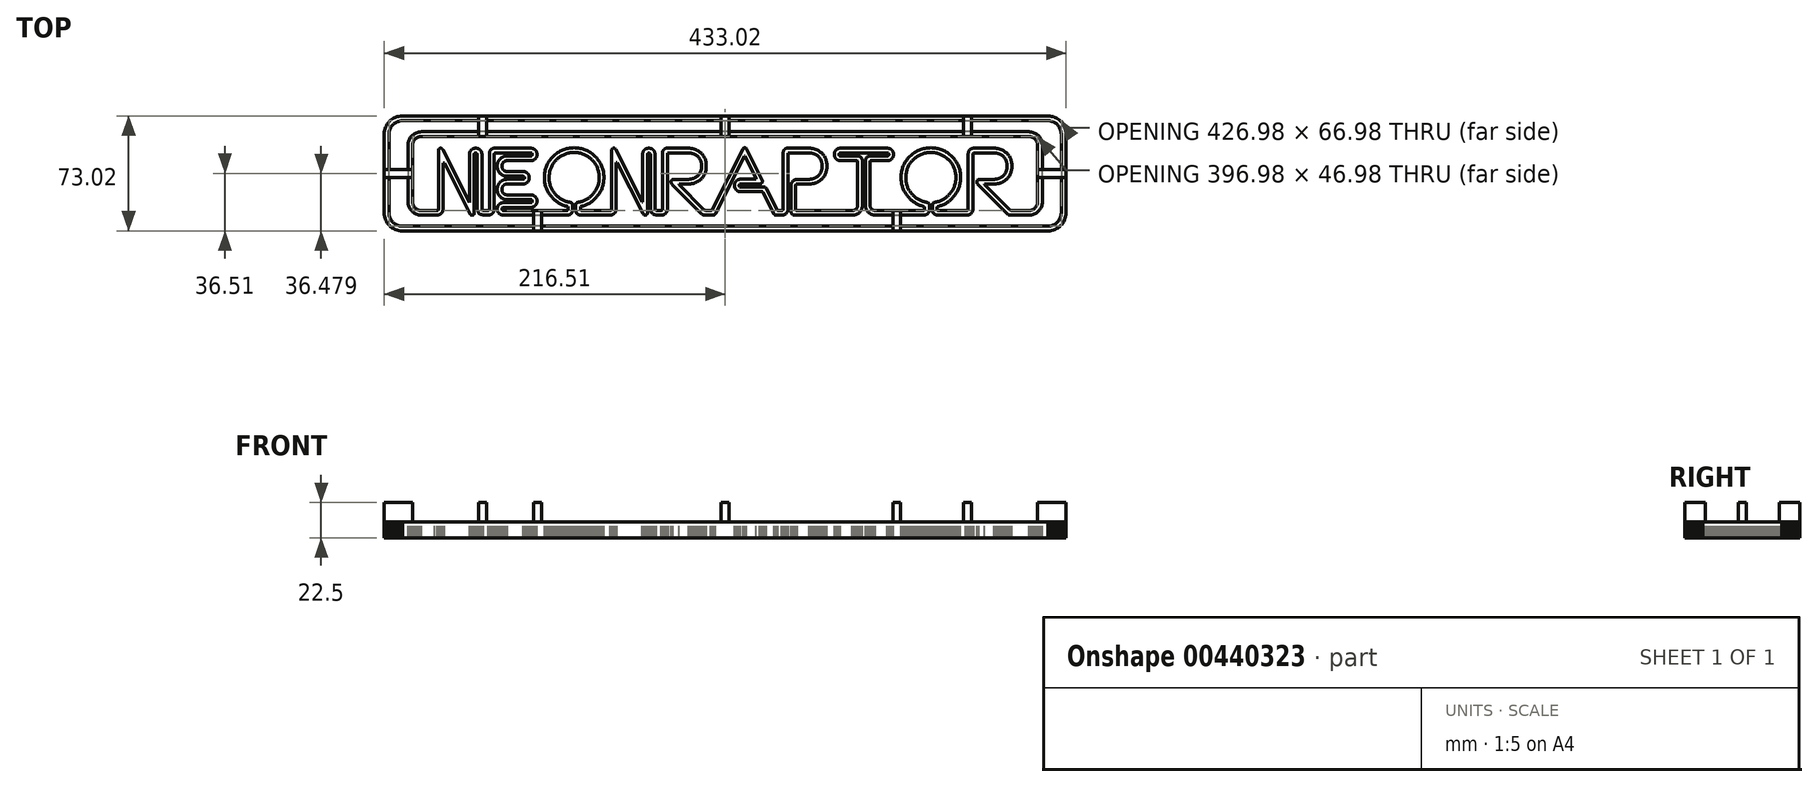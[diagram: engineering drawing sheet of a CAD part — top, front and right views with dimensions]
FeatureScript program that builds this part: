
annotation { "Feature Type Name" : "Feature", "Feature Type Description" : "" }
export const myFeature = defineFeature(function(context is Context, id is Id, definition is map)
    precondition{}
    {
        {
            var Q0;
            Q0=qCreatedBy(makeId("Top.planeOp"),FACE);
            var Q1;
            Q1=qCreatedBy(makeId("Top.planeOp"),FACE);
            var sketch = newSketch(context, id + "F0", { "sketchPlane" : qUnion([Q0, Q1])});
            skLineSegment(sketch, "E0", {"start": v(205, 36.51) * mm, "end": v(-205, 36.51) * mm});
            skLineSegment(sketch, "E1", {"start": v(-205, 36.51) * mm, "end": v(-206.18, 36.45) * mm});
            skLineSegment(sketch, "E2", {"start": v(-206.18, 36.45) * mm, "end": v(-207.32, 36.28) * mm});
            skLineSegment(sketch, "E3", {"start": v(-207.32, 36.28) * mm, "end": v(-208.42, 36) * mm});
            skLineSegment(sketch, "E4", {"start": v(-208.42, 36) * mm, "end": v(-209.48, 35.6) * mm});
            skLineSegment(sketch, "E5", {"start": v(-209.48, 35.6) * mm, "end": v(-210.48, 35.12) * mm});
            skLineSegment(sketch, "E6", {"start": v(-210.48, 35.12) * mm, "end": v(-211.43, 34.54) * mm});
            skLineSegment(sketch, "E7", {"start": v(-211.43, 34.54) * mm, "end": v(-212.32, 33.88) * mm});
            skLineSegment(sketch, "E8", {"start": v(-212.32, 33.88) * mm, "end": v(-213.14, 33.14) * mm});
            skLineSegment(sketch, "E9", {"start": v(-213.14, 33.14) * mm, "end": v(-213.88, 32.32) * mm});
            skLineSegment(sketch, "E10", {"start": v(-213.88, 32.32) * mm, "end": v(-214.54, 31.43) * mm});
            skLineSegment(sketch, "E11", {"start": v(-214.54, 31.43) * mm, "end": v(-215.12, 30.48) * mm});
            skLineSegment(sketch, "E12", {"start": v(-215.12, 30.48) * mm, "end": v(-215.6, 29.48) * mm});
            skLineSegment(sketch, "E13", {"start": v(-215.6, 29.48) * mm, "end": v(-216, 28.42) * mm});
            skLineSegment(sketch, "E14", {"start": v(-216, 28.42) * mm, "end": v(-216.28, 27.32) * mm});
            skLineSegment(sketch, "E15", {"start": v(-216.28, 27.32) * mm, "end": v(-216.45, 26.18) * mm});
            skLineSegment(sketch, "E16", {"start": v(-216.45, 26.18) * mm, "end": v(-216.51, 25) * mm});
            skLineSegment(sketch, "E17", {"start": v(-216.51, 25) * mm, "end": v(-216.51, -25) * mm});
            skLineSegment(sketch, "E18", {"start": v(-216.51, -25) * mm, "end": v(-216.45, -26.18) * mm});
            skLineSegment(sketch, "E19", {"start": v(-216.45, -26.18) * mm, "end": v(-216.28, -27.32) * mm});
            skLineSegment(sketch, "E20", {"start": v(-216.28, -27.32) * mm, "end": v(-216, -28.42) * mm});
            skLineSegment(sketch, "E21", {"start": v(-216, -28.42) * mm, "end": v(-215.6, -29.48) * mm});
            skLineSegment(sketch, "E22", {"start": v(-215.6, -29.48) * mm, "end": v(-215.12, -30.48) * mm});
            skLineSegment(sketch, "E23", {"start": v(-215.12, -30.48) * mm, "end": v(-214.54, -31.43) * mm});
            skLineSegment(sketch, "E24", {"start": v(-214.54, -31.43) * mm, "end": v(-213.88, -32.32) * mm});
            skLineSegment(sketch, "E25", {"start": v(-213.88, -32.32) * mm, "end": v(-213.14, -33.14) * mm});
            skLineSegment(sketch, "E26", {"start": v(-213.14, -33.14) * mm, "end": v(-212.32, -33.88) * mm});
            skLineSegment(sketch, "E27", {"start": v(-212.32, -33.88) * mm, "end": v(-211.43, -34.54) * mm});
            skLineSegment(sketch, "E28", {"start": v(-211.43, -34.54) * mm, "end": v(-210.48, -35.12) * mm});
            skLineSegment(sketch, "E29", {"start": v(-210.48, -35.12) * mm, "end": v(-209.48, -35.6) * mm});
            skLineSegment(sketch, "E30", {"start": v(-209.48, -35.6) * mm, "end": v(-208.42, -36) * mm});
            skLineSegment(sketch, "E31", {"start": v(-208.42, -36) * mm, "end": v(-207.32, -36.28) * mm});
            skLineSegment(sketch, "E32", {"start": v(-207.32, -36.28) * mm, "end": v(-206.18, -36.45) * mm});
            skLineSegment(sketch, "E33", {"start": v(-206.18, -36.45) * mm, "end": v(-205, -36.51) * mm});
            skLineSegment(sketch, "E34", {"start": v(-205, -36.51) * mm, "end": v(205, -36.51) * mm});
            skLineSegment(sketch, "E35", {"start": v(205, -36.51) * mm, "end": v(206.18, -36.45) * mm});
            skLineSegment(sketch, "E36", {"start": v(206.18, -36.45) * mm, "end": v(207.32, -36.28) * mm});
            skLineSegment(sketch, "E37", {"start": v(207.32, -36.28) * mm, "end": v(208.42, -36) * mm});
            skLineSegment(sketch, "E38", {"start": v(208.42, -36) * mm, "end": v(209.48, -35.6) * mm});
            skLineSegment(sketch, "E39", {"start": v(209.48, -35.6) * mm, "end": v(210.48, -35.12) * mm});
            skLineSegment(sketch, "E40", {"start": v(210.48, -35.12) * mm, "end": v(211.43, -34.54) * mm});
            skLineSegment(sketch, "E41", {"start": v(211.43, -34.54) * mm, "end": v(212.32, -33.88) * mm});
            skLineSegment(sketch, "E42", {"start": v(212.32, -33.88) * mm, "end": v(213.14, -33.14) * mm});
            skLineSegment(sketch, "E43", {"start": v(213.14, -33.14) * mm, "end": v(213.88, -32.32) * mm});
            skLineSegment(sketch, "E44", {"start": v(213.88, -32.32) * mm, "end": v(214.54, -31.43) * mm});
            skLineSegment(sketch, "E45", {"start": v(214.54, -31.43) * mm, "end": v(215.12, -30.48) * mm});
            skLineSegment(sketch, "E46", {"start": v(215.12, -30.48) * mm, "end": v(215.6, -29.48) * mm});
            skLineSegment(sketch, "E47", {"start": v(215.6, -29.48) * mm, "end": v(216, -28.42) * mm});
            skLineSegment(sketch, "E48", {"start": v(216, -28.42) * mm, "end": v(216.28, -27.32) * mm});
            skLineSegment(sketch, "E49", {"start": v(216.28, -27.32) * mm, "end": v(216.45, -26.18) * mm});
            skLineSegment(sketch, "E50", {"start": v(216.45, -26.18) * mm, "end": v(216.51, -25) * mm});
            skLineSegment(sketch, "E51", {"start": v(216.51, -25) * mm, "end": v(216.51, 25) * mm});
            skLineSegment(sketch, "E52", {"start": v(216.51, 25) * mm, "end": v(216.45, 26.18) * mm});
            skLineSegment(sketch, "E53", {"start": v(216.45, 26.18) * mm, "end": v(216.28, 27.32) * mm});
            skLineSegment(sketch, "E54", {"start": v(216.28, 27.32) * mm, "end": v(216, 28.42) * mm});
            skLineSegment(sketch, "E55", {"start": v(216, 28.42) * mm, "end": v(215.6, 29.48) * mm});
            skLineSegment(sketch, "E56", {"start": v(215.6, 29.48) * mm, "end": v(215.12, 30.48) * mm});
            skLineSegment(sketch, "E57", {"start": v(215.12, 30.48) * mm, "end": v(214.54, 31.43) * mm});
            skLineSegment(sketch, "E58", {"start": v(214.54, 31.43) * mm, "end": v(213.88, 32.32) * mm});
            skLineSegment(sketch, "E59", {"start": v(213.88, 32.32) * mm, "end": v(213.14, 33.14) * mm});
            skLineSegment(sketch, "E60", {"start": v(213.14, 33.14) * mm, "end": v(212.32, 33.88) * mm});
            skLineSegment(sketch, "E61", {"start": v(212.32, 33.88) * mm, "end": v(211.43, 34.54) * mm});
            skLineSegment(sketch, "E62", {"start": v(211.43, 34.54) * mm, "end": v(210.48, 35.12) * mm});
            skLineSegment(sketch, "E63", {"start": v(210.48, 35.12) * mm, "end": v(209.48, 35.6) * mm});
            skLineSegment(sketch, "E64", {"start": v(209.48, 35.6) * mm, "end": v(208.42, 36) * mm});
            skLineSegment(sketch, "E65", {"start": v(208.42, 36) * mm, "end": v(207.32, 36.28) * mm});
            skLineSegment(sketch, "E66", {"start": v(207.32, 36.28) * mm, "end": v(206.18, 36.45) * mm});
            skLineSegment(sketch, "E67", {"start": v(206.18, 36.45) * mm, "end": v(205, 36.51) * mm});
            skLineSegment(sketch, "E68", {"start": v(213.49, -25) * mm, "end": v(213.45, -25.87) * mm});
            skLineSegment(sketch, "E69", {"start": v(213.45, -25.87) * mm, "end": v(213.32, -26.7) * mm});
            skLineSegment(sketch, "E70", {"start": v(213.32, -26.7) * mm, "end": v(213.1, -27.52) * mm});
            skLineSegment(sketch, "E71", {"start": v(213.1, -27.52) * mm, "end": v(212.82, -28.3) * mm});
            skLineSegment(sketch, "E72", {"start": v(212.82, -28.3) * mm, "end": v(212.46, -29.04) * mm});
            skLineSegment(sketch, "E73", {"start": v(212.46, -29.04) * mm, "end": v(212.04, -29.74) * mm});
            skLineSegment(sketch, "E74", {"start": v(212.04, -29.74) * mm, "end": v(211.55, -30.4) * mm});
            skLineSegment(sketch, "E75", {"start": v(211.55, -30.4) * mm, "end": v(211, -31) * mm});
            skLineSegment(sketch, "E76", {"start": v(211, -31) * mm, "end": v(210.4, -31.55) * mm});
            skLineSegment(sketch, "E77", {"start": v(210.4, -31.55) * mm, "end": v(209.74, -32.04) * mm});
            skLineSegment(sketch, "E78", {"start": v(209.74, -32.04) * mm, "end": v(209.04, -32.46) * mm});
            skLineSegment(sketch, "E79", {"start": v(209.04, -32.46) * mm, "end": v(208.3, -32.82) * mm});
            skLineSegment(sketch, "E80", {"start": v(208.3, -32.82) * mm, "end": v(207.52, -33.1) * mm});
            skLineSegment(sketch, "E81", {"start": v(207.52, -33.1) * mm, "end": v(206.7, -33.32) * mm});
            skLineSegment(sketch, "E82", {"start": v(206.7, -33.32) * mm, "end": v(205.87, -33.45) * mm});
            skLineSegment(sketch, "E83", {"start": v(205.87, -33.45) * mm, "end": v(205, -33.49) * mm});
            skLineSegment(sketch, "E84", {"start": v(205, -33.49) * mm, "end": v(-205, -33.49) * mm});
            skLineSegment(sketch, "E85", {"start": v(-205, -33.49) * mm, "end": v(-205.87, -33.45) * mm});
            skLineSegment(sketch, "E86", {"start": v(-205.87, -33.45) * mm, "end": v(-206.7, -33.32) * mm});
            skLineSegment(sketch, "E87", {"start": v(-206.7, -33.32) * mm, "end": v(-207.52, -33.1) * mm});
            skLineSegment(sketch, "E88", {"start": v(-207.52, -33.1) * mm, "end": v(-208.3, -32.82) * mm});
            skLineSegment(sketch, "E89", {"start": v(-208.3, -32.82) * mm, "end": v(-209.04, -32.46) * mm});
            skLineSegment(sketch, "E90", {"start": v(-209.04, -32.46) * mm, "end": v(-209.74, -32.04) * mm});
            skLineSegment(sketch, "E91", {"start": v(-209.74, -32.04) * mm, "end": v(-210.4, -31.55) * mm});
            skLineSegment(sketch, "E92", {"start": v(-210.4, -31.55) * mm, "end": v(-211, -31) * mm});
            skLineSegment(sketch, "E93", {"start": v(-211, -31) * mm, "end": v(-211.55, -30.4) * mm});
            skLineSegment(sketch, "E94", {"start": v(-211.55, -30.4) * mm, "end": v(-212.04, -29.74) * mm});
            skLineSegment(sketch, "E95", {"start": v(-212.04, -29.74) * mm, "end": v(-212.46, -29.04) * mm});
            skLineSegment(sketch, "E96", {"start": v(-212.46, -29.04) * mm, "end": v(-212.82, -28.3) * mm});
            skLineSegment(sketch, "E97", {"start": v(-212.82, -28.3) * mm, "end": v(-213.1, -27.52) * mm});
            skLineSegment(sketch, "E98", {"start": v(-213.1, -27.52) * mm, "end": v(-213.32, -26.7) * mm});
            skLineSegment(sketch, "E99", {"start": v(-213.32, -26.7) * mm, "end": v(-213.44, -25.87) * mm});
            skLineSegment(sketch, "E100", {"start": v(-213.44, -25.87) * mm, "end": v(-213.49, -25) * mm});
            skLineSegment(sketch, "E101", {"start": v(-213.49, -25) * mm, "end": v(-213.49, 25) * mm});
            skLineSegment(sketch, "E102", {"start": v(-213.49, 25) * mm, "end": v(-213.44, 25.87) * mm});
            skLineSegment(sketch, "E103", {"start": v(-213.44, 25.87) * mm, "end": v(-213.32, 26.7) * mm});
            skLineSegment(sketch, "E104", {"start": v(-213.32, 26.7) * mm, "end": v(-213.1, 27.52) * mm});
            skLineSegment(sketch, "E105", {"start": v(-213.1, 27.52) * mm, "end": v(-212.82, 28.3) * mm});
            skLineSegment(sketch, "E106", {"start": v(-212.82, 28.3) * mm, "end": v(-212.46, 29.04) * mm});
            skLineSegment(sketch, "E107", {"start": v(-212.46, 29.04) * mm, "end": v(-212.04, 29.74) * mm});
            skLineSegment(sketch, "E108", {"start": v(-212.04, 29.74) * mm, "end": v(-211.55, 30.4) * mm});
            skLineSegment(sketch, "E109", {"start": v(-211.55, 30.4) * mm, "end": v(-211, 31) * mm});
            skLineSegment(sketch, "E110", {"start": v(-211, 31) * mm, "end": v(-210.4, 31.55) * mm});
            skLineSegment(sketch, "E111", {"start": v(-210.4, 31.55) * mm, "end": v(-209.74, 32.04) * mm});
            skLineSegment(sketch, "E112", {"start": v(-209.74, 32.04) * mm, "end": v(-209.04, 32.46) * mm});
            skLineSegment(sketch, "E113", {"start": v(-209.04, 32.46) * mm, "end": v(-208.3, 32.82) * mm});
            skLineSegment(sketch, "E114", {"start": v(-208.3, 32.82) * mm, "end": v(-207.52, 33.1) * mm});
            skLineSegment(sketch, "E115", {"start": v(-207.52, 33.1) * mm, "end": v(-206.7, 33.32) * mm});
            skLineSegment(sketch, "E116", {"start": v(-206.7, 33.32) * mm, "end": v(-205.87, 33.44) * mm});
            skLineSegment(sketch, "E117", {"start": v(-205.87, 33.44) * mm, "end": v(-205, 33.49) * mm});
            skLineSegment(sketch, "E118", {"start": v(-205, 33.49) * mm, "end": v(205, 33.49) * mm});
            skLineSegment(sketch, "E119", {"start": v(205, 33.49) * mm, "end": v(205.87, 33.44) * mm});
            skLineSegment(sketch, "E120", {"start": v(205.87, 33.44) * mm, "end": v(206.7, 33.32) * mm});
            skLineSegment(sketch, "E121", {"start": v(206.7, 33.32) * mm, "end": v(207.52, 33.1) * mm});
            skLineSegment(sketch, "E122", {"start": v(207.52, 33.1) * mm, "end": v(208.3, 32.82) * mm});
            skLineSegment(sketch, "E123", {"start": v(208.3, 32.82) * mm, "end": v(209.04, 32.46) * mm});
            skLineSegment(sketch, "E124", {"start": v(209.04, 32.46) * mm, "end": v(209.74, 32.04) * mm});
            skLineSegment(sketch, "E125", {"start": v(209.74, 32.04) * mm, "end": v(210.4, 31.55) * mm});
            skLineSegment(sketch, "E126", {"start": v(210.4, 31.55) * mm, "end": v(211, 31) * mm});
            skLineSegment(sketch, "E127", {"start": v(211, 31) * mm, "end": v(211.55, 30.4) * mm});
            skLineSegment(sketch, "E128", {"start": v(211.55, 30.4) * mm, "end": v(212.04, 29.74) * mm});
            skLineSegment(sketch, "E129", {"start": v(212.04, 29.74) * mm, "end": v(212.46, 29.04) * mm});
            skLineSegment(sketch, "E130", {"start": v(212.46, 29.04) * mm, "end": v(212.82, 28.3) * mm});
            skLineSegment(sketch, "E131", {"start": v(212.82, 28.3) * mm, "end": v(213.1, 27.52) * mm});
            skLineSegment(sketch, "E132", {"start": v(213.1, 27.52) * mm, "end": v(213.32, 26.7) * mm});
            skLineSegment(sketch, "E133", {"start": v(213.32, 26.7) * mm, "end": v(213.45, 25.87) * mm});
            skLineSegment(sketch, "E134", {"start": v(213.45, 25.87) * mm, "end": v(213.49, 25) * mm});
            skLineSegment(sketch, "E135", {"start": v(213.49, 25) * mm, "end": v(213.49, -25) * mm});
            skLineSegment(sketch, "E136", {"start": v(192.86, 26.48) * mm, "end": v(-192.86, 26.48) * mm});
            skLineSegment(sketch, "E137", {"start": v(-192.86, 26.48) * mm, "end": v(-193.74, 26.44) * mm});
            skLineSegment(sketch, "E138", {"start": v(-193.74, 26.44) * mm, "end": v(-194.6, 26.3) * mm});
            skLineSegment(sketch, "E139", {"start": v(-194.6, 26.3) * mm, "end": v(-195.43, 26.1) * mm});
            skLineSegment(sketch, "E140", {"start": v(-195.43, 26.1) * mm, "end": v(-196.22, 25.8) * mm});
            skLineSegment(sketch, "E141", {"start": v(-196.22, 25.8) * mm, "end": v(-196.98, 25.43) * mm});
            skLineSegment(sketch, "E142", {"start": v(-196.98, 25.43) * mm, "end": v(-197.7, 25) * mm});
            skLineSegment(sketch, "E143", {"start": v(-197.7, 25) * mm, "end": v(-198.36, 24.5) * mm});
            skLineSegment(sketch, "E144", {"start": v(-198.36, 24.5) * mm, "end": v(-198.97, 23.94) * mm});
            skLineSegment(sketch, "E145", {"start": v(-198.97, 23.94) * mm, "end": v(-199.53, 23.33) * mm});
            skLineSegment(sketch, "E146", {"start": v(-199.53, 23.33) * mm, "end": v(-200.03, 22.66) * mm});
            skLineSegment(sketch, "E147", {"start": v(-200.03, 22.66) * mm, "end": v(-200.46, 21.95) * mm});
            skLineSegment(sketch, "E148", {"start": v(-200.46, 21.95) * mm, "end": v(-200.83, 21.2) * mm});
            skLineSegment(sketch, "E149", {"start": v(-200.83, 21.2) * mm, "end": v(-201.12, 20.4) * mm});
            skLineSegment(sketch, "E150", {"start": v(-201.12, 20.4) * mm, "end": v(-201.33, 19.57) * mm});
            skLineSegment(sketch, "E151", {"start": v(-201.33, 19.57) * mm, "end": v(-201.47, 18.7) * mm});
            skLineSegment(sketch, "E152", {"start": v(-201.47, 18.7) * mm, "end": v(-201.51, 17.82) * mm});
            skLineSegment(sketch, "E153", {"start": v(-201.51, 17.82) * mm, "end": v(-201.51, -17.89) * mm});
            skLineSegment(sketch, "E154", {"start": v(-201.51, -17.89) * mm, "end": v(-201.47, -18.77) * mm});
            skLineSegment(sketch, "E155", {"start": v(-201.47, -18.77) * mm, "end": v(-201.33, -19.63) * mm});
            skLineSegment(sketch, "E156", {"start": v(-201.33, -19.63) * mm, "end": v(-201.12, -20.46) * mm});
            skLineSegment(sketch, "E157", {"start": v(-201.12, -20.46) * mm, "end": v(-200.83, -21.25) * mm});
            skLineSegment(sketch, "E158", {"start": v(-200.83, -21.25) * mm, "end": v(-200.46, -22) * mm});
            skLineSegment(sketch, "E159", {"start": v(-200.46, -22) * mm, "end": v(-200.03, -22.72) * mm});
            skLineSegment(sketch, "E160", {"start": v(-200.03, -22.72) * mm, "end": v(-199.53, -23.39) * mm});
            skLineSegment(sketch, "E161", {"start": v(-199.53, -23.39) * mm, "end": v(-198.97, -24) * mm});
            skLineSegment(sketch, "E162", {"start": v(-198.97, -24) * mm, "end": v(-198.36, -24.56) * mm});
            skLineSegment(sketch, "E163", {"start": v(-198.36, -24.56) * mm, "end": v(-197.7, -25.06) * mm});
            skLineSegment(sketch, "E164", {"start": v(-197.7, -25.06) * mm, "end": v(-196.98, -25.5) * mm});
            skLineSegment(sketch, "E165", {"start": v(-196.98, -25.5) * mm, "end": v(-196.22, -25.86) * mm});
            skLineSegment(sketch, "E166", {"start": v(-196.22, -25.86) * mm, "end": v(-195.43, -26.15) * mm});
            skLineSegment(sketch, "E167", {"start": v(-195.43, -26.15) * mm, "end": v(-194.6, -26.37) * mm});
            skLineSegment(sketch, "E168", {"start": v(-194.6, -26.37) * mm, "end": v(-193.74, -26.5) * mm});
            skLineSegment(sketch, "E169", {"start": v(-193.74, -26.5) * mm, "end": v(-192.86, -26.54) * mm});
            skLineSegment(sketch, "E170", {"start": v(-192.86, -26.54) * mm, "end": v(-184.5, -26.54) * mm});
            skLineSegment(sketch, "E171", {"start": v(-184.5, -26.54) * mm, "end": v(-184.4, -26.44) * mm});
            skLineSegment(sketch, "E172", {"start": v(-184.4, -26.44) * mm, "end": v(-184.4, -26.44) * mm});
            skLineSegment(sketch, "E173", {"start": v(-184.4, -26.44) * mm, "end": v(-183.06, -26.44) * mm});
            skLineSegment(sketch, "E174", {"start": v(-183.06, -26.44) * mm, "end": v(-182.85, -26.43) * mm});
            skLineSegment(sketch, "E175", {"start": v(-182.85, -26.43) * mm, "end": v(-182.64, -26.42) * mm});
            skLineSegment(sketch, "E176", {"start": v(-182.64, -26.42) * mm, "end": v(-182.44, -26.4) * mm});
            skLineSegment(sketch, "E177", {"start": v(-182.44, -26.4) * mm, "end": v(-182.24, -26.37) * mm});
            skLineSegment(sketch, "E178", {"start": v(-182.24, -26.37) * mm, "end": v(-182.04, -26.33) * mm});
            skLineSegment(sketch, "E179", {"start": v(-182.04, -26.33) * mm, "end": v(-181.85, -26.28) * mm});
            skLineSegment(sketch, "E180", {"start": v(-181.85, -26.28) * mm, "end": v(-181.67, -26.22) * mm});
            skLineSegment(sketch, "E181", {"start": v(-181.67, -26.22) * mm, "end": v(-181.5, -26.16) * mm});
            skLineSegment(sketch, "E182", {"start": v(-181.5, -26.16) * mm, "end": v(-181.32, -26.08) * mm});
            skLineSegment(sketch, "E183", {"start": v(-181.32, -26.08) * mm, "end": v(-181.15, -26) * mm});
            skLineSegment(sketch, "E184", {"start": v(-181.15, -26) * mm, "end": v(-180.98, -25.9) * mm});
            skLineSegment(sketch, "E185", {"start": v(-180.98, -25.9) * mm, "end": v(-180.82, -25.8) * mm});
            skLineSegment(sketch, "E186", {"start": v(-180.82, -25.8) * mm, "end": v(-180.67, -25.7) * mm});
            skLineSegment(sketch, "E187", {"start": v(-180.67, -25.7) * mm, "end": v(-180.52, -25.58) * mm});
            skLineSegment(sketch, "E188", {"start": v(-180.52, -25.58) * mm, "end": v(-180.38, -25.46) * mm});
            skLineSegment(sketch, "E189", {"start": v(-180.38, -25.46) * mm, "end": v(-180.24, -25.32) * mm});
            skLineSegment(sketch, "E190", {"start": v(-180.24, -25.32) * mm, "end": v(-180.1, -25.18) * mm});
            skLineSegment(sketch, "E191", {"start": v(-180.1, -25.18) * mm, "end": v(-179.99, -25.03) * mm});
            skLineSegment(sketch, "E192", {"start": v(-179.99, -25.03) * mm, "end": v(-179.87, -24.88) * mm});
            skLineSegment(sketch, "E193", {"start": v(-179.87, -24.88) * mm, "end": v(-179.77, -24.73) * mm});
            skLineSegment(sketch, "E194", {"start": v(-179.77, -24.73) * mm, "end": v(-179.67, -24.56) * mm});
            skLineSegment(sketch, "E195", {"start": v(-179.67, -24.56) * mm, "end": v(-179.58, -24.4) * mm});
            skLineSegment(sketch, "E196", {"start": v(-179.58, -24.4) * mm, "end": v(-179.5, -24.23) * mm});
            skLineSegment(sketch, "E197", {"start": v(-179.5, -24.23) * mm, "end": v(-179.43, -24.05) * mm});
            skLineSegment(sketch, "E198", {"start": v(-179.43, -24.05) * mm, "end": v(-179.36, -23.87) * mm});
            skLineSegment(sketch, "E199", {"start": v(-179.36, -23.87) * mm, "end": v(-179.3, -23.68) * mm});
            skLineSegment(sketch, "E200", {"start": v(-179.3, -23.68) * mm, "end": v(-179.26, -23.5) * mm});
            skLineSegment(sketch, "E201", {"start": v(-179.26, -23.5) * mm, "end": v(-179.22, -23.3) * mm});
            skLineSegment(sketch, "E202", {"start": v(-179.22, -23.3) * mm, "end": v(-179.2, -23.1) * mm});
            skLineSegment(sketch, "E203", {"start": v(-179.2, -23.1) * mm, "end": v(-179.17, -22.9) * mm});
            skLineSegment(sketch, "E204", {"start": v(-179.17, -22.9) * mm, "end": v(-179.16, -22.69) * mm});
            skLineSegment(sketch, "E205", {"start": v(-179.16, -22.69) * mm, "end": v(-179.15, -22.47) * mm});
            skLineSegment(sketch, "E206", {"start": v(-179.15, -22.47) * mm, "end": v(-179.15, 6.31) * mm});
            skLineSegment(sketch, "E207", {"start": v(-179.15, 6.31) * mm, "end": v(-179.15, 6.36) * mm});
            skLineSegment(sketch, "E208", {"start": v(-179.15, 6.36) * mm, "end": v(-179.14, 6.41) * mm});
            skLineSegment(sketch, "E209", {"start": v(-179.14, 6.41) * mm, "end": v(-179.13, 6.46) * mm});
            skLineSegment(sketch, "E210", {"start": v(-179.13, 6.46) * mm, "end": v(-179.11, 6.5) * mm});
            skLineSegment(sketch, "E211", {"start": v(-179.11, 6.5) * mm, "end": v(-179.1, 6.54) * mm});
            skLineSegment(sketch, "E212", {"start": v(-179.1, 6.54) * mm, "end": v(-179.07, 6.58) * mm});
            skLineSegment(sketch, "E213", {"start": v(-179.07, 6.58) * mm, "end": v(-179.04, 6.6) * mm});
            skLineSegment(sketch, "E214", {"start": v(-179.04, 6.6) * mm, "end": v(-179.01, 6.64) * mm});
            skLineSegment(sketch, "E215", {"start": v(-179.01, 6.64) * mm, "end": v(-178.98, 6.67) * mm});
            skLineSegment(sketch, "E216", {"start": v(-178.98, 6.67) * mm, "end": v(-178.94, 6.69) * mm});
            skLineSegment(sketch, "E217", {"start": v(-178.94, 6.69) * mm, "end": v(-178.9, 6.7) * mm});
            skLineSegment(sketch, "E218", {"start": v(-178.9, 6.7) * mm, "end": v(-178.87, 6.72) * mm});
            skLineSegment(sketch, "E219", {"start": v(-178.87, 6.72) * mm, "end": v(-178.83, 6.74) * mm});
            skLineSegment(sketch, "E220", {"start": v(-178.83, 6.74) * mm, "end": v(-178.79, 6.75) * mm});
            skLineSegment(sketch, "E221", {"start": v(-178.79, 6.75) * mm, "end": v(-178.75, 6.75) * mm});
            skLineSegment(sketch, "E222", {"start": v(-178.75, 6.75) * mm, "end": v(-178.7, 6.75) * mm});
            skLineSegment(sketch, "E223", {"start": v(-178.7, 6.75) * mm, "end": v(-178.67, 6.75) * mm});
            skLineSegment(sketch, "E224", {"start": v(-178.67, 6.75) * mm, "end": v(-178.64, 6.75) * mm});
            skLineSegment(sketch, "E225", {"start": v(-178.64, 6.75) * mm, "end": v(-178.61, 6.74) * mm});
            skLineSegment(sketch, "E226", {"start": v(-178.61, 6.74) * mm, "end": v(-178.58, 6.74) * mm});
            skLineSegment(sketch, "E227", {"start": v(-178.58, 6.74) * mm, "end": v(-178.56, 6.73) * mm});
            skLineSegment(sketch, "E228", {"start": v(-178.56, 6.73) * mm, "end": v(-178.53, 6.72) * mm});
            skLineSegment(sketch, "E229", {"start": v(-178.53, 6.72) * mm, "end": v(-178.5, 6.7) * mm});
            skLineSegment(sketch, "E230", {"start": v(-178.5, 6.7) * mm, "end": v(-178.48, 6.69) * mm});
            skLineSegment(sketch, "E231", {"start": v(-178.48, 6.69) * mm, "end": v(-178.45, 6.67) * mm});
            skLineSegment(sketch, "E232", {"start": v(-178.45, 6.67) * mm, "end": v(-178.43, 6.65) * mm});
            skLineSegment(sketch, "E233", {"start": v(-178.43, 6.65) * mm, "end": v(-178.4, 6.63) * mm});
            skLineSegment(sketch, "E234", {"start": v(-178.4, 6.63) * mm, "end": v(-178.39, 6.61) * mm});
            skLineSegment(sketch, "E235", {"start": v(-178.39, 6.61) * mm, "end": v(-178.37, 6.59) * mm});
            skLineSegment(sketch, "E236", {"start": v(-178.37, 6.59) * mm, "end": v(-178.35, 6.56) * mm});
            skLineSegment(sketch, "E237", {"start": v(-178.35, 6.56) * mm, "end": v(-178.33, 6.54) * mm});
            skLineSegment(sketch, "E238", {"start": v(-178.33, 6.54) * mm, "end": v(-178.32, 6.5) * mm});
            skLineSegment(sketch, "E239", {"start": v(-178.32, 6.5) * mm, "end": v(-162.07, -25.76) * mm});
            skLineSegment(sketch, "E240", {"start": v(-162.07, -25.76) * mm, "end": v(-162.03, -25.83) * mm});
            skLineSegment(sketch, "E241", {"start": v(-162.03, -25.83) * mm, "end": v(-161.98, -25.9) * mm});
            skLineSegment(sketch, "E242", {"start": v(-161.98, -25.9) * mm, "end": v(-161.92, -25.98) * mm});
            skLineSegment(sketch, "E243", {"start": v(-161.92, -25.98) * mm, "end": v(-161.86, -26.04) * mm});
            skLineSegment(sketch, "E244", {"start": v(-161.86, -26.04) * mm, "end": v(-161.8, -26.1) * mm});
            skLineSegment(sketch, "E245", {"start": v(-161.8, -26.1) * mm, "end": v(-161.72, -26.17) * mm});
            skLineSegment(sketch, "E246", {"start": v(-161.72, -26.17) * mm, "end": v(-161.65, -26.22) * mm});
            skLineSegment(sketch, "E247", {"start": v(-161.65, -26.22) * mm, "end": v(-161.57, -26.27) * mm});
            skLineSegment(sketch, "E248", {"start": v(-161.57, -26.27) * mm, "end": v(-161.49, -26.32) * mm});
            skLineSegment(sketch, "E249", {"start": v(-161.49, -26.32) * mm, "end": v(-161.4, -26.36) * mm});
            skLineSegment(sketch, "E250", {"start": v(-161.4, -26.36) * mm, "end": v(-161.32, -26.4) * mm});
            skLineSegment(sketch, "E251", {"start": v(-161.32, -26.4) * mm, "end": v(-161.23, -26.43) * mm});
            skLineSegment(sketch, "E252", {"start": v(-161.23, -26.43) * mm, "end": v(-161.14, -26.46) * mm});
            skLineSegment(sketch, "E253", {"start": v(-161.14, -26.46) * mm, "end": v(-161.05, -26.47) * mm});
            skLineSegment(sketch, "E254", {"start": v(-161.05, -26.47) * mm, "end": v(-160.97, -26.48) * mm});
            skLineSegment(sketch, "E255", {"start": v(-160.97, -26.48) * mm, "end": v(-160.88, -26.49) * mm});
            skLineSegment(sketch, "E256", {"start": v(-160.88, -26.49) * mm, "end": v(-160.61, -26.49) * mm});
            skLineSegment(sketch, "E257", {"start": v(-160.61, -26.49) * mm, "end": v(-160.49, -26.48) * mm});
            skLineSegment(sketch, "E258", {"start": v(-160.49, -26.48) * mm, "end": v(-160.36, -26.46) * mm});
            skLineSegment(sketch, "E259", {"start": v(-160.36, -26.46) * mm, "end": v(-160.24, -26.43) * mm});
            skLineSegment(sketch, "E260", {"start": v(-160.24, -26.43) * mm, "end": v(-160.13, -26.4) * mm});
            skLineSegment(sketch, "E261", {"start": v(-160.13, -26.4) * mm, "end": v(-160.02, -26.34) * mm});
            skLineSegment(sketch, "E262", {"start": v(-160.02, -26.34) * mm, "end": v(-159.91, -26.27) * mm});
            skLineSegment(sketch, "E263", {"start": v(-159.91, -26.27) * mm, "end": v(-159.82, -26.2) * mm});
            skLineSegment(sketch, "E264", {"start": v(-159.82, -26.2) * mm, "end": v(-159.73, -26.12) * mm});
            skLineSegment(sketch, "E265", {"start": v(-159.73, -26.12) * mm, "end": v(-159.65, -26.03) * mm});
            skLineSegment(sketch, "E266", {"start": v(-159.65, -26.03) * mm, "end": v(-159.58, -25.94) * mm});
            skLineSegment(sketch, "E267", {"start": v(-159.58, -25.94) * mm, "end": v(-159.51, -25.83) * mm});
            skLineSegment(sketch, "E268", {"start": v(-159.51, -25.83) * mm, "end": v(-159.46, -25.72) * mm});
            skLineSegment(sketch, "E269", {"start": v(-159.46, -25.72) * mm, "end": v(-159.42, -25.61) * mm});
            skLineSegment(sketch, "E270", {"start": v(-159.42, -25.61) * mm, "end": v(-159.39, -25.5) * mm});
            skLineSegment(sketch, "E271", {"start": v(-159.39, -25.5) * mm, "end": v(-159.37, -25.37) * mm});
            skLineSegment(sketch, "E272", {"start": v(-159.37, -25.37) * mm, "end": v(-159.36, -25.24) * mm});
            skLineSegment(sketch, "E273", {"start": v(-159.36, -25.24) * mm, "end": v(-159.36, 11.98) * mm});
            skLineSegment(sketch, "E274", {"start": v(-159.36, 11.98) * mm, "end": v(-159.36, 12.1) * mm});
            skLineSegment(sketch, "E275", {"start": v(-159.36, 12.1) * mm, "end": v(-159.35, 12.22) * mm});
            skLineSegment(sketch, "E276", {"start": v(-159.35, 12.22) * mm, "end": v(-159.33, 12.33) * mm});
            skLineSegment(sketch, "E277", {"start": v(-159.33, 12.33) * mm, "end": v(-159.3, 12.43) * mm});
            skLineSegment(sketch, "E278", {"start": v(-159.3, 12.43) * mm, "end": v(-159.27, 12.52) * mm});
            skLineSegment(sketch, "E279", {"start": v(-159.27, 12.52) * mm, "end": v(-159.24, 12.6) * mm});
            skLineSegment(sketch, "E280", {"start": v(-159.24, 12.6) * mm, "end": v(-159.19, 12.67) * mm});
            skLineSegment(sketch, "E281", {"start": v(-159.19, 12.67) * mm, "end": v(-159.14, 12.74) * mm});
            skLineSegment(sketch, "E282", {"start": v(-159.14, 12.74) * mm, "end": v(-159.07, 12.8) * mm});
            skLineSegment(sketch, "E283", {"start": v(-159.07, 12.8) * mm, "end": v(-159, 12.85) * mm});
            skLineSegment(sketch, "E284", {"start": v(-159, 12.85) * mm, "end": v(-158.93, 12.9) * mm});
            skLineSegment(sketch, "E285", {"start": v(-158.93, 12.9) * mm, "end": v(-158.84, 12.93) * mm});
            skLineSegment(sketch, "E286", {"start": v(-158.84, 12.93) * mm, "end": v(-158.75, 12.95) * mm});
            skLineSegment(sketch, "E287", {"start": v(-158.75, 12.95) * mm, "end": v(-158.65, 12.97) * mm});
            skLineSegment(sketch, "E288", {"start": v(-158.65, 12.97) * mm, "end": v(-158.55, 12.98) * mm});
            skLineSegment(sketch, "E289", {"start": v(-158.55, 12.98) * mm, "end": v(-158.43, 12.99) * mm});
            skLineSegment(sketch, "E290", {"start": v(-158.43, 12.99) * mm, "end": v(-158.3, 12.98) * mm});
            skLineSegment(sketch, "E291", {"start": v(-158.3, 12.98) * mm, "end": v(-158.2, 12.97) * mm});
            skLineSegment(sketch, "E292", {"start": v(-158.2, 12.97) * mm, "end": v(-158.09, 12.95) * mm});
            skLineSegment(sketch, "E293", {"start": v(-158.09, 12.95) * mm, "end": v(-158, 12.93) * mm});
            skLineSegment(sketch, "E294", {"start": v(-158, 12.93) * mm, "end": v(-157.9, 12.9) * mm});
            skLineSegment(sketch, "E295", {"start": v(-157.9, 12.9) * mm, "end": v(-157.82, 12.85) * mm});
            skLineSegment(sketch, "E296", {"start": v(-157.82, 12.85) * mm, "end": v(-157.75, 12.8) * mm});
            skLineSegment(sketch, "E297", {"start": v(-157.75, 12.8) * mm, "end": v(-157.69, 12.74) * mm});
            skLineSegment(sketch, "E298", {"start": v(-157.69, 12.74) * mm, "end": v(-157.63, 12.67) * mm});
            skLineSegment(sketch, "E299", {"start": v(-157.63, 12.67) * mm, "end": v(-157.58, 12.6) * mm});
            skLineSegment(sketch, "E300", {"start": v(-157.58, 12.6) * mm, "end": v(-157.54, 12.52) * mm});
            skLineSegment(sketch, "E301", {"start": v(-157.54, 12.52) * mm, "end": v(-157.5, 12.43) * mm});
            skLineSegment(sketch, "E302", {"start": v(-157.5, 12.43) * mm, "end": v(-157.48, 12.33) * mm});
            skLineSegment(sketch, "E303", {"start": v(-157.48, 12.33) * mm, "end": v(-157.46, 12.22) * mm});
            skLineSegment(sketch, "E304", {"start": v(-157.46, 12.22) * mm, "end": v(-157.45, 12.1) * mm});
            skLineSegment(sketch, "E305", {"start": v(-157.45, 12.1) * mm, "end": v(-157.45, 11.98) * mm});
            skLineSegment(sketch, "E306", {"start": v(-157.45, 11.98) * mm, "end": v(-157.45, -22.43) * mm});
            skLineSegment(sketch, "E307", {"start": v(-157.45, -22.43) * mm, "end": v(-157.43, -22.85) * mm});
            skLineSegment(sketch, "E308", {"start": v(-157.43, -22.85) * mm, "end": v(-157.38, -23.26) * mm});
            skLineSegment(sketch, "E309", {"start": v(-157.38, -23.26) * mm, "end": v(-157.3, -23.63) * mm});
            skLineSegment(sketch, "E310", {"start": v(-157.3, -23.63) * mm, "end": v(-157.2, -24) * mm});
            skLineSegment(sketch, "E311", {"start": v(-157.2, -24) * mm, "end": v(-157.06, -24.32) * mm});
            skLineSegment(sketch, "E312", {"start": v(-157.06, -24.32) * mm, "end": v(-156.9, -24.63) * mm});
            skLineSegment(sketch, "E313", {"start": v(-156.9, -24.63) * mm, "end": v(-156.7, -24.91) * mm});
            skLineSegment(sketch, "E314", {"start": v(-156.7, -24.91) * mm, "end": v(-156.46, -25.17) * mm});
            skLineSegment(sketch, "E315", {"start": v(-156.46, -25.17) * mm, "end": v(-156.2, -25.4) * mm});
            skLineSegment(sketch, "E316", {"start": v(-156.2, -25.4) * mm, "end": v(-155.91, -25.62) * mm});
            skLineSegment(sketch, "E317", {"start": v(-155.91, -25.62) * mm, "end": v(-155.6, -25.8) * mm});
            skLineSegment(sketch, "E318", {"start": v(-155.6, -25.8) * mm, "end": v(-155.24, -25.97) * mm});
            skLineSegment(sketch, "E319", {"start": v(-155.24, -25.97) * mm, "end": v(-154.86, -26.11) * mm});
            skLineSegment(sketch, "E320", {"start": v(-154.86, -26.11) * mm, "end": v(-154.45, -26.23) * mm});
            skLineSegment(sketch, "E321", {"start": v(-154.45, -26.23) * mm, "end": v(-154, -26.32) * mm});
            skLineSegment(sketch, "E322", {"start": v(-154, -26.32) * mm, "end": v(-153.53, -26.38) * mm});
            skLineSegment(sketch, "E323", {"start": v(-153.53, -26.38) * mm, "end": v(-150.63, -26.49) * mm});
            skLineSegment(sketch, "E324", {"start": v(-150.63, -26.49) * mm, "end": v(-150.41, -26.48) * mm});
            skLineSegment(sketch, "E325", {"start": v(-150.41, -26.48) * mm, "end": v(-150.2, -26.47) * mm});
            skLineSegment(sketch, "E326", {"start": v(-150.2, -26.47) * mm, "end": v(-150, -26.45) * mm});
            skLineSegment(sketch, "E327", {"start": v(-150, -26.45) * mm, "end": v(-149.8, -26.42) * mm});
            skLineSegment(sketch, "E328", {"start": v(-149.8, -26.42) * mm, "end": v(-149.6, -26.38) * mm});
            skLineSegment(sketch, "E329", {"start": v(-149.6, -26.38) * mm, "end": v(-149.41, -26.33) * mm});
            skLineSegment(sketch, "E330", {"start": v(-149.41, -26.33) * mm, "end": v(-149.23, -26.27) * mm});
            skLineSegment(sketch, "E331", {"start": v(-149.23, -26.27) * mm, "end": v(-149.05, -26.2) * mm});
            skLineSegment(sketch, "E332", {"start": v(-149.05, -26.2) * mm, "end": v(-148.87, -26.13) * mm});
            skLineSegment(sketch, "E333", {"start": v(-148.87, -26.13) * mm, "end": v(-148.7, -26.05) * mm});
            skLineSegment(sketch, "E334", {"start": v(-148.7, -26.05) * mm, "end": v(-148.53, -25.96) * mm});
            skLineSegment(sketch, "E335", {"start": v(-148.53, -25.96) * mm, "end": v(-148.37, -25.86) * mm});
            skLineSegment(sketch, "E336", {"start": v(-148.37, -25.86) * mm, "end": v(-148.22, -25.75) * mm});
            skLineSegment(sketch, "E337", {"start": v(-148.22, -25.75) * mm, "end": v(-148.06, -25.63) * mm});
            skLineSegment(sketch, "E338", {"start": v(-148.06, -25.63) * mm, "end": v(-147.92, -25.5) * mm});
            skLineSegment(sketch, "E339", {"start": v(-147.92, -25.5) * mm, "end": v(-147.78, -25.37) * mm});
            skLineSegment(sketch, "E340", {"start": v(-147.78, -25.37) * mm, "end": v(-147.64, -25.23) * mm});
            skLineSegment(sketch, "E341", {"start": v(-147.64, -25.23) * mm, "end": v(-147.52, -25.09) * mm});
            skLineSegment(sketch, "E342", {"start": v(-147.52, -25.09) * mm, "end": v(-147.4, -24.94) * mm});
            skLineSegment(sketch, "E343", {"start": v(-147.4, -24.94) * mm, "end": v(-147.3, -24.78) * mm});
            skLineSegment(sketch, "E344", {"start": v(-147.3, -24.78) * mm, "end": v(-147.2, -24.62) * mm});
            skLineSegment(sketch, "E345", {"start": v(-147.2, -24.62) * mm, "end": v(-147.1, -24.45) * mm});
            skLineSegment(sketch, "E346", {"start": v(-147.1, -24.45) * mm, "end": v(-147.02, -24.28) * mm});
            skLineSegment(sketch, "E347", {"start": v(-147.02, -24.28) * mm, "end": v(-146.94, -24.1) * mm});
            skLineSegment(sketch, "E348", {"start": v(-146.94, -24.1) * mm, "end": v(-146.88, -23.92) * mm});
            skLineSegment(sketch, "E349", {"start": v(-146.88, -23.92) * mm, "end": v(-146.82, -23.74) * mm});
            skLineSegment(sketch, "E350", {"start": v(-146.82, -23.74) * mm, "end": v(-146.77, -23.55) * mm});
            skLineSegment(sketch, "E351", {"start": v(-146.77, -23.55) * mm, "end": v(-146.73, -23.35) * mm});
            skLineSegment(sketch, "E352", {"start": v(-146.73, -23.35) * mm, "end": v(-146.7, -23.15) * mm});
            skLineSegment(sketch, "E353", {"start": v(-146.7, -23.15) * mm, "end": v(-146.68, -22.95) * mm});
            skLineSegment(sketch, "E354", {"start": v(-146.68, -22.95) * mm, "end": v(-146.67, -22.74) * mm});
            skLineSegment(sketch, "E355", {"start": v(-146.67, -22.74) * mm, "end": v(-146.66, -22.53) * mm});
            skLineSegment(sketch, "E356", {"start": v(-146.66, -22.53) * mm, "end": v(-146.66, 12.15) * mm});
            skLineSegment(sketch, "E357", {"start": v(-146.66, 12.15) * mm, "end": v(-146.66, 12.24) * mm});
            skLineSegment(sketch, "E358", {"start": v(-146.66, 12.24) * mm, "end": v(-146.65, 12.33) * mm});
            skLineSegment(sketch, "E359", {"start": v(-146.65, 12.33) * mm, "end": v(-146.62, 12.42) * mm});
            skLineSegment(sketch, "E360", {"start": v(-146.62, 12.42) * mm, "end": v(-146.6, 12.5) * mm});
            skLineSegment(sketch, "E361", {"start": v(-146.6, 12.5) * mm, "end": v(-146.56, 12.58) * mm});
            skLineSegment(sketch, "E362", {"start": v(-146.56, 12.58) * mm, "end": v(-146.51, 12.65) * mm});
            skLineSegment(sketch, "E363", {"start": v(-146.51, 12.65) * mm, "end": v(-146.46, 12.72) * mm});
            skLineSegment(sketch, "E364", {"start": v(-146.46, 12.72) * mm, "end": v(-146.4, 12.78) * mm});
            skLineSegment(sketch, "E365", {"start": v(-146.4, 12.78) * mm, "end": v(-146.34, 12.84) * mm});
            skLineSegment(sketch, "E366", {"start": v(-146.34, 12.84) * mm, "end": v(-146.27, 12.89) * mm});
            skLineSegment(sketch, "E367", {"start": v(-146.27, 12.89) * mm, "end": v(-146.2, 12.93) * mm});
            skLineSegment(sketch, "E368", {"start": v(-146.2, 12.93) * mm, "end": v(-146.12, 12.97) * mm});
            skLineSegment(sketch, "E369", {"start": v(-146.12, 12.97) * mm, "end": v(-146.04, 13) * mm});
            skLineSegment(sketch, "E370", {"start": v(-146.04, 13) * mm, "end": v(-145.96, 13.02) * mm});
            skLineSegment(sketch, "E371", {"start": v(-145.96, 13.02) * mm, "end": v(-145.87, 13.04) * mm});
            skLineSegment(sketch, "E372", {"start": v(-145.87, 13.04) * mm, "end": v(-145.78, 13.04) * mm});
            skLineSegment(sketch, "E373", {"start": v(-145.78, 13.04) * mm, "end": v(-123.48, 13.04) * mm});
            skLineSegment(sketch, "E374", {"start": v(-123.48, 13.04) * mm, "end": v(-123.35, 13.04) * mm});
            skLineSegment(sketch, "E375", {"start": v(-123.35, 13.04) * mm, "end": v(-123.24, 13.03) * mm});
            skLineSegment(sketch, "E376", {"start": v(-123.24, 13.03) * mm, "end": v(-123.13, 13) * mm});
            skLineSegment(sketch, "E377", {"start": v(-123.13, 13) * mm, "end": v(-123.03, 12.98) * mm});
            skLineSegment(sketch, "E378", {"start": v(-123.03, 12.98) * mm, "end": v(-122.94, 12.95) * mm});
            skLineSegment(sketch, "E379", {"start": v(-122.94, 12.95) * mm, "end": v(-122.86, 12.9) * mm});
            skLineSegment(sketch, "E380", {"start": v(-122.86, 12.9) * mm, "end": v(-122.78, 12.86) * mm});
            skLineSegment(sketch, "E381", {"start": v(-122.78, 12.86) * mm, "end": v(-122.72, 12.8) * mm});
            skLineSegment(sketch, "E382", {"start": v(-122.72, 12.8) * mm, "end": v(-122.66, 12.74) * mm});
            skLineSegment(sketch, "E383", {"start": v(-122.66, 12.74) * mm, "end": v(-122.6, 12.67) * mm});
            skLineSegment(sketch, "E384", {"start": v(-122.6, 12.67) * mm, "end": v(-122.56, 12.6) * mm});
            skLineSegment(sketch, "E385", {"start": v(-122.56, 12.6) * mm, "end": v(-122.53, 12.5) * mm});
            skLineSegment(sketch, "E386", {"start": v(-122.53, 12.5) * mm, "end": v(-122.5, 12.41) * mm});
            skLineSegment(sketch, "E387", {"start": v(-122.5, 12.41) * mm, "end": v(-122.48, 12.31) * mm});
            skLineSegment(sketch, "E388", {"start": v(-122.48, 12.31) * mm, "end": v(-122.47, 12.2) * mm});
            skLineSegment(sketch, "E389", {"start": v(-122.47, 12.2) * mm, "end": v(-122.47, 12.08) * mm});
            skLineSegment(sketch, "E390", {"start": v(-122.47, 12.08) * mm, "end": v(-122.47, 11.96) * mm});
            skLineSegment(sketch, "E391", {"start": v(-122.47, 11.96) * mm, "end": v(-122.48, 11.85) * mm});
            skLineSegment(sketch, "E392", {"start": v(-122.48, 11.85) * mm, "end": v(-122.5, 11.75) * mm});
            skLineSegment(sketch, "E393", {"start": v(-122.5, 11.75) * mm, "end": v(-122.53, 11.66) * mm});
            skLineSegment(sketch, "E394", {"start": v(-122.53, 11.66) * mm, "end": v(-122.56, 11.57) * mm});
            skLineSegment(sketch, "E395", {"start": v(-122.56, 11.57) * mm, "end": v(-122.6, 11.5) * mm});
            skLineSegment(sketch, "E396", {"start": v(-122.6, 11.5) * mm, "end": v(-122.66, 11.42) * mm});
            skLineSegment(sketch, "E397", {"start": v(-122.66, 11.42) * mm, "end": v(-122.72, 11.36) * mm});
            skLineSegment(sketch, "E398", {"start": v(-122.72, 11.36) * mm, "end": v(-122.78, 11.3) * mm});
            skLineSegment(sketch, "E399", {"start": v(-122.78, 11.3) * mm, "end": v(-122.86, 11.25) * mm});
            skLineSegment(sketch, "E400", {"start": v(-122.86, 11.25) * mm, "end": v(-122.94, 11.21) * mm});
            skLineSegment(sketch, "E401", {"start": v(-122.94, 11.21) * mm, "end": v(-123.03, 11.18) * mm});
            skLineSegment(sketch, "E402", {"start": v(-123.03, 11.18) * mm, "end": v(-123.13, 11.16) * mm});
            skLineSegment(sketch, "E403", {"start": v(-123.13, 11.16) * mm, "end": v(-123.24, 11.14) * mm});
            skLineSegment(sketch, "E404", {"start": v(-123.24, 11.14) * mm, "end": v(-123.35, 11.13) * mm});
            skLineSegment(sketch, "E405", {"start": v(-123.35, 11.13) * mm, "end": v(-123.48, 11.12) * mm});
            skLineSegment(sketch, "E406", {"start": v(-123.48, 11.12) * mm, "end": v(-138.3, 11.12) * mm});
            skLineSegment(sketch, "E407", {"start": v(-138.3, 11.12) * mm, "end": v(-138.64, 11.12) * mm});
            skLineSegment(sketch, "E408", {"start": v(-138.64, 11.12) * mm, "end": v(-138.98, 11.1) * mm});
            skLineSegment(sketch, "E409", {"start": v(-138.98, 11.1) * mm, "end": v(-139.3, 11.06) * mm});
            skLineSegment(sketch, "E410", {"start": v(-139.3, 11.06) * mm, "end": v(-139.63, 11) * mm});
            skLineSegment(sketch, "E411", {"start": v(-139.63, 11) * mm, "end": v(-139.95, 10.94) * mm});
            skLineSegment(sketch, "E412", {"start": v(-139.95, 10.94) * mm, "end": v(-140.25, 10.86) * mm});
            skLineSegment(sketch, "E413", {"start": v(-140.25, 10.86) * mm, "end": v(-140.55, 10.77) * mm});
            skLineSegment(sketch, "E414", {"start": v(-140.55, 10.77) * mm, "end": v(-140.85, 10.66) * mm});
            skLineSegment(sketch, "E415", {"start": v(-140.85, 10.66) * mm, "end": v(-141.13, 10.54) * mm});
            skLineSegment(sketch, "E416", {"start": v(-141.13, 10.54) * mm, "end": v(-141.41, 10.4) * mm});
            skLineSegment(sketch, "E417", {"start": v(-141.41, 10.4) * mm, "end": v(-141.68, 10.26) * mm});
            skLineSegment(sketch, "E418", {"start": v(-141.68, 10.26) * mm, "end": v(-141.94, 10.1) * mm});
            skLineSegment(sketch, "E419", {"start": v(-141.94, 10.1) * mm, "end": v(-142.2, 9.91) * mm});
            skLineSegment(sketch, "E420", {"start": v(-142.2, 9.91) * mm, "end": v(-142.45, 9.72) * mm});
            skLineSegment(sketch, "E421", {"start": v(-142.45, 9.72) * mm, "end": v(-142.69, 9.52) * mm});
            skLineSegment(sketch, "E422", {"start": v(-142.69, 9.52) * mm, "end": v(-142.92, 9.3) * mm});
            skLineSegment(sketch, "E423", {"start": v(-142.92, 9.3) * mm, "end": v(-143.14, 9.06) * mm});
            skLineSegment(sketch, "E424", {"start": v(-143.14, 9.06) * mm, "end": v(-143.34, 8.82) * mm});
            skLineSegment(sketch, "E425", {"start": v(-143.34, 8.82) * mm, "end": v(-143.54, 8.58) * mm});
            skLineSegment(sketch, "E426", {"start": v(-143.54, 8.58) * mm, "end": v(-143.72, 8.32) * mm});
            skLineSegment(sketch, "E427", {"start": v(-143.72, 8.32) * mm, "end": v(-143.88, 8.06) * mm});
            skLineSegment(sketch, "E428", {"start": v(-143.88, 8.06) * mm, "end": v(-144.03, 7.79) * mm});
            skLineSegment(sketch, "E429", {"start": v(-144.03, 7.79) * mm, "end": v(-144.17, 7.5) * mm});
            skLineSegment(sketch, "E430", {"start": v(-144.17, 7.5) * mm, "end": v(-144.29, 7.22) * mm});
            skLineSegment(sketch, "E431", {"start": v(-144.29, 7.22) * mm, "end": v(-144.4, 6.93) * mm});
            skLineSegment(sketch, "E432", {"start": v(-144.4, 6.93) * mm, "end": v(-144.49, 6.63) * mm});
            skLineSegment(sketch, "E433", {"start": v(-144.49, 6.63) * mm, "end": v(-144.57, 6.32) * mm});
            skLineSegment(sketch, "E434", {"start": v(-144.57, 6.32) * mm, "end": v(-144.63, 6) * mm});
            skLineSegment(sketch, "E435", {"start": v(-144.63, 6) * mm, "end": v(-144.68, 5.68) * mm});
            skLineSegment(sketch, "E436", {"start": v(-144.68, 5.68) * mm, "end": v(-144.72, 5.35) * mm});
            skLineSegment(sketch, "E437", {"start": v(-144.72, 5.35) * mm, "end": v(-144.74, 5.02) * mm});
            skLineSegment(sketch, "E438", {"start": v(-144.74, 5.02) * mm, "end": v(-144.75, 4.67) * mm});
            skLineSegment(sketch, "E439", {"start": v(-144.75, 4.67) * mm, "end": v(-144.74, 4.33) * mm});
            skLineSegment(sketch, "E440", {"start": v(-144.74, 4.33) * mm, "end": v(-144.72, 4) * mm});
            skLineSegment(sketch, "E441", {"start": v(-144.72, 4) * mm, "end": v(-144.68, 3.66) * mm});
            skLineSegment(sketch, "E442", {"start": v(-144.68, 3.66) * mm, "end": v(-144.63, 3.34) * mm});
            skLineSegment(sketch, "E443", {"start": v(-144.63, 3.34) * mm, "end": v(-144.57, 3.02) * mm});
            skLineSegment(sketch, "E444", {"start": v(-144.57, 3.02) * mm, "end": v(-144.49, 2.72) * mm});
            skLineSegment(sketch, "E445", {"start": v(-144.49, 2.72) * mm, "end": v(-144.4, 2.42) * mm});
            skLineSegment(sketch, "E446", {"start": v(-144.4, 2.42) * mm, "end": v(-144.29, 2.12) * mm});
            skLineSegment(sketch, "E447", {"start": v(-144.29, 2.12) * mm, "end": v(-144.17, 1.84) * mm});
            skLineSegment(sketch, "E448", {"start": v(-144.17, 1.84) * mm, "end": v(-144.03, 1.56) * mm});
            skLineSegment(sketch, "E449", {"start": v(-144.03, 1.56) * mm, "end": v(-143.88, 1.29) * mm});
            skLineSegment(sketch, "E450", {"start": v(-143.88, 1.29) * mm, "end": v(-143.72, 1.02) * mm});
            skLineSegment(sketch, "E451", {"start": v(-143.72, 1.02) * mm, "end": v(-143.54, 0.77) * mm});
            skLineSegment(sketch, "E452", {"start": v(-143.54, 0.77) * mm, "end": v(-143.35, 0.52) * mm});
            skLineSegment(sketch, "E453", {"start": v(-143.35, 0.52) * mm, "end": v(-143.14, 0.28) * mm});
            skLineSegment(sketch, "E454", {"start": v(-143.14, 0.28) * mm, "end": v(-142.92, 0.05) * mm});
            skLineSegment(sketch, "E455", {"start": v(-142.92, 0.05) * mm, "end": v(-142.69, -0.17) * mm});
            skLineSegment(sketch, "E456", {"start": v(-142.69, -0.17) * mm, "end": v(-142.45, -0.37) * mm});
            skLineSegment(sketch, "E457", {"start": v(-142.45, -0.37) * mm, "end": v(-142.2, -0.57) * mm});
            skLineSegment(sketch, "E458", {"start": v(-142.2, -0.57) * mm, "end": v(-141.95, -0.75) * mm});
            skLineSegment(sketch, "E459", {"start": v(-141.95, -0.75) * mm, "end": v(-141.68, -0.9) * mm});
            skLineSegment(sketch, "E460", {"start": v(-141.68, -0.9) * mm, "end": v(-141.41, -1.06) * mm});
            skLineSegment(sketch, "E461", {"start": v(-141.41, -1.06) * mm, "end": v(-141.13, -1.2) * mm});
            skLineSegment(sketch, "E462", {"start": v(-141.13, -1.2) * mm, "end": v(-140.85, -1.32) * mm});
            skLineSegment(sketch, "E463", {"start": v(-140.85, -1.32) * mm, "end": v(-140.55, -1.42) * mm});
            skLineSegment(sketch, "E464", {"start": v(-140.55, -1.42) * mm, "end": v(-140.25, -1.52) * mm});
            skLineSegment(sketch, "E465", {"start": v(-140.25, -1.52) * mm, "end": v(-139.95, -1.6) * mm});
            skLineSegment(sketch, "E466", {"start": v(-139.95, -1.6) * mm, "end": v(-139.63, -1.66) * mm});
            skLineSegment(sketch, "E467", {"start": v(-139.63, -1.66) * mm, "end": v(-139.3, -1.71) * mm});
            skLineSegment(sketch, "E468", {"start": v(-139.3, -1.71) * mm, "end": v(-138.98, -1.75) * mm});
            skLineSegment(sketch, "E469", {"start": v(-138.98, -1.75) * mm, "end": v(-138.64, -1.77) * mm});
            skLineSegment(sketch, "E470", {"start": v(-138.64, -1.77) * mm, "end": v(-138.3, -1.78) * mm});
            skLineSegment(sketch, "E471", {"start": v(-138.3, -1.78) * mm, "end": v(-128.4, -1.78) * mm});
            skLineSegment(sketch, "E472", {"start": v(-128.4, -1.78) * mm, "end": v(-128.28, -1.78) * mm});
            skLineSegment(sketch, "E473", {"start": v(-128.28, -1.78) * mm, "end": v(-128.17, -1.8) * mm});
            skLineSegment(sketch, "E474", {"start": v(-128.17, -1.8) * mm, "end": v(-128.07, -1.8) * mm});
            skLineSegment(sketch, "E475", {"start": v(-128.07, -1.8) * mm, "end": v(-127.98, -1.83) * mm});
            skLineSegment(sketch, "E476", {"start": v(-127.98, -1.83) * mm, "end": v(-127.89, -1.86) * mm});
            skLineSegment(sketch, "E477", {"start": v(-127.89, -1.86) * mm, "end": v(-127.81, -1.9) * mm});
            skLineSegment(sketch, "E478", {"start": v(-127.81, -1.9) * mm, "end": v(-127.74, -1.95) * mm});
            skLineSegment(sketch, "E479", {"start": v(-127.74, -1.95) * mm, "end": v(-127.68, -2) * mm});
            skLineSegment(sketch, "E480", {"start": v(-127.68, -2) * mm, "end": v(-127.62, -2.07) * mm});
            skLineSegment(sketch, "E481", {"start": v(-127.62, -2.07) * mm, "end": v(-127.57, -2.13) * mm});
            skLineSegment(sketch, "E482", {"start": v(-127.57, -2.13) * mm, "end": v(-127.53, -2.21) * mm});
            skLineSegment(sketch, "E483", {"start": v(-127.53, -2.21) * mm, "end": v(-127.5, -2.3) * mm});
            skLineSegment(sketch, "E484", {"start": v(-127.5, -2.3) * mm, "end": v(-127.48, -2.39) * mm});
            skLineSegment(sketch, "E485", {"start": v(-127.48, -2.39) * mm, "end": v(-127.46, -2.49) * mm});
            skLineSegment(sketch, "E486", {"start": v(-127.46, -2.49) * mm, "end": v(-127.45, -2.6) * mm});
            skLineSegment(sketch, "E487", {"start": v(-127.45, -2.6) * mm, "end": v(-127.44, -2.7) * mm});
            skLineSegment(sketch, "E488", {"start": v(-127.44, -2.7) * mm, "end": v(-127.45, -2.83) * mm});
            skLineSegment(sketch, "E489", {"start": v(-127.45, -2.83) * mm, "end": v(-127.46, -2.94) * mm});
            skLineSegment(sketch, "E490", {"start": v(-127.46, -2.94) * mm, "end": v(-127.48, -3.05) * mm});
            skLineSegment(sketch, "E491", {"start": v(-127.48, -3.05) * mm, "end": v(-127.5, -3.15) * mm});
            skLineSegment(sketch, "E492", {"start": v(-127.5, -3.15) * mm, "end": v(-127.53, -3.24) * mm});
            skLineSegment(sketch, "E493", {"start": v(-127.53, -3.24) * mm, "end": v(-127.57, -3.32) * mm});
            skLineSegment(sketch, "E494", {"start": v(-127.57, -3.32) * mm, "end": v(-127.62, -3.39) * mm});
            skLineSegment(sketch, "E495", {"start": v(-127.62, -3.39) * mm, "end": v(-127.68, -3.45) * mm});
            skLineSegment(sketch, "E496", {"start": v(-127.68, -3.45) * mm, "end": v(-127.74, -3.51) * mm});
            skLineSegment(sketch, "E497", {"start": v(-127.74, -3.51) * mm, "end": v(-127.81, -3.56) * mm});
            skLineSegment(sketch, "E498", {"start": v(-127.81, -3.56) * mm, "end": v(-127.89, -3.6) * mm});
            skLineSegment(sketch, "E499", {"start": v(-127.89, -3.6) * mm, "end": v(-127.98, -3.63) * mm});
            skLineSegment(sketch, "E500", {"start": v(-127.98, -3.63) * mm, "end": v(-128.07, -3.66) * mm});
            skLineSegment(sketch, "E501", {"start": v(-128.07, -3.66) * mm, "end": v(-128.17, -3.68) * mm});
            skLineSegment(sketch, "E502", {"start": v(-128.17, -3.68) * mm, "end": v(-128.28, -3.69) * mm});
            skLineSegment(sketch, "E503", {"start": v(-128.28, -3.69) * mm, "end": v(-128.4, -3.7) * mm});
            skLineSegment(sketch, "E504", {"start": v(-128.4, -3.7) * mm, "end": v(-138.3, -3.7) * mm});
            skLineSegment(sketch, "E505", {"start": v(-138.3, -3.7) * mm, "end": v(-138.64, -3.7) * mm});
            skLineSegment(sketch, "E506", {"start": v(-138.64, -3.7) * mm, "end": v(-138.98, -3.72) * mm});
            skLineSegment(sketch, "E507", {"start": v(-138.98, -3.72) * mm, "end": v(-139.3, -3.76) * mm});
            skLineSegment(sketch, "E508", {"start": v(-139.3, -3.76) * mm, "end": v(-139.63, -3.8) * mm});
            skLineSegment(sketch, "E509", {"start": v(-139.63, -3.8) * mm, "end": v(-139.95, -3.87) * mm});
            skLineSegment(sketch, "E510", {"start": v(-139.95, -3.87) * mm, "end": v(-140.25, -3.95) * mm});
            skLineSegment(sketch, "E511", {"start": v(-140.25, -3.95) * mm, "end": v(-140.55, -4.04) * mm});
            skLineSegment(sketch, "E512", {"start": v(-140.55, -4.04) * mm, "end": v(-140.85, -4.15) * mm});
            skLineSegment(sketch, "E513", {"start": v(-140.85, -4.15) * mm, "end": v(-141.13, -4.27) * mm});
            skLineSegment(sketch, "E514", {"start": v(-141.13, -4.27) * mm, "end": v(-141.41, -4.4) * mm});
            skLineSegment(sketch, "E515", {"start": v(-141.41, -4.4) * mm, "end": v(-141.68, -4.55) * mm});
            skLineSegment(sketch, "E516", {"start": v(-141.68, -4.55) * mm, "end": v(-141.94, -4.72) * mm});
            skLineSegment(sketch, "E517", {"start": v(-141.94, -4.72) * mm, "end": v(-142.2, -4.9) * mm});
            skLineSegment(sketch, "E518", {"start": v(-142.2, -4.9) * mm, "end": v(-142.45, -5.09) * mm});
            skLineSegment(sketch, "E519", {"start": v(-142.45, -5.09) * mm, "end": v(-142.69, -5.3) * mm});
            skLineSegment(sketch, "E520", {"start": v(-142.69, -5.3) * mm, "end": v(-142.92, -5.51) * mm});
            skLineSegment(sketch, "E521", {"start": v(-142.92, -5.51) * mm, "end": v(-143.14, -5.74) * mm});
            skLineSegment(sketch, "E522", {"start": v(-143.14, -5.74) * mm, "end": v(-143.34, -5.98) * mm});
            skLineSegment(sketch, "E523", {"start": v(-143.34, -5.98) * mm, "end": v(-143.54, -6.23) * mm});
            skLineSegment(sketch, "E524", {"start": v(-143.54, -6.23) * mm, "end": v(-143.72, -6.48) * mm});
            skLineSegment(sketch, "E525", {"start": v(-143.72, -6.48) * mm, "end": v(-143.88, -6.74) * mm});
            skLineSegment(sketch, "E526", {"start": v(-143.88, -6.74) * mm, "end": v(-144.03, -7.01) * mm});
            skLineSegment(sketch, "E527", {"start": v(-144.03, -7.01) * mm, "end": v(-144.17, -7.3) * mm});
            skLineSegment(sketch, "E528", {"start": v(-144.17, -7.3) * mm, "end": v(-144.29, -7.58) * mm});
            skLineSegment(sketch, "E529", {"start": v(-144.29, -7.58) * mm, "end": v(-144.4, -7.87) * mm});
            skLineSegment(sketch, "E530", {"start": v(-144.4, -7.87) * mm, "end": v(-144.49, -8.17) * mm});
            skLineSegment(sketch, "E531", {"start": v(-144.49, -8.17) * mm, "end": v(-144.57, -8.48) * mm});
            skLineSegment(sketch, "E532", {"start": v(-144.57, -8.48) * mm, "end": v(-144.63, -8.8) * mm});
            skLineSegment(sketch, "E533", {"start": v(-144.63, -8.8) * mm, "end": v(-144.68, -9.13) * mm});
            skLineSegment(sketch, "E534", {"start": v(-144.68, -9.13) * mm, "end": v(-144.72, -9.46) * mm});
            skLineSegment(sketch, "E535", {"start": v(-144.72, -9.46) * mm, "end": v(-144.74, -9.8) * mm});
            skLineSegment(sketch, "E536", {"start": v(-144.74, -9.8) * mm, "end": v(-144.75, -10.14) * mm});
            skLineSegment(sketch, "E537", {"start": v(-144.75, -10.14) * mm, "end": v(-144.74, -10.5) * mm});
            skLineSegment(sketch, "E538", {"start": v(-144.74, -10.5) * mm, "end": v(-144.72, -10.83) * mm});
            skLineSegment(sketch, "E539", {"start": v(-144.72, -10.83) * mm, "end": v(-144.68, -11.16) * mm});
            skLineSegment(sketch, "E540", {"start": v(-144.68, -11.16) * mm, "end": v(-144.63, -11.49) * mm});
            skLineSegment(sketch, "E541", {"start": v(-144.63, -11.49) * mm, "end": v(-144.57, -11.8) * mm});
            skLineSegment(sketch, "E542", {"start": v(-144.57, -11.8) * mm, "end": v(-144.49, -12.12) * mm});
            skLineSegment(sketch, "E543", {"start": v(-144.49, -12.12) * mm, "end": v(-144.4, -12.42) * mm});
            skLineSegment(sketch, "E544", {"start": v(-144.4, -12.42) * mm, "end": v(-144.29, -12.72) * mm});
            skLineSegment(sketch, "E545", {"start": v(-144.29, -12.72) * mm, "end": v(-144.17, -13) * mm});
            skLineSegment(sketch, "E546", {"start": v(-144.17, -13) * mm, "end": v(-144.03, -13.28) * mm});
            skLineSegment(sketch, "E547", {"start": v(-144.03, -13.28) * mm, "end": v(-143.88, -13.56) * mm});
            skLineSegment(sketch, "E548", {"start": v(-143.88, -13.56) * mm, "end": v(-143.72, -13.82) * mm});
            skLineSegment(sketch, "E549", {"start": v(-143.72, -13.82) * mm, "end": v(-143.54, -14.08) * mm});
            skLineSegment(sketch, "E550", {"start": v(-143.54, -14.08) * mm, "end": v(-143.35, -14.33) * mm});
            skLineSegment(sketch, "E551", {"start": v(-143.35, -14.33) * mm, "end": v(-143.14, -14.57) * mm});
            skLineSegment(sketch, "E552", {"start": v(-143.14, -14.57) * mm, "end": v(-142.92, -14.8) * mm});
            skLineSegment(sketch, "E553", {"start": v(-142.92, -14.8) * mm, "end": v(-142.69, -15.02) * mm});
            skLineSegment(sketch, "E554", {"start": v(-142.69, -15.02) * mm, "end": v(-142.45, -15.23) * mm});
            skLineSegment(sketch, "E555", {"start": v(-142.45, -15.23) * mm, "end": v(-142.2, -15.43) * mm});
            skLineSegment(sketch, "E556", {"start": v(-142.2, -15.43) * mm, "end": v(-141.95, -15.6) * mm});
            skLineSegment(sketch, "E557", {"start": v(-141.95, -15.6) * mm, "end": v(-141.68, -15.77) * mm});
            skLineSegment(sketch, "E558", {"start": v(-141.68, -15.77) * mm, "end": v(-141.41, -15.92) * mm});
            skLineSegment(sketch, "E559", {"start": v(-141.41, -15.92) * mm, "end": v(-141.13, -16.06) * mm});
            skLineSegment(sketch, "E560", {"start": v(-141.13, -16.06) * mm, "end": v(-140.85, -16.18) * mm});
            skLineSegment(sketch, "E561", {"start": v(-140.85, -16.18) * mm, "end": v(-140.55, -16.3) * mm});
            skLineSegment(sketch, "E562", {"start": v(-140.55, -16.3) * mm, "end": v(-140.25, -16.39) * mm});
            skLineSegment(sketch, "E563", {"start": v(-140.25, -16.39) * mm, "end": v(-139.95, -16.46) * mm});
            skLineSegment(sketch, "E564", {"start": v(-139.95, -16.46) * mm, "end": v(-139.63, -16.53) * mm});
            skLineSegment(sketch, "E565", {"start": v(-139.63, -16.53) * mm, "end": v(-139.3, -16.58) * mm});
            skLineSegment(sketch, "E566", {"start": v(-139.3, -16.58) * mm, "end": v(-138.98, -16.62) * mm});
            skLineSegment(sketch, "E567", {"start": v(-138.98, -16.62) * mm, "end": v(-138.64, -16.64) * mm});
            skLineSegment(sketch, "E568", {"start": v(-138.64, -16.64) * mm, "end": v(-138.3, -16.65) * mm});
            skLineSegment(sketch, "E569", {"start": v(-138.3, -16.65) * mm, "end": v(-123.48, -16.65) * mm});
            skLineSegment(sketch, "E570", {"start": v(-123.48, -16.65) * mm, "end": v(-123.35, -16.65) * mm});
            skLineSegment(sketch, "E571", {"start": v(-123.35, -16.65) * mm, "end": v(-123.24, -16.66) * mm});
            skLineSegment(sketch, "E572", {"start": v(-123.24, -16.66) * mm, "end": v(-123.13, -16.68) * mm});
            skLineSegment(sketch, "E573", {"start": v(-123.13, -16.68) * mm, "end": v(-123.03, -16.7) * mm});
            skLineSegment(sketch, "E574", {"start": v(-123.03, -16.7) * mm, "end": v(-122.94, -16.74) * mm});
            skLineSegment(sketch, "E575", {"start": v(-122.94, -16.74) * mm, "end": v(-122.86, -16.78) * mm});
            skLineSegment(sketch, "E576", {"start": v(-122.86, -16.78) * mm, "end": v(-122.78, -16.83) * mm});
            skLineSegment(sketch, "E577", {"start": v(-122.78, -16.83) * mm, "end": v(-122.72, -16.89) * mm});
            skLineSegment(sketch, "E578", {"start": v(-122.72, -16.89) * mm, "end": v(-122.66, -16.95) * mm});
            skLineSegment(sketch, "E579", {"start": v(-122.66, -16.95) * mm, "end": v(-122.6, -17.02) * mm});
            skLineSegment(sketch, "E580", {"start": v(-122.6, -17.02) * mm, "end": v(-122.56, -17.1) * mm});
            skLineSegment(sketch, "E581", {"start": v(-122.56, -17.1) * mm, "end": v(-122.53, -17.2) * mm});
            skLineSegment(sketch, "E582", {"start": v(-122.53, -17.2) * mm, "end": v(-122.5, -17.3) * mm});
            skLineSegment(sketch, "E583", {"start": v(-122.5, -17.3) * mm, "end": v(-122.48, -17.4) * mm});
            skLineSegment(sketch, "E584", {"start": v(-122.48, -17.4) * mm, "end": v(-122.47, -17.5) * mm});
            skLineSegment(sketch, "E585", {"start": v(-122.47, -17.5) * mm, "end": v(-122.47, -17.63) * mm});
            skLineSegment(sketch, "E586", {"start": v(-122.47, -17.63) * mm, "end": v(-122.47, -17.75) * mm});
            skLineSegment(sketch, "E587", {"start": v(-122.47, -17.75) * mm, "end": v(-122.48, -17.85) * mm});
            skLineSegment(sketch, "E588", {"start": v(-122.48, -17.85) * mm, "end": v(-122.5, -17.95) * mm});
            skLineSegment(sketch, "E589", {"start": v(-122.5, -17.95) * mm, "end": v(-122.53, -18.04) * mm});
            skLineSegment(sketch, "E590", {"start": v(-122.53, -18.04) * mm, "end": v(-122.56, -18.13) * mm});
            skLineSegment(sketch, "E591", {"start": v(-122.56, -18.13) * mm, "end": v(-122.6, -18.2) * mm});
            skLineSegment(sketch, "E592", {"start": v(-122.6, -18.2) * mm, "end": v(-122.66, -18.27) * mm});
            skLineSegment(sketch, "E593", {"start": v(-122.66, -18.27) * mm, "end": v(-122.72, -18.34) * mm});
            skLineSegment(sketch, "E594", {"start": v(-122.72, -18.34) * mm, "end": v(-122.78, -18.39) * mm});
            skLineSegment(sketch, "E595", {"start": v(-122.78, -18.39) * mm, "end": v(-122.86, -18.44) * mm});
            skLineSegment(sketch, "E596", {"start": v(-122.86, -18.44) * mm, "end": v(-122.94, -18.47) * mm});
            skLineSegment(sketch, "E597", {"start": v(-122.94, -18.47) * mm, "end": v(-123.03, -18.5) * mm});
            skLineSegment(sketch, "E598", {"start": v(-123.03, -18.5) * mm, "end": v(-123.13, -18.53) * mm});
            skLineSegment(sketch, "E599", {"start": v(-123.13, -18.53) * mm, "end": v(-123.24, -18.55) * mm});
            skLineSegment(sketch, "E600", {"start": v(-123.24, -18.55) * mm, "end": v(-123.35, -18.56) * mm});
            skLineSegment(sketch, "E601", {"start": v(-123.35, -18.56) * mm, "end": v(-123.48, -18.56) * mm});
            skLineSegment(sketch, "E602", {"start": v(-123.48, -18.56) * mm, "end": v(-140.73, -18.56) * mm});
            skLineSegment(sketch, "E603", {"start": v(-140.73, -18.56) * mm, "end": v(-140.94, -18.57) * mm});
            skLineSegment(sketch, "E604", {"start": v(-140.94, -18.57) * mm, "end": v(-141.15, -18.58) * mm});
            skLineSegment(sketch, "E605", {"start": v(-141.15, -18.58) * mm, "end": v(-141.36, -18.6) * mm});
            skLineSegment(sketch, "E606", {"start": v(-141.36, -18.6) * mm, "end": v(-141.56, -18.63) * mm});
            skLineSegment(sketch, "E607", {"start": v(-141.56, -18.63) * mm, "end": v(-141.75, -18.67) * mm});
            skLineSegment(sketch, "E608", {"start": v(-141.75, -18.67) * mm, "end": v(-141.95, -18.72) * mm});
            skLineSegment(sketch, "E609", {"start": v(-141.95, -18.72) * mm, "end": v(-142.13, -18.78) * mm});
            skLineSegment(sketch, "E610", {"start": v(-142.13, -18.78) * mm, "end": v(-142.31, -18.84) * mm});
            skLineSegment(sketch, "E611", {"start": v(-142.31, -18.84) * mm, "end": v(-142.5, -18.92) * mm});
            skLineSegment(sketch, "E612", {"start": v(-142.5, -18.92) * mm, "end": v(-142.67, -19) * mm});
            skLineSegment(sketch, "E613", {"start": v(-142.67, -19) * mm, "end": v(-142.83, -19.1) * mm});
            skLineSegment(sketch, "E614", {"start": v(-142.83, -19.1) * mm, "end": v(-143, -19.2) * mm});
            skLineSegment(sketch, "E615", {"start": v(-143, -19.2) * mm, "end": v(-143.16, -19.3) * mm});
            skLineSegment(sketch, "E616", {"start": v(-143.16, -19.3) * mm, "end": v(-143.31, -19.42) * mm});
            skLineSegment(sketch, "E617", {"start": v(-143.31, -19.42) * mm, "end": v(-143.46, -19.54) * mm});
            skLineSegment(sketch, "E618", {"start": v(-143.46, -19.54) * mm, "end": v(-143.6, -19.68) * mm});
            skLineSegment(sketch, "E619", {"start": v(-143.6, -19.68) * mm, "end": v(-143.74, -19.82) * mm});
            skLineSegment(sketch, "E620", {"start": v(-143.74, -19.82) * mm, "end": v(-143.87, -19.96) * mm});
            skLineSegment(sketch, "E621", {"start": v(-143.87, -19.96) * mm, "end": v(-144, -20.11) * mm});
            skLineSegment(sketch, "E622", {"start": v(-144, -20.11) * mm, "end": v(-144.1, -20.27) * mm});
            skLineSegment(sketch, "E623", {"start": v(-144.1, -20.27) * mm, "end": v(-144.2, -20.43) * mm});
            skLineSegment(sketch, "E624", {"start": v(-144.2, -20.43) * mm, "end": v(-144.3, -20.6) * mm});
            skLineSegment(sketch, "E625", {"start": v(-144.3, -20.6) * mm, "end": v(-144.38, -20.77) * mm});
            skLineSegment(sketch, "E626", {"start": v(-144.38, -20.77) * mm, "end": v(-144.46, -20.95) * mm});
            skLineSegment(sketch, "E627", {"start": v(-144.46, -20.95) * mm, "end": v(-144.53, -21.13) * mm});
            skLineSegment(sketch, "E628", {"start": v(-144.53, -21.13) * mm, "end": v(-144.59, -21.31) * mm});
            skLineSegment(sketch, "E629", {"start": v(-144.59, -21.31) * mm, "end": v(-144.63, -21.5) * mm});
            skLineSegment(sketch, "E630", {"start": v(-144.63, -21.5) * mm, "end": v(-144.67, -21.7) * mm});
            skLineSegment(sketch, "E631", {"start": v(-144.67, -21.7) * mm, "end": v(-144.7, -21.9) * mm});
            skLineSegment(sketch, "E632", {"start": v(-144.7, -21.9) * mm, "end": v(-144.73, -22.1) * mm});
            skLineSegment(sketch, "E633", {"start": v(-144.73, -22.1) * mm, "end": v(-144.74, -22.31) * mm});
            skLineSegment(sketch, "E634", {"start": v(-144.74, -22.31) * mm, "end": v(-144.75, -22.53) * mm});
            skLineSegment(sketch, "E635", {"start": v(-144.75, -22.53) * mm, "end": v(-144.74, -22.74) * mm});
            skLineSegment(sketch, "E636", {"start": v(-144.74, -22.74) * mm, "end": v(-144.73, -22.95) * mm});
            skLineSegment(sketch, "E637", {"start": v(-144.73, -22.95) * mm, "end": v(-144.7, -23.15) * mm});
            skLineSegment(sketch, "E638", {"start": v(-144.7, -23.15) * mm, "end": v(-144.67, -23.35) * mm});
            skLineSegment(sketch, "E639", {"start": v(-144.67, -23.35) * mm, "end": v(-144.63, -23.55) * mm});
            skLineSegment(sketch, "E640", {"start": v(-144.63, -23.55) * mm, "end": v(-144.59, -23.74) * mm});
            skLineSegment(sketch, "E641", {"start": v(-144.59, -23.74) * mm, "end": v(-144.53, -23.92) * mm});
            skLineSegment(sketch, "E642", {"start": v(-144.53, -23.92) * mm, "end": v(-144.46, -24.1) * mm});
            skLineSegment(sketch, "E643", {"start": v(-144.46, -24.1) * mm, "end": v(-144.38, -24.28) * mm});
            skLineSegment(sketch, "E644", {"start": v(-144.38, -24.28) * mm, "end": v(-144.3, -24.45) * mm});
            skLineSegment(sketch, "E645", {"start": v(-144.3, -24.45) * mm, "end": v(-144.2, -24.62) * mm});
            skLineSegment(sketch, "E646", {"start": v(-144.2, -24.62) * mm, "end": v(-144.1, -24.78) * mm});
            skLineSegment(sketch, "E647", {"start": v(-144.1, -24.78) * mm, "end": v(-144, -24.94) * mm});
            skLineSegment(sketch, "E648", {"start": v(-144, -24.94) * mm, "end": v(-143.87, -25.09) * mm});
            skLineSegment(sketch, "E649", {"start": v(-143.87, -25.09) * mm, "end": v(-143.74, -25.23) * mm});
            skLineSegment(sketch, "E650", {"start": v(-143.74, -25.23) * mm, "end": v(-143.6, -25.38) * mm});
            skLineSegment(sketch, "E651", {"start": v(-143.6, -25.38) * mm, "end": v(-143.46, -25.5) * mm});
            skLineSegment(sketch, "E652", {"start": v(-143.46, -25.5) * mm, "end": v(-143.31, -25.64) * mm});
            skLineSegment(sketch, "E653", {"start": v(-143.31, -25.64) * mm, "end": v(-143.16, -25.75) * mm});
            skLineSegment(sketch, "E654", {"start": v(-143.16, -25.75) * mm, "end": v(-143, -25.86) * mm});
            skLineSegment(sketch, "E655", {"start": v(-143, -25.86) * mm, "end": v(-142.84, -25.96) * mm});
            skLineSegment(sketch, "E656", {"start": v(-142.84, -25.96) * mm, "end": v(-142.67, -26.05) * mm});
            skLineSegment(sketch, "E657", {"start": v(-142.67, -26.05) * mm, "end": v(-142.5, -26.14) * mm});
            skLineSegment(sketch, "E658", {"start": v(-142.5, -26.14) * mm, "end": v(-142.32, -26.2) * mm});
            skLineSegment(sketch, "E659", {"start": v(-142.32, -26.2) * mm, "end": v(-142.13, -26.27) * mm});
            skLineSegment(sketch, "E660", {"start": v(-142.13, -26.27) * mm, "end": v(-141.95, -26.33) * mm});
            skLineSegment(sketch, "E661", {"start": v(-141.95, -26.33) * mm, "end": v(-141.75, -26.38) * mm});
            skLineSegment(sketch, "E662", {"start": v(-141.75, -26.38) * mm, "end": v(-141.56, -26.42) * mm});
            skLineSegment(sketch, "E663", {"start": v(-141.56, -26.42) * mm, "end": v(-141.36, -26.45) * mm});
            skLineSegment(sketch, "E664", {"start": v(-141.36, -26.45) * mm, "end": v(-141.15, -26.47) * mm});
            skLineSegment(sketch, "E665", {"start": v(-141.15, -26.47) * mm, "end": v(-140.94, -26.48) * mm});
            skLineSegment(sketch, "E666", {"start": v(-140.94, -26.48) * mm, "end": v(-140.73, -26.49) * mm});
            skLineSegment(sketch, "E667", {"start": v(-140.73, -26.49) * mm, "end": v(-100, -26.49) * mm});
            skLineSegment(sketch, "E668", {"start": v(-100, -26.49) * mm, "end": v(-99.68, -26.47) * mm});
            skLineSegment(sketch, "E669", {"start": v(-99.68, -26.47) * mm, "end": v(-99.37, -26.42) * mm});
            skLineSegment(sketch, "E670", {"start": v(-99.37, -26.42) * mm, "end": v(-99.07, -26.35) * mm});
            skLineSegment(sketch, "E671", {"start": v(-99.07, -26.35) * mm, "end": v(-98.78, -26.24) * mm});
            skLineSegment(sketch, "E672", {"start": v(-98.78, -26.24) * mm, "end": v(-98.5, -26.11) * mm});
            skLineSegment(sketch, "E673", {"start": v(-98.5, -26.11) * mm, "end": v(-98.25, -25.95) * mm});
            skLineSegment(sketch, "E674", {"start": v(-98.25, -25.95) * mm, "end": v(-98.01, -25.77) * mm});
            skLineSegment(sketch, "E675", {"start": v(-98.01, -25.77) * mm, "end": v(-97.79, -25.57) * mm});
            skLineSegment(sketch, "E676", {"start": v(-97.79, -25.57) * mm, "end": v(-97.59, -25.35) * mm});
            skLineSegment(sketch, "E677", {"start": v(-97.59, -25.35) * mm, "end": v(-97.4, -25.1) * mm});
            skLineSegment(sketch, "E678", {"start": v(-97.4, -25.1) * mm, "end": v(-97.25, -24.85) * mm});
            skLineSegment(sketch, "E679", {"start": v(-97.25, -24.85) * mm, "end": v(-97.12, -24.57) * mm});
            skLineSegment(sketch, "E680", {"start": v(-97.12, -24.57) * mm, "end": v(-97.01, -24.29) * mm});
            skLineSegment(sketch, "E681", {"start": v(-97.01, -24.29) * mm, "end": v(-96.93, -23.99) * mm});
            skLineSegment(sketch, "E682", {"start": v(-96.93, -23.99) * mm, "end": v(-96.89, -23.68) * mm});
            skLineSegment(sketch, "E683", {"start": v(-96.89, -23.68) * mm, "end": v(-96.87, -23.36) * mm});
            skLineSegment(sketch, "E684", {"start": v(-96.87, -23.36) * mm, "end": v(-96.87, -19.84) * mm});
            skLineSegment(sketch, "E685", {"start": v(-96.87, -19.84) * mm, "end": v(-96.88, -19.7) * mm});
            skLineSegment(sketch, "E686", {"start": v(-96.88, -19.7) * mm, "end": v(-96.9, -19.56) * mm});
            skLineSegment(sketch, "E687", {"start": v(-96.9, -19.56) * mm, "end": v(-96.93, -19.43) * mm});
            skLineSegment(sketch, "E688", {"start": v(-96.93, -19.43) * mm, "end": v(-96.97, -19.3) * mm});
            skLineSegment(sketch, "E689", {"start": v(-96.97, -19.3) * mm, "end": v(-97.02, -19.18) * mm});
            skLineSegment(sketch, "E690", {"start": v(-97.02, -19.18) * mm, "end": v(-97.09, -19.06) * mm});
            skLineSegment(sketch, "E691", {"start": v(-97.09, -19.06) * mm, "end": v(-97.16, -18.95) * mm});
            skLineSegment(sketch, "E692", {"start": v(-97.16, -18.95) * mm, "end": v(-97.24, -18.85) * mm});
            skLineSegment(sketch, "E693", {"start": v(-97.24, -18.85) * mm, "end": v(-97.33, -18.75) * mm});
            skLineSegment(sketch, "E694", {"start": v(-97.33, -18.75) * mm, "end": v(-97.43, -18.67) * mm});
            skLineSegment(sketch, "E695", {"start": v(-97.43, -18.67) * mm, "end": v(-97.54, -18.59) * mm});
            skLineSegment(sketch, "E696", {"start": v(-97.54, -18.59) * mm, "end": v(-97.66, -18.52) * mm});
            skLineSegment(sketch, "E697", {"start": v(-97.66, -18.52) * mm, "end": v(-97.78, -18.46) * mm});
            skLineSegment(sketch, "E698", {"start": v(-97.78, -18.46) * mm, "end": v(-97.9, -18.41) * mm});
            skLineSegment(sketch, "E699", {"start": v(-97.9, -18.41) * mm, "end": v(-98.04, -18.38) * mm});
            skLineSegment(sketch, "E700", {"start": v(-98.04, -18.38) * mm, "end": v(-98.17, -18.35) * mm});
            skLineSegment(sketch, "E701", {"start": v(-98.17, -18.35) * mm, "end": v(-98.9, -18.25) * mm});
            skLineSegment(sketch, "E702", {"start": v(-98.9, -18.25) * mm, "end": v(-99.6, -18.1) * mm});
            skLineSegment(sketch, "E703", {"start": v(-99.6, -18.1) * mm, "end": v(-100.29, -17.94) * mm});
            skLineSegment(sketch, "E704", {"start": v(-100.29, -17.94) * mm, "end": v(-100.96, -17.74) * mm});
            skLineSegment(sketch, "E705", {"start": v(-100.96, -17.74) * mm, "end": v(-101.63, -17.52) * mm});
            skLineSegment(sketch, "E706", {"start": v(-101.63, -17.52) * mm, "end": v(-102.27, -17.26) * mm});
            skLineSegment(sketch, "E707", {"start": v(-102.27, -17.26) * mm, "end": v(-102.9, -16.97) * mm});
            skLineSegment(sketch, "E708", {"start": v(-102.9, -16.97) * mm, "end": v(-103.52, -16.66) * mm});
            skLineSegment(sketch, "E709", {"start": v(-103.52, -16.66) * mm, "end": v(-104.12, -16.31) * mm});
            skLineSegment(sketch, "E710", {"start": v(-104.12, -16.31) * mm, "end": v(-104.7, -15.94) * mm});
            skLineSegment(sketch, "E711", {"start": v(-104.7, -15.94) * mm, "end": v(-105.28, -15.53) * mm});
            skLineSegment(sketch, "E712", {"start": v(-105.28, -15.53) * mm, "end": v(-105.84, -15.1) * mm});
            skLineSegment(sketch, "E713", {"start": v(-105.84, -15.1) * mm, "end": v(-106.38, -14.63) * mm});
            skLineSegment(sketch, "E714", {"start": v(-106.38, -14.63) * mm, "end": v(-106.9, -14.14) * mm});
            skLineSegment(sketch, "E715", {"start": v(-106.9, -14.14) * mm, "end": v(-107.4, -13.62) * mm});
            skLineSegment(sketch, "E716", {"start": v(-107.4, -13.62) * mm, "end": v(-107.9, -13.07) * mm});
            skLineSegment(sketch, "E717", {"start": v(-107.9, -13.07) * mm, "end": v(-108.37, -12.5) * mm});
            skLineSegment(sketch, "E718", {"start": v(-108.37, -12.5) * mm, "end": v(-108.8, -11.91) * mm});
            skLineSegment(sketch, "E719", {"start": v(-108.8, -11.91) * mm, "end": v(-109.22, -11.32) * mm});
            skLineSegment(sketch, "E720", {"start": v(-109.22, -11.32) * mm, "end": v(-109.6, -10.71) * mm});
            skLineSegment(sketch, "E721", {"start": v(-109.6, -10.71) * mm, "end": v(-109.95, -10.1) * mm});
            skLineSegment(sketch, "E722", {"start": v(-109.95, -10.1) * mm, "end": v(-110.27, -9.47) * mm});
            skLineSegment(sketch, "E723", {"start": v(-110.27, -9.47) * mm, "end": v(-110.55, -8.83) * mm});
            skLineSegment(sketch, "E724", {"start": v(-110.55, -8.83) * mm, "end": v(-110.81, -8.18) * mm});
            skLineSegment(sketch, "E725", {"start": v(-110.81, -8.18) * mm, "end": v(-111.04, -7.52) * mm});
            skLineSegment(sketch, "E726", {"start": v(-111.04, -7.52) * mm, "end": v(-111.24, -6.85) * mm});
            skLineSegment(sketch, "E727", {"start": v(-111.24, -6.85) * mm, "end": v(-111.4, -6.17) * mm});
            skLineSegment(sketch, "E728", {"start": v(-111.4, -6.17) * mm, "end": v(-111.55, -5.49) * mm});
            skLineSegment(sketch, "E729", {"start": v(-111.55, -5.49) * mm, "end": v(-111.65, -4.79) * mm});
            skLineSegment(sketch, "E730", {"start": v(-111.65, -4.79) * mm, "end": v(-111.73, -4.08) * mm});
            skLineSegment(sketch, "E731", {"start": v(-111.73, -4.08) * mm, "end": v(-111.78, -3.36) * mm});
            skLineSegment(sketch, "E732", {"start": v(-111.78, -3.36) * mm, "end": v(-111.8, -2.63) * mm});
            skLineSegment(sketch, "E733", {"start": v(-111.8, -2.63) * mm, "end": v(-111.77, -1.81) * mm});
            skLineSegment(sketch, "E734", {"start": v(-111.77, -1.81) * mm, "end": v(-111.72, -1) * mm});
            skLineSegment(sketch, "E735", {"start": v(-111.72, -1) * mm, "end": v(-111.63, -0.22) * mm});
            skLineSegment(sketch, "E736", {"start": v(-111.63, -0.22) * mm, "end": v(-111.5, 0.55) * mm});
            skLineSegment(sketch, "E737", {"start": v(-111.5, 0.55) * mm, "end": v(-111.34, 1.31) * mm});
            skLineSegment(sketch, "E738", {"start": v(-111.34, 1.31) * mm, "end": v(-111.14, 2.06) * mm});
            skLineSegment(sketch, "E739", {"start": v(-111.14, 2.06) * mm, "end": v(-110.9, 2.79) * mm});
            skLineSegment(sketch, "E740", {"start": v(-110.9, 2.79) * mm, "end": v(-110.63, 3.5) * mm});
            skLineSegment(sketch, "E741", {"start": v(-110.63, 3.5) * mm, "end": v(-110.32, 4.2) * mm});
            skLineSegment(sketch, "E742", {"start": v(-110.32, 4.2) * mm, "end": v(-109.98, 4.88) * mm});
            skLineSegment(sketch, "E743", {"start": v(-109.98, 4.88) * mm, "end": v(-109.6, 5.55) * mm});
            skLineSegment(sketch, "E744", {"start": v(-109.6, 5.55) * mm, "end": v(-109.18, 6.2) * mm});
            skLineSegment(sketch, "E745", {"start": v(-109.18, 6.2) * mm, "end": v(-108.73, 6.84) * mm});
            skLineSegment(sketch, "E746", {"start": v(-108.73, 6.84) * mm, "end": v(-108.24, 7.46) * mm});
            skLineSegment(sketch, "E747", {"start": v(-108.24, 7.46) * mm, "end": v(-107.72, 8.06) * mm});
            skLineSegment(sketch, "E748", {"start": v(-107.72, 8.06) * mm, "end": v(-107.16, 8.65) * mm});
            skLineSegment(sketch, "E749", {"start": v(-107.16, 8.65) * mm, "end": v(-106.58, 9.21) * mm});
            skLineSegment(sketch, "E750", {"start": v(-106.58, 9.21) * mm, "end": v(-105.98, 9.74) * mm});
            skLineSegment(sketch, "E751", {"start": v(-105.98, 9.74) * mm, "end": v(-105.36, 10.23) * mm});
            skLineSegment(sketch, "E752", {"start": v(-105.36, 10.23) * mm, "end": v(-104.73, 10.68) * mm});
            skLineSegment(sketch, "E753", {"start": v(-104.73, 10.68) * mm, "end": v(-104.08, 11.1) * mm});
            skLineSegment(sketch, "E754", {"start": v(-104.08, 11.1) * mm, "end": v(-103.41, 11.48) * mm});
            skLineSegment(sketch, "E755", {"start": v(-103.41, 11.48) * mm, "end": v(-102.73, 11.83) * mm});
            skLineSegment(sketch, "E756", {"start": v(-102.73, 11.83) * mm, "end": v(-102.03, 12.14) * mm});
            skLineSegment(sketch, "E757", {"start": v(-102.03, 12.14) * mm, "end": v(-101.32, 12.4) * mm});
            skLineSegment(sketch, "E758", {"start": v(-101.32, 12.4) * mm, "end": v(-100.6, 12.65) * mm});
            skLineSegment(sketch, "E759", {"start": v(-100.6, 12.65) * mm, "end": v(-99.85, 12.85) * mm});
            skLineSegment(sketch, "E760", {"start": v(-99.85, 12.85) * mm, "end": v(-99.1, 13.01) * mm});
            skLineSegment(sketch, "E761", {"start": v(-99.1, 13.01) * mm, "end": v(-98.32, 13.14) * mm});
            skLineSegment(sketch, "E762", {"start": v(-98.32, 13.14) * mm, "end": v(-97.53, 13.23) * mm});
            skLineSegment(sketch, "E763", {"start": v(-97.53, 13.23) * mm, "end": v(-96.73, 13.29) * mm});
            skLineSegment(sketch, "E764", {"start": v(-96.73, 13.29) * mm, "end": v(-95.91, 13.3) * mm});
            skLineSegment(sketch, "E765", {"start": v(-95.91, 13.3) * mm, "end": v(-95.09, 13.29) * mm});
            skLineSegment(sketch, "E766", {"start": v(-95.09, 13.29) * mm, "end": v(-94.28, 13.23) * mm});
            skLineSegment(sketch, "E767", {"start": v(-94.28, 13.23) * mm, "end": v(-93.48, 13.14) * mm});
            skLineSegment(sketch, "E768", {"start": v(-93.48, 13.14) * mm, "end": v(-92.7, 13.01) * mm});
            skLineSegment(sketch, "E769", {"start": v(-92.7, 13.01) * mm, "end": v(-91.94, 12.85) * mm});
            skLineSegment(sketch, "E770", {"start": v(-91.94, 12.85) * mm, "end": v(-91.2, 12.65) * mm});
            skLineSegment(sketch, "E771", {"start": v(-91.2, 12.65) * mm, "end": v(-90.46, 12.41) * mm});
            skLineSegment(sketch, "E772", {"start": v(-90.46, 12.41) * mm, "end": v(-89.75, 12.14) * mm});
            skLineSegment(sketch, "E773", {"start": v(-89.75, 12.14) * mm, "end": v(-89.05, 11.83) * mm});
            skLineSegment(sketch, "E774", {"start": v(-89.05, 11.83) * mm, "end": v(-88.36, 11.5) * mm});
            skLineSegment(sketch, "E775", {"start": v(-88.36, 11.5) * mm, "end": v(-87.7, 11.11) * mm});
            skLineSegment(sketch, "E776", {"start": v(-87.7, 11.11) * mm, "end": v(-87.04, 10.7) * mm});
            skLineSegment(sketch, "E777", {"start": v(-87.04, 10.7) * mm, "end": v(-86.4, 10.24) * mm});
            skLineSegment(sketch, "E778", {"start": v(-86.4, 10.24) * mm, "end": v(-85.8, 9.76) * mm});
            skLineSegment(sketch, "E779", {"start": v(-85.8, 9.76) * mm, "end": v(-85.19, 9.24) * mm});
            skLineSegment(sketch, "E780", {"start": v(-85.19, 9.24) * mm, "end": v(-84.6, 8.68) * mm});
            skLineSegment(sketch, "E781", {"start": v(-84.6, 8.68) * mm, "end": v(-84.05, 8.1) * mm});
            skLineSegment(sketch, "E782", {"start": v(-84.05, 8.1) * mm, "end": v(-83.52, 7.5) * mm});
            skLineSegment(sketch, "E783", {"start": v(-83.52, 7.5) * mm, "end": v(-83.04, 6.87) * mm});
            skLineSegment(sketch, "E784", {"start": v(-83.04, 6.87) * mm, "end": v(-82.59, 6.24) * mm});
            skLineSegment(sketch, "E785", {"start": v(-82.59, 6.24) * mm, "end": v(-82.17, 5.59) * mm});
            skLineSegment(sketch, "E786", {"start": v(-82.17, 5.59) * mm, "end": v(-81.8, 4.92) * mm});
            skLineSegment(sketch, "E787", {"start": v(-81.8, 4.92) * mm, "end": v(-81.45, 4.23) * mm});
            skLineSegment(sketch, "E788", {"start": v(-81.45, 4.23) * mm, "end": v(-81.14, 3.53) * mm});
            skLineSegment(sketch, "E789", {"start": v(-81.14, 3.53) * mm, "end": v(-80.87, 2.82) * mm});
            skLineSegment(sketch, "E790", {"start": v(-80.87, 2.82) * mm, "end": v(-80.63, 2.09) * mm});
            skLineSegment(sketch, "E791", {"start": v(-80.63, 2.09) * mm, "end": v(-80.43, 1.34) * mm});
            skLineSegment(sketch, "E792", {"start": v(-80.43, 1.34) * mm, "end": v(-80.27, 0.57) * mm});
            skLineSegment(sketch, "E793", {"start": v(-80.27, 0.57) * mm, "end": v(-80.14, -0.2) * mm});
            skLineSegment(sketch, "E794", {"start": v(-80.14, -0.2) * mm, "end": v(-80.05, -1) * mm});
            skLineSegment(sketch, "E795", {"start": v(-80.05, -1) * mm, "end": v(-80, -1.8) * mm});
            skLineSegment(sketch, "E796", {"start": v(-80, -1.8) * mm, "end": v(-79.98, -2.63) * mm});
            skLineSegment(sketch, "E797", {"start": v(-79.98, -2.63) * mm, "end": v(-80, -3.36) * mm});
            skLineSegment(sketch, "E798", {"start": v(-80, -3.36) * mm, "end": v(-80.04, -4.08) * mm});
            skLineSegment(sketch, "E799", {"start": v(-80.04, -4.08) * mm, "end": v(-80.12, -4.79) * mm});
            skLineSegment(sketch, "E800", {"start": v(-80.12, -4.79) * mm, "end": v(-80.22, -5.48) * mm});
            skLineSegment(sketch, "E801", {"start": v(-80.22, -5.48) * mm, "end": v(-80.36, -6.17) * mm});
            skLineSegment(sketch, "E802", {"start": v(-80.36, -6.17) * mm, "end": v(-80.53, -6.85) * mm});
            skLineSegment(sketch, "E803", {"start": v(-80.53, -6.85) * mm, "end": v(-80.73, -7.52) * mm});
            skLineSegment(sketch, "E804", {"start": v(-80.73, -7.52) * mm, "end": v(-80.96, -8.18) * mm});
            skLineSegment(sketch, "E805", {"start": v(-80.96, -8.18) * mm, "end": v(-81.22, -8.83) * mm});
            skLineSegment(sketch, "E806", {"start": v(-81.22, -8.83) * mm, "end": v(-81.5, -9.47) * mm});
            skLineSegment(sketch, "E807", {"start": v(-81.5, -9.47) * mm, "end": v(-81.83, -10.1) * mm});
            skLineSegment(sketch, "E808", {"start": v(-81.83, -10.1) * mm, "end": v(-82.18, -10.71) * mm});
            skLineSegment(sketch, "E809", {"start": v(-82.18, -10.71) * mm, "end": v(-82.56, -11.32) * mm});
            skLineSegment(sketch, "E810", {"start": v(-82.56, -11.32) * mm, "end": v(-82.97, -11.91) * mm});
            skLineSegment(sketch, "E811", {"start": v(-82.97, -11.91) * mm, "end": v(-83.41, -12.5) * mm});
            skLineSegment(sketch, "E812", {"start": v(-83.41, -12.5) * mm, "end": v(-83.88, -13.07) * mm});
            skLineSegment(sketch, "E813", {"start": v(-83.88, -13.07) * mm, "end": v(-84.38, -13.62) * mm});
            skLineSegment(sketch, "E814", {"start": v(-84.38, -13.62) * mm, "end": v(-84.89, -14.14) * mm});
            skLineSegment(sketch, "E815", {"start": v(-84.89, -14.14) * mm, "end": v(-85.41, -14.63) * mm});
            skLineSegment(sketch, "E816", {"start": v(-85.41, -14.63) * mm, "end": v(-85.95, -15.1) * mm});
            skLineSegment(sketch, "E817", {"start": v(-85.95, -15.1) * mm, "end": v(-86.51, -15.53) * mm});
            skLineSegment(sketch, "E818", {"start": v(-86.51, -15.53) * mm, "end": v(-87.09, -15.94) * mm});
            skLineSegment(sketch, "E819", {"start": v(-87.09, -15.94) * mm, "end": v(-87.67, -16.31) * mm});
            skLineSegment(sketch, "E820", {"start": v(-87.67, -16.31) * mm, "end": v(-88.28, -16.66) * mm});
            skLineSegment(sketch, "E821", {"start": v(-88.28, -16.66) * mm, "end": v(-88.9, -16.97) * mm});
            skLineSegment(sketch, "E822", {"start": v(-88.9, -16.97) * mm, "end": v(-89.53, -17.26) * mm});
            skLineSegment(sketch, "E823", {"start": v(-89.53, -17.26) * mm, "end": v(-90.18, -17.52) * mm});
            skLineSegment(sketch, "E824", {"start": v(-90.18, -17.52) * mm, "end": v(-90.85, -17.74) * mm});
            skLineSegment(sketch, "E825", {"start": v(-90.85, -17.74) * mm, "end": v(-91.52, -17.94) * mm});
            skLineSegment(sketch, "E826", {"start": v(-91.52, -17.94) * mm, "end": v(-92.22, -18.1) * mm});
            skLineSegment(sketch, "E827", {"start": v(-92.22, -18.1) * mm, "end": v(-92.93, -18.25) * mm});
            skLineSegment(sketch, "E828", {"start": v(-92.93, -18.25) * mm, "end": v(-93.65, -18.35) * mm});
            skLineSegment(sketch, "E829", {"start": v(-93.65, -18.35) * mm, "end": v(-93.78, -18.38) * mm});
            skLineSegment(sketch, "E830", {"start": v(-93.78, -18.38) * mm, "end": v(-93.92, -18.41) * mm});
            skLineSegment(sketch, "E831", {"start": v(-93.92, -18.41) * mm, "end": v(-94.04, -18.46) * mm});
            skLineSegment(sketch, "E832", {"start": v(-94.04, -18.46) * mm, "end": v(-94.17, -18.52) * mm});
            skLineSegment(sketch, "E833", {"start": v(-94.17, -18.52) * mm, "end": v(-94.28, -18.59) * mm});
            skLineSegment(sketch, "E834", {"start": v(-94.28, -18.59) * mm, "end": v(-94.39, -18.67) * mm});
            skLineSegment(sketch, "E835", {"start": v(-94.39, -18.67) * mm, "end": v(-94.49, -18.75) * mm});
            skLineSegment(sketch, "E836", {"start": v(-94.49, -18.75) * mm, "end": v(-94.58, -18.85) * mm});
            skLineSegment(sketch, "E837", {"start": v(-94.58, -18.85) * mm, "end": v(-94.66, -18.95) * mm});
            skLineSegment(sketch, "E838", {"start": v(-94.66, -18.95) * mm, "end": v(-94.74, -19.06) * mm});
            skLineSegment(sketch, "E839", {"start": v(-94.74, -19.06) * mm, "end": v(-94.8, -19.18) * mm});
            skLineSegment(sketch, "E840", {"start": v(-94.8, -19.18) * mm, "end": v(-94.85, -19.3) * mm});
            skLineSegment(sketch, "E841", {"start": v(-94.85, -19.3) * mm, "end": v(-94.9, -19.43) * mm});
            skLineSegment(sketch, "E842", {"start": v(-94.9, -19.43) * mm, "end": v(-94.93, -19.56) * mm});
            skLineSegment(sketch, "E843", {"start": v(-94.93, -19.56) * mm, "end": v(-94.95, -19.7) * mm});
            skLineSegment(sketch, "E844", {"start": v(-94.95, -19.7) * mm, "end": v(-94.95, -19.84) * mm});
            skLineSegment(sketch, "E845", {"start": v(-94.95, -19.84) * mm, "end": v(-94.95, -23.36) * mm});
            skLineSegment(sketch, "E846", {"start": v(-94.95, -23.36) * mm, "end": v(-94.94, -23.68) * mm});
            skLineSegment(sketch, "E847", {"start": v(-94.94, -23.68) * mm, "end": v(-94.89, -23.99) * mm});
            skLineSegment(sketch, "E848", {"start": v(-94.89, -23.99) * mm, "end": v(-94.81, -24.29) * mm});
            skLineSegment(sketch, "E849", {"start": v(-94.81, -24.29) * mm, "end": v(-94.7, -24.57) * mm});
            skLineSegment(sketch, "E850", {"start": v(-94.7, -24.57) * mm, "end": v(-94.57, -24.85) * mm});
            skLineSegment(sketch, "E851", {"start": v(-94.57, -24.85) * mm, "end": v(-94.42, -25.1) * mm});
            skLineSegment(sketch, "E852", {"start": v(-94.42, -25.1) * mm, "end": v(-94.24, -25.35) * mm});
            skLineSegment(sketch, "E853", {"start": v(-94.24, -25.35) * mm, "end": v(-94.03, -25.57) * mm});
            skLineSegment(sketch, "E854", {"start": v(-94.03, -25.57) * mm, "end": v(-93.81, -25.77) * mm});
            skLineSegment(sketch, "E855", {"start": v(-93.81, -25.77) * mm, "end": v(-93.57, -25.95) * mm});
            skLineSegment(sketch, "E856", {"start": v(-93.57, -25.95) * mm, "end": v(-93.31, -26.11) * mm});
            skLineSegment(sketch, "E857", {"start": v(-93.31, -26.11) * mm, "end": v(-93.04, -26.24) * mm});
            skLineSegment(sketch, "E858", {"start": v(-93.04, -26.24) * mm, "end": v(-92.75, -26.35) * mm});
            skLineSegment(sketch, "E859", {"start": v(-92.75, -26.35) * mm, "end": v(-92.45, -26.42) * mm});
            skLineSegment(sketch, "E860", {"start": v(-92.45, -26.42) * mm, "end": v(-92.14, -26.47) * mm});
            skLineSegment(sketch, "E861", {"start": v(-92.14, -26.47) * mm, "end": v(-91.82, -26.49) * mm});
            skLineSegment(sketch, "E862", {"start": v(-91.82, -26.49) * mm, "end": v(-73.1, -26.44) * mm});
            skLineSegment(sketch, "E863", {"start": v(-73.1, -26.44) * mm, "end": v(-72.89, -26.43) * mm});
            skLineSegment(sketch, "E864", {"start": v(-72.89, -26.43) * mm, "end": v(-72.68, -26.42) * mm});
            skLineSegment(sketch, "E865", {"start": v(-72.68, -26.42) * mm, "end": v(-72.48, -26.4) * mm});
            skLineSegment(sketch, "E866", {"start": v(-72.48, -26.4) * mm, "end": v(-72.28, -26.37) * mm});
            skLineSegment(sketch, "E867", {"start": v(-72.28, -26.37) * mm, "end": v(-72.08, -26.33) * mm});
            skLineSegment(sketch, "E868", {"start": v(-72.08, -26.33) * mm, "end": v(-71.9, -26.28) * mm});
            skLineSegment(sketch, "E869", {"start": v(-71.9, -26.28) * mm, "end": v(-71.71, -26.22) * mm});
            skLineSegment(sketch, "E870", {"start": v(-71.71, -26.22) * mm, "end": v(-71.53, -26.16) * mm});
            skLineSegment(sketch, "E871", {"start": v(-71.53, -26.16) * mm, "end": v(-71.36, -26.08) * mm});
            skLineSegment(sketch, "E872", {"start": v(-71.36, -26.08) * mm, "end": v(-71.19, -26) * mm});
            skLineSegment(sketch, "E873", {"start": v(-71.19, -26) * mm, "end": v(-71.02, -25.9) * mm});
            skLineSegment(sketch, "E874", {"start": v(-71.02, -25.9) * mm, "end": v(-70.86, -25.8) * mm});
            skLineSegment(sketch, "E875", {"start": v(-70.86, -25.8) * mm, "end": v(-70.71, -25.7) * mm});
            skLineSegment(sketch, "E876", {"start": v(-70.71, -25.7) * mm, "end": v(-70.56, -25.58) * mm});
            skLineSegment(sketch, "E877", {"start": v(-70.56, -25.58) * mm, "end": v(-70.42, -25.46) * mm});
            skLineSegment(sketch, "E878", {"start": v(-70.42, -25.46) * mm, "end": v(-70.28, -25.32) * mm});
            skLineSegment(sketch, "E879", {"start": v(-70.28, -25.32) * mm, "end": v(-70.15, -25.18) * mm});
            skLineSegment(sketch, "E880", {"start": v(-70.15, -25.18) * mm, "end": v(-70.03, -25.03) * mm});
            skLineSegment(sketch, "E881", {"start": v(-70.03, -25.03) * mm, "end": v(-69.91, -24.88) * mm});
            skLineSegment(sketch, "E882", {"start": v(-69.91, -24.88) * mm, "end": v(-69.8, -24.73) * mm});
            skLineSegment(sketch, "E883", {"start": v(-69.8, -24.73) * mm, "end": v(-69.7, -24.56) * mm});
            skLineSegment(sketch, "E884", {"start": v(-69.7, -24.56) * mm, "end": v(-69.62, -24.4) * mm});
            skLineSegment(sketch, "E885", {"start": v(-69.62, -24.4) * mm, "end": v(-69.54, -24.23) * mm});
            skLineSegment(sketch, "E886", {"start": v(-69.54, -24.23) * mm, "end": v(-69.47, -24.05) * mm});
            skLineSegment(sketch, "E887", {"start": v(-69.47, -24.05) * mm, "end": v(-69.4, -23.87) * mm});
            skLineSegment(sketch, "E888", {"start": v(-69.4, -23.87) * mm, "end": v(-69.35, -23.69) * mm});
            skLineSegment(sketch, "E889", {"start": v(-69.35, -23.69) * mm, "end": v(-69.3, -23.5) * mm});
            skLineSegment(sketch, "E890", {"start": v(-69.3, -23.5) * mm, "end": v(-69.26, -23.3) * mm});
            skLineSegment(sketch, "E891", {"start": v(-69.26, -23.3) * mm, "end": v(-69.23, -23.1) * mm});
            skLineSegment(sketch, "E892", {"start": v(-69.23, -23.1) * mm, "end": v(-69.21, -22.9) * mm});
            skLineSegment(sketch, "E893", {"start": v(-69.21, -22.9) * mm, "end": v(-69.2, -22.69) * mm});
            skLineSegment(sketch, "E894", {"start": v(-69.2, -22.69) * mm, "end": v(-69.2, -22.47) * mm});
            skLineSegment(sketch, "E895", {"start": v(-69.2, -22.47) * mm, "end": v(-69.2, 6.62) * mm});
            skLineSegment(sketch, "E896", {"start": v(-69.2, 6.62) * mm, "end": v(-69.2, 6.66) * mm});
            skLineSegment(sketch, "E897", {"start": v(-69.2, 6.66) * mm, "end": v(-69.18, 6.7) * mm});
            skLineSegment(sketch, "E898", {"start": v(-69.18, 6.7) * mm, "end": v(-69.17, 6.74) * mm});
            skLineSegment(sketch, "E899", {"start": v(-69.17, 6.74) * mm, "end": v(-69.16, 6.78) * mm});
            skLineSegment(sketch, "E900", {"start": v(-69.16, 6.78) * mm, "end": v(-69.14, 6.81) * mm});
            skLineSegment(sketch, "E901", {"start": v(-69.14, 6.81) * mm, "end": v(-69.12, 6.84) * mm});
            skLineSegment(sketch, "E902", {"start": v(-69.12, 6.84) * mm, "end": v(-69.1, 6.87) * mm});
            skLineSegment(sketch, "E903", {"start": v(-69.1, 6.87) * mm, "end": v(-69.07, 6.9) * mm});
            skLineSegment(sketch, "E904", {"start": v(-69.07, 6.9) * mm, "end": v(-69.05, 6.92) * mm});
            skLineSegment(sketch, "E905", {"start": v(-69.05, 6.92) * mm, "end": v(-69.02, 6.93) * mm});
            skLineSegment(sketch, "E906", {"start": v(-69.02, 6.93) * mm, "end": v(-68.99, 6.95) * mm});
            skLineSegment(sketch, "E907", {"start": v(-68.99, 6.95) * mm, "end": v(-68.95, 6.96) * mm});
            skLineSegment(sketch, "E908", {"start": v(-68.95, 6.96) * mm, "end": v(-68.92, 6.98) * mm});
            skLineSegment(sketch, "E909", {"start": v(-68.92, 6.98) * mm, "end": v(-68.89, 6.98) * mm});
            skLineSegment(sketch, "E910", {"start": v(-68.89, 6.98) * mm, "end": v(-68.85, 6.99) * mm});
            skLineSegment(sketch, "E911", {"start": v(-68.85, 6.99) * mm, "end": v(-68.82, 6.99) * mm});
            skLineSegment(sketch, "E912", {"start": v(-68.82, 6.99) * mm, "end": v(-68.8, 6.99) * mm});
            skLineSegment(sketch, "E913", {"start": v(-68.8, 6.99) * mm, "end": v(-68.77, 6.99) * mm});
            skLineSegment(sketch, "E914", {"start": v(-68.77, 6.99) * mm, "end": v(-68.74, 6.98) * mm});
            skLineSegment(sketch, "E915", {"start": v(-68.74, 6.98) * mm, "end": v(-68.72, 6.97) * mm});
            skLineSegment(sketch, "E916", {"start": v(-68.72, 6.97) * mm, "end": v(-68.7, 6.97) * mm});
            skLineSegment(sketch, "E917", {"start": v(-68.7, 6.97) * mm, "end": v(-68.67, 6.96) * mm});
            skLineSegment(sketch, "E918", {"start": v(-68.67, 6.96) * mm, "end": v(-68.65, 6.95) * mm});
            skLineSegment(sketch, "E919", {"start": v(-68.65, 6.95) * mm, "end": v(-68.63, 6.94) * mm});
            skLineSegment(sketch, "E920", {"start": v(-68.63, 6.94) * mm, "end": v(-68.6, 6.92) * mm});
            skLineSegment(sketch, "E921", {"start": v(-68.6, 6.92) * mm, "end": v(-68.6, 6.9) * mm});
            skLineSegment(sketch, "E922", {"start": v(-68.6, 6.9) * mm, "end": v(-68.57, 6.89) * mm});
            skLineSegment(sketch, "E923", {"start": v(-68.57, 6.89) * mm, "end": v(-68.55, 6.87) * mm});
            skLineSegment(sketch, "E924", {"start": v(-68.55, 6.87) * mm, "end": v(-68.54, 6.85) * mm});
            skLineSegment(sketch, "E925", {"start": v(-68.54, 6.85) * mm, "end": v(-68.52, 6.83) * mm});
            skLineSegment(sketch, "E926", {"start": v(-68.52, 6.83) * mm, "end": v(-68.5, 6.8) * mm});
            skLineSegment(sketch, "E927", {"start": v(-68.5, 6.8) * mm, "end": v(-68.5, 6.79) * mm});
            skLineSegment(sketch, "E928", {"start": v(-68.5, 6.79) * mm, "end": v(-52.2, -25.59) * mm});
            skLineSegment(sketch, "E929", {"start": v(-52.2, -25.59) * mm, "end": v(-52.14, -25.69) * mm});
            skLineSegment(sketch, "E930", {"start": v(-52.14, -25.69) * mm, "end": v(-52.08, -25.78) * mm});
            skLineSegment(sketch, "E931", {"start": v(-52.08, -25.78) * mm, "end": v(-52, -25.88) * mm});
            skLineSegment(sketch, "E932", {"start": v(-52, -25.88) * mm, "end": v(-51.93, -25.96) * mm});
            skLineSegment(sketch, "E933", {"start": v(-51.93, -25.96) * mm, "end": v(-51.86, -26.04) * mm});
            skLineSegment(sketch, "E934", {"start": v(-51.86, -26.04) * mm, "end": v(-51.77, -26.12) * mm});
            skLineSegment(sketch, "E935", {"start": v(-51.77, -26.12) * mm, "end": v(-51.68, -26.18) * mm});
            skLineSegment(sketch, "E936", {"start": v(-51.68, -26.18) * mm, "end": v(-51.6, -26.25) * mm});
            skLineSegment(sketch, "E937", {"start": v(-51.6, -26.25) * mm, "end": v(-51.5, -26.3) * mm});
            skLineSegment(sketch, "E938", {"start": v(-51.5, -26.3) * mm, "end": v(-51.4, -26.35) * mm});
            skLineSegment(sketch, "E939", {"start": v(-51.4, -26.35) * mm, "end": v(-51.29, -26.4) * mm});
            skLineSegment(sketch, "E940", {"start": v(-51.29, -26.4) * mm, "end": v(-51.18, -26.43) * mm});
            skLineSegment(sketch, "E941", {"start": v(-51.18, -26.43) * mm, "end": v(-51.07, -26.45) * mm});
            skLineSegment(sketch, "E942", {"start": v(-51.07, -26.45) * mm, "end": v(-50.96, -26.47) * mm});
            skLineSegment(sketch, "E943", {"start": v(-50.96, -26.47) * mm, "end": v(-50.85, -26.48) * mm});
            skLineSegment(sketch, "E944", {"start": v(-50.85, -26.48) * mm, "end": v(-50.73, -26.49) * mm});
            skLineSegment(sketch, "E945", {"start": v(-50.73, -26.49) * mm, "end": v(-50.6, -26.48) * mm});
            skLineSegment(sketch, "E946", {"start": v(-50.6, -26.48) * mm, "end": v(-50.46, -26.46) * mm});
            skLineSegment(sketch, "E947", {"start": v(-50.46, -26.46) * mm, "end": v(-50.34, -26.43) * mm});
            skLineSegment(sketch, "E948", {"start": v(-50.34, -26.43) * mm, "end": v(-50.21, -26.38) * mm});
            skLineSegment(sketch, "E949", {"start": v(-50.21, -26.38) * mm, "end": v(-50.1, -26.33) * mm});
            skLineSegment(sketch, "E950", {"start": v(-50.1, -26.33) * mm, "end": v(-49.99, -26.26) * mm});
            skLineSegment(sketch, "E951", {"start": v(-49.99, -26.26) * mm, "end": v(-49.89, -26.19) * mm});
            skLineSegment(sketch, "E952", {"start": v(-49.89, -26.19) * mm, "end": v(-49.8, -26.1) * mm});
            skLineSegment(sketch, "E953", {"start": v(-49.8, -26.1) * mm, "end": v(-49.7, -26) * mm});
            skLineSegment(sketch, "E954", {"start": v(-49.7, -26) * mm, "end": v(-49.63, -25.9) * mm});
            skLineSegment(sketch, "E955", {"start": v(-49.63, -25.9) * mm, "end": v(-49.56, -25.8) * mm});
            skLineSegment(sketch, "E956", {"start": v(-49.56, -25.8) * mm, "end": v(-49.5, -25.68) * mm});
            skLineSegment(sketch, "E957", {"start": v(-49.5, -25.68) * mm, "end": v(-49.46, -25.56) * mm});
            skLineSegment(sketch, "E958", {"start": v(-49.46, -25.56) * mm, "end": v(-49.43, -25.43) * mm});
            skLineSegment(sketch, "E959", {"start": v(-49.43, -25.43) * mm, "end": v(-49.4, -25.3) * mm});
            skLineSegment(sketch, "E960", {"start": v(-49.4, -25.3) * mm, "end": v(-49.4, -25.16) * mm});
            skLineSegment(sketch, "E961", {"start": v(-49.4, -25.16) * mm, "end": v(-49.4, 11.98) * mm});
            skLineSegment(sketch, "E962", {"start": v(-49.4, 11.98) * mm, "end": v(-49.4, 12.1) * mm});
            skLineSegment(sketch, "E963", {"start": v(-49.4, 12.1) * mm, "end": v(-49.39, 12.22) * mm});
            skLineSegment(sketch, "E964", {"start": v(-49.39, 12.22) * mm, "end": v(-49.37, 12.33) * mm});
            skLineSegment(sketch, "E965", {"start": v(-49.37, 12.33) * mm, "end": v(-49.35, 12.43) * mm});
            skLineSegment(sketch, "E966", {"start": v(-49.35, 12.43) * mm, "end": v(-49.31, 12.52) * mm});
            skLineSegment(sketch, "E967", {"start": v(-49.31, 12.52) * mm, "end": v(-49.28, 12.6) * mm});
            skLineSegment(sketch, "E968", {"start": v(-49.28, 12.6) * mm, "end": v(-49.23, 12.67) * mm});
            skLineSegment(sketch, "E969", {"start": v(-49.23, 12.67) * mm, "end": v(-49.17, 12.74) * mm});
            skLineSegment(sketch, "E970", {"start": v(-49.17, 12.74) * mm, "end": v(-49.11, 12.8) * mm});
            skLineSegment(sketch, "E971", {"start": v(-49.11, 12.8) * mm, "end": v(-49.04, 12.85) * mm});
            skLineSegment(sketch, "E972", {"start": v(-49.04, 12.85) * mm, "end": v(-48.97, 12.9) * mm});
            skLineSegment(sketch, "E973", {"start": v(-48.97, 12.9) * mm, "end": v(-48.88, 12.93) * mm});
            skLineSegment(sketch, "E974", {"start": v(-48.88, 12.93) * mm, "end": v(-48.8, 12.95) * mm});
            skLineSegment(sketch, "E975", {"start": v(-48.8, 12.95) * mm, "end": v(-48.7, 12.97) * mm});
            skLineSegment(sketch, "E976", {"start": v(-48.7, 12.97) * mm, "end": v(-48.59, 12.98) * mm});
            skLineSegment(sketch, "E977", {"start": v(-48.59, 12.98) * mm, "end": v(-48.47, 12.99) * mm});
            skLineSegment(sketch, "E978", {"start": v(-48.47, 12.99) * mm, "end": v(-48.35, 12.98) * mm});
            skLineSegment(sketch, "E979", {"start": v(-48.35, 12.98) * mm, "end": v(-48.23, 12.97) * mm});
            skLineSegment(sketch, "E980", {"start": v(-48.23, 12.97) * mm, "end": v(-48.13, 12.95) * mm});
            skLineSegment(sketch, "E981", {"start": v(-48.13, 12.95) * mm, "end": v(-48.03, 12.93) * mm});
            skLineSegment(sketch, "E982", {"start": v(-48.03, 12.93) * mm, "end": v(-47.94, 12.9) * mm});
            skLineSegment(sketch, "E983", {"start": v(-47.94, 12.9) * mm, "end": v(-47.86, 12.85) * mm});
            skLineSegment(sketch, "E984", {"start": v(-47.86, 12.85) * mm, "end": v(-47.8, 12.8) * mm});
            skLineSegment(sketch, "E985", {"start": v(-47.8, 12.8) * mm, "end": v(-47.73, 12.74) * mm});
            skLineSegment(sketch, "E986", {"start": v(-47.73, 12.74) * mm, "end": v(-47.67, 12.67) * mm});
            skLineSegment(sketch, "E987", {"start": v(-47.67, 12.67) * mm, "end": v(-47.62, 12.6) * mm});
            skLineSegment(sketch, "E988", {"start": v(-47.62, 12.6) * mm, "end": v(-47.58, 12.52) * mm});
            skLineSegment(sketch, "E989", {"start": v(-47.58, 12.52) * mm, "end": v(-47.55, 12.43) * mm});
            skLineSegment(sketch, "E990", {"start": v(-47.55, 12.43) * mm, "end": v(-47.52, 12.33) * mm});
            skLineSegment(sketch, "E991", {"start": v(-47.52, 12.33) * mm, "end": v(-47.5, 12.22) * mm});
            skLineSegment(sketch, "E992", {"start": v(-47.5, 12.22) * mm, "end": v(-47.49, 12.1) * mm});
            skLineSegment(sketch, "E993", {"start": v(-47.49, 12.1) * mm, "end": v(-47.49, 11.98) * mm});
            skLineSegment(sketch, "E994", {"start": v(-47.49, 11.98) * mm, "end": v(-47.49, -22.43) * mm});
            skLineSegment(sketch, "E995", {"start": v(-47.49, -22.43) * mm, "end": v(-47.47, -22.85) * mm});
            skLineSegment(sketch, "E996", {"start": v(-47.47, -22.85) * mm, "end": v(-47.42, -23.26) * mm});
            skLineSegment(sketch, "E997", {"start": v(-47.42, -23.26) * mm, "end": v(-47.35, -23.64) * mm});
            skLineSegment(sketch, "E998", {"start": v(-47.35, -23.64) * mm, "end": v(-47.24, -24) * mm});
            skLineSegment(sketch, "E999", {"start": v(-47.24, -24) * mm, "end": v(-47.1, -24.32) * mm});
            skLineSegment(sketch, "E1000", {"start": v(-47.1, -24.32) * mm, "end": v(-46.93, -24.63) * mm});
            skLineSegment(sketch, "E1001", {"start": v(-46.93, -24.63) * mm, "end": v(-46.73, -24.91) * mm});
            skLineSegment(sketch, "E1002", {"start": v(-46.73, -24.91) * mm, "end": v(-46.5, -25.17) * mm});
            skLineSegment(sketch, "E1003", {"start": v(-46.5, -25.17) * mm, "end": v(-46.24, -25.4) * mm});
            skLineSegment(sketch, "E1004", {"start": v(-46.24, -25.4) * mm, "end": v(-45.95, -25.62) * mm});
            skLineSegment(sketch, "E1005", {"start": v(-45.95, -25.62) * mm, "end": v(-45.63, -25.8) * mm});
            skLineSegment(sketch, "E1006", {"start": v(-45.63, -25.8) * mm, "end": v(-45.28, -25.97) * mm});
            skLineSegment(sketch, "E1007", {"start": v(-45.28, -25.97) * mm, "end": v(-44.9, -26.11) * mm});
            skLineSegment(sketch, "E1008", {"start": v(-44.9, -26.11) * mm, "end": v(-44.49, -26.23) * mm});
            skLineSegment(sketch, "E1009", {"start": v(-44.49, -26.23) * mm, "end": v(-44.04, -26.32) * mm});
            skLineSegment(sketch, "E1010", {"start": v(-44.04, -26.32) * mm, "end": v(-43.57, -26.38) * mm});
            skLineSegment(sketch, "E1011", {"start": v(-43.57, -26.38) * mm, "end": v(-40.67, -26.49) * mm});
            skLineSegment(sketch, "E1012", {"start": v(-40.67, -26.49) * mm, "end": v(-40.45, -26.48) * mm});
            skLineSegment(sketch, "E1013", {"start": v(-40.45, -26.48) * mm, "end": v(-40.24, -26.47) * mm});
            skLineSegment(sketch, "E1014", {"start": v(-40.24, -26.47) * mm, "end": v(-40.04, -26.45) * mm});
            skLineSegment(sketch, "E1015", {"start": v(-40.04, -26.45) * mm, "end": v(-39.84, -26.42) * mm});
            skLineSegment(sketch, "E1016", {"start": v(-39.84, -26.42) * mm, "end": v(-39.64, -26.38) * mm});
            skLineSegment(sketch, "E1017", {"start": v(-39.64, -26.38) * mm, "end": v(-39.45, -26.33) * mm});
            skLineSegment(sketch, "E1018", {"start": v(-39.45, -26.33) * mm, "end": v(-39.27, -26.27) * mm});
            skLineSegment(sketch, "E1019", {"start": v(-39.27, -26.27) * mm, "end": v(-39.09, -26.2) * mm});
            skLineSegment(sketch, "E1020", {"start": v(-39.09, -26.2) * mm, "end": v(-38.91, -26.13) * mm});
            skLineSegment(sketch, "E1021", {"start": v(-38.91, -26.13) * mm, "end": v(-38.74, -26.05) * mm});
            skLineSegment(sketch, "E1022", {"start": v(-38.74, -26.05) * mm, "end": v(-38.57, -25.96) * mm});
            skLineSegment(sketch, "E1023", {"start": v(-38.57, -25.96) * mm, "end": v(-38.41, -25.86) * mm});
            skLineSegment(sketch, "E1024", {"start": v(-38.41, -25.86) * mm, "end": v(-38.26, -25.75) * mm});
            skLineSegment(sketch, "E1025", {"start": v(-38.26, -25.75) * mm, "end": v(-38.1, -25.63) * mm});
            skLineSegment(sketch, "E1026", {"start": v(-38.1, -25.63) * mm, "end": v(-37.96, -25.5) * mm});
            skLineSegment(sketch, "E1027", {"start": v(-37.96, -25.5) * mm, "end": v(-37.82, -25.37) * mm});
            skLineSegment(sketch, "E1028", {"start": v(-37.82, -25.37) * mm, "end": v(-37.68, -25.23) * mm});
            skLineSegment(sketch, "E1029", {"start": v(-37.68, -25.23) * mm, "end": v(-37.56, -25.09) * mm});
            skLineSegment(sketch, "E1030", {"start": v(-37.56, -25.09) * mm, "end": v(-37.44, -24.94) * mm});
            skLineSegment(sketch, "E1031", {"start": v(-37.44, -24.94) * mm, "end": v(-37.33, -24.78) * mm});
            skLineSegment(sketch, "E1032", {"start": v(-37.33, -24.78) * mm, "end": v(-37.23, -24.62) * mm});
            skLineSegment(sketch, "E1033", {"start": v(-37.23, -24.62) * mm, "end": v(-37.14, -24.45) * mm});
            skLineSegment(sketch, "E1034", {"start": v(-37.14, -24.45) * mm, "end": v(-37.06, -24.28) * mm});
            skLineSegment(sketch, "E1035", {"start": v(-37.06, -24.28) * mm, "end": v(-36.98, -24.1) * mm});
            skLineSegment(sketch, "E1036", {"start": v(-36.98, -24.1) * mm, "end": v(-36.92, -23.92) * mm});
            skLineSegment(sketch, "E1037", {"start": v(-36.92, -23.92) * mm, "end": v(-36.86, -23.74) * mm});
            skLineSegment(sketch, "E1038", {"start": v(-36.86, -23.74) * mm, "end": v(-36.81, -23.55) * mm});
            skLineSegment(sketch, "E1039", {"start": v(-36.81, -23.55) * mm, "end": v(-36.77, -23.35) * mm});
            skLineSegment(sketch, "E1040", {"start": v(-36.77, -23.35) * mm, "end": v(-36.74, -23.15) * mm});
            skLineSegment(sketch, "E1041", {"start": v(-36.74, -23.15) * mm, "end": v(-36.72, -22.95) * mm});
            skLineSegment(sketch, "E1042", {"start": v(-36.72, -22.95) * mm, "end": v(-36.7, -22.74) * mm});
            skLineSegment(sketch, "E1043", {"start": v(-36.7, -22.74) * mm, "end": v(-36.7, -22.53) * mm});
            skLineSegment(sketch, "E1044", {"start": v(-36.7, -22.53) * mm, "end": v(-36.7, 12.27) * mm});
            skLineSegment(sketch, "E1045", {"start": v(-36.7, 12.27) * mm, "end": v(-36.7, 12.34) * mm});
            skLineSegment(sketch, "E1046", {"start": v(-36.7, 12.34) * mm, "end": v(-36.69, 12.42) * mm});
            skLineSegment(sketch, "E1047", {"start": v(-36.69, 12.42) * mm, "end": v(-36.67, 12.5) * mm});
            skLineSegment(sketch, "E1048", {"start": v(-36.67, 12.5) * mm, "end": v(-36.64, 12.57) * mm});
            skLineSegment(sketch, "E1049", {"start": v(-36.64, 12.57) * mm, "end": v(-36.6, 12.63) * mm});
            skLineSegment(sketch, "E1050", {"start": v(-36.6, 12.63) * mm, "end": v(-36.57, 12.7) * mm});
            skLineSegment(sketch, "E1051", {"start": v(-36.57, 12.7) * mm, "end": v(-36.53, 12.76) * mm});
            skLineSegment(sketch, "E1052", {"start": v(-36.53, 12.76) * mm, "end": v(-36.48, 12.81) * mm});
            skLineSegment(sketch, "E1053", {"start": v(-36.48, 12.81) * mm, "end": v(-36.42, 12.86) * mm});
            skLineSegment(sketch, "E1054", {"start": v(-36.42, 12.86) * mm, "end": v(-36.36, 12.9) * mm});
            skLineSegment(sketch, "E1055", {"start": v(-36.36, 12.9) * mm, "end": v(-36.3, 12.95) * mm});
            skLineSegment(sketch, "E1056", {"start": v(-36.3, 12.95) * mm, "end": v(-36.23, 12.98) * mm});
            skLineSegment(sketch, "E1057", {"start": v(-36.23, 12.98) * mm, "end": v(-36.16, 13) * mm});
            skLineSegment(sketch, "E1058", {"start": v(-36.16, 13) * mm, "end": v(-36.08, 13.02) * mm});
            skLineSegment(sketch, "E1059", {"start": v(-36.08, 13.02) * mm, "end": v(-36, 13.04) * mm});
            skLineSegment(sketch, "E1060", {"start": v(-36, 13.04) * mm, "end": v(-35.93, 13.04) * mm});
            skLineSegment(sketch, "E1061", {"start": v(-35.93, 13.04) * mm, "end": v(-23.09, 13.04) * mm});
            skLineSegment(sketch, "E1062", {"start": v(-23.09, 13.04) * mm, "end": v(-22.82, 13.02) * mm});
            skLineSegment(sketch, "E1063", {"start": v(-22.82, 13.02) * mm, "end": v(-22.54, 13) * mm});
            skLineSegment(sketch, "E1064", {"start": v(-22.54, 13) * mm, "end": v(-22.27, 12.97) * mm});
            skLineSegment(sketch, "E1065", {"start": v(-22.27, 12.97) * mm, "end": v(-22, 12.93) * mm});
            skLineSegment(sketch, "E1066", {"start": v(-22, 12.93) * mm, "end": v(-21.72, 12.88) * mm});
            skLineSegment(sketch, "E1067", {"start": v(-21.72, 12.88) * mm, "end": v(-21.45, 12.83) * mm});
            skLineSegment(sketch, "E1068", {"start": v(-21.45, 12.83) * mm, "end": v(-21.18, 12.76) * mm});
            skLineSegment(sketch, "E1069", {"start": v(-21.18, 12.76) * mm, "end": v(-20.9, 12.7) * mm});
            skLineSegment(sketch, "E1070", {"start": v(-20.9, 12.7) * mm, "end": v(-20.63, 12.6) * mm});
            skLineSegment(sketch, "E1071", {"start": v(-20.63, 12.6) * mm, "end": v(-20.36, 12.52) * mm});
            skLineSegment(sketch, "E1072", {"start": v(-20.36, 12.52) * mm, "end": v(-20.1, 12.42) * mm});
            skLineSegment(sketch, "E1073", {"start": v(-20.1, 12.42) * mm, "end": v(-19.82, 12.31) * mm});
            skLineSegment(sketch, "E1074", {"start": v(-19.82, 12.31) * mm, "end": v(-19.55, 12.2) * mm});
            skLineSegment(sketch, "E1075", {"start": v(-19.55, 12.2) * mm, "end": v(-19.28, 12.07) * mm});
            skLineSegment(sketch, "E1076", {"start": v(-19.28, 12.07) * mm, "end": v(-19.02, 11.94) * mm});
            skLineSegment(sketch, "E1077", {"start": v(-19.02, 11.94) * mm, "end": v(-18.53, 11.67) * mm});
            skLineSegment(sketch, "E1078", {"start": v(-18.53, 11.67) * mm, "end": v(-18.08, 11.37) * mm});
            skLineSegment(sketch, "E1079", {"start": v(-18.08, 11.37) * mm, "end": v(-17.65, 11.05) * mm});
            skLineSegment(sketch, "E1080", {"start": v(-17.65, 11.05) * mm, "end": v(-17.26, 10.7) * mm});
            skLineSegment(sketch, "E1081", {"start": v(-17.26, 10.7) * mm, "end": v(-16.9, 10.33) * mm});
            skLineSegment(sketch, "E1082", {"start": v(-16.9, 10.33) * mm, "end": v(-16.57, 9.94) * mm});
            skLineSegment(sketch, "E1083", {"start": v(-16.57, 9.94) * mm, "end": v(-16.27, 9.52) * mm});
            skLineSegment(sketch, "E1084", {"start": v(-16.27, 9.52) * mm, "end": v(-16, 9.08) * mm});
            skLineSegment(sketch, "E1085", {"start": v(-16, 9.08) * mm, "end": v(-15.77, 8.6) * mm});
            skLineSegment(sketch, "E1086", {"start": v(-15.77, 8.6) * mm, "end": v(-15.56, 8.12) * mm});
            skLineSegment(sketch, "E1087", {"start": v(-15.56, 8.12) * mm, "end": v(-15.4, 7.6) * mm});
            skLineSegment(sketch, "E1088", {"start": v(-15.4, 7.6) * mm, "end": v(-15.25, 7.06) * mm});
            skLineSegment(sketch, "E1089", {"start": v(-15.25, 7.06) * mm, "end": v(-15.14, 6.5) * mm});
            skLineSegment(sketch, "E1090", {"start": v(-15.14, 6.5) * mm, "end": v(-15.06, 5.92) * mm});
            skLineSegment(sketch, "E1091", {"start": v(-15.06, 5.92) * mm, "end": v(-15.01, 5.3) * mm});
            skLineSegment(sketch, "E1092", {"start": v(-15.01, 5.3) * mm, "end": v(-15, 4.67) * mm});
            skLineSegment(sketch, "E1093", {"start": v(-15, 4.67) * mm, "end": v(-15.01, 4.04) * mm});
            skLineSegment(sketch, "E1094", {"start": v(-15.01, 4.04) * mm, "end": v(-15.06, 3.43) * mm});
            skLineSegment(sketch, "E1095", {"start": v(-15.06, 3.43) * mm, "end": v(-15.14, 2.85) * mm});
            skLineSegment(sketch, "E1096", {"start": v(-15.14, 2.85) * mm, "end": v(-15.25, 2.28) * mm});
            skLineSegment(sketch, "E1097", {"start": v(-15.25, 2.28) * mm, "end": v(-15.4, 1.74) * mm});
            skLineSegment(sketch, "E1098", {"start": v(-15.4, 1.74) * mm, "end": v(-15.56, 1.23) * mm});
            skLineSegment(sketch, "E1099", {"start": v(-15.56, 1.23) * mm, "end": v(-15.77, 0.74) * mm});
            skLineSegment(sketch, "E1100", {"start": v(-15.77, 0.74) * mm, "end": v(-16, 0.27) * mm});
            skLineSegment(sketch, "E1101", {"start": v(-16, 0.27) * mm, "end": v(-16.27, -0.17) * mm});
            skLineSegment(sketch, "E1102", {"start": v(-16.27, -0.17) * mm, "end": v(-16.57, -0.6) * mm});
            skLineSegment(sketch, "E1103", {"start": v(-16.57, -0.6) * mm, "end": v(-16.9, -0.99) * mm});
            skLineSegment(sketch, "E1104", {"start": v(-16.9, -0.99) * mm, "end": v(-17.26, -1.36) * mm});
            skLineSegment(sketch, "E1105", {"start": v(-17.26, -1.36) * mm, "end": v(-17.65, -1.7) * mm});
            skLineSegment(sketch, "E1106", {"start": v(-17.65, -1.7) * mm, "end": v(-18.08, -2.02) * mm});
            skLineSegment(sketch, "E1107", {"start": v(-18.08, -2.02) * mm, "end": v(-18.53, -2.32) * mm});
            skLineSegment(sketch, "E1108", {"start": v(-18.53, -2.32) * mm, "end": v(-19.02, -2.6) * mm});
            skLineSegment(sketch, "E1109", {"start": v(-19.02, -2.6) * mm, "end": v(-19.3, -2.73) * mm});
            skLineSegment(sketch, "E1110", {"start": v(-19.3, -2.73) * mm, "end": v(-19.57, -2.86) * mm});
            skLineSegment(sketch, "E1111", {"start": v(-19.57, -2.86) * mm, "end": v(-19.85, -2.98) * mm});
            skLineSegment(sketch, "E1112", {"start": v(-19.85, -2.98) * mm, "end": v(-20.13, -3.1) * mm});
            skLineSegment(sketch, "E1113", {"start": v(-20.13, -3.1) * mm, "end": v(-20.4, -3.2) * mm});
            skLineSegment(sketch, "E1114", {"start": v(-20.4, -3.2) * mm, "end": v(-20.68, -3.3) * mm});
            skLineSegment(sketch, "E1115", {"start": v(-20.68, -3.3) * mm, "end": v(-20.96, -3.38) * mm});
            skLineSegment(sketch, "E1116", {"start": v(-20.96, -3.38) * mm, "end": v(-21.23, -3.46) * mm});
            skLineSegment(sketch, "E1117", {"start": v(-21.23, -3.46) * mm, "end": v(-21.5, -3.52) * mm});
            skLineSegment(sketch, "E1118", {"start": v(-21.5, -3.52) * mm, "end": v(-21.77, -3.58) * mm});
            skLineSegment(sketch, "E1119", {"start": v(-21.77, -3.58) * mm, "end": v(-22.04, -3.63) * mm});
            skLineSegment(sketch, "E1120", {"start": v(-22.04, -3.63) * mm, "end": v(-22.3, -3.67) * mm});
            skLineSegment(sketch, "E1121", {"start": v(-22.3, -3.67) * mm, "end": v(-22.57, -3.7) * mm});
            skLineSegment(sketch, "E1122", {"start": v(-22.57, -3.7) * mm, "end": v(-22.84, -3.73) * mm});
            skLineSegment(sketch, "E1123", {"start": v(-22.84, -3.73) * mm, "end": v(-23.1, -3.74) * mm});
            skLineSegment(sketch, "E1124", {"start": v(-23.1, -3.74) * mm, "end": v(-33.04, -3.75) * mm});
            skLineSegment(sketch, "E1125", {"start": v(-33.04, -3.75) * mm, "end": v(-33.16, -3.75) * mm});
            skLineSegment(sketch, "E1126", {"start": v(-33.16, -3.75) * mm, "end": v(-33.27, -3.77) * mm});
            skLineSegment(sketch, "E1127", {"start": v(-33.27, -3.77) * mm, "end": v(-33.39, -3.8) * mm});
            skLineSegment(sketch, "E1128", {"start": v(-33.39, -3.8) * mm, "end": v(-33.5, -3.84) * mm});
            skLineSegment(sketch, "E1129", {"start": v(-33.5, -3.84) * mm, "end": v(-33.6, -3.89) * mm});
            skLineSegment(sketch, "E1130", {"start": v(-33.6, -3.89) * mm, "end": v(-33.7, -3.95) * mm});
            skLineSegment(sketch, "E1131", {"start": v(-33.7, -3.95) * mm, "end": v(-33.78, -4.01) * mm});
            skLineSegment(sketch, "E1132", {"start": v(-33.78, -4.01) * mm, "end": v(-33.86, -4.09) * mm});
            skLineSegment(sketch, "E1133", {"start": v(-33.86, -4.09) * mm, "end": v(-33.94, -4.17) * mm});
            skLineSegment(sketch, "E1134", {"start": v(-33.94, -4.17) * mm, "end": v(-34, -4.26) * mm});
            skLineSegment(sketch, "E1135", {"start": v(-34, -4.26) * mm, "end": v(-34.06, -4.36) * mm});
            skLineSegment(sketch, "E1136", {"start": v(-34.06, -4.36) * mm, "end": v(-34.11, -4.46) * mm});
            skLineSegment(sketch, "E1137", {"start": v(-34.11, -4.46) * mm, "end": v(-34.15, -4.57) * mm});
            skLineSegment(sketch, "E1138", {"start": v(-34.15, -4.57) * mm, "end": v(-34.18, -4.68) * mm});
            skLineSegment(sketch, "E1139", {"start": v(-34.18, -4.68) * mm, "end": v(-34.2, -4.8) * mm});
            skLineSegment(sketch, "E1140", {"start": v(-34.2, -4.8) * mm, "end": v(-34.2, -4.91) * mm});
            skLineSegment(sketch, "E1141", {"start": v(-34.2, -4.91) * mm, "end": v(-34.2, -5.74) * mm});
            skLineSegment(sketch, "E1142", {"start": v(-34.2, -5.74) * mm, "end": v(-34.2, -5.82) * mm});
            skLineSegment(sketch, "E1143", {"start": v(-34.2, -5.82) * mm, "end": v(-34.2, -5.9) * mm});
            skLineSegment(sketch, "E1144", {"start": v(-34.2, -5.9) * mm, "end": v(-34.19, -5.98) * mm});
            skLineSegment(sketch, "E1145", {"start": v(-34.19, -5.98) * mm, "end": v(-34.17, -6.06) * mm});
            skLineSegment(sketch, "E1146", {"start": v(-34.17, -6.06) * mm, "end": v(-34.15, -6.14) * mm});
            skLineSegment(sketch, "E1147", {"start": v(-34.15, -6.14) * mm, "end": v(-34.13, -6.22) * mm});
            skLineSegment(sketch, "E1148", {"start": v(-34.13, -6.22) * mm, "end": v(-34.1, -6.3) * mm});
            skLineSegment(sketch, "E1149", {"start": v(-34.1, -6.3) * mm, "end": v(-34.08, -6.37) * mm});
            skLineSegment(sketch, "E1150", {"start": v(-34.08, -6.37) * mm, "end": v(-34.04, -6.45) * mm});
            skLineSegment(sketch, "E1151", {"start": v(-34.04, -6.45) * mm, "end": v(-34, -6.52) * mm});
            skLineSegment(sketch, "E1152", {"start": v(-34, -6.52) * mm, "end": v(-33.97, -6.6) * mm});
            skLineSegment(sketch, "E1153", {"start": v(-33.97, -6.6) * mm, "end": v(-33.92, -6.66) * mm});
            skLineSegment(sketch, "E1154", {"start": v(-33.92, -6.66) * mm, "end": v(-33.88, -6.73) * mm});
            skLineSegment(sketch, "E1155", {"start": v(-33.88, -6.73) * mm, "end": v(-33.83, -6.8) * mm});
            skLineSegment(sketch, "E1156", {"start": v(-33.83, -6.8) * mm, "end": v(-33.77, -6.86) * mm});
            skLineSegment(sketch, "E1157", {"start": v(-33.77, -6.86) * mm, "end": v(-33.72, -6.91) * mm});
            skLineSegment(sketch, "E1158", {"start": v(-33.72, -6.91) * mm, "end": v(-14.92, -25.66) * mm});
            skLineSegment(sketch, "E1159", {"start": v(-14.92, -25.66) * mm, "end": v(-14.82, -25.76) * mm});
            skLineSegment(sketch, "E1160", {"start": v(-14.82, -25.76) * mm, "end": v(-14.7, -25.85) * mm});
            skLineSegment(sketch, "E1161", {"start": v(-14.7, -25.85) * mm, "end": v(-14.6, -25.94) * mm});
            skLineSegment(sketch, "E1162", {"start": v(-14.6, -25.94) * mm, "end": v(-14.49, -26.02) * mm});
            skLineSegment(sketch, "E1163", {"start": v(-14.49, -26.02) * mm, "end": v(-14.37, -26.1) * mm});
            skLineSegment(sketch, "E1164", {"start": v(-14.37, -26.1) * mm, "end": v(-14.25, -26.16) * mm});
            skLineSegment(sketch, "E1165", {"start": v(-14.25, -26.16) * mm, "end": v(-14.13, -26.22) * mm});
            skLineSegment(sketch, "E1166", {"start": v(-14.13, -26.22) * mm, "end": v(-14, -26.28) * mm});
            skLineSegment(sketch, "E1167", {"start": v(-14, -26.28) * mm, "end": v(-13.87, -26.33) * mm});
            skLineSegment(sketch, "E1168", {"start": v(-13.87, -26.33) * mm, "end": v(-13.74, -26.37) * mm});
            skLineSegment(sketch, "E1169", {"start": v(-13.74, -26.37) * mm, "end": v(-13.61, -26.4) * mm});
            skLineSegment(sketch, "E1170", {"start": v(-13.61, -26.4) * mm, "end": v(-13.48, -26.43) * mm});
            skLineSegment(sketch, "E1171", {"start": v(-13.48, -26.43) * mm, "end": v(-13.34, -26.46) * mm});
            skLineSegment(sketch, "E1172", {"start": v(-13.34, -26.46) * mm, "end": v(-13.2, -26.48) * mm});
            skLineSegment(sketch, "E1173", {"start": v(-13.2, -26.48) * mm, "end": v(-13.06, -26.49) * mm});
            skLineSegment(sketch, "E1174", {"start": v(-13.06, -26.49) * mm, "end": v(-12.92, -26.49) * mm});
            skLineSegment(sketch, "E1175", {"start": v(-12.92, -26.49) * mm, "end": v(-7.66, -26.49) * mm});
            skLineSegment(sketch, "E1176", {"start": v(-7.66, -26.49) * mm, "end": v(-7.53, -26.48) * mm});
            skLineSegment(sketch, "E1177", {"start": v(-7.53, -26.48) * mm, "end": v(-7.4, -26.47) * mm});
            skLineSegment(sketch, "E1178", {"start": v(-7.4, -26.47) * mm, "end": v(-7.28, -26.45) * mm});
            skLineSegment(sketch, "E1179", {"start": v(-7.28, -26.45) * mm, "end": v(-7.15, -26.42) * mm});
            skLineSegment(sketch, "E1180", {"start": v(-7.15, -26.42) * mm, "end": v(-7.03, -26.38) * mm});
            skLineSegment(sketch, "E1181", {"start": v(-7.03, -26.38) * mm, "end": v(-6.92, -26.33) * mm});
            skLineSegment(sketch, "E1182", {"start": v(-6.92, -26.33) * mm, "end": v(-6.8, -26.28) * mm});
            skLineSegment(sketch, "E1183", {"start": v(-6.8, -26.28) * mm, "end": v(-6.7, -26.22) * mm});
            skLineSegment(sketch, "E1184", {"start": v(-6.7, -26.22) * mm, "end": v(-6.6, -26.15) * mm});
            skLineSegment(sketch, "E1185", {"start": v(-6.6, -26.15) * mm, "end": v(-6.5, -26.07) * mm});
            skLineSegment(sketch, "E1186", {"start": v(-6.5, -26.07) * mm, "end": v(-6.4, -25.99) * mm});
            skLineSegment(sketch, "E1187", {"start": v(-6.4, -25.99) * mm, "end": v(-6.3, -25.9) * mm});
            skLineSegment(sketch, "E1188", {"start": v(-6.3, -25.9) * mm, "end": v(-6.23, -25.8) * mm});
            skLineSegment(sketch, "E1189", {"start": v(-6.23, -25.8) * mm, "end": v(-6.15, -25.7) * mm});
            skLineSegment(sketch, "E1190", {"start": v(-6.15, -25.7) * mm, "end": v(-6.08, -25.59) * mm});
            skLineSegment(sketch, "E1191", {"start": v(-6.08, -25.59) * mm, "end": v(-6.02, -25.47) * mm});
            skLineSegment(sketch, "E1192", {"start": v(-6.02, -25.47) * mm, "end": v(12.19, 10.93) * mm});
            skLineSegment(sketch, "E1193", {"start": v(12.19, 10.93) * mm, "end": v(12.2, 10.95) * mm});
            skLineSegment(sketch, "E1194", {"start": v(12.2, 10.95) * mm, "end": v(12.2, 10.97) * mm});
            skLineSegment(sketch, "E1195", {"start": v(12.2, 10.97) * mm, "end": v(12.21, 10.98) * mm});
            skLineSegment(sketch, "E1196", {"start": v(12.21, 10.98) * mm, "end": v(12.22, 11) * mm});
            skLineSegment(sketch, "E1197", {"start": v(12.22, 11) * mm, "end": v(12.24, 11) * mm});
            skLineSegment(sketch, "E1198", {"start": v(12.24, 11) * mm, "end": v(12.25, 11.02) * mm});
            skLineSegment(sketch, "E1199", {"start": v(12.25, 11.02) * mm, "end": v(12.26, 11.03) * mm});
            skLineSegment(sketch, "E1200", {"start": v(12.26, 11.03) * mm, "end": v(12.28, 11.04) * mm});
            skLineSegment(sketch, "E1201", {"start": v(12.28, 11.04) * mm, "end": v(12.3, 11.04) * mm});
            skLineSegment(sketch, "E1202", {"start": v(12.3, 11.04) * mm, "end": v(12.3, 11.05) * mm});
            skLineSegment(sketch, "E1203", {"start": v(12.3, 11.05) * mm, "end": v(12.32, 11.06) * mm});
            skLineSegment(sketch, "E1204", {"start": v(12.32, 11.06) * mm, "end": v(12.34, 11.06) * mm});
            skLineSegment(sketch, "E1205", {"start": v(12.34, 11.06) * mm, "end": v(12.36, 11.07) * mm});
            skLineSegment(sketch, "E1206", {"start": v(12.36, 11.07) * mm, "end": v(12.37, 11.07) * mm});
            skLineSegment(sketch, "E1207", {"start": v(12.37, 11.07) * mm, "end": v(12.4, 11.07) * mm});
            skLineSegment(sketch, "E1208", {"start": v(12.4, 11.07) * mm, "end": v(12.4, 11.07) * mm});
            skLineSegment(sketch, "E1209", {"start": v(12.4, 11.07) * mm, "end": v(12.43, 11.07) * mm});
            skLineSegment(sketch, "E1210", {"start": v(12.43, 11.07) * mm, "end": v(12.44, 11.07) * mm});
            skLineSegment(sketch, "E1211", {"start": v(12.44, 11.07) * mm, "end": v(12.46, 11.07) * mm});
            skLineSegment(sketch, "E1212", {"start": v(12.46, 11.07) * mm, "end": v(12.48, 11.06) * mm});
            skLineSegment(sketch, "E1213", {"start": v(12.48, 11.06) * mm, "end": v(12.5, 11.06) * mm});
            skLineSegment(sketch, "E1214", {"start": v(12.5, 11.06) * mm, "end": v(12.51, 11.05) * mm});
            skLineSegment(sketch, "E1215", {"start": v(12.51, 11.05) * mm, "end": v(12.53, 11.04) * mm});
            skLineSegment(sketch, "E1216", {"start": v(12.53, 11.04) * mm, "end": v(12.54, 11.04) * mm});
            skLineSegment(sketch, "E1217", {"start": v(12.54, 11.04) * mm, "end": v(12.56, 11.03) * mm});
            skLineSegment(sketch, "E1218", {"start": v(12.56, 11.03) * mm, "end": v(12.57, 11.02) * mm});
            skLineSegment(sketch, "E1219", {"start": v(12.57, 11.02) * mm, "end": v(12.58, 11) * mm});
            skLineSegment(sketch, "E1220", {"start": v(12.58, 11) * mm, "end": v(12.6, 11) * mm});
            skLineSegment(sketch, "E1221", {"start": v(12.6, 11) * mm, "end": v(12.6, 10.98) * mm});
            skLineSegment(sketch, "E1222", {"start": v(12.6, 10.98) * mm, "end": v(12.61, 10.97) * mm});
            skLineSegment(sketch, "E1223", {"start": v(12.61, 10.97) * mm, "end": v(12.62, 10.95) * mm});
            skLineSegment(sketch, "E1224", {"start": v(12.62, 10.95) * mm, "end": v(12.63, 10.93) * mm});
            skLineSegment(sketch, "E1225", {"start": v(12.63, 10.93) * mm, "end": v(19.74, -3.27) * mm});
            skLineSegment(sketch, "E1226", {"start": v(19.74, -3.27) * mm, "end": v(19.74, -3.29) * mm});
            skLineSegment(sketch, "E1227", {"start": v(19.74, -3.29) * mm, "end": v(19.75, -3.3) * mm});
            skLineSegment(sketch, "E1228", {"start": v(19.75, -3.3) * mm, "end": v(19.75, -3.32) * mm});
            skLineSegment(sketch, "E1229", {"start": v(19.75, -3.32) * mm, "end": v(19.76, -3.33) * mm});
            skLineSegment(sketch, "E1230", {"start": v(19.76, -3.33) * mm, "end": v(19.76, -3.35) * mm});
            skLineSegment(sketch, "E1231", {"start": v(19.76, -3.35) * mm, "end": v(19.76, -3.37) * mm});
            skLineSegment(sketch, "E1232", {"start": v(19.76, -3.37) * mm, "end": v(19.76, -3.38) * mm});
            skLineSegment(sketch, "E1233", {"start": v(19.76, -3.38) * mm, "end": v(19.76, -3.4) * mm});
            skLineSegment(sketch, "E1234", {"start": v(19.76, -3.4) * mm, "end": v(19.76, -3.41) * mm});
            skLineSegment(sketch, "E1235", {"start": v(19.76, -3.41) * mm, "end": v(19.76, -3.43) * mm});
            skLineSegment(sketch, "E1236", {"start": v(19.76, -3.43) * mm, "end": v(19.76, -3.44) * mm});
            skLineSegment(sketch, "E1237", {"start": v(19.76, -3.44) * mm, "end": v(19.75, -3.46) * mm});
            skLineSegment(sketch, "E1238", {"start": v(19.75, -3.46) * mm, "end": v(19.75, -3.48) * mm});
            skLineSegment(sketch, "E1239", {"start": v(19.75, -3.48) * mm, "end": v(19.74, -3.5) * mm});
            skLineSegment(sketch, "E1240", {"start": v(19.74, -3.5) * mm, "end": v(19.73, -3.5) * mm});
            skLineSegment(sketch, "E1241", {"start": v(19.73, -3.5) * mm, "end": v(19.72, -3.52) * mm});
            skLineSegment(sketch, "E1242", {"start": v(19.72, -3.52) * mm, "end": v(19.72, -3.53) * mm});
            skLineSegment(sketch, "E1243", {"start": v(19.72, -3.53) * mm, "end": v(19.7, -3.55) * mm});
            skLineSegment(sketch, "E1244", {"start": v(19.7, -3.55) * mm, "end": v(19.7, -3.56) * mm});
            skLineSegment(sketch, "E1245", {"start": v(19.7, -3.56) * mm, "end": v(19.68, -3.57) * mm});
            skLineSegment(sketch, "E1246", {"start": v(19.68, -3.57) * mm, "end": v(19.67, -3.58) * mm});
            skLineSegment(sketch, "E1247", {"start": v(19.67, -3.58) * mm, "end": v(19.66, -3.6) * mm});
            skLineSegment(sketch, "E1248", {"start": v(19.66, -3.6) * mm, "end": v(19.65, -3.6) * mm});
            skLineSegment(sketch, "E1249", {"start": v(19.65, -3.6) * mm, "end": v(19.63, -3.6) * mm});
            skLineSegment(sketch, "E1250", {"start": v(19.63, -3.6) * mm, "end": v(19.62, -3.62) * mm});
            skLineSegment(sketch, "E1251", {"start": v(19.62, -3.62) * mm, "end": v(19.6, -3.62) * mm});
            skLineSegment(sketch, "E1252", {"start": v(19.6, -3.62) * mm, "end": v(19.59, -3.63) * mm});
            skLineSegment(sketch, "E1253", {"start": v(19.59, -3.63) * mm, "end": v(19.57, -3.63) * mm});
            skLineSegment(sketch, "E1254", {"start": v(19.57, -3.63) * mm, "end": v(19.56, -3.64) * mm});
            skLineSegment(sketch, "E1255", {"start": v(19.56, -3.64) * mm, "end": v(19.54, -3.64) * mm});
            skLineSegment(sketch, "E1256", {"start": v(19.54, -3.64) * mm, "end": v(19.53, -3.64) * mm});
            skLineSegment(sketch, "E1257", {"start": v(19.53, -3.64) * mm, "end": v(19.5, -3.64) * mm});
            skLineSegment(sketch, "E1258", {"start": v(19.5, -3.64) * mm, "end": v(9.92, -3.64) * mm});
            skLineSegment(sketch, "E1259", {"start": v(9.92, -3.64) * mm, "end": v(9.7, -3.64) * mm});
            skLineSegment(sketch, "E1260", {"start": v(9.7, -3.64) * mm, "end": v(9.49, -3.66) * mm});
            skLineSegment(sketch, "E1261", {"start": v(9.49, -3.66) * mm, "end": v(9.28, -3.68) * mm});
            skLineSegment(sketch, "E1262", {"start": v(9.28, -3.68) * mm, "end": v(9.07, -3.7) * mm});
            skLineSegment(sketch, "E1263", {"start": v(9.07, -3.7) * mm, "end": v(8.87, -3.75) * mm});
            skLineSegment(sketch, "E1264", {"start": v(8.87, -3.75) * mm, "end": v(8.68, -3.8) * mm});
            skLineSegment(sketch, "E1265", {"start": v(8.68, -3.8) * mm, "end": v(8.5, -3.85) * mm});
            skLineSegment(sketch, "E1266", {"start": v(8.5, -3.85) * mm, "end": v(8.31, -3.91) * mm});
            skLineSegment(sketch, "E1267", {"start": v(8.31, -3.91) * mm, "end": v(8.13, -3.99) * mm});
            skLineSegment(sketch, "E1268", {"start": v(8.13, -3.99) * mm, "end": v(7.96, -4.07) * mm});
            skLineSegment(sketch, "E1269", {"start": v(7.96, -4.07) * mm, "end": v(7.8, -4.16) * mm});
            skLineSegment(sketch, "E1270", {"start": v(7.8, -4.16) * mm, "end": v(7.63, -4.25) * mm});
            skLineSegment(sketch, "E1271", {"start": v(7.63, -4.25) * mm, "end": v(7.48, -4.36) * mm});
            skLineSegment(sketch, "E1272", {"start": v(7.48, -4.36) * mm, "end": v(7.33, -4.47) * mm});
            skLineSegment(sketch, "E1273", {"start": v(7.33, -4.47) * mm, "end": v(7.18, -4.6) * mm});
            skLineSegment(sketch, "E1274", {"start": v(7.18, -4.6) * mm, "end": v(7.05, -4.73) * mm});
            skLineSegment(sketch, "E1275", {"start": v(7.05, -4.73) * mm, "end": v(6.92, -4.87) * mm});
            skLineSegment(sketch, "E1276", {"start": v(6.92, -4.87) * mm, "end": v(6.8, -5.01) * mm});
            skLineSegment(sketch, "E1277", {"start": v(6.8, -5.01) * mm, "end": v(6.68, -5.16) * mm});
            skLineSegment(sketch, "E1278", {"start": v(6.68, -5.16) * mm, "end": v(6.57, -5.31) * mm});
            skLineSegment(sketch, "E1279", {"start": v(6.57, -5.31) * mm, "end": v(6.47, -5.48) * mm});
            skLineSegment(sketch, "E1280", {"start": v(6.47, -5.48) * mm, "end": v(6.39, -5.64) * mm});
            skLineSegment(sketch, "E1281", {"start": v(6.39, -5.64) * mm, "end": v(6.3, -5.81) * mm});
            skLineSegment(sketch, "E1282", {"start": v(6.3, -5.81) * mm, "end": v(6.23, -6) * mm});
            skLineSegment(sketch, "E1283", {"start": v(6.23, -6) * mm, "end": v(6.17, -6.17) * mm});
            skLineSegment(sketch, "E1284", {"start": v(6.17, -6.17) * mm, "end": v(6.11, -6.36) * mm});
            skLineSegment(sketch, "E1285", {"start": v(6.11, -6.36) * mm, "end": v(6.07, -6.56) * mm});
            skLineSegment(sketch, "E1286", {"start": v(6.07, -6.56) * mm, "end": v(6.03, -6.76) * mm});
            skLineSegment(sketch, "E1287", {"start": v(6.03, -6.76) * mm, "end": v(6, -6.96) * mm});
            skLineSegment(sketch, "E1288", {"start": v(6, -6.96) * mm, "end": v(5.98, -7.17) * mm});
            skLineSegment(sketch, "E1289", {"start": v(5.98, -7.17) * mm, "end": v(5.96, -7.38) * mm});
            skLineSegment(sketch, "E1290", {"start": v(5.96, -7.38) * mm, "end": v(5.96, -7.6) * mm});
            skLineSegment(sketch, "E1291", {"start": v(5.96, -7.6) * mm, "end": v(5.96, -7.82) * mm});
            skLineSegment(sketch, "E1292", {"start": v(5.96, -7.82) * mm, "end": v(5.98, -8.03) * mm});
            skLineSegment(sketch, "E1293", {"start": v(5.98, -8.03) * mm, "end": v(6, -8.23) * mm});
            skLineSegment(sketch, "E1294", {"start": v(6, -8.23) * mm, "end": v(6.03, -8.43) * mm});
            skLineSegment(sketch, "E1295", {"start": v(6.03, -8.43) * mm, "end": v(6.07, -8.63) * mm});
            skLineSegment(sketch, "E1296", {"start": v(6.07, -8.63) * mm, "end": v(6.12, -8.82) * mm});
            skLineSegment(sketch, "E1297", {"start": v(6.12, -8.82) * mm, "end": v(6.17, -9) * mm});
            skLineSegment(sketch, "E1298", {"start": v(6.17, -9) * mm, "end": v(6.24, -9.19) * mm});
            skLineSegment(sketch, "E1299", {"start": v(6.24, -9.19) * mm, "end": v(6.31, -9.37) * mm});
            skLineSegment(sketch, "E1300", {"start": v(6.31, -9.37) * mm, "end": v(6.4, -9.54) * mm});
            skLineSegment(sketch, "E1301", {"start": v(6.4, -9.54) * mm, "end": v(6.49, -9.7) * mm});
            skLineSegment(sketch, "E1302", {"start": v(6.49, -9.7) * mm, "end": v(6.59, -9.87) * mm});
            skLineSegment(sketch, "E1303", {"start": v(6.59, -9.87) * mm, "end": v(6.7, -10.03) * mm});
            skLineSegment(sketch, "E1304", {"start": v(6.7, -10.03) * mm, "end": v(6.81, -10.18) * mm});
            skLineSegment(sketch, "E1305", {"start": v(6.81, -10.18) * mm, "end": v(6.94, -10.33) * mm});
            skLineSegment(sketch, "E1306", {"start": v(6.94, -10.33) * mm, "end": v(7.07, -10.48) * mm});
            skLineSegment(sketch, "E1307", {"start": v(7.07, -10.48) * mm, "end": v(7.21, -10.62) * mm});
            skLineSegment(sketch, "E1308", {"start": v(7.21, -10.62) * mm, "end": v(7.36, -10.74) * mm});
            skLineSegment(sketch, "E1309", {"start": v(7.36, -10.74) * mm, "end": v(7.51, -10.86) * mm});
            skLineSegment(sketch, "E1310", {"start": v(7.51, -10.86) * mm, "end": v(7.67, -10.98) * mm});
            skLineSegment(sketch, "E1311", {"start": v(7.67, -10.98) * mm, "end": v(7.83, -11.08) * mm});
            skLineSegment(sketch, "E1312", {"start": v(7.83, -11.08) * mm, "end": v(8, -11.17) * mm});
            skLineSegment(sketch, "E1313", {"start": v(8, -11.17) * mm, "end": v(8.17, -11.26) * mm});
            skLineSegment(sketch, "E1314", {"start": v(8.17, -11.26) * mm, "end": v(8.34, -11.33) * mm});
            skLineSegment(sketch, "E1315", {"start": v(8.34, -11.33) * mm, "end": v(8.52, -11.4) * mm});
            skLineSegment(sketch, "E1316", {"start": v(8.52, -11.4) * mm, "end": v(8.7, -11.46) * mm});
            skLineSegment(sketch, "E1317", {"start": v(8.7, -11.46) * mm, "end": v(8.9, -11.5) * mm});
            skLineSegment(sketch, "E1318", {"start": v(8.9, -11.5) * mm, "end": v(9.1, -11.55) * mm});
            skLineSegment(sketch, "E1319", {"start": v(9.1, -11.55) * mm, "end": v(9.3, -11.58) * mm});
            skLineSegment(sketch, "E1320", {"start": v(9.3, -11.58) * mm, "end": v(9.5, -11.6) * mm});
            skLineSegment(sketch, "E1321", {"start": v(9.5, -11.6) * mm, "end": v(9.7, -11.61) * mm});
            skLineSegment(sketch, "E1322", {"start": v(9.7, -11.61) * mm, "end": v(9.92, -11.62) * mm});
            skLineSegment(sketch, "E1323", {"start": v(9.92, -11.62) * mm, "end": v(23.5, -11.62) * mm});
            skLineSegment(sketch, "E1324", {"start": v(23.5, -11.62) * mm, "end": v(23.54, -11.62) * mm});
            skLineSegment(sketch, "E1325", {"start": v(23.54, -11.62) * mm, "end": v(23.58, -11.63) * mm});
            skLineSegment(sketch, "E1326", {"start": v(23.58, -11.63) * mm, "end": v(23.63, -11.63) * mm});
            skLineSegment(sketch, "E1327", {"start": v(23.63, -11.63) * mm, "end": v(23.67, -11.64) * mm});
            skLineSegment(sketch, "E1328", {"start": v(23.67, -11.64) * mm, "end": v(23.7, -11.66) * mm});
            skLineSegment(sketch, "E1329", {"start": v(23.7, -11.66) * mm, "end": v(23.75, -11.67) * mm});
            skLineSegment(sketch, "E1330", {"start": v(23.75, -11.67) * mm, "end": v(23.79, -11.7) * mm});
            skLineSegment(sketch, "E1331", {"start": v(23.79, -11.7) * mm, "end": v(23.83, -11.71) * mm});
            skLineSegment(sketch, "E1332", {"start": v(23.83, -11.71) * mm, "end": v(23.86, -11.74) * mm});
            skLineSegment(sketch, "E1333", {"start": v(23.86, -11.74) * mm, "end": v(23.9, -11.76) * mm});
            skLineSegment(sketch, "E1334", {"start": v(23.9, -11.76) * mm, "end": v(23.93, -11.8) * mm});
            skLineSegment(sketch, "E1335", {"start": v(23.93, -11.8) * mm, "end": v(23.96, -11.82) * mm});
            skLineSegment(sketch, "E1336", {"start": v(23.96, -11.82) * mm, "end": v(23.99, -11.85) * mm});
            skLineSegment(sketch, "E1337", {"start": v(23.99, -11.85) * mm, "end": v(24.01, -11.89) * mm});
            skLineSegment(sketch, "E1338", {"start": v(24.01, -11.89) * mm, "end": v(24.04, -11.93) * mm});
            skLineSegment(sketch, "E1339", {"start": v(24.04, -11.93) * mm, "end": v(24.06, -11.97) * mm});
            skLineSegment(sketch, "E1340", {"start": v(24.06, -11.97) * mm, "end": v(30.99, -25.78) * mm});
            skLineSegment(sketch, "E1341", {"start": v(30.99, -25.78) * mm, "end": v(31.03, -25.86) * mm});
            skLineSegment(sketch, "E1342", {"start": v(31.03, -25.86) * mm, "end": v(31.08, -25.93) * mm});
            skLineSegment(sketch, "E1343", {"start": v(31.08, -25.93) * mm, "end": v(31.13, -26) * mm});
            skLineSegment(sketch, "E1344", {"start": v(31.13, -26) * mm, "end": v(31.2, -26.07) * mm});
            skLineSegment(sketch, "E1345", {"start": v(31.2, -26.07) * mm, "end": v(31.25, -26.14) * mm});
            skLineSegment(sketch, "E1346", {"start": v(31.25, -26.14) * mm, "end": v(31.32, -26.2) * mm});
            skLineSegment(sketch, "E1347", {"start": v(31.32, -26.2) * mm, "end": v(31.39, -26.25) * mm});
            skLineSegment(sketch, "E1348", {"start": v(31.39, -26.25) * mm, "end": v(31.46, -26.3) * mm});
            skLineSegment(sketch, "E1349", {"start": v(31.46, -26.3) * mm, "end": v(31.54, -26.34) * mm});
            skLineSegment(sketch, "E1350", {"start": v(31.54, -26.34) * mm, "end": v(31.62, -26.38) * mm});
            skLineSegment(sketch, "E1351", {"start": v(31.62, -26.38) * mm, "end": v(31.7, -26.41) * mm});
            skLineSegment(sketch, "E1352", {"start": v(31.7, -26.41) * mm, "end": v(31.79, -26.44) * mm});
            skLineSegment(sketch, "E1353", {"start": v(31.79, -26.44) * mm, "end": v(31.87, -26.46) * mm});
            skLineSegment(sketch, "E1354", {"start": v(31.87, -26.46) * mm, "end": v(31.96, -26.48) * mm});
            skLineSegment(sketch, "E1355", {"start": v(31.96, -26.48) * mm, "end": v(32.05, -26.49) * mm});
            skLineSegment(sketch, "E1356", {"start": v(32.05, -26.49) * mm, "end": v(32.14, -26.49) * mm});
            skLineSegment(sketch, "E1357", {"start": v(32.14, -26.49) * mm, "end": v(35.96, -26.49) * mm});
            skLineSegment(sketch, "E1358", {"start": v(35.96, -26.49) * mm, "end": v(36.17, -26.48) * mm});
            skLineSegment(sketch, "E1359", {"start": v(36.17, -26.48) * mm, "end": v(36.38, -26.47) * mm});
            skLineSegment(sketch, "E1360", {"start": v(36.38, -26.47) * mm, "end": v(36.58, -26.45) * mm});
            skLineSegment(sketch, "E1361", {"start": v(36.58, -26.45) * mm, "end": v(36.78, -26.42) * mm});
            skLineSegment(sketch, "E1362", {"start": v(36.78, -26.42) * mm, "end": v(36.98, -26.38) * mm});
            skLineSegment(sketch, "E1363", {"start": v(36.98, -26.38) * mm, "end": v(37.17, -26.33) * mm});
            skLineSegment(sketch, "E1364", {"start": v(37.17, -26.33) * mm, "end": v(37.35, -26.27) * mm});
            skLineSegment(sketch, "E1365", {"start": v(37.35, -26.27) * mm, "end": v(37.53, -26.2) * mm});
            skLineSegment(sketch, "E1366", {"start": v(37.53, -26.2) * mm, "end": v(37.71, -26.13) * mm});
            skLineSegment(sketch, "E1367", {"start": v(37.71, -26.13) * mm, "end": v(37.88, -26.05) * mm});
            skLineSegment(sketch, "E1368", {"start": v(37.88, -26.05) * mm, "end": v(38.05, -25.96) * mm});
            skLineSegment(sketch, "E1369", {"start": v(38.05, -25.96) * mm, "end": v(38.2, -25.86) * mm});
            skLineSegment(sketch, "E1370", {"start": v(38.2, -25.86) * mm, "end": v(38.37, -25.75) * mm});
            skLineSegment(sketch, "E1371", {"start": v(38.37, -25.75) * mm, "end": v(38.52, -25.63) * mm});
            skLineSegment(sketch, "E1372", {"start": v(38.52, -25.63) * mm, "end": v(38.66, -25.5) * mm});
            skLineSegment(sketch, "E1373", {"start": v(38.66, -25.5) * mm, "end": v(38.8, -25.37) * mm});
            skLineSegment(sketch, "E1374", {"start": v(38.8, -25.37) * mm, "end": v(38.94, -25.23) * mm});
            skLineSegment(sketch, "E1375", {"start": v(38.94, -25.23) * mm, "end": v(39.07, -25.09) * mm});
            skLineSegment(sketch, "E1376", {"start": v(39.07, -25.09) * mm, "end": v(39.18, -24.94) * mm});
            skLineSegment(sketch, "E1377", {"start": v(39.18, -24.94) * mm, "end": v(39.3, -24.78) * mm});
            skLineSegment(sketch, "E1378", {"start": v(39.3, -24.78) * mm, "end": v(39.4, -24.62) * mm});
            skLineSegment(sketch, "E1379", {"start": v(39.4, -24.62) * mm, "end": v(39.48, -24.45) * mm});
            skLineSegment(sketch, "E1380", {"start": v(39.48, -24.45) * mm, "end": v(39.57, -24.28) * mm});
            skLineSegment(sketch, "E1381", {"start": v(39.57, -24.28) * mm, "end": v(39.64, -24.1) * mm});
            skLineSegment(sketch, "E1382", {"start": v(39.64, -24.1) * mm, "end": v(39.7, -23.92) * mm});
            skLineSegment(sketch, "E1383", {"start": v(39.7, -23.92) * mm, "end": v(39.76, -23.74) * mm});
            skLineSegment(sketch, "E1384", {"start": v(39.76, -23.74) * mm, "end": v(39.8, -23.55) * mm});
            skLineSegment(sketch, "E1385", {"start": v(39.8, -23.55) * mm, "end": v(39.85, -23.35) * mm});
            skLineSegment(sketch, "E1386", {"start": v(39.85, -23.35) * mm, "end": v(39.88, -23.15) * mm});
            skLineSegment(sketch, "E1387", {"start": v(39.88, -23.15) * mm, "end": v(39.9, -22.95) * mm});
            skLineSegment(sketch, "E1388", {"start": v(39.9, -22.95) * mm, "end": v(39.91, -22.74) * mm});
            skLineSegment(sketch, "E1389", {"start": v(39.91, -22.74) * mm, "end": v(39.92, -22.53) * mm});
            skLineSegment(sketch, "E1390", {"start": v(39.92, -22.53) * mm, "end": v(39.92, 12.54) * mm});
            skLineSegment(sketch, "E1391", {"start": v(39.92, 12.54) * mm, "end": v(39.92, 12.6) * mm});
            skLineSegment(sketch, "E1392", {"start": v(39.92, 12.6) * mm, "end": v(39.93, 12.64) * mm});
            skLineSegment(sketch, "E1393", {"start": v(39.93, 12.64) * mm, "end": v(39.94, 12.7) * mm});
            skLineSegment(sketch, "E1394", {"start": v(39.94, 12.7) * mm, "end": v(39.96, 12.74) * mm});
            skLineSegment(sketch, "E1395", {"start": v(39.96, 12.74) * mm, "end": v(39.98, 12.78) * mm});
            skLineSegment(sketch, "E1396", {"start": v(39.98, 12.78) * mm, "end": v(40, 12.82) * mm});
            skLineSegment(sketch, "E1397", {"start": v(40, 12.82) * mm, "end": v(40.03, 12.86) * mm});
            skLineSegment(sketch, "E1398", {"start": v(40.03, 12.86) * mm, "end": v(40.06, 12.9) * mm});
            skLineSegment(sketch, "E1399", {"start": v(40.06, 12.9) * mm, "end": v(40.1, 12.93) * mm});
            skLineSegment(sketch, "E1400", {"start": v(40.1, 12.93) * mm, "end": v(40.14, 12.96) * mm});
            skLineSegment(sketch, "E1401", {"start": v(40.14, 12.96) * mm, "end": v(40.18, 12.98) * mm});
            skLineSegment(sketch, "E1402", {"start": v(40.18, 12.98) * mm, "end": v(40.22, 13) * mm});
            skLineSegment(sketch, "E1403", {"start": v(40.22, 13) * mm, "end": v(40.27, 13.02) * mm});
            skLineSegment(sketch, "E1404", {"start": v(40.27, 13.02) * mm, "end": v(40.32, 13.03) * mm});
            skLineSegment(sketch, "E1405", {"start": v(40.32, 13.03) * mm, "end": v(40.37, 13.04) * mm});
            skLineSegment(sketch, "E1406", {"start": v(40.37, 13.04) * mm, "end": v(40.42, 13.04) * mm});
            skLineSegment(sketch, "E1407", {"start": v(40.42, 13.04) * mm, "end": v(53.53, 13.04) * mm});
            skLineSegment(sketch, "E1408", {"start": v(53.53, 13.04) * mm, "end": v(53.8, 13.02) * mm});
            skLineSegment(sketch, "E1409", {"start": v(53.8, 13.02) * mm, "end": v(54.08, 13) * mm});
            skLineSegment(sketch, "E1410", {"start": v(54.08, 13) * mm, "end": v(54.35, 12.97) * mm});
            skLineSegment(sketch, "E1411", {"start": v(54.35, 12.97) * mm, "end": v(54.63, 12.93) * mm});
            skLineSegment(sketch, "E1412", {"start": v(54.63, 12.93) * mm, "end": v(54.9, 12.88) * mm});
            skLineSegment(sketch, "E1413", {"start": v(54.9, 12.88) * mm, "end": v(55.17, 12.83) * mm});
            skLineSegment(sketch, "E1414", {"start": v(55.17, 12.83) * mm, "end": v(55.45, 12.76) * mm});
            skLineSegment(sketch, "E1415", {"start": v(55.45, 12.76) * mm, "end": v(55.72, 12.7) * mm});
            skLineSegment(sketch, "E1416", {"start": v(55.72, 12.7) * mm, "end": v(55.99, 12.6) * mm});
            skLineSegment(sketch, "E1417", {"start": v(55.99, 12.6) * mm, "end": v(56.26, 12.52) * mm});
            skLineSegment(sketch, "E1418", {"start": v(56.26, 12.52) * mm, "end": v(56.53, 12.42) * mm});
            skLineSegment(sketch, "E1419", {"start": v(56.53, 12.42) * mm, "end": v(56.8, 12.31) * mm});
            skLineSegment(sketch, "E1420", {"start": v(56.8, 12.31) * mm, "end": v(57.07, 12.2) * mm});
            skLineSegment(sketch, "E1421", {"start": v(57.07, 12.2) * mm, "end": v(57.34, 12.07) * mm});
            skLineSegment(sketch, "E1422", {"start": v(57.34, 12.07) * mm, "end": v(57.6, 11.94) * mm});
            skLineSegment(sketch, "E1423", {"start": v(57.6, 11.94) * mm, "end": v(58.1, 11.67) * mm});
            skLineSegment(sketch, "E1424", {"start": v(58.1, 11.67) * mm, "end": v(58.54, 11.37) * mm});
            skLineSegment(sketch, "E1425", {"start": v(58.54, 11.37) * mm, "end": v(58.97, 11.05) * mm});
            skLineSegment(sketch, "E1426", {"start": v(58.97, 11.05) * mm, "end": v(59.36, 10.7) * mm});
            skLineSegment(sketch, "E1427", {"start": v(59.36, 10.7) * mm, "end": v(59.72, 10.33) * mm});
            skLineSegment(sketch, "E1428", {"start": v(59.72, 10.33) * mm, "end": v(60.05, 9.94) * mm});
            skLineSegment(sketch, "E1429", {"start": v(60.05, 9.94) * mm, "end": v(60.35, 9.52) * mm});
            skLineSegment(sketch, "E1430", {"start": v(60.35, 9.52) * mm, "end": v(60.62, 9.08) * mm});
            skLineSegment(sketch, "E1431", {"start": v(60.62, 9.08) * mm, "end": v(60.85, 8.6) * mm});
            skLineSegment(sketch, "E1432", {"start": v(60.85, 8.6) * mm, "end": v(61.06, 8.12) * mm});
            skLineSegment(sketch, "E1433", {"start": v(61.06, 8.12) * mm, "end": v(61.23, 7.6) * mm});
            skLineSegment(sketch, "E1434", {"start": v(61.23, 7.6) * mm, "end": v(61.37, 7.06) * mm});
            skLineSegment(sketch, "E1435", {"start": v(61.37, 7.06) * mm, "end": v(61.48, 6.5) * mm});
            skLineSegment(sketch, "E1436", {"start": v(61.48, 6.5) * mm, "end": v(61.56, 5.92) * mm});
            skLineSegment(sketch, "E1437", {"start": v(61.56, 5.92) * mm, "end": v(61.61, 5.3) * mm});
            skLineSegment(sketch, "E1438", {"start": v(61.61, 5.3) * mm, "end": v(61.63, 4.67) * mm});
            skLineSegment(sketch, "E1439", {"start": v(61.63, 4.67) * mm, "end": v(61.61, 4.04) * mm});
            skLineSegment(sketch, "E1440", {"start": v(61.61, 4.04) * mm, "end": v(61.56, 3.43) * mm});
            skLineSegment(sketch, "E1441", {"start": v(61.56, 3.43) * mm, "end": v(61.48, 2.85) * mm});
            skLineSegment(sketch, "E1442", {"start": v(61.48, 2.85) * mm, "end": v(61.37, 2.28) * mm});
            skLineSegment(sketch, "E1443", {"start": v(61.37, 2.28) * mm, "end": v(61.23, 1.74) * mm});
            skLineSegment(sketch, "E1444", {"start": v(61.23, 1.74) * mm, "end": v(61.06, 1.23) * mm});
            skLineSegment(sketch, "E1445", {"start": v(61.06, 1.23) * mm, "end": v(60.85, 0.74) * mm});
            skLineSegment(sketch, "E1446", {"start": v(60.85, 0.74) * mm, "end": v(60.62, 0.27) * mm});
            skLineSegment(sketch, "E1447", {"start": v(60.62, 0.27) * mm, "end": v(60.35, -0.17) * mm});
            skLineSegment(sketch, "E1448", {"start": v(60.35, -0.17) * mm, "end": v(60.05, -0.6) * mm});
            skLineSegment(sketch, "E1449", {"start": v(60.05, -0.6) * mm, "end": v(59.72, -0.99) * mm});
            skLineSegment(sketch, "E1450", {"start": v(59.72, -0.99) * mm, "end": v(59.36, -1.36) * mm});
            skLineSegment(sketch, "E1451", {"start": v(59.36, -1.36) * mm, "end": v(58.97, -1.7) * mm});
            skLineSegment(sketch, "E1452", {"start": v(58.97, -1.7) * mm, "end": v(58.55, -2.02) * mm});
            skLineSegment(sketch, "E1453", {"start": v(58.55, -2.02) * mm, "end": v(58.1, -2.32) * mm});
            skLineSegment(sketch, "E1454", {"start": v(58.1, -2.32) * mm, "end": v(57.6, -2.6) * mm});
            skLineSegment(sketch, "E1455", {"start": v(57.6, -2.6) * mm, "end": v(57.33, -2.73) * mm});
            skLineSegment(sketch, "E1456", {"start": v(57.33, -2.73) * mm, "end": v(57.05, -2.86) * mm});
            skLineSegment(sketch, "E1457", {"start": v(57.05, -2.86) * mm, "end": v(56.77, -2.98) * mm});
            skLineSegment(sketch, "E1458", {"start": v(56.77, -2.98) * mm, "end": v(56.5, -3.1) * mm});
            skLineSegment(sketch, "E1459", {"start": v(56.5, -3.1) * mm, "end": v(56.22, -3.2) * mm});
            skLineSegment(sketch, "E1460", {"start": v(56.22, -3.2) * mm, "end": v(55.94, -3.3) * mm});
            skLineSegment(sketch, "E1461", {"start": v(55.94, -3.3) * mm, "end": v(55.67, -3.38) * mm});
            skLineSegment(sketch, "E1462", {"start": v(55.67, -3.38) * mm, "end": v(55.4, -3.46) * mm});
            skLineSegment(sketch, "E1463", {"start": v(55.4, -3.46) * mm, "end": v(55.12, -3.52) * mm});
            skLineSegment(sketch, "E1464", {"start": v(55.12, -3.52) * mm, "end": v(54.85, -3.58) * mm});
            skLineSegment(sketch, "E1465", {"start": v(54.85, -3.58) * mm, "end": v(54.58, -3.63) * mm});
            skLineSegment(sketch, "E1466", {"start": v(54.58, -3.63) * mm, "end": v(54.31, -3.67) * mm});
            skLineSegment(sketch, "E1467", {"start": v(54.31, -3.67) * mm, "end": v(54.05, -3.7) * mm});
            skLineSegment(sketch, "E1468", {"start": v(54.05, -3.7) * mm, "end": v(53.78, -3.73) * mm});
            skLineSegment(sketch, "E1469", {"start": v(53.78, -3.73) * mm, "end": v(53.52, -3.74) * mm});
            skLineSegment(sketch, "E1470", {"start": v(53.52, -3.74) * mm, "end": v(45.85, -3.75) * mm});
            skLineSegment(sketch, "E1471", {"start": v(45.85, -3.75) * mm, "end": v(45.64, -3.75) * mm});
            skLineSegment(sketch, "E1472", {"start": v(45.64, -3.75) * mm, "end": v(45.43, -3.76) * mm});
            skLineSegment(sketch, "E1473", {"start": v(45.43, -3.76) * mm, "end": v(45.22, -3.79) * mm});
            skLineSegment(sketch, "E1474", {"start": v(45.22, -3.79) * mm, "end": v(45.02, -3.82) * mm});
            skLineSegment(sketch, "E1475", {"start": v(45.02, -3.82) * mm, "end": v(44.83, -3.86) * mm});
            skLineSegment(sketch, "E1476", {"start": v(44.83, -3.86) * mm, "end": v(44.64, -3.9) * mm});
            skLineSegment(sketch, "E1477", {"start": v(44.64, -3.9) * mm, "end": v(44.45, -3.96) * mm});
            skLineSegment(sketch, "E1478", {"start": v(44.45, -3.96) * mm, "end": v(44.27, -4.03) * mm});
            skLineSegment(sketch, "E1479", {"start": v(44.27, -4.03) * mm, "end": v(44.09, -4.1) * mm});
            skLineSegment(sketch, "E1480", {"start": v(44.09, -4.1) * mm, "end": v(43.92, -4.18) * mm});
            skLineSegment(sketch, "E1481", {"start": v(43.92, -4.18) * mm, "end": v(43.75, -4.27) * mm});
            skLineSegment(sketch, "E1482", {"start": v(43.75, -4.27) * mm, "end": v(43.58, -4.37) * mm});
            skLineSegment(sketch, "E1483", {"start": v(43.58, -4.37) * mm, "end": v(43.43, -4.48) * mm});
            skLineSegment(sketch, "E1484", {"start": v(43.43, -4.48) * mm, "end": v(43.27, -4.6) * mm});
            skLineSegment(sketch, "E1485", {"start": v(43.27, -4.6) * mm, "end": v(43.12, -4.73) * mm});
            skLineSegment(sketch, "E1486", {"start": v(43.12, -4.73) * mm, "end": v(42.98, -4.86) * mm});
            skLineSegment(sketch, "E1487", {"start": v(42.98, -4.86) * mm, "end": v(42.84, -5) * mm});
            skLineSegment(sketch, "E1488", {"start": v(42.84, -5) * mm, "end": v(42.71, -5.15) * mm});
            skLineSegment(sketch, "E1489", {"start": v(42.71, -5.15) * mm, "end": v(42.6, -5.3) * mm});
            skLineSegment(sketch, "E1490", {"start": v(42.6, -5.3) * mm, "end": v(42.48, -5.45) * mm});
            skLineSegment(sketch, "E1491", {"start": v(42.48, -5.45) * mm, "end": v(42.38, -5.62) * mm});
            skLineSegment(sketch, "E1492", {"start": v(42.38, -5.62) * mm, "end": v(42.28, -5.78) * mm});
            skLineSegment(sketch, "E1493", {"start": v(42.28, -5.78) * mm, "end": v(42.2, -5.95) * mm});
            skLineSegment(sketch, "E1494", {"start": v(42.2, -5.95) * mm, "end": v(42.12, -6.13) * mm});
            skLineSegment(sketch, "E1495", {"start": v(42.12, -6.13) * mm, "end": v(42.06, -6.31) * mm});
            skLineSegment(sketch, "E1496", {"start": v(42.06, -6.31) * mm, "end": v(42, -6.5) * mm});
            skLineSegment(sketch, "E1497", {"start": v(42, -6.5) * mm, "end": v(41.95, -6.69) * mm});
            skLineSegment(sketch, "E1498", {"start": v(41.95, -6.69) * mm, "end": v(41.9, -6.88) * mm});
            skLineSegment(sketch, "E1499", {"start": v(41.9, -6.88) * mm, "end": v(41.88, -7.08) * mm});
            skLineSegment(sketch, "E1500", {"start": v(41.88, -7.08) * mm, "end": v(41.85, -7.29) * mm});
            skLineSegment(sketch, "E1501", {"start": v(41.85, -7.29) * mm, "end": v(41.84, -7.5) * mm});
            skLineSegment(sketch, "E1502", {"start": v(41.84, -7.5) * mm, "end": v(41.84, -7.7) * mm});
            skLineSegment(sketch, "E1503", {"start": v(41.84, -7.7) * mm, "end": v(41.84, -24.27) * mm});
            skLineSegment(sketch, "E1504", {"start": v(41.84, -24.27) * mm, "end": v(41.85, -24.5) * mm});
            skLineSegment(sketch, "E1505", {"start": v(41.85, -24.5) * mm, "end": v(41.88, -24.72) * mm});
            skLineSegment(sketch, "E1506", {"start": v(41.88, -24.72) * mm, "end": v(41.94, -24.93) * mm});
            skLineSegment(sketch, "E1507", {"start": v(41.94, -24.93) * mm, "end": v(42.01, -25.13) * mm});
            skLineSegment(sketch, "E1508", {"start": v(42.01, -25.13) * mm, "end": v(42.1, -25.33) * mm});
            skLineSegment(sketch, "E1509", {"start": v(42.1, -25.33) * mm, "end": v(42.22, -25.5) * mm});
            skLineSegment(sketch, "E1510", {"start": v(42.22, -25.5) * mm, "end": v(42.34, -25.68) * mm});
            skLineSegment(sketch, "E1511", {"start": v(42.34, -25.68) * mm, "end": v(42.49, -25.84) * mm});
            skLineSegment(sketch, "E1512", {"start": v(42.49, -25.84) * mm, "end": v(42.64, -25.98) * mm});
            skLineSegment(sketch, "E1513", {"start": v(42.64, -25.98) * mm, "end": v(42.81, -26.1) * mm});
            skLineSegment(sketch, "E1514", {"start": v(42.81, -26.1) * mm, "end": v(43, -26.22) * mm});
            skLineSegment(sketch, "E1515", {"start": v(43, -26.22) * mm, "end": v(43.2, -26.31) * mm});
            skLineSegment(sketch, "E1516", {"start": v(43.2, -26.31) * mm, "end": v(43.4, -26.39) * mm});
            skLineSegment(sketch, "E1517", {"start": v(43.4, -26.39) * mm, "end": v(43.6, -26.44) * mm});
            skLineSegment(sketch, "E1518", {"start": v(43.6, -26.44) * mm, "end": v(43.83, -26.48) * mm});
            skLineSegment(sketch, "E1519", {"start": v(43.83, -26.48) * mm, "end": v(44.05, -26.49) * mm});
            skLineSegment(sketch, "E1520", {"start": v(44.05, -26.49) * mm, "end": v(80.72, -26.49) * mm});
            skLineSegment(sketch, "E1521", {"start": v(80.72, -26.49) * mm, "end": v(81.07, -26.48) * mm});
            skLineSegment(sketch, "E1522", {"start": v(81.07, -26.48) * mm, "end": v(81.42, -26.46) * mm});
            skLineSegment(sketch, "E1523", {"start": v(81.42, -26.46) * mm, "end": v(81.75, -26.42) * mm});
            skLineSegment(sketch, "E1524", {"start": v(81.75, -26.42) * mm, "end": v(82.08, -26.38) * mm});
            skLineSegment(sketch, "E1525", {"start": v(82.08, -26.38) * mm, "end": v(82.4, -26.31) * mm});
            skLineSegment(sketch, "E1526", {"start": v(82.4, -26.31) * mm, "end": v(82.7, -26.23) * mm});
            skLineSegment(sketch, "E1527", {"start": v(82.7, -26.23) * mm, "end": v(83.01, -26.14) * mm});
            skLineSegment(sketch, "E1528", {"start": v(83.01, -26.14) * mm, "end": v(83.3, -26.04) * mm});
            skLineSegment(sketch, "E1529", {"start": v(83.3, -26.04) * mm, "end": v(83.6, -25.92) * mm});
            skLineSegment(sketch, "E1530", {"start": v(83.6, -25.92) * mm, "end": v(83.87, -25.78) * mm});
            skLineSegment(sketch, "E1531", {"start": v(83.87, -25.78) * mm, "end": v(84.14, -25.63) * mm});
            skLineSegment(sketch, "E1532", {"start": v(84.14, -25.63) * mm, "end": v(84.4, -25.47) * mm});
            skLineSegment(sketch, "E1533", {"start": v(84.4, -25.47) * mm, "end": v(84.66, -25.3) * mm});
            skLineSegment(sketch, "E1534", {"start": v(84.66, -25.3) * mm, "end": v(84.9, -25.1) * mm});
            skLineSegment(sketch, "E1535", {"start": v(84.9, -25.1) * mm, "end": v(85.14, -24.9) * mm});
            skLineSegment(sketch, "E1536", {"start": v(85.14, -24.9) * mm, "end": v(85.37, -24.69) * mm});
            skLineSegment(sketch, "E1537", {"start": v(85.37, -24.69) * mm, "end": v(85.59, -24.46) * mm});
            skLineSegment(sketch, "E1538", {"start": v(85.59, -24.46) * mm, "end": v(85.8, -24.22) * mm});
            skLineSegment(sketch, "E1539", {"start": v(85.8, -24.22) * mm, "end": v(85.98, -23.98) * mm});
            skLineSegment(sketch, "E1540", {"start": v(85.98, -23.98) * mm, "end": v(86.16, -23.72) * mm});
            skLineSegment(sketch, "E1541", {"start": v(86.16, -23.72) * mm, "end": v(86.32, -23.46) * mm});
            skLineSegment(sketch, "E1542", {"start": v(86.32, -23.46) * mm, "end": v(86.47, -23.19) * mm});
            skLineSegment(sketch, "E1543", {"start": v(86.47, -23.19) * mm, "end": v(86.6, -22.9) * mm});
            skLineSegment(sketch, "E1544", {"start": v(86.6, -22.9) * mm, "end": v(86.72, -22.62) * mm});
            skLineSegment(sketch, "E1545", {"start": v(86.72, -22.62) * mm, "end": v(86.83, -22.33) * mm});
            skLineSegment(sketch, "E1546", {"start": v(86.83, -22.33) * mm, "end": v(86.92, -22.02) * mm});
            skLineSegment(sketch, "E1547", {"start": v(86.92, -22.02) * mm, "end": v(87, -21.71) * mm});
            skLineSegment(sketch, "E1548", {"start": v(87, -21.71) * mm, "end": v(87.06, -21.4) * mm});
            skLineSegment(sketch, "E1549", {"start": v(87.06, -21.4) * mm, "end": v(87.1, -21.07) * mm});
            skLineSegment(sketch, "E1550", {"start": v(87.1, -21.07) * mm, "end": v(87.15, -20.73) * mm});
            skLineSegment(sketch, "E1551", {"start": v(87.15, -20.73) * mm, "end": v(87.17, -20.39) * mm});
            skLineSegment(sketch, "E1552", {"start": v(87.17, -20.39) * mm, "end": v(87.17, -20.04) * mm});
            skLineSegment(sketch, "E1553", {"start": v(87.17, -20.04) * mm, "end": v(87.17, 7.99) * mm});
            skLineSegment(sketch, "E1554", {"start": v(87.17, 7.99) * mm, "end": v(87.16, 8.3) * mm});
            skLineSegment(sketch, "E1555", {"start": v(87.16, 8.3) * mm, "end": v(87.1, 8.62) * mm});
            skLineSegment(sketch, "E1556", {"start": v(87.1, 8.62) * mm, "end": v(87.03, 8.92) * mm});
            skLineSegment(sketch, "E1557", {"start": v(87.03, 8.92) * mm, "end": v(86.93, 9.2) * mm});
            skLineSegment(sketch, "E1558", {"start": v(86.93, 9.2) * mm, "end": v(86.8, 9.48) * mm});
            skLineSegment(sketch, "E1559", {"start": v(86.8, 9.48) * mm, "end": v(86.64, 9.74) * mm});
            skLineSegment(sketch, "E1560", {"start": v(86.64, 9.74) * mm, "end": v(86.46, 9.98) * mm});
            skLineSegment(sketch, "E1561", {"start": v(86.46, 9.98) * mm, "end": v(86.25, 10.2) * mm});
            skLineSegment(sketch, "E1562", {"start": v(86.25, 10.2) * mm, "end": v(86.03, 10.4) * mm});
            skLineSegment(sketch, "E1563", {"start": v(86.03, 10.4) * mm, "end": v(85.8, 10.59) * mm});
            skLineSegment(sketch, "E1564", {"start": v(85.8, 10.59) * mm, "end": v(85.53, 10.74) * mm});
            skLineSegment(sketch, "E1565", {"start": v(85.53, 10.74) * mm, "end": v(85.26, 10.88) * mm});
            skLineSegment(sketch, "E1566", {"start": v(85.26, 10.88) * mm, "end": v(84.97, 10.98) * mm});
            skLineSegment(sketch, "E1567", {"start": v(84.97, 10.98) * mm, "end": v(84.67, 11.06) * mm});
            skLineSegment(sketch, "E1568", {"start": v(84.67, 11.06) * mm, "end": v(84.36, 11.1) * mm});
            skLineSegment(sketch, "E1569", {"start": v(84.36, 11.1) * mm, "end": v(84.04, 11.12) * mm});
            skLineSegment(sketch, "E1570", {"start": v(84.04, 11.12) * mm, "end": v(73.32, 11.12) * mm});
            skLineSegment(sketch, "E1571", {"start": v(73.32, 11.12) * mm, "end": v(73.2, 11.13) * mm});
            skLineSegment(sketch, "E1572", {"start": v(73.2, 11.13) * mm, "end": v(73.07, 11.14) * mm});
            skLineSegment(sketch, "E1573", {"start": v(73.07, 11.14) * mm, "end": v(72.97, 11.16) * mm});
            skLineSegment(sketch, "E1574", {"start": v(72.97, 11.16) * mm, "end": v(72.87, 11.18) * mm});
            skLineSegment(sketch, "E1575", {"start": v(72.87, 11.18) * mm, "end": v(72.77, 11.21) * mm});
            skLineSegment(sketch, "E1576", {"start": v(72.77, 11.21) * mm, "end": v(72.7, 11.25) * mm});
            skLineSegment(sketch, "E1577", {"start": v(72.7, 11.25) * mm, "end": v(72.62, 11.3) * mm});
            skLineSegment(sketch, "E1578", {"start": v(72.62, 11.3) * mm, "end": v(72.55, 11.36) * mm});
            skLineSegment(sketch, "E1579", {"start": v(72.55, 11.36) * mm, "end": v(72.5, 11.42) * mm});
            skLineSegment(sketch, "E1580", {"start": v(72.5, 11.42) * mm, "end": v(72.44, 11.5) * mm});
            skLineSegment(sketch, "E1581", {"start": v(72.44, 11.5) * mm, "end": v(72.4, 11.57) * mm});
            skLineSegment(sketch, "E1582", {"start": v(72.4, 11.57) * mm, "end": v(72.36, 11.66) * mm});
            skLineSegment(sketch, "E1583", {"start": v(72.36, 11.66) * mm, "end": v(72.34, 11.75) * mm});
            skLineSegment(sketch, "E1584", {"start": v(72.34, 11.75) * mm, "end": v(72.32, 11.85) * mm});
            skLineSegment(sketch, "E1585", {"start": v(72.32, 11.85) * mm, "end": v(72.3, 11.96) * mm});
            skLineSegment(sketch, "E1586", {"start": v(72.3, 11.96) * mm, "end": v(72.3, 12.08) * mm});
            skLineSegment(sketch, "E1587", {"start": v(72.3, 12.08) * mm, "end": v(72.3, 12.2) * mm});
            skLineSegment(sketch, "E1588", {"start": v(72.3, 12.2) * mm, "end": v(72.32, 12.31) * mm});
            skLineSegment(sketch, "E1589", {"start": v(72.32, 12.31) * mm, "end": v(72.34, 12.41) * mm});
            skLineSegment(sketch, "E1590", {"start": v(72.34, 12.41) * mm, "end": v(72.36, 12.5) * mm});
            skLineSegment(sketch, "E1591", {"start": v(72.36, 12.5) * mm, "end": v(72.4, 12.6) * mm});
            skLineSegment(sketch, "E1592", {"start": v(72.4, 12.6) * mm, "end": v(72.44, 12.67) * mm});
            skLineSegment(sketch, "E1593", {"start": v(72.44, 12.67) * mm, "end": v(72.5, 12.74) * mm});
            skLineSegment(sketch, "E1594", {"start": v(72.5, 12.74) * mm, "end": v(72.55, 12.8) * mm});
            skLineSegment(sketch, "E1595", {"start": v(72.55, 12.8) * mm, "end": v(72.62, 12.86) * mm});
            skLineSegment(sketch, "E1596", {"start": v(72.62, 12.86) * mm, "end": v(72.7, 12.9) * mm});
            skLineSegment(sketch, "E1597", {"start": v(72.7, 12.9) * mm, "end": v(72.77, 12.95) * mm});
            skLineSegment(sketch, "E1598", {"start": v(72.77, 12.95) * mm, "end": v(72.87, 12.98) * mm});
            skLineSegment(sketch, "E1599", {"start": v(72.87, 12.98) * mm, "end": v(72.97, 13) * mm});
            skLineSegment(sketch, "E1600", {"start": v(72.97, 13) * mm, "end": v(73.07, 13.03) * mm});
            skLineSegment(sketch, "E1601", {"start": v(73.07, 13.03) * mm, "end": v(73.2, 13.04) * mm});
            skLineSegment(sketch, "E1602", {"start": v(73.2, 13.04) * mm, "end": v(73.32, 13.04) * mm});
            skLineSegment(sketch, "E1603", {"start": v(73.32, 13.04) * mm, "end": v(102.95, 13.04) * mm});
            skLineSegment(sketch, "E1604", {"start": v(102.95, 13.04) * mm, "end": v(103.07, 13.04) * mm});
            skLineSegment(sketch, "E1605", {"start": v(103.07, 13.04) * mm, "end": v(103.2, 13.03) * mm});
            skLineSegment(sketch, "E1606", {"start": v(103.2, 13.03) * mm, "end": v(103.3, 13) * mm});
            skLineSegment(sketch, "E1607", {"start": v(103.3, 13) * mm, "end": v(103.4, 12.98) * mm});
            skLineSegment(sketch, "E1608", {"start": v(103.4, 12.98) * mm, "end": v(103.49, 12.95) * mm});
            skLineSegment(sketch, "E1609", {"start": v(103.49, 12.95) * mm, "end": v(103.57, 12.9) * mm});
            skLineSegment(sketch, "E1610", {"start": v(103.57, 12.9) * mm, "end": v(103.65, 12.86) * mm});
            skLineSegment(sketch, "E1611", {"start": v(103.65, 12.86) * mm, "end": v(103.71, 12.8) * mm});
            skLineSegment(sketch, "E1612", {"start": v(103.71, 12.8) * mm, "end": v(103.77, 12.74) * mm});
            skLineSegment(sketch, "E1613", {"start": v(103.77, 12.74) * mm, "end": v(103.82, 12.67) * mm});
            skLineSegment(sketch, "E1614", {"start": v(103.82, 12.67) * mm, "end": v(103.86, 12.6) * mm});
            skLineSegment(sketch, "E1615", {"start": v(103.86, 12.6) * mm, "end": v(103.9, 12.5) * mm});
            skLineSegment(sketch, "E1616", {"start": v(103.9, 12.5) * mm, "end": v(103.93, 12.41) * mm});
            skLineSegment(sketch, "E1617", {"start": v(103.93, 12.41) * mm, "end": v(103.94, 12.31) * mm});
            skLineSegment(sketch, "E1618", {"start": v(103.94, 12.31) * mm, "end": v(103.96, 12.2) * mm});
            skLineSegment(sketch, "E1619", {"start": v(103.96, 12.2) * mm, "end": v(103.96, 12.08) * mm});
            skLineSegment(sketch, "E1620", {"start": v(103.96, 12.08) * mm, "end": v(103.96, 11.96) * mm});
            skLineSegment(sketch, "E1621", {"start": v(103.96, 11.96) * mm, "end": v(103.94, 11.85) * mm});
            skLineSegment(sketch, "E1622", {"start": v(103.94, 11.85) * mm, "end": v(103.93, 11.75) * mm});
            skLineSegment(sketch, "E1623", {"start": v(103.93, 11.75) * mm, "end": v(103.9, 11.66) * mm});
            skLineSegment(sketch, "E1624", {"start": v(103.9, 11.66) * mm, "end": v(103.86, 11.57) * mm});
            skLineSegment(sketch, "E1625", {"start": v(103.86, 11.57) * mm, "end": v(103.82, 11.5) * mm});
            skLineSegment(sketch, "E1626", {"start": v(103.82, 11.5) * mm, "end": v(103.77, 11.42) * mm});
            skLineSegment(sketch, "E1627", {"start": v(103.77, 11.42) * mm, "end": v(103.71, 11.36) * mm});
            skLineSegment(sketch, "E1628", {"start": v(103.71, 11.36) * mm, "end": v(103.65, 11.3) * mm});
            skLineSegment(sketch, "E1629", {"start": v(103.65, 11.3) * mm, "end": v(103.57, 11.25) * mm});
            skLineSegment(sketch, "E1630", {"start": v(103.57, 11.25) * mm, "end": v(103.49, 11.21) * mm});
            skLineSegment(sketch, "E1631", {"start": v(103.49, 11.21) * mm, "end": v(103.4, 11.18) * mm});
            skLineSegment(sketch, "E1632", {"start": v(103.4, 11.18) * mm, "end": v(103.3, 11.16) * mm});
            skLineSegment(sketch, "E1633", {"start": v(103.3, 11.16) * mm, "end": v(103.2, 11.14) * mm});
            skLineSegment(sketch, "E1634", {"start": v(103.2, 11.14) * mm, "end": v(103.07, 11.13) * mm});
            skLineSegment(sketch, "E1635", {"start": v(103.07, 11.13) * mm, "end": v(102.95, 11.12) * mm});
            skLineSegment(sketch, "E1636", {"start": v(102.95, 11.12) * mm, "end": v(92.22, 11.12) * mm});
            skLineSegment(sketch, "E1637", {"start": v(92.22, 11.12) * mm, "end": v(91.9, 11.1) * mm});
            skLineSegment(sketch, "E1638", {"start": v(91.9, 11.1) * mm, "end": v(91.6, 11.06) * mm});
            skLineSegment(sketch, "E1639", {"start": v(91.6, 11.06) * mm, "end": v(91.3, 10.98) * mm});
            skLineSegment(sketch, "E1640", {"start": v(91.3, 10.98) * mm, "end": v(91, 10.88) * mm});
            skLineSegment(sketch, "E1641", {"start": v(91, 10.88) * mm, "end": v(90.73, 10.74) * mm});
            skLineSegment(sketch, "E1642", {"start": v(90.73, 10.74) * mm, "end": v(90.47, 10.59) * mm});
            skLineSegment(sketch, "E1643", {"start": v(90.47, 10.59) * mm, "end": v(90.23, 10.4) * mm});
            skLineSegment(sketch, "E1644", {"start": v(90.23, 10.4) * mm, "end": v(90, 10.2) * mm});
            skLineSegment(sketch, "E1645", {"start": v(90, 10.2) * mm, "end": v(89.8, 9.98) * mm});
            skLineSegment(sketch, "E1646", {"start": v(89.8, 9.98) * mm, "end": v(89.63, 9.74) * mm});
            skLineSegment(sketch, "E1647", {"start": v(89.63, 9.74) * mm, "end": v(89.47, 9.48) * mm});
            skLineSegment(sketch, "E1648", {"start": v(89.47, 9.48) * mm, "end": v(89.34, 9.2) * mm});
            skLineSegment(sketch, "E1649", {"start": v(89.34, 9.2) * mm, "end": v(89.23, 8.92) * mm});
            skLineSegment(sketch, "E1650", {"start": v(89.23, 8.92) * mm, "end": v(89.15, 8.62) * mm});
            skLineSegment(sketch, "E1651", {"start": v(89.15, 8.62) * mm, "end": v(89.1, 8.3) * mm});
            skLineSegment(sketch, "E1652", {"start": v(89.1, 8.3) * mm, "end": v(89.1, 7.99) * mm});
            skLineSegment(sketch, "E1653", {"start": v(89.1, 7.99) * mm, "end": v(89.1, -20.04) * mm});
            skLineSegment(sketch, "E1654", {"start": v(89.1, -20.04) * mm, "end": v(89.1, -20.38) * mm});
            skLineSegment(sketch, "E1655", {"start": v(89.1, -20.38) * mm, "end": v(89.12, -20.72) * mm});
            skLineSegment(sketch, "E1656", {"start": v(89.12, -20.72) * mm, "end": v(89.16, -21.05) * mm});
            skLineSegment(sketch, "E1657", {"start": v(89.16, -21.05) * mm, "end": v(89.2, -21.37) * mm});
            skLineSegment(sketch, "E1658", {"start": v(89.2, -21.37) * mm, "end": v(89.27, -21.69) * mm});
            skLineSegment(sketch, "E1659", {"start": v(89.27, -21.69) * mm, "end": v(89.35, -22) * mm});
            skLineSegment(sketch, "E1660", {"start": v(89.35, -22) * mm, "end": v(89.44, -22.3) * mm});
            skLineSegment(sketch, "E1661", {"start": v(89.44, -22.3) * mm, "end": v(89.55, -22.6) * mm});
            skLineSegment(sketch, "E1662", {"start": v(89.55, -22.6) * mm, "end": v(89.67, -22.88) * mm});
            skLineSegment(sketch, "E1663", {"start": v(89.67, -22.88) * mm, "end": v(89.8, -23.15) * mm});
            skLineSegment(sketch, "E1664", {"start": v(89.8, -23.15) * mm, "end": v(89.96, -23.42) * mm});
            skLineSegment(sketch, "E1665", {"start": v(89.96, -23.42) * mm, "end": v(90.12, -23.69) * mm});
            skLineSegment(sketch, "E1666", {"start": v(90.12, -23.69) * mm, "end": v(90.3, -23.94) * mm});
            skLineSegment(sketch, "E1667", {"start": v(90.3, -23.94) * mm, "end": v(90.5, -24.19) * mm});
            skLineSegment(sketch, "E1668", {"start": v(90.5, -24.19) * mm, "end": v(90.7, -24.43) * mm});
            skLineSegment(sketch, "E1669", {"start": v(90.7, -24.43) * mm, "end": v(90.92, -24.66) * mm});
            skLineSegment(sketch, "E1670", {"start": v(90.92, -24.66) * mm, "end": v(91.15, -24.88) * mm});
            skLineSegment(sketch, "E1671", {"start": v(91.15, -24.88) * mm, "end": v(91.39, -25.09) * mm});
            skLineSegment(sketch, "E1672", {"start": v(91.39, -25.09) * mm, "end": v(91.64, -25.28) * mm});
            skLineSegment(sketch, "E1673", {"start": v(91.64, -25.28) * mm, "end": v(91.9, -25.46) * mm});
            skLineSegment(sketch, "E1674", {"start": v(91.9, -25.46) * mm, "end": v(92.15, -25.62) * mm});
            skLineSegment(sketch, "E1675", {"start": v(92.15, -25.62) * mm, "end": v(92.42, -25.77) * mm});
            skLineSegment(sketch, "E1676", {"start": v(92.42, -25.77) * mm, "end": v(92.7, -25.9) * mm});
            skLineSegment(sketch, "E1677", {"start": v(92.7, -25.9) * mm, "end": v(92.99, -26.03) * mm});
            skLineSegment(sketch, "E1678", {"start": v(92.99, -26.03) * mm, "end": v(93.28, -26.14) * mm});
            skLineSegment(sketch, "E1679", {"start": v(93.28, -26.14) * mm, "end": v(93.58, -26.23) * mm});
            skLineSegment(sketch, "E1680", {"start": v(93.58, -26.23) * mm, "end": v(93.9, -26.3) * mm});
            skLineSegment(sketch, "E1681", {"start": v(93.9, -26.3) * mm, "end": v(94.2, -26.37) * mm});
            skLineSegment(sketch, "E1682", {"start": v(94.2, -26.37) * mm, "end": v(94.53, -26.42) * mm});
            skLineSegment(sketch, "E1683", {"start": v(94.53, -26.42) * mm, "end": v(94.86, -26.46) * mm});
            skLineSegment(sketch, "E1684", {"start": v(94.86, -26.46) * mm, "end": v(95.2, -26.48) * mm});
            skLineSegment(sketch, "E1685", {"start": v(95.2, -26.48) * mm, "end": v(95.54, -26.49) * mm});
            skLineSegment(sketch, "E1686", {"start": v(95.54, -26.49) * mm, "end": v(126.33, -26.49) * mm});
            skLineSegment(sketch, "E1687", {"start": v(126.33, -26.49) * mm, "end": v(126.67, -26.47) * mm});
            skLineSegment(sketch, "E1688", {"start": v(126.67, -26.47) * mm, "end": v(127, -26.42) * mm});
            skLineSegment(sketch, "E1689", {"start": v(127, -26.42) * mm, "end": v(127.32, -26.34) * mm});
            skLineSegment(sketch, "E1690", {"start": v(127.32, -26.34) * mm, "end": v(127.63, -26.23) * mm});
            skLineSegment(sketch, "E1691", {"start": v(127.63, -26.23) * mm, "end": v(127.92, -26.09) * mm});
            skLineSegment(sketch, "E1692", {"start": v(127.92, -26.09) * mm, "end": v(128.2, -25.92) * mm});
            skLineSegment(sketch, "E1693", {"start": v(128.2, -25.92) * mm, "end": v(128.45, -25.73) * mm});
            skLineSegment(sketch, "E1694", {"start": v(128.45, -25.73) * mm, "end": v(128.69, -25.51) * mm});
            skLineSegment(sketch, "E1695", {"start": v(128.69, -25.51) * mm, "end": v(128.9, -25.27) * mm});
            skLineSegment(sketch, "E1696", {"start": v(128.9, -25.27) * mm, "end": v(129.1, -25.02) * mm});
            skLineSegment(sketch, "E1697", {"start": v(129.1, -25.02) * mm, "end": v(129.26, -24.74) * mm});
            skLineSegment(sketch, "E1698", {"start": v(129.26, -24.74) * mm, "end": v(129.4, -24.45) * mm});
            skLineSegment(sketch, "E1699", {"start": v(129.4, -24.45) * mm, "end": v(129.52, -24.14) * mm});
            skLineSegment(sketch, "E1700", {"start": v(129.52, -24.14) * mm, "end": v(129.6, -23.83) * mm});
            skLineSegment(sketch, "E1701", {"start": v(129.6, -23.83) * mm, "end": v(129.65, -23.5) * mm});
            skLineSegment(sketch, "E1702", {"start": v(129.65, -23.5) * mm, "end": v(129.67, -23.15) * mm});
            skLineSegment(sketch, "E1703", {"start": v(129.67, -23.15) * mm, "end": v(129.67, -19.84) * mm});
            skLineSegment(sketch, "E1704", {"start": v(129.67, -19.84) * mm, "end": v(129.66, -19.7) * mm});
            skLineSegment(sketch, "E1705", {"start": v(129.66, -19.7) * mm, "end": v(129.64, -19.56) * mm});
            skLineSegment(sketch, "E1706", {"start": v(129.64, -19.56) * mm, "end": v(129.6, -19.43) * mm});
            skLineSegment(sketch, "E1707", {"start": v(129.6, -19.43) * mm, "end": v(129.57, -19.3) * mm});
            skLineSegment(sketch, "E1708", {"start": v(129.57, -19.3) * mm, "end": v(129.51, -19.18) * mm});
            skLineSegment(sketch, "E1709", {"start": v(129.51, -19.18) * mm, "end": v(129.45, -19.06) * mm});
            skLineSegment(sketch, "E1710", {"start": v(129.45, -19.06) * mm, "end": v(129.37, -18.95) * mm});
            skLineSegment(sketch, "E1711", {"start": v(129.37, -18.95) * mm, "end": v(129.3, -18.85) * mm});
            skLineSegment(sketch, "E1712", {"start": v(129.3, -18.85) * mm, "end": v(129.2, -18.75) * mm});
            skLineSegment(sketch, "E1713", {"start": v(129.2, -18.75) * mm, "end": v(129.1, -18.67) * mm});
            skLineSegment(sketch, "E1714", {"start": v(129.1, -18.67) * mm, "end": v(129, -18.59) * mm});
            skLineSegment(sketch, "E1715", {"start": v(129, -18.59) * mm, "end": v(128.88, -18.52) * mm});
            skLineSegment(sketch, "E1716", {"start": v(128.88, -18.52) * mm, "end": v(128.76, -18.46) * mm});
            skLineSegment(sketch, "E1717", {"start": v(128.76, -18.46) * mm, "end": v(128.63, -18.41) * mm});
            skLineSegment(sketch, "E1718", {"start": v(128.63, -18.41) * mm, "end": v(128.5, -18.38) * mm});
            skLineSegment(sketch, "E1719", {"start": v(128.5, -18.38) * mm, "end": v(128.36, -18.35) * mm});
            skLineSegment(sketch, "E1720", {"start": v(128.36, -18.35) * mm, "end": v(127.64, -18.25) * mm});
            skLineSegment(sketch, "E1721", {"start": v(127.64, -18.25) * mm, "end": v(126.94, -18.1) * mm});
            skLineSegment(sketch, "E1722", {"start": v(126.94, -18.1) * mm, "end": v(126.25, -17.94) * mm});
            skLineSegment(sketch, "E1723", {"start": v(126.25, -17.94) * mm, "end": v(125.57, -17.74) * mm});
            skLineSegment(sketch, "E1724", {"start": v(125.57, -17.74) * mm, "end": v(124.9, -17.52) * mm});
            skLineSegment(sketch, "E1725", {"start": v(124.9, -17.52) * mm, "end": v(124.26, -17.26) * mm});
            skLineSegment(sketch, "E1726", {"start": v(124.26, -17.26) * mm, "end": v(123.63, -16.97) * mm});
            skLineSegment(sketch, "E1727", {"start": v(123.63, -16.97) * mm, "end": v(123.01, -16.66) * mm});
            skLineSegment(sketch, "E1728", {"start": v(123.01, -16.66) * mm, "end": v(122.41, -16.31) * mm});
            skLineSegment(sketch, "E1729", {"start": v(122.41, -16.31) * mm, "end": v(121.83, -15.94) * mm});
            skLineSegment(sketch, "E1730", {"start": v(121.83, -15.94) * mm, "end": v(121.25, -15.53) * mm});
            skLineSegment(sketch, "E1731", {"start": v(121.25, -15.53) * mm, "end": v(120.7, -15.1) * mm});
            skLineSegment(sketch, "E1732", {"start": v(120.7, -15.1) * mm, "end": v(120.16, -14.63) * mm});
            skLineSegment(sketch, "E1733", {"start": v(120.16, -14.63) * mm, "end": v(119.63, -14.14) * mm});
            skLineSegment(sketch, "E1734", {"start": v(119.63, -14.14) * mm, "end": v(119.13, -13.62) * mm});
            skLineSegment(sketch, "E1735", {"start": v(119.13, -13.62) * mm, "end": v(118.63, -13.07) * mm});
            skLineSegment(sketch, "E1736", {"start": v(118.63, -13.07) * mm, "end": v(118.17, -12.5) * mm});
            skLineSegment(sketch, "E1737", {"start": v(118.17, -12.5) * mm, "end": v(117.73, -11.91) * mm});
            skLineSegment(sketch, "E1738", {"start": v(117.73, -11.91) * mm, "end": v(117.32, -11.32) * mm});
            skLineSegment(sketch, "E1739", {"start": v(117.32, -11.32) * mm, "end": v(116.94, -10.71) * mm});
            skLineSegment(sketch, "E1740", {"start": v(116.94, -10.71) * mm, "end": v(116.59, -10.1) * mm});
            skLineSegment(sketch, "E1741", {"start": v(116.59, -10.1) * mm, "end": v(116.27, -9.47) * mm});
            skLineSegment(sketch, "E1742", {"start": v(116.27, -9.47) * mm, "end": v(115.98, -8.83) * mm});
            skLineSegment(sketch, "E1743", {"start": v(115.98, -8.83) * mm, "end": v(115.72, -8.18) * mm});
            skLineSegment(sketch, "E1744", {"start": v(115.72, -8.18) * mm, "end": v(115.5, -7.52) * mm});
            skLineSegment(sketch, "E1745", {"start": v(115.5, -7.52) * mm, "end": v(115.3, -6.85) * mm});
            skLineSegment(sketch, "E1746", {"start": v(115.3, -6.85) * mm, "end": v(115.13, -6.17) * mm});
            skLineSegment(sketch, "E1747", {"start": v(115.13, -6.17) * mm, "end": v(114.99, -5.49) * mm});
            skLineSegment(sketch, "E1748", {"start": v(114.99, -5.49) * mm, "end": v(114.88, -4.79) * mm});
            skLineSegment(sketch, "E1749", {"start": v(114.88, -4.79) * mm, "end": v(114.8, -4.08) * mm});
            skLineSegment(sketch, "E1750", {"start": v(114.8, -4.08) * mm, "end": v(114.76, -3.36) * mm});
            skLineSegment(sketch, "E1751", {"start": v(114.76, -3.36) * mm, "end": v(114.74, -2.63) * mm});
            skLineSegment(sketch, "E1752", {"start": v(114.74, -2.63) * mm, "end": v(114.76, -1.81) * mm});
            skLineSegment(sketch, "E1753", {"start": v(114.76, -1.81) * mm, "end": v(114.82, -1) * mm});
            skLineSegment(sketch, "E1754", {"start": v(114.82, -1) * mm, "end": v(114.9, -0.22) * mm});
            skLineSegment(sketch, "E1755", {"start": v(114.9, -0.22) * mm, "end": v(115.03, 0.55) * mm});
            skLineSegment(sketch, "E1756", {"start": v(115.03, 0.55) * mm, "end": v(115.2, 1.31) * mm});
            skLineSegment(sketch, "E1757", {"start": v(115.2, 1.31) * mm, "end": v(115.4, 2.06) * mm});
            skLineSegment(sketch, "E1758", {"start": v(115.4, 2.06) * mm, "end": v(115.63, 2.79) * mm});
            skLineSegment(sketch, "E1759", {"start": v(115.63, 2.79) * mm, "end": v(115.9, 3.5) * mm});
            skLineSegment(sketch, "E1760", {"start": v(115.9, 3.5) * mm, "end": v(116.21, 4.2) * mm});
            skLineSegment(sketch, "E1761", {"start": v(116.21, 4.2) * mm, "end": v(116.56, 4.88) * mm});
            skLineSegment(sketch, "E1762", {"start": v(116.56, 4.88) * mm, "end": v(116.94, 5.55) * mm});
            skLineSegment(sketch, "E1763", {"start": v(116.94, 5.55) * mm, "end": v(117.35, 6.2) * mm});
            skLineSegment(sketch, "E1764", {"start": v(117.35, 6.2) * mm, "end": v(117.8, 6.84) * mm});
            skLineSegment(sketch, "E1765", {"start": v(117.8, 6.84) * mm, "end": v(118.3, 7.46) * mm});
            skLineSegment(sketch, "E1766", {"start": v(118.3, 7.46) * mm, "end": v(118.81, 8.06) * mm});
            skLineSegment(sketch, "E1767", {"start": v(118.81, 8.06) * mm, "end": v(119.37, 8.65) * mm});
            skLineSegment(sketch, "E1768", {"start": v(119.37, 8.65) * mm, "end": v(119.95, 9.21) * mm});
            skLineSegment(sketch, "E1769", {"start": v(119.95, 9.21) * mm, "end": v(120.56, 9.74) * mm});
            skLineSegment(sketch, "E1770", {"start": v(120.56, 9.74) * mm, "end": v(121.17, 10.23) * mm});
            skLineSegment(sketch, "E1771", {"start": v(121.17, 10.23) * mm, "end": v(121.8, 10.68) * mm});
            skLineSegment(sketch, "E1772", {"start": v(121.8, 10.68) * mm, "end": v(122.46, 11.1) * mm});
            skLineSegment(sketch, "E1773", {"start": v(122.46, 11.1) * mm, "end": v(123.12, 11.48) * mm});
            skLineSegment(sketch, "E1774", {"start": v(123.12, 11.48) * mm, "end": v(123.8, 11.83) * mm});
            skLineSegment(sketch, "E1775", {"start": v(123.8, 11.83) * mm, "end": v(124.5, 12.14) * mm});
            skLineSegment(sketch, "E1776", {"start": v(124.5, 12.14) * mm, "end": v(125.21, 12.4) * mm});
            skLineSegment(sketch, "E1777", {"start": v(125.21, 12.4) * mm, "end": v(125.94, 12.65) * mm});
            skLineSegment(sketch, "E1778", {"start": v(125.94, 12.65) * mm, "end": v(126.68, 12.85) * mm});
            skLineSegment(sketch, "E1779", {"start": v(126.68, 12.85) * mm, "end": v(127.44, 13.01) * mm});
            skLineSegment(sketch, "E1780", {"start": v(127.44, 13.01) * mm, "end": v(128.22, 13.14) * mm});
            skLineSegment(sketch, "E1781", {"start": v(128.22, 13.14) * mm, "end": v(129, 13.23) * mm});
            skLineSegment(sketch, "E1782", {"start": v(129, 13.23) * mm, "end": v(129.8, 13.29) * mm});
            skLineSegment(sketch, "E1783", {"start": v(129.8, 13.29) * mm, "end": v(130.62, 13.3) * mm});
            skLineSegment(sketch, "E1784", {"start": v(130.62, 13.3) * mm, "end": v(131.45, 13.29) * mm});
            skLineSegment(sketch, "E1785", {"start": v(131.45, 13.29) * mm, "end": v(132.26, 13.23) * mm});
            skLineSegment(sketch, "E1786", {"start": v(132.26, 13.23) * mm, "end": v(133.05, 13.14) * mm});
            skLineSegment(sketch, "E1787", {"start": v(133.05, 13.14) * mm, "end": v(133.83, 13.01) * mm});
            skLineSegment(sketch, "E1788", {"start": v(133.83, 13.01) * mm, "end": v(134.6, 12.85) * mm});
            skLineSegment(sketch, "E1789", {"start": v(134.6, 12.85) * mm, "end": v(135.34, 12.65) * mm});
            skLineSegment(sketch, "E1790", {"start": v(135.34, 12.65) * mm, "end": v(136.07, 12.41) * mm});
            skLineSegment(sketch, "E1791", {"start": v(136.07, 12.41) * mm, "end": v(136.79, 12.14) * mm});
            skLineSegment(sketch, "E1792", {"start": v(136.79, 12.14) * mm, "end": v(137.49, 11.83) * mm});
            skLineSegment(sketch, "E1793", {"start": v(137.49, 11.83) * mm, "end": v(138.17, 11.5) * mm});
            skLineSegment(sketch, "E1794", {"start": v(138.17, 11.5) * mm, "end": v(138.84, 11.11) * mm});
            skLineSegment(sketch, "E1795", {"start": v(138.84, 11.11) * mm, "end": v(139.5, 10.7) * mm});
            skLineSegment(sketch, "E1796", {"start": v(139.5, 10.7) * mm, "end": v(140.13, 10.24) * mm});
            skLineSegment(sketch, "E1797", {"start": v(140.13, 10.24) * mm, "end": v(140.74, 9.76) * mm});
            skLineSegment(sketch, "E1798", {"start": v(140.74, 9.76) * mm, "end": v(141.35, 9.24) * mm});
            skLineSegment(sketch, "E1799", {"start": v(141.35, 9.24) * mm, "end": v(141.93, 8.68) * mm});
            skLineSegment(sketch, "E1800", {"start": v(141.93, 8.68) * mm, "end": v(142.49, 8.1) * mm});
            skLineSegment(sketch, "E1801", {"start": v(142.49, 8.1) * mm, "end": v(143.01, 7.5) * mm});
            skLineSegment(sketch, "E1802", {"start": v(143.01, 7.5) * mm, "end": v(143.5, 6.87) * mm});
            skLineSegment(sketch, "E1803", {"start": v(143.5, 6.87) * mm, "end": v(143.95, 6.24) * mm});
            skLineSegment(sketch, "E1804", {"start": v(143.95, 6.24) * mm, "end": v(144.36, 5.59) * mm});
            skLineSegment(sketch, "E1805", {"start": v(144.36, 5.59) * mm, "end": v(144.74, 4.92) * mm});
            skLineSegment(sketch, "E1806", {"start": v(144.74, 4.92) * mm, "end": v(145.09, 4.23) * mm});
            skLineSegment(sketch, "E1807", {"start": v(145.09, 4.23) * mm, "end": v(145.4, 3.53) * mm});
            skLineSegment(sketch, "E1808", {"start": v(145.4, 3.53) * mm, "end": v(145.67, 2.82) * mm});
            skLineSegment(sketch, "E1809", {"start": v(145.67, 2.82) * mm, "end": v(145.9, 2.09) * mm});
            skLineSegment(sketch, "E1810", {"start": v(145.9, 2.09) * mm, "end": v(146.1, 1.34) * mm});
            skLineSegment(sketch, "E1811", {"start": v(146.1, 1.34) * mm, "end": v(146.27, 0.57) * mm});
            skLineSegment(sketch, "E1812", {"start": v(146.27, 0.57) * mm, "end": v(146.4, -0.2) * mm});
            skLineSegment(sketch, "E1813", {"start": v(146.4, -0.2) * mm, "end": v(146.48, -1) * mm});
            skLineSegment(sketch, "E1814", {"start": v(146.48, -1) * mm, "end": v(146.54, -1.8) * mm});
            skLineSegment(sketch, "E1815", {"start": v(146.54, -1.8) * mm, "end": v(146.56, -2.63) * mm});
            skLineSegment(sketch, "E1816", {"start": v(146.56, -2.63) * mm, "end": v(146.54, -3.36) * mm});
            skLineSegment(sketch, "E1817", {"start": v(146.54, -3.36) * mm, "end": v(146.5, -4.08) * mm});
            skLineSegment(sketch, "E1818", {"start": v(146.5, -4.08) * mm, "end": v(146.42, -4.79) * mm});
            skLineSegment(sketch, "E1819", {"start": v(146.42, -4.79) * mm, "end": v(146.31, -5.48) * mm});
            skLineSegment(sketch, "E1820", {"start": v(146.31, -5.48) * mm, "end": v(146.17, -6.17) * mm});
            skLineSegment(sketch, "E1821", {"start": v(146.17, -6.17) * mm, "end": v(146, -6.85) * mm});
            skLineSegment(sketch, "E1822", {"start": v(146, -6.85) * mm, "end": v(145.8, -7.52) * mm});
            skLineSegment(sketch, "E1823", {"start": v(145.8, -7.52) * mm, "end": v(145.58, -8.18) * mm});
            skLineSegment(sketch, "E1824", {"start": v(145.58, -8.18) * mm, "end": v(145.32, -8.83) * mm});
            skLineSegment(sketch, "E1825", {"start": v(145.32, -8.83) * mm, "end": v(145.03, -9.47) * mm});
            skLineSegment(sketch, "E1826", {"start": v(145.03, -9.47) * mm, "end": v(144.7, -10.1) * mm});
            skLineSegment(sketch, "E1827", {"start": v(144.7, -10.1) * mm, "end": v(144.36, -10.71) * mm});
            skLineSegment(sketch, "E1828", {"start": v(144.36, -10.71) * mm, "end": v(143.97, -11.32) * mm});
            skLineSegment(sketch, "E1829", {"start": v(143.97, -11.32) * mm, "end": v(143.56, -11.91) * mm});
            skLineSegment(sketch, "E1830", {"start": v(143.56, -11.91) * mm, "end": v(143.12, -12.5) * mm});
            skLineSegment(sketch, "E1831", {"start": v(143.12, -12.5) * mm, "end": v(142.65, -13.07) * mm});
            skLineSegment(sketch, "E1832", {"start": v(142.65, -13.07) * mm, "end": v(142.16, -13.62) * mm});
            skLineSegment(sketch, "E1833", {"start": v(142.16, -13.62) * mm, "end": v(141.65, -14.14) * mm});
            skLineSegment(sketch, "E1834", {"start": v(141.65, -14.14) * mm, "end": v(141.12, -14.63) * mm});
            skLineSegment(sketch, "E1835", {"start": v(141.12, -14.63) * mm, "end": v(140.58, -15.1) * mm});
            skLineSegment(sketch, "E1836", {"start": v(140.58, -15.1) * mm, "end": v(140.02, -15.53) * mm});
            skLineSegment(sketch, "E1837", {"start": v(140.02, -15.53) * mm, "end": v(139.45, -15.94) * mm});
            skLineSegment(sketch, "E1838", {"start": v(139.45, -15.94) * mm, "end": v(138.86, -16.31) * mm});
            skLineSegment(sketch, "E1839", {"start": v(138.86, -16.31) * mm, "end": v(138.26, -16.66) * mm});
            skLineSegment(sketch, "E1840", {"start": v(138.26, -16.66) * mm, "end": v(137.64, -16.97) * mm});
            skLineSegment(sketch, "E1841", {"start": v(137.64, -16.97) * mm, "end": v(137, -17.26) * mm});
            skLineSegment(sketch, "E1842", {"start": v(137, -17.26) * mm, "end": v(136.35, -17.52) * mm});
            skLineSegment(sketch, "E1843", {"start": v(136.35, -17.52) * mm, "end": v(135.69, -17.74) * mm});
            skLineSegment(sketch, "E1844", {"start": v(135.69, -17.74) * mm, "end": v(135.01, -17.94) * mm});
            skLineSegment(sketch, "E1845", {"start": v(135.01, -17.94) * mm, "end": v(134.32, -18.1) * mm});
            skLineSegment(sketch, "E1846", {"start": v(134.32, -18.1) * mm, "end": v(133.6, -18.25) * mm});
            skLineSegment(sketch, "E1847", {"start": v(133.6, -18.25) * mm, "end": v(132.89, -18.35) * mm});
            skLineSegment(sketch, "E1848", {"start": v(132.89, -18.35) * mm, "end": v(132.75, -18.38) * mm});
            skLineSegment(sketch, "E1849", {"start": v(132.75, -18.38) * mm, "end": v(132.62, -18.41) * mm});
            skLineSegment(sketch, "E1850", {"start": v(132.62, -18.41) * mm, "end": v(132.5, -18.46) * mm});
            skLineSegment(sketch, "E1851", {"start": v(132.5, -18.46) * mm, "end": v(132.37, -18.52) * mm});
            skLineSegment(sketch, "E1852", {"start": v(132.37, -18.52) * mm, "end": v(132.25, -18.59) * mm});
            skLineSegment(sketch, "E1853", {"start": v(132.25, -18.59) * mm, "end": v(132.15, -18.67) * mm});
            skLineSegment(sketch, "E1854", {"start": v(132.15, -18.67) * mm, "end": v(132.05, -18.75) * mm});
            skLineSegment(sketch, "E1855", {"start": v(132.05, -18.75) * mm, "end": v(131.96, -18.85) * mm});
            skLineSegment(sketch, "E1856", {"start": v(131.96, -18.85) * mm, "end": v(131.87, -18.95) * mm});
            skLineSegment(sketch, "E1857", {"start": v(131.87, -18.95) * mm, "end": v(131.8, -19.06) * mm});
            skLineSegment(sketch, "E1858", {"start": v(131.8, -19.06) * mm, "end": v(131.73, -19.18) * mm});
            skLineSegment(sketch, "E1859", {"start": v(131.73, -19.18) * mm, "end": v(131.68, -19.3) * mm});
            skLineSegment(sketch, "E1860", {"start": v(131.68, -19.3) * mm, "end": v(131.64, -19.43) * mm});
            skLineSegment(sketch, "E1861", {"start": v(131.64, -19.43) * mm, "end": v(131.6, -19.56) * mm});
            skLineSegment(sketch, "E1862", {"start": v(131.6, -19.56) * mm, "end": v(131.59, -19.7) * mm});
            skLineSegment(sketch, "E1863", {"start": v(131.59, -19.7) * mm, "end": v(131.58, -19.84) * mm});
            skLineSegment(sketch, "E1864", {"start": v(131.58, -19.84) * mm, "end": v(131.58, -23.15) * mm});
            skLineSegment(sketch, "E1865", {"start": v(131.58, -23.15) * mm, "end": v(131.6, -23.5) * mm});
            skLineSegment(sketch, "E1866", {"start": v(131.6, -23.5) * mm, "end": v(131.65, -23.83) * mm});
            skLineSegment(sketch, "E1867", {"start": v(131.65, -23.83) * mm, "end": v(131.73, -24.14) * mm});
            skLineSegment(sketch, "E1868", {"start": v(131.73, -24.14) * mm, "end": v(131.84, -24.45) * mm});
            skLineSegment(sketch, "E1869", {"start": v(131.84, -24.45) * mm, "end": v(131.99, -24.74) * mm});
            skLineSegment(sketch, "E1870", {"start": v(131.99, -24.74) * mm, "end": v(132.15, -25.02) * mm});
            skLineSegment(sketch, "E1871", {"start": v(132.15, -25.02) * mm, "end": v(132.34, -25.27) * mm});
            skLineSegment(sketch, "E1872", {"start": v(132.34, -25.27) * mm, "end": v(132.56, -25.51) * mm});
            skLineSegment(sketch, "E1873", {"start": v(132.56, -25.51) * mm, "end": v(132.8, -25.73) * mm});
            skLineSegment(sketch, "E1874", {"start": v(132.8, -25.73) * mm, "end": v(133.05, -25.92) * mm});
            skLineSegment(sketch, "E1875", {"start": v(133.05, -25.92) * mm, "end": v(133.33, -26.09) * mm});
            skLineSegment(sketch, "E1876", {"start": v(133.33, -26.09) * mm, "end": v(133.62, -26.23) * mm});
            skLineSegment(sketch, "E1877", {"start": v(133.62, -26.23) * mm, "end": v(133.93, -26.34) * mm});
            skLineSegment(sketch, "E1878", {"start": v(133.93, -26.34) * mm, "end": v(134.25, -26.42) * mm});
            skLineSegment(sketch, "E1879", {"start": v(134.25, -26.42) * mm, "end": v(134.58, -26.47) * mm});
            skLineSegment(sketch, "E1880", {"start": v(134.58, -26.47) * mm, "end": v(134.92, -26.49) * mm});
            skLineSegment(sketch, "E1881", {"start": v(134.92, -26.49) * mm, "end": v(153.43, -26.49) * mm});
            skLineSegment(sketch, "E1882", {"start": v(153.43, -26.49) * mm, "end": v(153.64, -26.48) * mm});
            skLineSegment(sketch, "E1883", {"start": v(153.64, -26.48) * mm, "end": v(153.85, -26.47) * mm});
            skLineSegment(sketch, "E1884", {"start": v(153.85, -26.47) * mm, "end": v(154.06, -26.45) * mm});
            skLineSegment(sketch, "E1885", {"start": v(154.06, -26.45) * mm, "end": v(154.26, -26.42) * mm});
            skLineSegment(sketch, "E1886", {"start": v(154.26, -26.42) * mm, "end": v(154.45, -26.38) * mm});
            skLineSegment(sketch, "E1887", {"start": v(154.45, -26.38) * mm, "end": v(154.64, -26.33) * mm});
            skLineSegment(sketch, "E1888", {"start": v(154.64, -26.33) * mm, "end": v(154.83, -26.27) * mm});
            skLineSegment(sketch, "E1889", {"start": v(154.83, -26.27) * mm, "end": v(155, -26.2) * mm});
            skLineSegment(sketch, "E1890", {"start": v(155, -26.2) * mm, "end": v(155.19, -26.13) * mm});
            skLineSegment(sketch, "E1891", {"start": v(155.19, -26.13) * mm, "end": v(155.36, -26.05) * mm});
            skLineSegment(sketch, "E1892", {"start": v(155.36, -26.05) * mm, "end": v(155.52, -25.96) * mm});
            skLineSegment(sketch, "E1893", {"start": v(155.52, -25.96) * mm, "end": v(155.68, -25.86) * mm});
            skLineSegment(sketch, "E1894", {"start": v(155.68, -25.86) * mm, "end": v(155.84, -25.75) * mm});
            skLineSegment(sketch, "E1895", {"start": v(155.84, -25.75) * mm, "end": v(156, -25.63) * mm});
            skLineSegment(sketch, "E1896", {"start": v(156, -25.63) * mm, "end": v(156.14, -25.5) * mm});
            skLineSegment(sketch, "E1897", {"start": v(156.14, -25.5) * mm, "end": v(156.28, -25.37) * mm});
            skLineSegment(sketch, "E1898", {"start": v(156.28, -25.37) * mm, "end": v(156.41, -25.23) * mm});
            skLineSegment(sketch, "E1899", {"start": v(156.41, -25.23) * mm, "end": v(156.54, -25.09) * mm});
            skLineSegment(sketch, "E1900", {"start": v(156.54, -25.09) * mm, "end": v(156.66, -24.94) * mm});
            skLineSegment(sketch, "E1901", {"start": v(156.66, -24.94) * mm, "end": v(156.77, -24.78) * mm});
            skLineSegment(sketch, "E1902", {"start": v(156.77, -24.78) * mm, "end": v(156.87, -24.62) * mm});
            skLineSegment(sketch, "E1903", {"start": v(156.87, -24.62) * mm, "end": v(156.96, -24.45) * mm});
            skLineSegment(sketch, "E1904", {"start": v(156.96, -24.45) * mm, "end": v(157.04, -24.28) * mm});
            skLineSegment(sketch, "E1905", {"start": v(157.04, -24.28) * mm, "end": v(157.11, -24.1) * mm});
            skLineSegment(sketch, "E1906", {"start": v(157.11, -24.1) * mm, "end": v(157.18, -23.92) * mm});
            skLineSegment(sketch, "E1907", {"start": v(157.18, -23.92) * mm, "end": v(157.24, -23.74) * mm});
            skLineSegment(sketch, "E1908", {"start": v(157.24, -23.74) * mm, "end": v(157.28, -23.55) * mm});
            skLineSegment(sketch, "E1909", {"start": v(157.28, -23.55) * mm, "end": v(157.32, -23.35) * mm});
            skLineSegment(sketch, "E1910", {"start": v(157.32, -23.35) * mm, "end": v(157.35, -23.15) * mm});
            skLineSegment(sketch, "E1911", {"start": v(157.35, -23.15) * mm, "end": v(157.38, -22.95) * mm});
            skLineSegment(sketch, "E1912", {"start": v(157.38, -22.95) * mm, "end": v(157.39, -22.74) * mm});
            skLineSegment(sketch, "E1913", {"start": v(157.39, -22.74) * mm, "end": v(157.4, -22.53) * mm});
            skLineSegment(sketch, "E1914", {"start": v(157.4, -22.53) * mm, "end": v(157.4, 12.26) * mm});
            skLineSegment(sketch, "E1915", {"start": v(157.4, 12.26) * mm, "end": v(157.4, 12.34) * mm});
            skLineSegment(sketch, "E1916", {"start": v(157.4, 12.34) * mm, "end": v(157.4, 12.42) * mm});
            skLineSegment(sketch, "E1917", {"start": v(157.4, 12.42) * mm, "end": v(157.43, 12.5) * mm});
            skLineSegment(sketch, "E1918", {"start": v(157.43, 12.5) * mm, "end": v(157.45, 12.57) * mm});
            skLineSegment(sketch, "E1919", {"start": v(157.45, 12.57) * mm, "end": v(157.49, 12.63) * mm});
            skLineSegment(sketch, "E1920", {"start": v(157.49, 12.63) * mm, "end": v(157.53, 12.7) * mm});
            skLineSegment(sketch, "E1921", {"start": v(157.53, 12.7) * mm, "end": v(157.57, 12.76) * mm});
            skLineSegment(sketch, "E1922", {"start": v(157.57, 12.76) * mm, "end": v(157.62, 12.81) * mm});
            skLineSegment(sketch, "E1923", {"start": v(157.62, 12.81) * mm, "end": v(157.68, 12.86) * mm});
            skLineSegment(sketch, "E1924", {"start": v(157.68, 12.86) * mm, "end": v(157.74, 12.9) * mm});
            skLineSegment(sketch, "E1925", {"start": v(157.74, 12.9) * mm, "end": v(157.8, 12.95) * mm});
            skLineSegment(sketch, "E1926", {"start": v(157.8, 12.95) * mm, "end": v(157.87, 12.98) * mm});
            skLineSegment(sketch, "E1927", {"start": v(157.87, 12.98) * mm, "end": v(157.94, 13) * mm});
            skLineSegment(sketch, "E1928", {"start": v(157.94, 13) * mm, "end": v(158.01, 13.02) * mm});
            skLineSegment(sketch, "E1929", {"start": v(158.01, 13.02) * mm, "end": v(158.09, 13.04) * mm});
            skLineSegment(sketch, "E1930", {"start": v(158.09, 13.04) * mm, "end": v(158.17, 13.04) * mm});
            skLineSegment(sketch, "E1931", {"start": v(158.17, 13.04) * mm, "end": v(171, 13.04) * mm});
            skLineSegment(sketch, "E1932", {"start": v(171, 13.04) * mm, "end": v(171.28, 13.02) * mm});
            skLineSegment(sketch, "E1933", {"start": v(171.28, 13.02) * mm, "end": v(171.55, 13) * mm});
            skLineSegment(sketch, "E1934", {"start": v(171.55, 13) * mm, "end": v(171.83, 12.97) * mm});
            skLineSegment(sketch, "E1935", {"start": v(171.83, 12.97) * mm, "end": v(172.1, 12.93) * mm});
            skLineSegment(sketch, "E1936", {"start": v(172.1, 12.93) * mm, "end": v(172.37, 12.88) * mm});
            skLineSegment(sketch, "E1937", {"start": v(172.37, 12.88) * mm, "end": v(172.65, 12.83) * mm});
            skLineSegment(sketch, "E1938", {"start": v(172.65, 12.83) * mm, "end": v(172.92, 12.76) * mm});
            skLineSegment(sketch, "E1939", {"start": v(172.92, 12.76) * mm, "end": v(173.2, 12.7) * mm});
            skLineSegment(sketch, "E1940", {"start": v(173.2, 12.7) * mm, "end": v(173.46, 12.6) * mm});
            skLineSegment(sketch, "E1941", {"start": v(173.46, 12.6) * mm, "end": v(173.73, 12.52) * mm});
            skLineSegment(sketch, "E1942", {"start": v(173.73, 12.52) * mm, "end": v(174, 12.42) * mm});
            skLineSegment(sketch, "E1943", {"start": v(174, 12.42) * mm, "end": v(174.27, 12.31) * mm});
            skLineSegment(sketch, "E1944", {"start": v(174.27, 12.31) * mm, "end": v(174.54, 12.2) * mm});
            skLineSegment(sketch, "E1945", {"start": v(174.54, 12.2) * mm, "end": v(174.81, 12.07) * mm});
            skLineSegment(sketch, "E1946", {"start": v(174.81, 12.07) * mm, "end": v(175.08, 11.94) * mm});
            skLineSegment(sketch, "E1947", {"start": v(175.08, 11.94) * mm, "end": v(175.56, 11.67) * mm});
            skLineSegment(sketch, "E1948", {"start": v(175.56, 11.67) * mm, "end": v(176.02, 11.37) * mm});
            skLineSegment(sketch, "E1949", {"start": v(176.02, 11.37) * mm, "end": v(176.44, 11.05) * mm});
            skLineSegment(sketch, "E1950", {"start": v(176.44, 11.05) * mm, "end": v(176.83, 10.7) * mm});
            skLineSegment(sketch, "E1951", {"start": v(176.83, 10.7) * mm, "end": v(177.2, 10.33) * mm});
            skLineSegment(sketch, "E1952", {"start": v(177.2, 10.33) * mm, "end": v(177.52, 9.94) * mm});
            skLineSegment(sketch, "E1953", {"start": v(177.52, 9.94) * mm, "end": v(177.82, 9.52) * mm});
            skLineSegment(sketch, "E1954", {"start": v(177.82, 9.52) * mm, "end": v(178.1, 9.08) * mm});
            skLineSegment(sketch, "E1955", {"start": v(178.1, 9.08) * mm, "end": v(178.33, 8.6) * mm});
            skLineSegment(sketch, "E1956", {"start": v(178.33, 8.6) * mm, "end": v(178.53, 8.12) * mm});
            skLineSegment(sketch, "E1957", {"start": v(178.53, 8.12) * mm, "end": v(178.7, 7.6) * mm});
            skLineSegment(sketch, "E1958", {"start": v(178.7, 7.6) * mm, "end": v(178.85, 7.06) * mm});
            skLineSegment(sketch, "E1959", {"start": v(178.85, 7.06) * mm, "end": v(178.96, 6.5) * mm});
            skLineSegment(sketch, "E1960", {"start": v(178.96, 6.5) * mm, "end": v(179.04, 5.92) * mm});
            skLineSegment(sketch, "E1961", {"start": v(179.04, 5.92) * mm, "end": v(179.09, 5.3) * mm});
            skLineSegment(sketch, "E1962", {"start": v(179.09, 5.3) * mm, "end": v(179.1, 4.67) * mm});
            skLineSegment(sketch, "E1963", {"start": v(179.1, 4.67) * mm, "end": v(179.09, 4.04) * mm});
            skLineSegment(sketch, "E1964", {"start": v(179.09, 4.04) * mm, "end": v(179.04, 3.43) * mm});
            skLineSegment(sketch, "E1965", {"start": v(179.04, 3.43) * mm, "end": v(178.96, 2.85) * mm});
            skLineSegment(sketch, "E1966", {"start": v(178.96, 2.85) * mm, "end": v(178.85, 2.28) * mm});
            skLineSegment(sketch, "E1967", {"start": v(178.85, 2.28) * mm, "end": v(178.7, 1.74) * mm});
            skLineSegment(sketch, "E1968", {"start": v(178.7, 1.74) * mm, "end": v(178.53, 1.23) * mm});
            skLineSegment(sketch, "E1969", {"start": v(178.53, 1.23) * mm, "end": v(178.33, 0.74) * mm});
            skLineSegment(sketch, "E1970", {"start": v(178.33, 0.74) * mm, "end": v(178.1, 0.27) * mm});
            skLineSegment(sketch, "E1971", {"start": v(178.1, 0.27) * mm, "end": v(177.82, -0.17) * mm});
            skLineSegment(sketch, "E1972", {"start": v(177.82, -0.17) * mm, "end": v(177.52, -0.6) * mm});
            skLineSegment(sketch, "E1973", {"start": v(177.52, -0.6) * mm, "end": v(177.2, -0.99) * mm});
            skLineSegment(sketch, "E1974", {"start": v(177.2, -0.99) * mm, "end": v(176.83, -1.36) * mm});
            skLineSegment(sketch, "E1975", {"start": v(176.83, -1.36) * mm, "end": v(176.44, -1.7) * mm});
            skLineSegment(sketch, "E1976", {"start": v(176.44, -1.7) * mm, "end": v(176.02, -2.02) * mm});
            skLineSegment(sketch, "E1977", {"start": v(176.02, -2.02) * mm, "end": v(175.57, -2.32) * mm});
            skLineSegment(sketch, "E1978", {"start": v(175.57, -2.32) * mm, "end": v(175.08, -2.6) * mm});
            skLineSegment(sketch, "E1979", {"start": v(175.08, -2.6) * mm, "end": v(174.8, -2.73) * mm});
            skLineSegment(sketch, "E1980", {"start": v(174.8, -2.73) * mm, "end": v(174.52, -2.86) * mm});
            skLineSegment(sketch, "E1981", {"start": v(174.52, -2.86) * mm, "end": v(174.24, -2.98) * mm});
            skLineSegment(sketch, "E1982", {"start": v(174.24, -2.98) * mm, "end": v(173.97, -3.1) * mm});
            skLineSegment(sketch, "E1983", {"start": v(173.97, -3.1) * mm, "end": v(173.7, -3.2) * mm});
            skLineSegment(sketch, "E1984", {"start": v(173.7, -3.2) * mm, "end": v(173.41, -3.3) * mm});
            skLineSegment(sketch, "E1985", {"start": v(173.41, -3.3) * mm, "end": v(173.14, -3.38) * mm});
            skLineSegment(sketch, "E1986", {"start": v(173.14, -3.38) * mm, "end": v(172.87, -3.46) * mm});
            skLineSegment(sketch, "E1987", {"start": v(172.87, -3.46) * mm, "end": v(172.6, -3.52) * mm});
            skLineSegment(sketch, "E1988", {"start": v(172.6, -3.52) * mm, "end": v(172.33, -3.58) * mm});
            skLineSegment(sketch, "E1989", {"start": v(172.33, -3.58) * mm, "end": v(172.06, -3.63) * mm});
            skLineSegment(sketch, "E1990", {"start": v(172.06, -3.63) * mm, "end": v(171.79, -3.67) * mm});
            skLineSegment(sketch, "E1991", {"start": v(171.79, -3.67) * mm, "end": v(171.52, -3.7) * mm});
            skLineSegment(sketch, "E1992", {"start": v(171.52, -3.7) * mm, "end": v(171.26, -3.73) * mm});
            skLineSegment(sketch, "E1993", {"start": v(171.26, -3.73) * mm, "end": v(171, -3.74) * mm});
            skLineSegment(sketch, "E1994", {"start": v(171, -3.74) * mm, "end": v(161.26, -3.75) * mm});
            skLineSegment(sketch, "E1995", {"start": v(161.26, -3.75) * mm, "end": v(161.12, -3.75) * mm});
            skLineSegment(sketch, "E1996", {"start": v(161.12, -3.75) * mm, "end": v(160.99, -3.77) * mm});
            skLineSegment(sketch, "E1997", {"start": v(160.99, -3.77) * mm, "end": v(160.85, -3.8) * mm});
            skLineSegment(sketch, "E1998", {"start": v(160.85, -3.8) * mm, "end": v(160.73, -3.85) * mm});
            skLineSegment(sketch, "E1999", {"start": v(160.73, -3.85) * mm, "end": v(160.6, -3.91) * mm});
            skLineSegment(sketch, "E2000", {"start": v(160.6, -3.91) * mm, "end": v(160.5, -3.98) * mm});
            skLineSegment(sketch, "E2001", {"start": v(160.5, -3.98) * mm, "end": v(160.4, -4.06) * mm});
            skLineSegment(sketch, "E2002", {"start": v(160.4, -4.06) * mm, "end": v(160.3, -4.15) * mm});
            skLineSegment(sketch, "E2003", {"start": v(160.3, -4.15) * mm, "end": v(160.2, -4.24) * mm});
            skLineSegment(sketch, "E2004", {"start": v(160.2, -4.24) * mm, "end": v(160.13, -4.35) * mm});
            skLineSegment(sketch, "E2005", {"start": v(160.13, -4.35) * mm, "end": v(160.06, -4.46) * mm});
            skLineSegment(sketch, "E2006", {"start": v(160.06, -4.46) * mm, "end": v(160, -4.58) * mm});
            skLineSegment(sketch, "E2007", {"start": v(160, -4.58) * mm, "end": v(159.95, -4.7) * mm});
            skLineSegment(sketch, "E2008", {"start": v(159.95, -4.7) * mm, "end": v(159.92, -4.84) * mm});
            skLineSegment(sketch, "E2009", {"start": v(159.92, -4.84) * mm, "end": v(159.9, -4.98) * mm});
            skLineSegment(sketch, "E2010", {"start": v(159.9, -4.98) * mm, "end": v(159.9, -5.11) * mm});
            skLineSegment(sketch, "E2011", {"start": v(159.9, -5.11) * mm, "end": v(159.9, -5.43) * mm});
            skLineSegment(sketch, "E2012", {"start": v(159.9, -5.43) * mm, "end": v(159.9, -5.55) * mm});
            skLineSegment(sketch, "E2013", {"start": v(159.9, -5.55) * mm, "end": v(159.9, -5.67) * mm});
            skLineSegment(sketch, "E2014", {"start": v(159.9, -5.67) * mm, "end": v(159.92, -5.79) * mm});
            skLineSegment(sketch, "E2015", {"start": v(159.92, -5.79) * mm, "end": v(159.94, -5.9) * mm});
            skLineSegment(sketch, "E2016", {"start": v(159.94, -5.9) * mm, "end": v(159.97, -6.02) * mm});
            skLineSegment(sketch, "E2017", {"start": v(159.97, -6.02) * mm, "end": v(160, -6.13) * mm});
            skLineSegment(sketch, "E2018", {"start": v(160, -6.13) * mm, "end": v(160.03, -6.24) * mm});
            skLineSegment(sketch, "E2019", {"start": v(160.03, -6.24) * mm, "end": v(160.08, -6.35) * mm});
            skLineSegment(sketch, "E2020", {"start": v(160.08, -6.35) * mm, "end": v(160.12, -6.46) * mm});
            skLineSegment(sketch, "E2021", {"start": v(160.12, -6.46) * mm, "end": v(160.18, -6.56) * mm});
            skLineSegment(sketch, "E2022", {"start": v(160.18, -6.56) * mm, "end": v(160.23, -6.67) * mm});
            skLineSegment(sketch, "E2023", {"start": v(160.23, -6.67) * mm, "end": v(160.3, -6.76) * mm});
            skLineSegment(sketch, "E2024", {"start": v(160.3, -6.76) * mm, "end": v(160.36, -6.86) * mm});
            skLineSegment(sketch, "E2025", {"start": v(160.36, -6.86) * mm, "end": v(160.44, -6.95) * mm});
            skLineSegment(sketch, "E2026", {"start": v(160.44, -6.95) * mm, "end": v(160.51, -7.04) * mm});
            skLineSegment(sketch, "E2027", {"start": v(160.51, -7.04) * mm, "end": v(160.6, -7.13) * mm});
            skLineSegment(sketch, "E2028", {"start": v(160.6, -7.13) * mm, "end": v(179.2, -25.68) * mm});
            skLineSegment(sketch, "E2029", {"start": v(179.2, -25.68) * mm, "end": v(179.3, -25.78) * mm});
            skLineSegment(sketch, "E2030", {"start": v(179.3, -25.78) * mm, "end": v(179.4, -25.87) * mm});
            skLineSegment(sketch, "E2031", {"start": v(179.4, -25.87) * mm, "end": v(179.5, -25.95) * mm});
            skLineSegment(sketch, "E2032", {"start": v(179.5, -25.95) * mm, "end": v(179.62, -26.03) * mm});
            skLineSegment(sketch, "E2033", {"start": v(179.62, -26.03) * mm, "end": v(179.73, -26.1) * mm});
            skLineSegment(sketch, "E2034", {"start": v(179.73, -26.1) * mm, "end": v(179.85, -26.17) * mm});
            skLineSegment(sketch, "E2035", {"start": v(179.85, -26.17) * mm, "end": v(179.97, -26.23) * mm});
            skLineSegment(sketch, "E2036", {"start": v(179.97, -26.23) * mm, "end": v(180.1, -26.28) * mm});
            skLineSegment(sketch, "E2037", {"start": v(180.1, -26.28) * mm, "end": v(180.22, -26.33) * mm});
            skLineSegment(sketch, "E2038", {"start": v(180.22, -26.33) * mm, "end": v(180.34, -26.37) * mm});
            skLineSegment(sketch, "E2039", {"start": v(180.34, -26.37) * mm, "end": v(180.47, -26.4) * mm});
            skLineSegment(sketch, "E2040", {"start": v(180.47, -26.4) * mm, "end": v(180.6, -26.44) * mm});
            skLineSegment(sketch, "E2041", {"start": v(180.6, -26.44) * mm, "end": v(180.74, -26.46) * mm});
            skLineSegment(sketch, "E2042", {"start": v(180.74, -26.46) * mm, "end": v(180.87, -26.48) * mm});
            skLineSegment(sketch, "E2043", {"start": v(180.87, -26.48) * mm, "end": v(181.01, -26.49) * mm});
            skLineSegment(sketch, "E2044", {"start": v(181.01, -26.49) * mm, "end": v(181.15, -26.5) * mm});
            skLineSegment(sketch, "E2045", {"start": v(181.15, -26.5) * mm, "end": v(192.86, -26.54) * mm});
            skLineSegment(sketch, "E2046", {"start": v(192.86, -26.54) * mm, "end": v(193.74, -26.5) * mm});
            skLineSegment(sketch, "E2047", {"start": v(193.74, -26.5) * mm, "end": v(194.6, -26.37) * mm});
            skLineSegment(sketch, "E2048", {"start": v(194.6, -26.37) * mm, "end": v(195.43, -26.15) * mm});
            skLineSegment(sketch, "E2049", {"start": v(195.43, -26.15) * mm, "end": v(196.22, -25.86) * mm});
            skLineSegment(sketch, "E2050", {"start": v(196.22, -25.86) * mm, "end": v(196.98, -25.5) * mm});
            skLineSegment(sketch, "E2051", {"start": v(196.98, -25.5) * mm, "end": v(197.7, -25.06) * mm});
            skLineSegment(sketch, "E2052", {"start": v(197.7, -25.06) * mm, "end": v(198.36, -24.56) * mm});
            skLineSegment(sketch, "E2053", {"start": v(198.36, -24.56) * mm, "end": v(198.97, -24) * mm});
            skLineSegment(sketch, "E2054", {"start": v(198.97, -24) * mm, "end": v(199.53, -23.39) * mm});
            skLineSegment(sketch, "E2055", {"start": v(199.53, -23.39) * mm, "end": v(200.03, -22.72) * mm});
            skLineSegment(sketch, "E2056", {"start": v(200.03, -22.72) * mm, "end": v(200.46, -22) * mm});
            skLineSegment(sketch, "E2057", {"start": v(200.46, -22) * mm, "end": v(200.83, -21.25) * mm});
            skLineSegment(sketch, "E2058", {"start": v(200.83, -21.25) * mm, "end": v(201.12, -20.46) * mm});
            skLineSegment(sketch, "E2059", {"start": v(201.12, -20.46) * mm, "end": v(201.33, -19.63) * mm});
            skLineSegment(sketch, "E2060", {"start": v(201.33, -19.63) * mm, "end": v(201.47, -18.77) * mm});
            skLineSegment(sketch, "E2061", {"start": v(201.47, -18.77) * mm, "end": v(201.51, -17.89) * mm});
            skLineSegment(sketch, "E2062", {"start": v(201.51, -17.89) * mm, "end": v(201.51, 17.82) * mm});
            skLineSegment(sketch, "E2063", {"start": v(201.51, 17.82) * mm, "end": v(201.47, 18.7) * mm});
            skLineSegment(sketch, "E2064", {"start": v(201.47, 18.7) * mm, "end": v(201.33, 19.57) * mm});
            skLineSegment(sketch, "E2065", {"start": v(201.33, 19.57) * mm, "end": v(201.12, 20.4) * mm});
            skLineSegment(sketch, "E2066", {"start": v(201.12, 20.4) * mm, "end": v(200.83, 21.2) * mm});
            skLineSegment(sketch, "E2067", {"start": v(200.83, 21.2) * mm, "end": v(200.46, 21.95) * mm});
            skLineSegment(sketch, "E2068", {"start": v(200.46, 21.95) * mm, "end": v(200.03, 22.66) * mm});
            skLineSegment(sketch, "E2069", {"start": v(200.03, 22.66) * mm, "end": v(199.53, 23.33) * mm});
            skLineSegment(sketch, "E2070", {"start": v(199.53, 23.33) * mm, "end": v(198.97, 23.94) * mm});
            skLineSegment(sketch, "E2071", {"start": v(198.97, 23.94) * mm, "end": v(198.36, 24.5) * mm});
            skLineSegment(sketch, "E2072", {"start": v(198.36, 24.5) * mm, "end": v(197.7, 25) * mm});
            skLineSegment(sketch, "E2073", {"start": v(197.7, 25) * mm, "end": v(196.98, 25.43) * mm});
            skLineSegment(sketch, "E2074", {"start": v(196.98, 25.43) * mm, "end": v(196.22, 25.8) * mm});
            skLineSegment(sketch, "E2075", {"start": v(196.22, 25.8) * mm, "end": v(195.43, 26.1) * mm});
            skLineSegment(sketch, "E2076", {"start": v(195.43, 26.1) * mm, "end": v(194.6, 26.3) * mm});
            skLineSegment(sketch, "E2077", {"start": v(194.6, 26.3) * mm, "end": v(193.74, 26.44) * mm});
            skLineSegment(sketch, "E2078", {"start": v(193.74, 26.44) * mm, "end": v(192.86, 26.48) * mm});
            skLineSegment(sketch, "E2079", {"start": v(198.49, -17.89) * mm, "end": v(198.46, -18.46) * mm});
            skLineSegment(sketch, "E2080", {"start": v(198.46, -18.46) * mm, "end": v(198.37, -19.02) * mm});
            skLineSegment(sketch, "E2081", {"start": v(198.37, -19.02) * mm, "end": v(198.24, -19.56) * mm});
            skLineSegment(sketch, "E2082", {"start": v(198.24, -19.56) * mm, "end": v(198.05, -20.08) * mm});
            skLineSegment(sketch, "E2083", {"start": v(198.05, -20.08) * mm, "end": v(197.8, -20.57) * mm});
            skLineSegment(sketch, "E2084", {"start": v(197.8, -20.57) * mm, "end": v(197.53, -21.03) * mm});
            skLineSegment(sketch, "E2085", {"start": v(197.53, -21.03) * mm, "end": v(197.2, -21.47) * mm});
            skLineSegment(sketch, "E2086", {"start": v(197.2, -21.47) * mm, "end": v(196.84, -21.87) * mm});
            skLineSegment(sketch, "E2087", {"start": v(196.84, -21.87) * mm, "end": v(196.44, -22.23) * mm});
            skLineSegment(sketch, "E2088", {"start": v(196.44, -22.23) * mm, "end": v(196, -22.56) * mm});
            skLineSegment(sketch, "E2089", {"start": v(196, -22.56) * mm, "end": v(195.54, -22.84) * mm});
            skLineSegment(sketch, "E2090", {"start": v(195.54, -22.84) * mm, "end": v(195.05, -23.08) * mm});
            skLineSegment(sketch, "E2091", {"start": v(195.05, -23.08) * mm, "end": v(194.53, -23.27) * mm});
            skLineSegment(sketch, "E2092", {"start": v(194.53, -23.27) * mm, "end": v(193.99, -23.4) * mm});
            skLineSegment(sketch, "E2093", {"start": v(193.99, -23.4) * mm, "end": v(193.43, -23.5) * mm});
            skLineSegment(sketch, "E2094", {"start": v(193.43, -23.5) * mm, "end": v(192.86, -23.52) * mm});
            skLineSegment(sketch, "E2095", {"start": v(192.86, -23.52) * mm, "end": v(181.97, -23.49) * mm});
            skLineSegment(sketch, "E2096", {"start": v(181.97, -23.49) * mm, "end": v(181.88, -23.48) * mm});
            skLineSegment(sketch, "E2097", {"start": v(181.88, -23.48) * mm, "end": v(181.79, -23.48) * mm});
            skLineSegment(sketch, "E2098", {"start": v(181.79, -23.48) * mm, "end": v(181.7, -23.47) * mm});
            skLineSegment(sketch, "E2099", {"start": v(181.7, -23.47) * mm, "end": v(181.6, -23.45) * mm});
            skLineSegment(sketch, "E2100", {"start": v(181.6, -23.45) * mm, "end": v(181.52, -23.43) * mm});
            skLineSegment(sketch, "E2101", {"start": v(181.52, -23.43) * mm, "end": v(181.43, -23.4) * mm});
            skLineSegment(sketch, "E2102", {"start": v(181.43, -23.4) * mm, "end": v(181.34, -23.38) * mm});
            skLineSegment(sketch, "E2103", {"start": v(181.34, -23.38) * mm, "end": v(181.26, -23.34) * mm});
            skLineSegment(sketch, "E2104", {"start": v(181.26, -23.34) * mm, "end": v(181.18, -23.3) * mm});
            skLineSegment(sketch, "E2105", {"start": v(181.18, -23.3) * mm, "end": v(181.1, -23.27) * mm});
            skLineSegment(sketch, "E2106", {"start": v(181.1, -23.27) * mm, "end": v(181.02, -23.22) * mm});
            skLineSegment(sketch, "E2107", {"start": v(181.02, -23.22) * mm, "end": v(180.94, -23.17) * mm});
            skLineSegment(sketch, "E2108", {"start": v(180.94, -23.17) * mm, "end": v(180.86, -23.12) * mm});
            skLineSegment(sketch, "E2109", {"start": v(180.86, -23.12) * mm, "end": v(180.8, -23.06) * mm});
            skLineSegment(sketch, "E2110", {"start": v(180.8, -23.06) * mm, "end": v(180.72, -23) * mm});
            skLineSegment(sketch, "E2111", {"start": v(180.72, -23) * mm, "end": v(180.66, -22.94) * mm});
            skLineSegment(sketch, "E2112", {"start": v(180.66, -22.94) * mm, "end": v(164.7, -7) * mm});
            skLineSegment(sketch, "E2113", {"start": v(164.7, -7) * mm, "end": v(164.7, -6.98) * mm});
            skLineSegment(sketch, "E2114", {"start": v(164.7, -6.98) * mm, "end": v(164.69, -6.97) * mm});
            skLineSegment(sketch, "E2115", {"start": v(164.69, -6.97) * mm, "end": v(164.68, -6.96) * mm});
            skLineSegment(sketch, "E2116", {"start": v(164.68, -6.96) * mm, "end": v(164.68, -6.95) * mm});
            skLineSegment(sketch, "E2117", {"start": v(164.68, -6.95) * mm, "end": v(164.67, -6.94) * mm});
            skLineSegment(sketch, "E2118", {"start": v(164.67, -6.94) * mm, "end": v(164.67, -6.93) * mm});
            skLineSegment(sketch, "E2119", {"start": v(164.67, -6.93) * mm, "end": v(164.66, -6.92) * mm});
            skLineSegment(sketch, "E2120", {"start": v(164.66, -6.92) * mm, "end": v(164.66, -6.9) * mm});
            skLineSegment(sketch, "E2121", {"start": v(164.66, -6.9) * mm, "end": v(164.66, -6.9) * mm});
            skLineSegment(sketch, "E2122", {"start": v(164.66, -6.9) * mm, "end": v(164.66, -6.88) * mm});
            skLineSegment(sketch, "E2123", {"start": v(164.66, -6.88) * mm, "end": v(164.66, -6.87) * mm});
            skLineSegment(sketch, "E2124", {"start": v(164.66, -6.87) * mm, "end": v(164.66, -6.85) * mm});
            skLineSegment(sketch, "E2125", {"start": v(164.66, -6.85) * mm, "end": v(164.66, -6.84) * mm});
            skLineSegment(sketch, "E2126", {"start": v(164.66, -6.84) * mm, "end": v(164.66, -6.83) * mm});
            skLineSegment(sketch, "E2127", {"start": v(164.66, -6.83) * mm, "end": v(164.67, -6.82) * mm});
            skLineSegment(sketch, "E2128", {"start": v(164.67, -6.82) * mm, "end": v(164.67, -6.8) * mm});
            skLineSegment(sketch, "E2129", {"start": v(164.67, -6.8) * mm, "end": v(164.68, -6.8) * mm});
            skLineSegment(sketch, "E2130", {"start": v(164.68, -6.8) * mm, "end": v(164.68, -6.78) * mm});
            skLineSegment(sketch, "E2131", {"start": v(164.68, -6.78) * mm, "end": v(164.69, -6.77) * mm});
            skLineSegment(sketch, "E2132", {"start": v(164.69, -6.77) * mm, "end": v(164.7, -6.76) * mm});
            skLineSegment(sketch, "E2133", {"start": v(164.7, -6.76) * mm, "end": v(164.7, -6.75) * mm});
            skLineSegment(sketch, "E2134", {"start": v(164.7, -6.75) * mm, "end": v(164.71, -6.74) * mm});
            skLineSegment(sketch, "E2135", {"start": v(164.71, -6.74) * mm, "end": v(164.72, -6.73) * mm});
            skLineSegment(sketch, "E2136", {"start": v(164.72, -6.73) * mm, "end": v(164.73, -6.73) * mm});
            skLineSegment(sketch, "E2137", {"start": v(164.73, -6.73) * mm, "end": v(164.74, -6.72) * mm});
            skLineSegment(sketch, "E2138", {"start": v(164.74, -6.72) * mm, "end": v(164.75, -6.71) * mm});
            skLineSegment(sketch, "E2139", {"start": v(164.75, -6.71) * mm, "end": v(164.77, -6.7) * mm});
            skLineSegment(sketch, "E2140", {"start": v(164.77, -6.7) * mm, "end": v(164.78, -6.7) * mm});
            skLineSegment(sketch, "E2141", {"start": v(164.78, -6.7) * mm, "end": v(164.79, -6.7) * mm});
            skLineSegment(sketch, "E2142", {"start": v(164.79, -6.7) * mm, "end": v(164.8, -6.7) * mm});
            skLineSegment(sketch, "E2143", {"start": v(164.8, -6.7) * mm, "end": v(164.82, -6.7) * mm});
            skLineSegment(sketch, "E2144", {"start": v(164.82, -6.7) * mm, "end": v(164.83, -6.7) * mm});
            skLineSegment(sketch, "E2145", {"start": v(164.83, -6.7) * mm, "end": v(170.73, -6.7) * mm});
            skLineSegment(sketch, "E2146", {"start": v(170.73, -6.7) * mm, "end": v(171.23, -6.69) * mm});
            skLineSegment(sketch, "E2147", {"start": v(171.23, -6.69) * mm, "end": v(171.72, -6.66) * mm});
            skLineSegment(sketch, "E2148", {"start": v(171.72, -6.66) * mm, "end": v(172.2, -6.62) * mm});
            skLineSegment(sketch, "E2149", {"start": v(172.2, -6.62) * mm, "end": v(172.68, -6.55) * mm});
            skLineSegment(sketch, "E2150", {"start": v(172.68, -6.55) * mm, "end": v(173.15, -6.47) * mm});
            skLineSegment(sketch, "E2151", {"start": v(173.15, -6.47) * mm, "end": v(173.61, -6.37) * mm});
            skLineSegment(sketch, "E2152", {"start": v(173.61, -6.37) * mm, "end": v(174.07, -6.26) * mm});
            skLineSegment(sketch, "E2153", {"start": v(174.07, -6.26) * mm, "end": v(174.52, -6.12) * mm});
            skLineSegment(sketch, "E2154", {"start": v(174.52, -6.12) * mm, "end": v(174.97, -5.97) * mm});
            skLineSegment(sketch, "E2155", {"start": v(174.97, -5.97) * mm, "end": v(175.4, -5.8) * mm});
            skLineSegment(sketch, "E2156", {"start": v(175.4, -5.8) * mm, "end": v(175.83, -5.61) * mm});
            skLineSegment(sketch, "E2157", {"start": v(175.83, -5.61) * mm, "end": v(176.26, -5.4) * mm});
            skLineSegment(sketch, "E2158", {"start": v(176.26, -5.4) * mm, "end": v(176.68, -5.18) * mm});
            skLineSegment(sketch, "E2159", {"start": v(176.68, -5.18) * mm, "end": v(177.09, -4.94) * mm});
            skLineSegment(sketch, "E2160", {"start": v(177.09, -4.94) * mm, "end": v(177.49, -4.68) * mm});
            skLineSegment(sketch, "E2161", {"start": v(177.49, -4.68) * mm, "end": v(177.88, -4.4) * mm});
            skLineSegment(sketch, "E2162", {"start": v(177.88, -4.4) * mm, "end": v(178.4, -4) * mm});
            skLineSegment(sketch, "E2163", {"start": v(178.4, -4) * mm, "end": v(178.87, -3.59) * mm});
            skLineSegment(sketch, "E2164", {"start": v(178.87, -3.59) * mm, "end": v(179.31, -3.14) * mm});
            skLineSegment(sketch, "E2165", {"start": v(179.31, -3.14) * mm, "end": v(179.73, -2.68) * mm});
            skLineSegment(sketch, "E2166", {"start": v(179.73, -2.68) * mm, "end": v(180.1, -2.19) * mm});
            skLineSegment(sketch, "E2167", {"start": v(180.1, -2.19) * mm, "end": v(180.45, -1.67) * mm});
            skLineSegment(sketch, "E2168", {"start": v(180.45, -1.67) * mm, "end": v(180.76, -1.14) * mm});
            skLineSegment(sketch, "E2169", {"start": v(180.76, -1.14) * mm, "end": v(181.05, -0.58) * mm});
            skLineSegment(sketch, "E2170", {"start": v(181.05, -0.58) * mm, "end": v(181.3, 0) * mm});
            skLineSegment(sketch, "E2171", {"start": v(181.3, 0) * mm, "end": v(181.5, 0.6) * mm});
            skLineSegment(sketch, "E2172", {"start": v(181.5, 0.6) * mm, "end": v(181.7, 1.22) * mm});
            skLineSegment(sketch, "E2173", {"start": v(181.7, 1.22) * mm, "end": v(181.84, 1.87) * mm});
            skLineSegment(sketch, "E2174", {"start": v(181.84, 1.87) * mm, "end": v(181.96, 2.54) * mm});
            skLineSegment(sketch, "E2175", {"start": v(181.96, 2.54) * mm, "end": v(182.04, 3.23) * mm});
            skLineSegment(sketch, "E2176", {"start": v(182.04, 3.23) * mm, "end": v(182.09, 3.94) * mm});
            skLineSegment(sketch, "E2177", {"start": v(182.09, 3.94) * mm, "end": v(182.1, 4.67) * mm});
            skLineSegment(sketch, "E2178", {"start": v(182.1, 4.67) * mm, "end": v(182.09, 5.4) * mm});
            skLineSegment(sketch, "E2179", {"start": v(182.09, 5.4) * mm, "end": v(182.04, 6.12) * mm});
            skLineSegment(sketch, "E2180", {"start": v(182.04, 6.12) * mm, "end": v(181.96, 6.8) * mm});
            skLineSegment(sketch, "E2181", {"start": v(181.96, 6.8) * mm, "end": v(181.84, 7.48) * mm});
            skLineSegment(sketch, "E2182", {"start": v(181.84, 7.48) * mm, "end": v(181.7, 8.12) * mm});
            skLineSegment(sketch, "E2183", {"start": v(181.7, 8.12) * mm, "end": v(181.5, 8.75) * mm});
            skLineSegment(sketch, "E2184", {"start": v(181.5, 8.75) * mm, "end": v(181.3, 9.35) * mm});
            skLineSegment(sketch, "E2185", {"start": v(181.3, 9.35) * mm, "end": v(181.05, 9.93) * mm});
            skLineSegment(sketch, "E2186", {"start": v(181.05, 9.93) * mm, "end": v(180.76, 10.48) * mm});
            skLineSegment(sketch, "E2187", {"start": v(180.76, 10.48) * mm, "end": v(180.45, 11.02) * mm});
            skLineSegment(sketch, "E2188", {"start": v(180.45, 11.02) * mm, "end": v(180.1, 11.53) * mm});
            skLineSegment(sketch, "E2189", {"start": v(180.1, 11.53) * mm, "end": v(179.73, 12.02) * mm});
            skLineSegment(sketch, "E2190", {"start": v(179.73, 12.02) * mm, "end": v(179.31, 12.49) * mm});
            skLineSegment(sketch, "E2191", {"start": v(179.31, 12.49) * mm, "end": v(178.87, 12.93) * mm});
            skLineSegment(sketch, "E2192", {"start": v(178.87, 12.93) * mm, "end": v(178.4, 13.35) * mm});
            skLineSegment(sketch, "E2193", {"start": v(178.4, 13.35) * mm, "end": v(177.88, 13.75) * mm});
            skLineSegment(sketch, "E2194", {"start": v(177.88, 13.75) * mm, "end": v(177.49, 14.03) * mm});
            skLineSegment(sketch, "E2195", {"start": v(177.49, 14.03) * mm, "end": v(177.09, 14.29) * mm});
            skLineSegment(sketch, "E2196", {"start": v(177.09, 14.29) * mm, "end": v(176.68, 14.53) * mm});
            skLineSegment(sketch, "E2197", {"start": v(176.68, 14.53) * mm, "end": v(176.26, 14.75) * mm});
            skLineSegment(sketch, "E2198", {"start": v(176.26, 14.75) * mm, "end": v(175.83, 14.96) * mm});
            skLineSegment(sketch, "E2199", {"start": v(175.83, 14.96) * mm, "end": v(175.4, 15.15) * mm});
            skLineSegment(sketch, "E2200", {"start": v(175.4, 15.15) * mm, "end": v(174.97, 15.32) * mm});
            skLineSegment(sketch, "E2201", {"start": v(174.97, 15.32) * mm, "end": v(174.52, 15.47) * mm});
            skLineSegment(sketch, "E2202", {"start": v(174.52, 15.47) * mm, "end": v(174.07, 15.6) * mm});
            skLineSegment(sketch, "E2203", {"start": v(174.07, 15.6) * mm, "end": v(173.61, 15.72) * mm});
            skLineSegment(sketch, "E2204", {"start": v(173.61, 15.72) * mm, "end": v(173.15, 15.82) * mm});
            skLineSegment(sketch, "E2205", {"start": v(173.15, 15.82) * mm, "end": v(172.68, 15.9) * mm});
            skLineSegment(sketch, "E2206", {"start": v(172.68, 15.9) * mm, "end": v(172.2, 15.96) * mm});
            skLineSegment(sketch, "E2207", {"start": v(172.2, 15.96) * mm, "end": v(171.72, 16) * mm});
            skLineSegment(sketch, "E2208", {"start": v(171.72, 16) * mm, "end": v(171.23, 16.04) * mm});
            skLineSegment(sketch, "E2209", {"start": v(171.23, 16.04) * mm, "end": v(170.73, 16.04) * mm});
            skLineSegment(sketch, "E2210", {"start": v(170.73, 16.04) * mm, "end": v(157.68, 16.04) * mm});
            skLineSegment(sketch, "E2211", {"start": v(157.68, 16.04) * mm, "end": v(157.35, 16.03) * mm});
            skLineSegment(sketch, "E2212", {"start": v(157.35, 16.03) * mm, "end": v(157.02, 15.98) * mm});
            skLineSegment(sketch, "E2213", {"start": v(157.02, 15.98) * mm, "end": v(156.7, 15.9) * mm});
            skLineSegment(sketch, "E2214", {"start": v(156.7, 15.9) * mm, "end": v(156.4, 15.79) * mm});
            skLineSegment(sketch, "E2215", {"start": v(156.4, 15.79) * mm, "end": v(156.11, 15.65) * mm});
            skLineSegment(sketch, "E2216", {"start": v(156.11, 15.65) * mm, "end": v(155.84, 15.48) * mm});
            skLineSegment(sketch, "E2217", {"start": v(155.84, 15.48) * mm, "end": v(155.59, 15.3) * mm});
            skLineSegment(sketch, "E2218", {"start": v(155.59, 15.3) * mm, "end": v(155.35, 15.08) * mm});
            skLineSegment(sketch, "E2219", {"start": v(155.35, 15.08) * mm, "end": v(155.14, 14.85) * mm});
            skLineSegment(sketch, "E2220", {"start": v(155.14, 14.85) * mm, "end": v(154.95, 14.6) * mm});
            skLineSegment(sketch, "E2221", {"start": v(154.95, 14.6) * mm, "end": v(154.79, 14.32) * mm});
            skLineSegment(sketch, "E2222", {"start": v(154.79, 14.32) * mm, "end": v(154.65, 14.03) * mm});
            skLineSegment(sketch, "E2223", {"start": v(154.65, 14.03) * mm, "end": v(154.54, 13.73) * mm});
            skLineSegment(sketch, "E2224", {"start": v(154.54, 13.73) * mm, "end": v(154.46, 13.41) * mm});
            skLineSegment(sketch, "E2225", {"start": v(154.46, 13.41) * mm, "end": v(154.4, 13.09) * mm});
            skLineSegment(sketch, "E2226", {"start": v(154.4, 13.09) * mm, "end": v(154.39, 12.75) * mm});
            skLineSegment(sketch, "E2227", {"start": v(154.39, 12.75) * mm, "end": v(154.39, -22.53) * mm});
            skLineSegment(sketch, "E2228", {"start": v(154.39, -22.53) * mm, "end": v(154.39, -22.64) * mm});
            skLineSegment(sketch, "E2229", {"start": v(154.39, -22.64) * mm, "end": v(154.37, -22.74) * mm});
            skLineSegment(sketch, "E2230", {"start": v(154.37, -22.74) * mm, "end": v(154.35, -22.84) * mm});
            skLineSegment(sketch, "E2231", {"start": v(154.35, -22.84) * mm, "end": v(154.33, -22.93) * mm});
            skLineSegment(sketch, "E2232", {"start": v(154.33, -22.93) * mm, "end": v(154.3, -23.01) * mm});
            skLineSegment(sketch, "E2233", {"start": v(154.3, -23.01) * mm, "end": v(154.25, -23.09) * mm});
            skLineSegment(sketch, "E2234", {"start": v(154.25, -23.09) * mm, "end": v(154.2, -23.16) * mm});
            skLineSegment(sketch, "E2235", {"start": v(154.2, -23.16) * mm, "end": v(154.14, -23.22) * mm});
            skLineSegment(sketch, "E2236", {"start": v(154.14, -23.22) * mm, "end": v(154.07, -23.28) * mm});
            skLineSegment(sketch, "E2237", {"start": v(154.07, -23.28) * mm, "end": v(154, -23.33) * mm});
            skLineSegment(sketch, "E2238", {"start": v(154, -23.33) * mm, "end": v(153.91, -23.37) * mm});
            skLineSegment(sketch, "E2239", {"start": v(153.91, -23.37) * mm, "end": v(153.82, -23.4) * mm});
            skLineSegment(sketch, "E2240", {"start": v(153.82, -23.4) * mm, "end": v(153.72, -23.44) * mm});
            skLineSegment(sketch, "E2241", {"start": v(153.72, -23.44) * mm, "end": v(153.61, -23.46) * mm});
            skLineSegment(sketch, "E2242", {"start": v(153.61, -23.46) * mm, "end": v(153.5, -23.47) * mm});
            skLineSegment(sketch, "E2243", {"start": v(153.5, -23.47) * mm, "end": v(153.37, -23.48) * mm});
            skLineSegment(sketch, "E2244", {"start": v(153.37, -23.48) * mm, "end": v(152.53, -23.52) * mm});
            skLineSegment(sketch, "E2245", {"start": v(152.53, -23.52) * mm, "end": v(135.23, -23.49) * mm});
            skLineSegment(sketch, "E2246", {"start": v(135.23, -23.49) * mm, "end": v(135.17, -23.48) * mm});
            skLineSegment(sketch, "E2247", {"start": v(135.17, -23.48) * mm, "end": v(135.1, -23.47) * mm});
            skLineSegment(sketch, "E2248", {"start": v(135.1, -23.47) * mm, "end": v(135.05, -23.46) * mm});
            skLineSegment(sketch, "E2249", {"start": v(135.05, -23.46) * mm, "end": v(135, -23.44) * mm});
            skLineSegment(sketch, "E2250", {"start": v(135, -23.44) * mm, "end": v(134.95, -23.41) * mm});
            skLineSegment(sketch, "E2251", {"start": v(134.95, -23.41) * mm, "end": v(134.9, -23.38) * mm});
            skLineSegment(sketch, "E2252", {"start": v(134.9, -23.38) * mm, "end": v(134.85, -23.35) * mm});
            skLineSegment(sketch, "E2253", {"start": v(134.85, -23.35) * mm, "end": v(134.81, -23.31) * mm});
            skLineSegment(sketch, "E2254", {"start": v(134.81, -23.31) * mm, "end": v(134.77, -23.27) * mm});
            skLineSegment(sketch, "E2255", {"start": v(134.77, -23.27) * mm, "end": v(134.74, -23.23) * mm});
            skLineSegment(sketch, "E2256", {"start": v(134.74, -23.23) * mm, "end": v(134.71, -23.18) * mm});
            skLineSegment(sketch, "E2257", {"start": v(134.71, -23.18) * mm, "end": v(134.69, -23.13) * mm});
            skLineSegment(sketch, "E2258", {"start": v(134.69, -23.13) * mm, "end": v(134.67, -23.07) * mm});
            skLineSegment(sketch, "E2259", {"start": v(134.67, -23.07) * mm, "end": v(134.65, -23.02) * mm});
            skLineSegment(sketch, "E2260", {"start": v(134.65, -23.02) * mm, "end": v(134.64, -22.96) * mm});
            skLineSegment(sketch, "E2261", {"start": v(134.64, -22.96) * mm, "end": v(134.64, -22.9) * mm});
            skLineSegment(sketch, "E2262", {"start": v(134.64, -22.9) * mm, "end": v(134.64, -21.76) * mm});
            skLineSegment(sketch, "E2263", {"start": v(134.64, -21.76) * mm, "end": v(134.64, -21.69) * mm});
            skLineSegment(sketch, "E2264", {"start": v(134.64, -21.69) * mm, "end": v(134.65, -21.61) * mm});
            skLineSegment(sketch, "E2265", {"start": v(134.65, -21.61) * mm, "end": v(134.67, -21.54) * mm});
            skLineSegment(sketch, "E2266", {"start": v(134.67, -21.54) * mm, "end": v(134.69, -21.47) * mm});
            skLineSegment(sketch, "E2267", {"start": v(134.69, -21.47) * mm, "end": v(134.71, -21.4) * mm});
            skLineSegment(sketch, "E2268", {"start": v(134.71, -21.4) * mm, "end": v(134.74, -21.35) * mm});
            skLineSegment(sketch, "E2269", {"start": v(134.74, -21.35) * mm, "end": v(134.78, -21.28) * mm});
            skLineSegment(sketch, "E2270", {"start": v(134.78, -21.28) * mm, "end": v(134.82, -21.23) * mm});
            skLineSegment(sketch, "E2271", {"start": v(134.82, -21.23) * mm, "end": v(134.86, -21.17) * mm});
            skLineSegment(sketch, "E2272", {"start": v(134.86, -21.17) * mm, "end": v(134.91, -21.12) * mm});
            skLineSegment(sketch, "E2273", {"start": v(134.91, -21.12) * mm, "end": v(134.96, -21.08) * mm});
            skLineSegment(sketch, "E2274", {"start": v(134.96, -21.08) * mm, "end": v(135.02, -21.04) * mm});
            skLineSegment(sketch, "E2275", {"start": v(135.02, -21.04) * mm, "end": v(135.08, -21) * mm});
            skLineSegment(sketch, "E2276", {"start": v(135.08, -21) * mm, "end": v(135.14, -20.97) * mm});
            skLineSegment(sketch, "E2277", {"start": v(135.14, -20.97) * mm, "end": v(135.21, -20.94) * mm});
            skLineSegment(sketch, "E2278", {"start": v(135.21, -20.94) * mm, "end": v(135.28, -20.92) * mm});
            skLineSegment(sketch, "E2279", {"start": v(135.28, -20.92) * mm, "end": v(136.03, -20.72) * mm});
            skLineSegment(sketch, "E2280", {"start": v(136.03, -20.72) * mm, "end": v(136.76, -20.5) * mm});
            skLineSegment(sketch, "E2281", {"start": v(136.76, -20.5) * mm, "end": v(137.47, -20.24) * mm});
            skLineSegment(sketch, "E2282", {"start": v(137.47, -20.24) * mm, "end": v(138.17, -19.96) * mm});
            skLineSegment(sketch, "E2283", {"start": v(138.17, -19.96) * mm, "end": v(138.86, -19.65) * mm});
            skLineSegment(sketch, "E2284", {"start": v(138.86, -19.65) * mm, "end": v(139.53, -19.31) * mm});
            skLineSegment(sketch, "E2285", {"start": v(139.53, -19.31) * mm, "end": v(140.18, -18.95) * mm});
            skLineSegment(sketch, "E2286", {"start": v(140.18, -18.95) * mm, "end": v(140.82, -18.56) * mm});
            skLineSegment(sketch, "E2287", {"start": v(140.82, -18.56) * mm, "end": v(141.44, -18.14) * mm});
            skLineSegment(sketch, "E2288", {"start": v(141.44, -18.14) * mm, "end": v(142.05, -17.7) * mm});
            skLineSegment(sketch, "E2289", {"start": v(142.05, -17.7) * mm, "end": v(142.64, -17.23) * mm});
            skLineSegment(sketch, "E2290", {"start": v(142.64, -17.23) * mm, "end": v(143.2, -16.74) * mm});
            skLineSegment(sketch, "E2291", {"start": v(143.2, -16.74) * mm, "end": v(143.77, -16.21) * mm});
            skLineSegment(sketch, "E2292", {"start": v(143.77, -16.21) * mm, "end": v(144.3, -15.67) * mm});
            skLineSegment(sketch, "E2293", {"start": v(144.3, -15.67) * mm, "end": v(144.83, -15.1) * mm});
            skLineSegment(sketch, "E2294", {"start": v(144.83, -15.1) * mm, "end": v(145.33, -14.5) * mm});
            skLineSegment(sketch, "E2295", {"start": v(145.33, -14.5) * mm, "end": v(145.84, -13.84) * mm});
            skLineSegment(sketch, "E2296", {"start": v(145.84, -13.84) * mm, "end": v(146.32, -13.17) * mm});
            skLineSegment(sketch, "E2297", {"start": v(146.32, -13.17) * mm, "end": v(146.77, -12.5) * mm});
            skLineSegment(sketch, "E2298", {"start": v(146.77, -12.5) * mm, "end": v(147.18, -11.8) * mm});
            skLineSegment(sketch, "E2299", {"start": v(147.18, -11.8) * mm, "end": v(147.56, -11.1) * mm});
            skLineSegment(sketch, "E2300", {"start": v(147.56, -11.1) * mm, "end": v(147.9, -10.38) * mm});
            skLineSegment(sketch, "E2301", {"start": v(147.9, -10.38) * mm, "end": v(148.22, -9.66) * mm});
            skLineSegment(sketch, "E2302", {"start": v(148.22, -9.66) * mm, "end": v(148.5, -8.92) * mm});
            skLineSegment(sketch, "E2303", {"start": v(148.5, -8.92) * mm, "end": v(148.75, -8.17) * mm});
            skLineSegment(sketch, "E2304", {"start": v(148.75, -8.17) * mm, "end": v(148.96, -7.4) * mm});
            skLineSegment(sketch, "E2305", {"start": v(148.96, -7.4) * mm, "end": v(149.15, -6.64) * mm});
            skLineSegment(sketch, "E2306", {"start": v(149.15, -6.64) * mm, "end": v(149.3, -5.86) * mm});
            skLineSegment(sketch, "E2307", {"start": v(149.3, -5.86) * mm, "end": v(149.41, -5.07) * mm});
            skLineSegment(sketch, "E2308", {"start": v(149.41, -5.07) * mm, "end": v(149.5, -4.26) * mm});
            skLineSegment(sketch, "E2309", {"start": v(149.5, -4.26) * mm, "end": v(149.55, -3.45) * mm});
            skLineSegment(sketch, "E2310", {"start": v(149.55, -3.45) * mm, "end": v(149.56, -2.63) * mm});
            skLineSegment(sketch, "E2311", {"start": v(149.56, -2.63) * mm, "end": v(149.54, -1.65) * mm});
            skLineSegment(sketch, "E2312", {"start": v(149.54, -1.65) * mm, "end": v(149.48, -0.7) * mm});
            skLineSegment(sketch, "E2313", {"start": v(149.48, -0.7) * mm, "end": v(149.37, 0.25) * mm});
            skLineSegment(sketch, "E2314", {"start": v(149.37, 0.25) * mm, "end": v(149.22, 1.17) * mm});
            skLineSegment(sketch, "E2315", {"start": v(149.22, 1.17) * mm, "end": v(149.02, 2.08) * mm});
            skLineSegment(sketch, "E2316", {"start": v(149.02, 2.08) * mm, "end": v(148.78, 2.97) * mm});
            skLineSegment(sketch, "E2317", {"start": v(148.78, 2.97) * mm, "end": v(148.5, 3.84) * mm});
            skLineSegment(sketch, "E2318", {"start": v(148.5, 3.84) * mm, "end": v(148.18, 4.69) * mm});
            skLineSegment(sketch, "E2319", {"start": v(148.18, 4.69) * mm, "end": v(147.81, 5.52) * mm});
            skLineSegment(sketch, "E2320", {"start": v(147.81, 5.52) * mm, "end": v(147.4, 6.33) * mm});
            skLineSegment(sketch, "E2321", {"start": v(147.4, 6.33) * mm, "end": v(146.95, 7.13) * mm});
            skLineSegment(sketch, "E2322", {"start": v(146.95, 7.13) * mm, "end": v(146.46, 7.9) * mm});
            skLineSegment(sketch, "E2323", {"start": v(146.46, 7.9) * mm, "end": v(145.92, 8.66) * mm});
            skLineSegment(sketch, "E2324", {"start": v(145.92, 8.66) * mm, "end": v(145.34, 9.4) * mm});
            skLineSegment(sketch, "E2325", {"start": v(145.34, 9.4) * mm, "end": v(144.72, 10.1) * mm});
            skLineSegment(sketch, "E2326", {"start": v(144.72, 10.1) * mm, "end": v(144.06, 10.8) * mm});
            skLineSegment(sketch, "E2327", {"start": v(144.06, 10.8) * mm, "end": v(143.36, 11.47) * mm});
            skLineSegment(sketch, "E2328", {"start": v(143.36, 11.47) * mm, "end": v(142.65, 12.09) * mm});
            skLineSegment(sketch, "E2329", {"start": v(142.65, 12.09) * mm, "end": v(141.91, 12.67) * mm});
            skLineSegment(sketch, "E2330", {"start": v(141.91, 12.67) * mm, "end": v(141.16, 13.2) * mm});
            skLineSegment(sketch, "E2331", {"start": v(141.16, 13.2) * mm, "end": v(140.38, 13.7) * mm});
            skLineSegment(sketch, "E2332", {"start": v(140.38, 13.7) * mm, "end": v(139.59, 14.15) * mm});
            skLineSegment(sketch, "E2333", {"start": v(139.59, 14.15) * mm, "end": v(138.77, 14.56) * mm});
            skLineSegment(sketch, "E2334", {"start": v(138.77, 14.56) * mm, "end": v(137.94, 14.93) * mm});
            skLineSegment(sketch, "E2335", {"start": v(137.94, 14.93) * mm, "end": v(137.1, 15.25) * mm});
            skLineSegment(sketch, "E2336", {"start": v(137.1, 15.25) * mm, "end": v(136.22, 15.53) * mm});
            skLineSegment(sketch, "E2337", {"start": v(136.22, 15.53) * mm, "end": v(135.33, 15.77) * mm});
            skLineSegment(sketch, "E2338", {"start": v(135.33, 15.77) * mm, "end": v(134.43, 15.96) * mm});
            skLineSegment(sketch, "E2339", {"start": v(134.43, 15.96) * mm, "end": v(133.5, 16.11) * mm});
            skLineSegment(sketch, "E2340", {"start": v(133.5, 16.11) * mm, "end": v(132.56, 16.22) * mm});
            skLineSegment(sketch, "E2341", {"start": v(132.56, 16.22) * mm, "end": v(131.6, 16.29) * mm});
            skLineSegment(sketch, "E2342", {"start": v(131.6, 16.29) * mm, "end": v(130.62, 16.3) * mm});
            skLineSegment(sketch, "E2343", {"start": v(130.62, 16.3) * mm, "end": v(129.65, 16.29) * mm});
            skLineSegment(sketch, "E2344", {"start": v(129.65, 16.29) * mm, "end": v(128.7, 16.22) * mm});
            skLineSegment(sketch, "E2345", {"start": v(128.7, 16.22) * mm, "end": v(127.76, 16.11) * mm});
            skLineSegment(sketch, "E2346", {"start": v(127.76, 16.11) * mm, "end": v(126.84, 15.96) * mm});
            skLineSegment(sketch, "E2347", {"start": v(126.84, 15.96) * mm, "end": v(125.94, 15.77) * mm});
            skLineSegment(sketch, "E2348", {"start": v(125.94, 15.77) * mm, "end": v(125.06, 15.53) * mm});
            skLineSegment(sketch, "E2349", {"start": v(125.06, 15.53) * mm, "end": v(124.2, 15.25) * mm});
            skLineSegment(sketch, "E2350", {"start": v(124.2, 15.25) * mm, "end": v(123.34, 14.93) * mm});
            skLineSegment(sketch, "E2351", {"start": v(123.34, 14.93) * mm, "end": v(122.52, 14.56) * mm});
            skLineSegment(sketch, "E2352", {"start": v(122.52, 14.56) * mm, "end": v(121.7, 14.15) * mm});
            skLineSegment(sketch, "E2353", {"start": v(121.7, 14.15) * mm, "end": v(120.91, 13.7) * mm});
            skLineSegment(sketch, "E2354", {"start": v(120.91, 13.7) * mm, "end": v(120.14, 13.2) * mm});
            skLineSegment(sketch, "E2355", {"start": v(120.14, 13.2) * mm, "end": v(119.39, 12.67) * mm});
            skLineSegment(sketch, "E2356", {"start": v(119.39, 12.67) * mm, "end": v(118.65, 12.09) * mm});
            skLineSegment(sketch, "E2357", {"start": v(118.65, 12.09) * mm, "end": v(117.94, 11.47) * mm});
            skLineSegment(sketch, "E2358", {"start": v(117.94, 11.47) * mm, "end": v(117.24, 10.8) * mm});
            skLineSegment(sketch, "E2359", {"start": v(117.24, 10.8) * mm, "end": v(116.58, 10.1) * mm});
            skLineSegment(sketch, "E2360", {"start": v(116.58, 10.1) * mm, "end": v(115.96, 9.4) * mm});
            skLineSegment(sketch, "E2361", {"start": v(115.96, 9.4) * mm, "end": v(115.38, 8.66) * mm});
            skLineSegment(sketch, "E2362", {"start": v(115.38, 8.66) * mm, "end": v(114.84, 7.9) * mm});
            skLineSegment(sketch, "E2363", {"start": v(114.84, 7.9) * mm, "end": v(114.35, 7.13) * mm});
            skLineSegment(sketch, "E2364", {"start": v(114.35, 7.13) * mm, "end": v(113.9, 6.33) * mm});
            skLineSegment(sketch, "E2365", {"start": v(113.9, 6.33) * mm, "end": v(113.49, 5.52) * mm});
            skLineSegment(sketch, "E2366", {"start": v(113.49, 5.52) * mm, "end": v(113.12, 4.69) * mm});
            skLineSegment(sketch, "E2367", {"start": v(113.12, 4.69) * mm, "end": v(112.8, 3.84) * mm});
            skLineSegment(sketch, "E2368", {"start": v(112.8, 3.84) * mm, "end": v(112.52, 2.97) * mm});
            skLineSegment(sketch, "E2369", {"start": v(112.52, 2.97) * mm, "end": v(112.28, 2.08) * mm});
            skLineSegment(sketch, "E2370", {"start": v(112.28, 2.08) * mm, "end": v(112.08, 1.17) * mm});
            skLineSegment(sketch, "E2371", {"start": v(112.08, 1.17) * mm, "end": v(111.93, 0.25) * mm});
            skLineSegment(sketch, "E2372", {"start": v(111.93, 0.25) * mm, "end": v(111.83, -0.7) * mm});
            skLineSegment(sketch, "E2373", {"start": v(111.83, -0.7) * mm, "end": v(111.76, -1.65) * mm});
            skLineSegment(sketch, "E2374", {"start": v(111.76, -1.65) * mm, "end": v(111.74, -2.63) * mm});
            skLineSegment(sketch, "E2375", {"start": v(111.74, -2.63) * mm, "end": v(111.75, -3.45) * mm});
            skLineSegment(sketch, "E2376", {"start": v(111.75, -3.45) * mm, "end": v(111.8, -4.26) * mm});
            skLineSegment(sketch, "E2377", {"start": v(111.8, -4.26) * mm, "end": v(111.89, -5.07) * mm});
            skLineSegment(sketch, "E2378", {"start": v(111.89, -5.07) * mm, "end": v(112, -5.86) * mm});
            skLineSegment(sketch, "E2379", {"start": v(112, -5.86) * mm, "end": v(112.15, -6.64) * mm});
            skLineSegment(sketch, "E2380", {"start": v(112.15, -6.64) * mm, "end": v(112.34, -7.4) * mm});
            skLineSegment(sketch, "E2381", {"start": v(112.34, -7.4) * mm, "end": v(112.55, -8.17) * mm});
            skLineSegment(sketch, "E2382", {"start": v(112.55, -8.17) * mm, "end": v(112.8, -8.92) * mm});
            skLineSegment(sketch, "E2383", {"start": v(112.8, -8.92) * mm, "end": v(113.08, -9.66) * mm});
            skLineSegment(sketch, "E2384", {"start": v(113.08, -9.66) * mm, "end": v(113.4, -10.38) * mm});
            skLineSegment(sketch, "E2385", {"start": v(113.4, -10.38) * mm, "end": v(113.74, -11.1) * mm});
            skLineSegment(sketch, "E2386", {"start": v(113.74, -11.1) * mm, "end": v(114.12, -11.8) * mm});
            skLineSegment(sketch, "E2387", {"start": v(114.12, -11.8) * mm, "end": v(114.54, -12.5) * mm});
            skLineSegment(sketch, "E2388", {"start": v(114.54, -12.5) * mm, "end": v(114.98, -13.17) * mm});
            skLineSegment(sketch, "E2389", {"start": v(114.98, -13.17) * mm, "end": v(115.46, -13.84) * mm});
            skLineSegment(sketch, "E2390", {"start": v(115.46, -13.84) * mm, "end": v(115.97, -14.5) * mm});
            skLineSegment(sketch, "E2391", {"start": v(115.97, -14.5) * mm, "end": v(116.47, -15.1) * mm});
            skLineSegment(sketch, "E2392", {"start": v(116.47, -15.1) * mm, "end": v(117, -15.67) * mm});
            skLineSegment(sketch, "E2393", {"start": v(117, -15.67) * mm, "end": v(117.53, -16.21) * mm});
            skLineSegment(sketch, "E2394", {"start": v(117.53, -16.21) * mm, "end": v(118.1, -16.74) * mm});
            skLineSegment(sketch, "E2395", {"start": v(118.1, -16.74) * mm, "end": v(118.66, -17.23) * mm});
            skLineSegment(sketch, "E2396", {"start": v(118.66, -17.23) * mm, "end": v(119.25, -17.7) * mm});
            skLineSegment(sketch, "E2397", {"start": v(119.25, -17.7) * mm, "end": v(119.86, -18.14) * mm});
            skLineSegment(sketch, "E2398", {"start": v(119.86, -18.14) * mm, "end": v(120.48, -18.56) * mm});
            skLineSegment(sketch, "E2399", {"start": v(120.48, -18.56) * mm, "end": v(121.12, -18.95) * mm});
            skLineSegment(sketch, "E2400", {"start": v(121.12, -18.95) * mm, "end": v(121.77, -19.31) * mm});
            skLineSegment(sketch, "E2401", {"start": v(121.77, -19.31) * mm, "end": v(122.44, -19.65) * mm});
            skLineSegment(sketch, "E2402", {"start": v(122.44, -19.65) * mm, "end": v(123.13, -19.96) * mm});
            skLineSegment(sketch, "E2403", {"start": v(123.13, -19.96) * mm, "end": v(123.83, -20.24) * mm});
            skLineSegment(sketch, "E2404", {"start": v(123.83, -20.24) * mm, "end": v(124.54, -20.5) * mm});
            skLineSegment(sketch, "E2405", {"start": v(124.54, -20.5) * mm, "end": v(125.27, -20.72) * mm});
            skLineSegment(sketch, "E2406", {"start": v(125.27, -20.72) * mm, "end": v(126.02, -20.92) * mm});
            skLineSegment(sketch, "E2407", {"start": v(126.02, -20.92) * mm, "end": v(126.09, -20.94) * mm});
            skLineSegment(sketch, "E2408", {"start": v(126.09, -20.94) * mm, "end": v(126.16, -20.97) * mm});
            skLineSegment(sketch, "E2409", {"start": v(126.16, -20.97) * mm, "end": v(126.22, -21) * mm});
            skLineSegment(sketch, "E2410", {"start": v(126.22, -21) * mm, "end": v(126.28, -21.04) * mm});
            skLineSegment(sketch, "E2411", {"start": v(126.28, -21.04) * mm, "end": v(126.34, -21.08) * mm});
            skLineSegment(sketch, "E2412", {"start": v(126.34, -21.08) * mm, "end": v(126.39, -21.12) * mm});
            skLineSegment(sketch, "E2413", {"start": v(126.39, -21.12) * mm, "end": v(126.44, -21.17) * mm});
            skLineSegment(sketch, "E2414", {"start": v(126.44, -21.17) * mm, "end": v(126.48, -21.23) * mm});
            skLineSegment(sketch, "E2415", {"start": v(126.48, -21.23) * mm, "end": v(126.52, -21.28) * mm});
            skLineSegment(sketch, "E2416", {"start": v(126.52, -21.28) * mm, "end": v(126.56, -21.34) * mm});
            skLineSegment(sketch, "E2417", {"start": v(126.56, -21.34) * mm, "end": v(126.59, -21.4) * mm});
            skLineSegment(sketch, "E2418", {"start": v(126.59, -21.4) * mm, "end": v(126.61, -21.47) * mm});
            skLineSegment(sketch, "E2419", {"start": v(126.61, -21.47) * mm, "end": v(126.63, -21.54) * mm});
            skLineSegment(sketch, "E2420", {"start": v(126.63, -21.54) * mm, "end": v(126.65, -21.61) * mm});
            skLineSegment(sketch, "E2421", {"start": v(126.65, -21.61) * mm, "end": v(126.66, -21.69) * mm});
            skLineSegment(sketch, "E2422", {"start": v(126.66, -21.69) * mm, "end": v(126.66, -21.76) * mm});
            skLineSegment(sketch, "E2423", {"start": v(126.66, -21.76) * mm, "end": v(126.66, -22.9) * mm});
            skLineSegment(sketch, "E2424", {"start": v(126.66, -22.9) * mm, "end": v(126.66, -22.96) * mm});
            skLineSegment(sketch, "E2425", {"start": v(126.66, -22.96) * mm, "end": v(126.65, -23.02) * mm});
            skLineSegment(sketch, "E2426", {"start": v(126.65, -23.02) * mm, "end": v(126.63, -23.07) * mm});
            skLineSegment(sketch, "E2427", {"start": v(126.63, -23.07) * mm, "end": v(126.61, -23.13) * mm});
            skLineSegment(sketch, "E2428", {"start": v(126.61, -23.13) * mm, "end": v(126.59, -23.18) * mm});
            skLineSegment(sketch, "E2429", {"start": v(126.59, -23.18) * mm, "end": v(126.56, -23.23) * mm});
            skLineSegment(sketch, "E2430", {"start": v(126.56, -23.23) * mm, "end": v(126.53, -23.27) * mm});
            skLineSegment(sketch, "E2431", {"start": v(126.53, -23.27) * mm, "end": v(126.49, -23.31) * mm});
            skLineSegment(sketch, "E2432", {"start": v(126.49, -23.31) * mm, "end": v(126.45, -23.35) * mm});
            skLineSegment(sketch, "E2433", {"start": v(126.45, -23.35) * mm, "end": v(126.4, -23.38) * mm});
            skLineSegment(sketch, "E2434", {"start": v(126.4, -23.38) * mm, "end": v(126.35, -23.41) * mm});
            skLineSegment(sketch, "E2435", {"start": v(126.35, -23.41) * mm, "end": v(126.3, -23.44) * mm});
            skLineSegment(sketch, "E2436", {"start": v(126.3, -23.44) * mm, "end": v(126.25, -23.46) * mm});
            skLineSegment(sketch, "E2437", {"start": v(126.25, -23.46) * mm, "end": v(126.2, -23.47) * mm});
            skLineSegment(sketch, "E2438", {"start": v(126.2, -23.47) * mm, "end": v(126.13, -23.48) * mm});
            skLineSegment(sketch, "E2439", {"start": v(126.13, -23.48) * mm, "end": v(126.07, -23.48) * mm});
            skLineSegment(sketch, "E2440", {"start": v(126.07, -23.48) * mm, "end": v(95.18, -23.48) * mm});
            skLineSegment(sketch, "E2441", {"start": v(95.18, -23.48) * mm, "end": v(94.87, -23.47) * mm});
            skLineSegment(sketch, "E2442", {"start": v(94.87, -23.47) * mm, "end": v(94.56, -23.42) * mm});
            skLineSegment(sketch, "E2443", {"start": v(94.56, -23.42) * mm, "end": v(94.27, -23.35) * mm});
            skLineSegment(sketch, "E2444", {"start": v(94.27, -23.35) * mm, "end": v(93.98, -23.24) * mm});
            skLineSegment(sketch, "E2445", {"start": v(93.98, -23.24) * mm, "end": v(93.71, -23.11) * mm});
            skLineSegment(sketch, "E2446", {"start": v(93.71, -23.11) * mm, "end": v(93.46, -22.96) * mm});
            skLineSegment(sketch, "E2447", {"start": v(93.46, -22.96) * mm, "end": v(93.22, -22.78) * mm});
            skLineSegment(sketch, "E2448", {"start": v(93.22, -22.78) * mm, "end": v(93, -22.58) * mm});
            skLineSegment(sketch, "E2449", {"start": v(93, -22.58) * mm, "end": v(92.8, -22.36) * mm});
            skLineSegment(sketch, "E2450", {"start": v(92.8, -22.36) * mm, "end": v(92.62, -22.12) * mm});
            skLineSegment(sketch, "E2451", {"start": v(92.62, -22.12) * mm, "end": v(92.47, -21.87) * mm});
            skLineSegment(sketch, "E2452", {"start": v(92.47, -21.87) * mm, "end": v(92.34, -21.6) * mm});
            skLineSegment(sketch, "E2453", {"start": v(92.34, -21.6) * mm, "end": v(92.23, -21.31) * mm});
            skLineSegment(sketch, "E2454", {"start": v(92.23, -21.31) * mm, "end": v(92.16, -21.02) * mm});
            skLineSegment(sketch, "E2455", {"start": v(92.16, -21.02) * mm, "end": v(92.11, -20.7) * mm});
            skLineSegment(sketch, "E2456", {"start": v(92.11, -20.7) * mm, "end": v(92.1, -20.4) * mm});
            skLineSegment(sketch, "E2457", {"start": v(92.1, -20.4) * mm, "end": v(92.1, 7.6) * mm});
            skLineSegment(sketch, "E2458", {"start": v(92.1, 7.6) * mm, "end": v(92.1, 7.65) * mm});
            skLineSegment(sketch, "E2459", {"start": v(92.1, 7.65) * mm, "end": v(92.1, 7.7) * mm});
            skLineSegment(sketch, "E2460", {"start": v(92.1, 7.7) * mm, "end": v(92.12, 7.75) * mm});
            skLineSegment(sketch, "E2461", {"start": v(92.12, 7.75) * mm, "end": v(92.14, 7.8) * mm});
            skLineSegment(sketch, "E2462", {"start": v(92.14, 7.8) * mm, "end": v(92.16, 7.85) * mm});
            skLineSegment(sketch, "E2463", {"start": v(92.16, 7.85) * mm, "end": v(92.18, 7.89) * mm});
            skLineSegment(sketch, "E2464", {"start": v(92.18, 7.89) * mm, "end": v(92.21, 7.93) * mm});
            skLineSegment(sketch, "E2465", {"start": v(92.21, 7.93) * mm, "end": v(92.25, 7.97) * mm});
            skLineSegment(sketch, "E2466", {"start": v(92.25, 7.97) * mm, "end": v(92.28, 8) * mm});
            skLineSegment(sketch, "E2467", {"start": v(92.28, 8) * mm, "end": v(92.33, 8.03) * mm});
            skLineSegment(sketch, "E2468", {"start": v(92.33, 8.03) * mm, "end": v(92.37, 8.06) * mm});
            skLineSegment(sketch, "E2469", {"start": v(92.37, 8.06) * mm, "end": v(92.41, 8.08) * mm});
            skLineSegment(sketch, "E2470", {"start": v(92.41, 8.08) * mm, "end": v(92.46, 8.1) * mm});
            skLineSegment(sketch, "E2471", {"start": v(92.46, 8.1) * mm, "end": v(92.51, 8.1) * mm});
            skLineSegment(sketch, "E2472", {"start": v(92.51, 8.1) * mm, "end": v(92.56, 8.12) * mm});
            skLineSegment(sketch, "E2473", {"start": v(92.56, 8.12) * mm, "end": v(92.62, 8.12) * mm});
            skLineSegment(sketch, "E2474", {"start": v(92.62, 8.12) * mm, "end": v(102.95, 8.12) * mm});
            skLineSegment(sketch, "E2475", {"start": v(102.95, 8.12) * mm, "end": v(103.17, 8.12) * mm});
            skLineSegment(sketch, "E2476", {"start": v(103.17, 8.12) * mm, "end": v(103.38, 8.14) * mm});
            skLineSegment(sketch, "E2477", {"start": v(103.38, 8.14) * mm, "end": v(103.6, 8.16) * mm});
            skLineSegment(sketch, "E2478", {"start": v(103.6, 8.16) * mm, "end": v(103.8, 8.19) * mm});
            skLineSegment(sketch, "E2479", {"start": v(103.8, 8.19) * mm, "end": v(104, 8.23) * mm});
            skLineSegment(sketch, "E2480", {"start": v(104, 8.23) * mm, "end": v(104.19, 8.27) * mm});
            skLineSegment(sketch, "E2481", {"start": v(104.19, 8.27) * mm, "end": v(104.38, 8.33) * mm});
            skLineSegment(sketch, "E2482", {"start": v(104.38, 8.33) * mm, "end": v(104.56, 8.4) * mm});
            skLineSegment(sketch, "E2483", {"start": v(104.56, 8.4) * mm, "end": v(104.74, 8.46) * mm});
            skLineSegment(sketch, "E2484", {"start": v(104.74, 8.46) * mm, "end": v(104.9, 8.55) * mm});
            skLineSegment(sketch, "E2485", {"start": v(104.9, 8.55) * mm, "end": v(105.08, 8.63) * mm});
            skLineSegment(sketch, "E2486", {"start": v(105.08, 8.63) * mm, "end": v(105.24, 8.73) * mm});
            skLineSegment(sketch, "E2487", {"start": v(105.24, 8.73) * mm, "end": v(105.4, 8.84) * mm});
            skLineSegment(sketch, "E2488", {"start": v(105.4, 8.84) * mm, "end": v(105.54, 8.95) * mm});
            skLineSegment(sketch, "E2489", {"start": v(105.54, 8.95) * mm, "end": v(105.69, 9.08) * mm});
            skLineSegment(sketch, "E2490", {"start": v(105.69, 9.08) * mm, "end": v(105.82, 9.2) * mm});
            skLineSegment(sketch, "E2491", {"start": v(105.82, 9.2) * mm, "end": v(105.95, 9.34) * mm});
            skLineSegment(sketch, "E2492", {"start": v(105.95, 9.34) * mm, "end": v(106.08, 9.49) * mm});
            skLineSegment(sketch, "E2493", {"start": v(106.08, 9.49) * mm, "end": v(106.2, 9.64) * mm});
            skLineSegment(sketch, "E2494", {"start": v(106.2, 9.64) * mm, "end": v(106.3, 9.8) * mm});
            skLineSegment(sketch, "E2495", {"start": v(106.3, 9.8) * mm, "end": v(106.4, 9.95) * mm});
            skLineSegment(sketch, "E2496", {"start": v(106.4, 9.95) * mm, "end": v(106.49, 10.12) * mm});
            skLineSegment(sketch, "E2497", {"start": v(106.49, 10.12) * mm, "end": v(106.57, 10.3) * mm});
            skLineSegment(sketch, "E2498", {"start": v(106.57, 10.3) * mm, "end": v(106.64, 10.47) * mm});
            skLineSegment(sketch, "E2499", {"start": v(106.64, 10.47) * mm, "end": v(106.7, 10.65) * mm});
            skLineSegment(sketch, "E2500", {"start": v(106.7, 10.65) * mm, "end": v(106.76, 10.84) * mm});
            skLineSegment(sketch, "E2501", {"start": v(106.76, 10.84) * mm, "end": v(106.8, 11.03) * mm});
            skLineSegment(sketch, "E2502", {"start": v(106.8, 11.03) * mm, "end": v(106.84, 11.23) * mm});
            skLineSegment(sketch, "E2503", {"start": v(106.84, 11.23) * mm, "end": v(106.87, 11.44) * mm});
            skLineSegment(sketch, "E2504", {"start": v(106.87, 11.44) * mm, "end": v(106.9, 11.65) * mm});
            skLineSegment(sketch, "E2505", {"start": v(106.9, 11.65) * mm, "end": v(106.9, 11.86) * mm});
            skLineSegment(sketch, "E2506", {"start": v(106.9, 11.86) * mm, "end": v(106.91, 12.08) * mm});
            skLineSegment(sketch, "E2507", {"start": v(106.91, 12.08) * mm, "end": v(106.9, 12.3) * mm});
            skLineSegment(sketch, "E2508", {"start": v(106.9, 12.3) * mm, "end": v(106.9, 12.52) * mm});
            skLineSegment(sketch, "E2509", {"start": v(106.9, 12.52) * mm, "end": v(106.87, 12.73) * mm});
            skLineSegment(sketch, "E2510", {"start": v(106.87, 12.73) * mm, "end": v(106.84, 12.93) * mm});
            skLineSegment(sketch, "E2511", {"start": v(106.84, 12.93) * mm, "end": v(106.8, 13.13) * mm});
            skLineSegment(sketch, "E2512", {"start": v(106.8, 13.13) * mm, "end": v(106.76, 13.32) * mm});
            skLineSegment(sketch, "E2513", {"start": v(106.76, 13.32) * mm, "end": v(106.7, 13.5) * mm});
            skLineSegment(sketch, "E2514", {"start": v(106.7, 13.5) * mm, "end": v(106.64, 13.7) * mm});
            skLineSegment(sketch, "E2515", {"start": v(106.64, 13.7) * mm, "end": v(106.57, 13.87) * mm});
            skLineSegment(sketch, "E2516", {"start": v(106.57, 13.87) * mm, "end": v(106.49, 14.04) * mm});
            skLineSegment(sketch, "E2517", {"start": v(106.49, 14.04) * mm, "end": v(106.4, 14.2) * mm});
            skLineSegment(sketch, "E2518", {"start": v(106.4, 14.2) * mm, "end": v(106.3, 14.37) * mm});
            skLineSegment(sketch, "E2519", {"start": v(106.3, 14.37) * mm, "end": v(106.2, 14.52) * mm});
            skLineSegment(sketch, "E2520", {"start": v(106.2, 14.52) * mm, "end": v(106.08, 14.67) * mm});
            skLineSegment(sketch, "E2521", {"start": v(106.08, 14.67) * mm, "end": v(105.95, 14.82) * mm});
            skLineSegment(sketch, "E2522", {"start": v(105.95, 14.82) * mm, "end": v(105.82, 14.96) * mm});
            skLineSegment(sketch, "E2523", {"start": v(105.82, 14.96) * mm, "end": v(105.69, 15.09) * mm});
            skLineSegment(sketch, "E2524", {"start": v(105.69, 15.09) * mm, "end": v(105.54, 15.21) * mm});
            skLineSegment(sketch, "E2525", {"start": v(105.54, 15.21) * mm, "end": v(105.4, 15.33) * mm});
            skLineSegment(sketch, "E2526", {"start": v(105.4, 15.33) * mm, "end": v(105.24, 15.43) * mm});
            skLineSegment(sketch, "E2527", {"start": v(105.24, 15.43) * mm, "end": v(105.08, 15.53) * mm});
            skLineSegment(sketch, "E2528", {"start": v(105.08, 15.53) * mm, "end": v(104.9, 15.62) * mm});
            skLineSegment(sketch, "E2529", {"start": v(104.9, 15.62) * mm, "end": v(104.74, 15.7) * mm});
            skLineSegment(sketch, "E2530", {"start": v(104.74, 15.7) * mm, "end": v(104.56, 15.77) * mm});
            skLineSegment(sketch, "E2531", {"start": v(104.56, 15.77) * mm, "end": v(104.38, 15.84) * mm});
            skLineSegment(sketch, "E2532", {"start": v(104.38, 15.84) * mm, "end": v(104.19, 15.9) * mm});
            skLineSegment(sketch, "E2533", {"start": v(104.19, 15.9) * mm, "end": v(104, 15.94) * mm});
            skLineSegment(sketch, "E2534", {"start": v(104, 15.94) * mm, "end": v(103.8, 15.98) * mm});
            skLineSegment(sketch, "E2535", {"start": v(103.8, 15.98) * mm, "end": v(103.6, 16) * mm});
            skLineSegment(sketch, "E2536", {"start": v(103.6, 16) * mm, "end": v(103.38, 16.03) * mm});
            skLineSegment(sketch, "E2537", {"start": v(103.38, 16.03) * mm, "end": v(103.17, 16.04) * mm});
            skLineSegment(sketch, "E2538", {"start": v(103.17, 16.04) * mm, "end": v(102.95, 16.04) * mm});
            skLineSegment(sketch, "E2539", {"start": v(102.95, 16.04) * mm, "end": v(73.32, 16.04) * mm});
            skLineSegment(sketch, "E2540", {"start": v(73.32, 16.04) * mm, "end": v(73.1, 16.04) * mm});
            skLineSegment(sketch, "E2541", {"start": v(73.1, 16.04) * mm, "end": v(72.88, 16.03) * mm});
            skLineSegment(sketch, "E2542", {"start": v(72.88, 16.03) * mm, "end": v(72.67, 16) * mm});
            skLineSegment(sketch, "E2543", {"start": v(72.67, 16) * mm, "end": v(72.47, 15.98) * mm});
            skLineSegment(sketch, "E2544", {"start": v(72.47, 15.98) * mm, "end": v(72.27, 15.94) * mm});
            skLineSegment(sketch, "E2545", {"start": v(72.27, 15.94) * mm, "end": v(72.07, 15.9) * mm});
            skLineSegment(sketch, "E2546", {"start": v(72.07, 15.9) * mm, "end": v(71.89, 15.84) * mm});
            skLineSegment(sketch, "E2547", {"start": v(71.89, 15.84) * mm, "end": v(71.7, 15.77) * mm});
            skLineSegment(sketch, "E2548", {"start": v(71.7, 15.77) * mm, "end": v(71.53, 15.7) * mm});
            skLineSegment(sketch, "E2549", {"start": v(71.53, 15.7) * mm, "end": v(71.35, 15.62) * mm});
            skLineSegment(sketch, "E2550", {"start": v(71.35, 15.62) * mm, "end": v(71.19, 15.53) * mm});
            skLineSegment(sketch, "E2551", {"start": v(71.19, 15.53) * mm, "end": v(71.03, 15.43) * mm});
            skLineSegment(sketch, "E2552", {"start": v(71.03, 15.43) * mm, "end": v(70.87, 15.33) * mm});
            skLineSegment(sketch, "E2553", {"start": v(70.87, 15.33) * mm, "end": v(70.72, 15.21) * mm});
            skLineSegment(sketch, "E2554", {"start": v(70.72, 15.21) * mm, "end": v(70.58, 15.09) * mm});
            skLineSegment(sketch, "E2555", {"start": v(70.58, 15.09) * mm, "end": v(70.44, 14.96) * mm});
            skLineSegment(sketch, "E2556", {"start": v(70.44, 14.96) * mm, "end": v(70.3, 14.82) * mm});
            skLineSegment(sketch, "E2557", {"start": v(70.3, 14.82) * mm, "end": v(70.19, 14.67) * mm});
            skLineSegment(sketch, "E2558", {"start": v(70.19, 14.67) * mm, "end": v(70.07, 14.53) * mm});
            skLineSegment(sketch, "E2559", {"start": v(70.07, 14.53) * mm, "end": v(69.97, 14.37) * mm});
            skLineSegment(sketch, "E2560", {"start": v(69.97, 14.37) * mm, "end": v(69.87, 14.2) * mm});
            skLineSegment(sketch, "E2561", {"start": v(69.87, 14.2) * mm, "end": v(69.78, 14.04) * mm});
            skLineSegment(sketch, "E2562", {"start": v(69.78, 14.04) * mm, "end": v(69.7, 13.87) * mm});
            skLineSegment(sketch, "E2563", {"start": v(69.7, 13.87) * mm, "end": v(69.63, 13.7) * mm});
            skLineSegment(sketch, "E2564", {"start": v(69.63, 13.7) * mm, "end": v(69.56, 13.51) * mm});
            skLineSegment(sketch, "E2565", {"start": v(69.56, 13.51) * mm, "end": v(69.5, 13.32) * mm});
            skLineSegment(sketch, "E2566", {"start": v(69.5, 13.32) * mm, "end": v(69.46, 13.13) * mm});
            skLineSegment(sketch, "E2567", {"start": v(69.46, 13.13) * mm, "end": v(69.42, 12.93) * mm});
            skLineSegment(sketch, "E2568", {"start": v(69.42, 12.93) * mm, "end": v(69.4, 12.73) * mm});
            skLineSegment(sketch, "E2569", {"start": v(69.4, 12.73) * mm, "end": v(69.37, 12.52) * mm});
            skLineSegment(sketch, "E2570", {"start": v(69.37, 12.52) * mm, "end": v(69.36, 12.3) * mm});
            skLineSegment(sketch, "E2571", {"start": v(69.36, 12.3) * mm, "end": v(69.35, 12.08) * mm});
            skLineSegment(sketch, "E2572", {"start": v(69.35, 12.08) * mm, "end": v(69.36, 11.87) * mm});
            skLineSegment(sketch, "E2573", {"start": v(69.36, 11.87) * mm, "end": v(69.37, 11.66) * mm});
            skLineSegment(sketch, "E2574", {"start": v(69.37, 11.66) * mm, "end": v(69.4, 11.45) * mm});
            skLineSegment(sketch, "E2575", {"start": v(69.4, 11.45) * mm, "end": v(69.42, 11.25) * mm});
            skLineSegment(sketch, "E2576", {"start": v(69.42, 11.25) * mm, "end": v(69.46, 11.06) * mm});
            skLineSegment(sketch, "E2577", {"start": v(69.46, 11.06) * mm, "end": v(69.5, 10.87) * mm});
            skLineSegment(sketch, "E2578", {"start": v(69.5, 10.87) * mm, "end": v(69.57, 10.68) * mm});
            skLineSegment(sketch, "E2579", {"start": v(69.57, 10.68) * mm, "end": v(69.63, 10.5) * mm});
            skLineSegment(sketch, "E2580", {"start": v(69.63, 10.5) * mm, "end": v(69.7, 10.33) * mm});
            skLineSegment(sketch, "E2581", {"start": v(69.7, 10.33) * mm, "end": v(69.79, 10.16) * mm});
            skLineSegment(sketch, "E2582", {"start": v(69.79, 10.16) * mm, "end": v(69.88, 9.99) * mm});
            skLineSegment(sketch, "E2583", {"start": v(69.88, 9.99) * mm, "end": v(69.98, 9.83) * mm});
            skLineSegment(sketch, "E2584", {"start": v(69.98, 9.83) * mm, "end": v(70.09, 9.67) * mm});
            skLineSegment(sketch, "E2585", {"start": v(70.09, 9.67) * mm, "end": v(70.2, 9.52) * mm});
            skLineSegment(sketch, "E2586", {"start": v(70.2, 9.52) * mm, "end": v(70.33, 9.37) * mm});
            skLineSegment(sketch, "E2587", {"start": v(70.33, 9.37) * mm, "end": v(70.47, 9.23) * mm});
            skLineSegment(sketch, "E2588", {"start": v(70.47, 9.23) * mm, "end": v(70.6, 9.1) * mm});
            skLineSegment(sketch, "E2589", {"start": v(70.6, 9.1) * mm, "end": v(70.75, 8.97) * mm});
            skLineSegment(sketch, "E2590", {"start": v(70.75, 8.97) * mm, "end": v(70.9, 8.86) * mm});
            skLineSegment(sketch, "E2591", {"start": v(70.9, 8.86) * mm, "end": v(71.06, 8.75) * mm});
            skLineSegment(sketch, "E2592", {"start": v(71.06, 8.75) * mm, "end": v(71.22, 8.65) * mm});
            skLineSegment(sketch, "E2593", {"start": v(71.22, 8.65) * mm, "end": v(71.39, 8.56) * mm});
            skLineSegment(sketch, "E2594", {"start": v(71.39, 8.56) * mm, "end": v(71.56, 8.47) * mm});
            skLineSegment(sketch, "E2595", {"start": v(71.56, 8.47) * mm, "end": v(71.74, 8.4) * mm});
            skLineSegment(sketch, "E2596", {"start": v(71.74, 8.4) * mm, "end": v(71.92, 8.33) * mm});
            skLineSegment(sketch, "E2597", {"start": v(71.92, 8.33) * mm, "end": v(72.1, 8.28) * mm});
            skLineSegment(sketch, "E2598", {"start": v(72.1, 8.28) * mm, "end": v(72.3, 8.23) * mm});
            skLineSegment(sketch, "E2599", {"start": v(72.3, 8.23) * mm, "end": v(72.49, 8.19) * mm});
            skLineSegment(sketch, "E2600", {"start": v(72.49, 8.19) * mm, "end": v(72.69, 8.16) * mm});
            skLineSegment(sketch, "E2601", {"start": v(72.69, 8.16) * mm, "end": v(72.9, 8.14) * mm});
            skLineSegment(sketch, "E2602", {"start": v(72.9, 8.14) * mm, "end": v(73.1, 8.12) * mm});
            skLineSegment(sketch, "E2603", {"start": v(73.1, 8.12) * mm, "end": v(73.32, 8.12) * mm});
            skLineSegment(sketch, "E2604", {"start": v(73.32, 8.12) * mm, "end": v(83.65, 8.12) * mm});
            skLineSegment(sketch, "E2605", {"start": v(83.65, 8.12) * mm, "end": v(83.7, 8.12) * mm});
            skLineSegment(sketch, "E2606", {"start": v(83.7, 8.12) * mm, "end": v(83.75, 8.1) * mm});
            skLineSegment(sketch, "E2607", {"start": v(83.75, 8.1) * mm, "end": v(83.8, 8.1) * mm});
            skLineSegment(sketch, "E2608", {"start": v(83.8, 8.1) * mm, "end": v(83.85, 8.08) * mm});
            skLineSegment(sketch, "E2609", {"start": v(83.85, 8.08) * mm, "end": v(83.9, 8.06) * mm});
            skLineSegment(sketch, "E2610", {"start": v(83.9, 8.06) * mm, "end": v(83.94, 8.03) * mm});
            skLineSegment(sketch, "E2611", {"start": v(83.94, 8.03) * mm, "end": v(83.98, 8) * mm});
            skLineSegment(sketch, "E2612", {"start": v(83.98, 8) * mm, "end": v(84.02, 7.97) * mm});
            skLineSegment(sketch, "E2613", {"start": v(84.02, 7.97) * mm, "end": v(84.05, 7.93) * mm});
            skLineSegment(sketch, "E2614", {"start": v(84.05, 7.93) * mm, "end": v(84.08, 7.89) * mm});
            skLineSegment(sketch, "E2615", {"start": v(84.08, 7.89) * mm, "end": v(84.1, 7.85) * mm});
            skLineSegment(sketch, "E2616", {"start": v(84.1, 7.85) * mm, "end": v(84.13, 7.8) * mm});
            skLineSegment(sketch, "E2617", {"start": v(84.13, 7.8) * mm, "end": v(84.15, 7.75) * mm});
            skLineSegment(sketch, "E2618", {"start": v(84.15, 7.75) * mm, "end": v(84.16, 7.7) * mm});
            skLineSegment(sketch, "E2619", {"start": v(84.16, 7.7) * mm, "end": v(84.17, 7.65) * mm});
            skLineSegment(sketch, "E2620", {"start": v(84.17, 7.65) * mm, "end": v(84.17, 7.6) * mm});
            skLineSegment(sketch, "E2621", {"start": v(84.17, 7.6) * mm, "end": v(84.17, -20.4) * mm});
            skLineSegment(sketch, "E2622", {"start": v(84.17, -20.4) * mm, "end": v(84.15, -20.7) * mm});
            skLineSegment(sketch, "E2623", {"start": v(84.15, -20.7) * mm, "end": v(84.1, -21.02) * mm});
            skLineSegment(sketch, "E2624", {"start": v(84.1, -21.02) * mm, "end": v(84.03, -21.31) * mm});
            skLineSegment(sketch, "E2625", {"start": v(84.03, -21.31) * mm, "end": v(83.93, -21.6) * mm});
            skLineSegment(sketch, "E2626", {"start": v(83.93, -21.6) * mm, "end": v(83.8, -21.87) * mm});
            skLineSegment(sketch, "E2627", {"start": v(83.8, -21.87) * mm, "end": v(83.64, -22.12) * mm});
            skLineSegment(sketch, "E2628", {"start": v(83.64, -22.12) * mm, "end": v(83.46, -22.36) * mm});
            skLineSegment(sketch, "E2629", {"start": v(83.46, -22.36) * mm, "end": v(83.26, -22.58) * mm});
            skLineSegment(sketch, "E2630", {"start": v(83.26, -22.58) * mm, "end": v(83.04, -22.78) * mm});
            skLineSegment(sketch, "E2631", {"start": v(83.04, -22.78) * mm, "end": v(82.8, -22.96) * mm});
            skLineSegment(sketch, "E2632", {"start": v(82.8, -22.96) * mm, "end": v(82.55, -23.11) * mm});
            skLineSegment(sketch, "E2633", {"start": v(82.55, -23.11) * mm, "end": v(82.28, -23.24) * mm});
            skLineSegment(sketch, "E2634", {"start": v(82.28, -23.24) * mm, "end": v(82, -23.35) * mm});
            skLineSegment(sketch, "E2635", {"start": v(82, -23.35) * mm, "end": v(81.7, -23.42) * mm});
            skLineSegment(sketch, "E2636", {"start": v(81.7, -23.42) * mm, "end": v(81.4, -23.47) * mm});
            skLineSegment(sketch, "E2637", {"start": v(81.4, -23.47) * mm, "end": v(81.08, -23.48) * mm});
            skLineSegment(sketch, "E2638", {"start": v(81.08, -23.48) * mm, "end": v(45.27, -23.48) * mm});
            skLineSegment(sketch, "E2639", {"start": v(45.27, -23.48) * mm, "end": v(45.23, -23.48) * mm});
            skLineSegment(sketch, "E2640", {"start": v(45.23, -23.48) * mm, "end": v(45.18, -23.48) * mm});
            skLineSegment(sketch, "E2641", {"start": v(45.18, -23.48) * mm, "end": v(45.14, -23.46) * mm});
            skLineSegment(sketch, "E2642", {"start": v(45.14, -23.46) * mm, "end": v(45.1, -23.45) * mm});
            skLineSegment(sketch, "E2643", {"start": v(45.1, -23.45) * mm, "end": v(45.07, -23.43) * mm});
            skLineSegment(sketch, "E2644", {"start": v(45.07, -23.43) * mm, "end": v(45.03, -23.41) * mm});
            skLineSegment(sketch, "E2645", {"start": v(45.03, -23.41) * mm, "end": v(45, -23.39) * mm});
            skLineSegment(sketch, "E2646", {"start": v(45, -23.39) * mm, "end": v(44.97, -23.36) * mm});
            skLineSegment(sketch, "E2647", {"start": v(44.97, -23.36) * mm, "end": v(44.94, -23.33) * mm});
            skLineSegment(sketch, "E2648", {"start": v(44.94, -23.33) * mm, "end": v(44.91, -23.3) * mm});
            skLineSegment(sketch, "E2649", {"start": v(44.91, -23.3) * mm, "end": v(44.9, -23.26) * mm});
            skLineSegment(sketch, "E2650", {"start": v(44.9, -23.26) * mm, "end": v(44.87, -23.22) * mm});
            skLineSegment(sketch, "E2651", {"start": v(44.87, -23.22) * mm, "end": v(44.86, -23.18) * mm});
            skLineSegment(sketch, "E2652", {"start": v(44.86, -23.18) * mm, "end": v(44.85, -23.14) * mm});
            skLineSegment(sketch, "E2653", {"start": v(44.85, -23.14) * mm, "end": v(44.84, -23.1) * mm});
            skLineSegment(sketch, "E2654", {"start": v(44.84, -23.1) * mm, "end": v(44.84, -23.05) * mm});
            skLineSegment(sketch, "E2655", {"start": v(44.84, -23.05) * mm, "end": v(44.84, -7.35) * mm});
            skLineSegment(sketch, "E2656", {"start": v(44.84, -7.35) * mm, "end": v(44.84, -7.29) * mm});
            skLineSegment(sketch, "E2657", {"start": v(44.84, -7.29) * mm, "end": v(44.85, -7.22) * mm});
            skLineSegment(sketch, "E2658", {"start": v(44.85, -7.22) * mm, "end": v(44.87, -7.16) * mm});
            skLineSegment(sketch, "E2659", {"start": v(44.87, -7.16) * mm, "end": v(44.9, -7.1) * mm});
            skLineSegment(sketch, "E2660", {"start": v(44.9, -7.1) * mm, "end": v(44.92, -7.04) * mm});
            skLineSegment(sketch, "E2661", {"start": v(44.92, -7.04) * mm, "end": v(44.95, -6.99) * mm});
            skLineSegment(sketch, "E2662", {"start": v(44.95, -6.99) * mm, "end": v(45, -6.94) * mm});
            skLineSegment(sketch, "E2663", {"start": v(45, -6.94) * mm, "end": v(45.03, -6.9) * mm});
            skLineSegment(sketch, "E2664", {"start": v(45.03, -6.9) * mm, "end": v(45.08, -6.85) * mm});
            skLineSegment(sketch, "E2665", {"start": v(45.08, -6.85) * mm, "end": v(45.13, -6.81) * mm});
            skLineSegment(sketch, "E2666", {"start": v(45.13, -6.81) * mm, "end": v(45.18, -6.78) * mm});
            skLineSegment(sketch, "E2667", {"start": v(45.18, -6.78) * mm, "end": v(45.24, -6.75) * mm});
            skLineSegment(sketch, "E2668", {"start": v(45.24, -6.75) * mm, "end": v(45.3, -6.73) * mm});
            skLineSegment(sketch, "E2669", {"start": v(45.3, -6.73) * mm, "end": v(45.36, -6.71) * mm});
            skLineSegment(sketch, "E2670", {"start": v(45.36, -6.71) * mm, "end": v(45.43, -6.7) * mm});
            skLineSegment(sketch, "E2671", {"start": v(45.43, -6.7) * mm, "end": v(45.5, -6.7) * mm});
            skLineSegment(sketch, "E2672", {"start": v(45.5, -6.7) * mm, "end": v(53.26, -6.7) * mm});
            skLineSegment(sketch, "E2673", {"start": v(53.26, -6.7) * mm, "end": v(53.75, -6.69) * mm});
            skLineSegment(sketch, "E2674", {"start": v(53.75, -6.69) * mm, "end": v(54.24, -6.66) * mm});
            skLineSegment(sketch, "E2675", {"start": v(54.24, -6.66) * mm, "end": v(54.73, -6.62) * mm});
            skLineSegment(sketch, "E2676", {"start": v(54.73, -6.62) * mm, "end": v(55.2, -6.55) * mm});
            skLineSegment(sketch, "E2677", {"start": v(55.2, -6.55) * mm, "end": v(55.67, -6.47) * mm});
            skLineSegment(sketch, "E2678", {"start": v(55.67, -6.47) * mm, "end": v(56.14, -6.37) * mm});
            skLineSegment(sketch, "E2679", {"start": v(56.14, -6.37) * mm, "end": v(56.6, -6.26) * mm});
            skLineSegment(sketch, "E2680", {"start": v(56.6, -6.26) * mm, "end": v(57.05, -6.12) * mm});
            skLineSegment(sketch, "E2681", {"start": v(57.05, -6.12) * mm, "end": v(57.5, -5.97) * mm});
            skLineSegment(sketch, "E2682", {"start": v(57.5, -5.97) * mm, "end": v(57.93, -5.8) * mm});
            skLineSegment(sketch, "E2683", {"start": v(57.93, -5.8) * mm, "end": v(58.36, -5.61) * mm});
            skLineSegment(sketch, "E2684", {"start": v(58.36, -5.61) * mm, "end": v(58.78, -5.4) * mm});
            skLineSegment(sketch, "E2685", {"start": v(58.78, -5.4) * mm, "end": v(59.2, -5.18) * mm});
            skLineSegment(sketch, "E2686", {"start": v(59.2, -5.18) * mm, "end": v(59.61, -4.94) * mm});
            skLineSegment(sketch, "E2687", {"start": v(59.61, -4.94) * mm, "end": v(60.01, -4.68) * mm});
            skLineSegment(sketch, "E2688", {"start": v(60.01, -4.68) * mm, "end": v(60.41, -4.4) * mm});
            skLineSegment(sketch, "E2689", {"start": v(60.41, -4.4) * mm, "end": v(60.92, -4) * mm});
            skLineSegment(sketch, "E2690", {"start": v(60.92, -4) * mm, "end": v(61.4, -3.59) * mm});
            skLineSegment(sketch, "E2691", {"start": v(61.4, -3.59) * mm, "end": v(61.84, -3.14) * mm});
            skLineSegment(sketch, "E2692", {"start": v(61.84, -3.14) * mm, "end": v(62.25, -2.68) * mm});
            skLineSegment(sketch, "E2693", {"start": v(62.25, -2.68) * mm, "end": v(62.63, -2.19) * mm});
            skLineSegment(sketch, "E2694", {"start": v(62.63, -2.19) * mm, "end": v(62.98, -1.67) * mm});
            skLineSegment(sketch, "E2695", {"start": v(62.98, -1.67) * mm, "end": v(63.3, -1.14) * mm});
            skLineSegment(sketch, "E2696", {"start": v(63.3, -1.14) * mm, "end": v(63.57, -0.58) * mm});
            skLineSegment(sketch, "E2697", {"start": v(63.57, -0.58) * mm, "end": v(63.82, 0) * mm});
            skLineSegment(sketch, "E2698", {"start": v(63.82, 0) * mm, "end": v(64.03, 0.6) * mm});
            skLineSegment(sketch, "E2699", {"start": v(64.03, 0.6) * mm, "end": v(64.22, 1.22) * mm});
            skLineSegment(sketch, "E2700", {"start": v(64.22, 1.22) * mm, "end": v(64.37, 1.87) * mm});
            skLineSegment(sketch, "E2701", {"start": v(64.37, 1.87) * mm, "end": v(64.48, 2.54) * mm});
            skLineSegment(sketch, "E2702", {"start": v(64.48, 2.54) * mm, "end": v(64.56, 3.23) * mm});
            skLineSegment(sketch, "E2703", {"start": v(64.56, 3.23) * mm, "end": v(64.61, 3.94) * mm});
            skLineSegment(sketch, "E2704", {"start": v(64.61, 3.94) * mm, "end": v(64.63, 4.67) * mm});
            skLineSegment(sketch, "E2705", {"start": v(64.63, 4.67) * mm, "end": v(64.61, 5.4) * mm});
            skLineSegment(sketch, "E2706", {"start": v(64.61, 5.4) * mm, "end": v(64.56, 6.12) * mm});
            skLineSegment(sketch, "E2707", {"start": v(64.56, 6.12) * mm, "end": v(64.48, 6.8) * mm});
            skLineSegment(sketch, "E2708", {"start": v(64.48, 6.8) * mm, "end": v(64.37, 7.48) * mm});
            skLineSegment(sketch, "E2709", {"start": v(64.37, 7.48) * mm, "end": v(64.22, 8.12) * mm});
            skLineSegment(sketch, "E2710", {"start": v(64.22, 8.12) * mm, "end": v(64.03, 8.75) * mm});
            skLineSegment(sketch, "E2711", {"start": v(64.03, 8.75) * mm, "end": v(63.82, 9.35) * mm});
            skLineSegment(sketch, "E2712", {"start": v(63.82, 9.35) * mm, "end": v(63.57, 9.93) * mm});
            skLineSegment(sketch, "E2713", {"start": v(63.57, 9.93) * mm, "end": v(63.3, 10.48) * mm});
            skLineSegment(sketch, "E2714", {"start": v(63.3, 10.48) * mm, "end": v(62.98, 11.02) * mm});
            skLineSegment(sketch, "E2715", {"start": v(62.98, 11.02) * mm, "end": v(62.63, 11.53) * mm});
            skLineSegment(sketch, "E2716", {"start": v(62.63, 11.53) * mm, "end": v(62.25, 12.02) * mm});
            skLineSegment(sketch, "E2717", {"start": v(62.25, 12.02) * mm, "end": v(61.84, 12.49) * mm});
            skLineSegment(sketch, "E2718", {"start": v(61.84, 12.49) * mm, "end": v(61.4, 12.93) * mm});
            skLineSegment(sketch, "E2719", {"start": v(61.4, 12.93) * mm, "end": v(60.92, 13.35) * mm});
            skLineSegment(sketch, "E2720", {"start": v(60.92, 13.35) * mm, "end": v(60.4, 13.75) * mm});
            skLineSegment(sketch, "E2721", {"start": v(60.4, 13.75) * mm, "end": v(60.01, 14.03) * mm});
            skLineSegment(sketch, "E2722", {"start": v(60.01, 14.03) * mm, "end": v(59.61, 14.29) * mm});
            skLineSegment(sketch, "E2723", {"start": v(59.61, 14.29) * mm, "end": v(59.2, 14.53) * mm});
            skLineSegment(sketch, "E2724", {"start": v(59.2, 14.53) * mm, "end": v(58.78, 14.75) * mm});
            skLineSegment(sketch, "E2725", {"start": v(58.78, 14.75) * mm, "end": v(58.36, 14.96) * mm});
            skLineSegment(sketch, "E2726", {"start": v(58.36, 14.96) * mm, "end": v(57.93, 15.15) * mm});
            skLineSegment(sketch, "E2727", {"start": v(57.93, 15.15) * mm, "end": v(57.5, 15.32) * mm});
            skLineSegment(sketch, "E2728", {"start": v(57.5, 15.32) * mm, "end": v(57.05, 15.47) * mm});
            skLineSegment(sketch, "E2729", {"start": v(57.05, 15.47) * mm, "end": v(56.6, 15.6) * mm});
            skLineSegment(sketch, "E2730", {"start": v(56.6, 15.6) * mm, "end": v(56.14, 15.72) * mm});
            skLineSegment(sketch, "E2731", {"start": v(56.14, 15.72) * mm, "end": v(55.67, 15.82) * mm});
            skLineSegment(sketch, "E2732", {"start": v(55.67, 15.82) * mm, "end": v(55.2, 15.9) * mm});
            skLineSegment(sketch, "E2733", {"start": v(55.2, 15.9) * mm, "end": v(54.73, 15.96) * mm});
            skLineSegment(sketch, "E2734", {"start": v(54.73, 15.96) * mm, "end": v(54.24, 16) * mm});
            skLineSegment(sketch, "E2735", {"start": v(54.24, 16) * mm, "end": v(53.75, 16.04) * mm});
            skLineSegment(sketch, "E2736", {"start": v(53.75, 16.04) * mm, "end": v(53.26, 16.04) * mm});
            skLineSegment(sketch, "E2737", {"start": v(53.26, 16.04) * mm, "end": v(39.5, 16.04) * mm});
            skLineSegment(sketch, "E2738", {"start": v(39.5, 16.04) * mm, "end": v(39.24, 16.03) * mm});
            skLineSegment(sketch, "E2739", {"start": v(39.24, 16.03) * mm, "end": v(38.98, 16) * mm});
            skLineSegment(sketch, "E2740", {"start": v(38.98, 16) * mm, "end": v(38.74, 15.93) * mm});
            skLineSegment(sketch, "E2741", {"start": v(38.74, 15.93) * mm, "end": v(38.5, 15.84) * mm});
            skLineSegment(sketch, "E2742", {"start": v(38.5, 15.84) * mm, "end": v(38.27, 15.73) * mm});
            skLineSegment(sketch, "E2743", {"start": v(38.27, 15.73) * mm, "end": v(38.06, 15.6) * mm});
            skLineSegment(sketch, "E2744", {"start": v(38.06, 15.6) * mm, "end": v(37.86, 15.45) * mm});
            skLineSegment(sketch, "E2745", {"start": v(37.86, 15.45) * mm, "end": v(37.67, 15.29) * mm});
            skLineSegment(sketch, "E2746", {"start": v(37.67, 15.29) * mm, "end": v(37.5, 15.1) * mm});
            skLineSegment(sketch, "E2747", {"start": v(37.5, 15.1) * mm, "end": v(37.36, 14.9) * mm});
            skLineSegment(sketch, "E2748", {"start": v(37.36, 14.9) * mm, "end": v(37.23, 14.69) * mm});
            skLineSegment(sketch, "E2749", {"start": v(37.23, 14.69) * mm, "end": v(37.12, 14.46) * mm});
            skLineSegment(sketch, "E2750", {"start": v(37.12, 14.46) * mm, "end": v(37.03, 14.22) * mm});
            skLineSegment(sketch, "E2751", {"start": v(37.03, 14.22) * mm, "end": v(36.97, 13.98) * mm});
            skLineSegment(sketch, "E2752", {"start": v(36.97, 13.98) * mm, "end": v(36.93, 13.72) * mm});
            skLineSegment(sketch, "E2753", {"start": v(36.93, 13.72) * mm, "end": v(36.91, 13.45) * mm});
            skLineSegment(sketch, "E2754", {"start": v(36.91, 13.45) * mm, "end": v(36.91, -22.53) * mm});
            skLineSegment(sketch, "E2755", {"start": v(36.91, -22.53) * mm, "end": v(36.91, -22.64) * mm});
            skLineSegment(sketch, "E2756", {"start": v(36.91, -22.64) * mm, "end": v(36.9, -22.74) * mm});
            skLineSegment(sketch, "E2757", {"start": v(36.9, -22.74) * mm, "end": v(36.88, -22.84) * mm});
            skLineSegment(sketch, "E2758", {"start": v(36.88, -22.84) * mm, "end": v(36.85, -22.93) * mm});
            skLineSegment(sketch, "E2759", {"start": v(36.85, -22.93) * mm, "end": v(36.82, -23.01) * mm});
            skLineSegment(sketch, "E2760", {"start": v(36.82, -23.01) * mm, "end": v(36.77, -23.09) * mm});
            skLineSegment(sketch, "E2761", {"start": v(36.77, -23.09) * mm, "end": v(36.72, -23.16) * mm});
            skLineSegment(sketch, "E2762", {"start": v(36.72, -23.16) * mm, "end": v(36.66, -23.22) * mm});
            skLineSegment(sketch, "E2763", {"start": v(36.66, -23.22) * mm, "end": v(36.6, -23.28) * mm});
            skLineSegment(sketch, "E2764", {"start": v(36.6, -23.28) * mm, "end": v(36.52, -23.33) * mm});
            skLineSegment(sketch, "E2765", {"start": v(36.52, -23.33) * mm, "end": v(36.44, -23.37) * mm});
            skLineSegment(sketch, "E2766", {"start": v(36.44, -23.37) * mm, "end": v(36.35, -23.4) * mm});
            skLineSegment(sketch, "E2767", {"start": v(36.35, -23.4) * mm, "end": v(36.25, -23.44) * mm});
            skLineSegment(sketch, "E2768", {"start": v(36.25, -23.44) * mm, "end": v(36.14, -23.46) * mm});
            skLineSegment(sketch, "E2769", {"start": v(36.14, -23.46) * mm, "end": v(36.03, -23.47) * mm});
            skLineSegment(sketch, "E2770", {"start": v(36.03, -23.47) * mm, "end": v(35.9, -23.48) * mm});
            skLineSegment(sketch, "E2771", {"start": v(35.9, -23.48) * mm, "end": v(33.5, -23.48) * mm});
            skLineSegment(sketch, "E2772", {"start": v(33.5, -23.48) * mm, "end": v(33.46, -23.48) * mm});
            skLineSegment(sketch, "E2773", {"start": v(33.46, -23.48) * mm, "end": v(33.43, -23.48) * mm});
            skLineSegment(sketch, "E2774", {"start": v(33.43, -23.48) * mm, "end": v(33.39, -23.47) * mm});
            skLineSegment(sketch, "E2775", {"start": v(33.39, -23.47) * mm, "end": v(33.35, -23.46) * mm});
            skLineSegment(sketch, "E2776", {"start": v(33.35, -23.46) * mm, "end": v(33.31, -23.45) * mm});
            skLineSegment(sketch, "E2777", {"start": v(33.31, -23.45) * mm, "end": v(33.28, -23.44) * mm});
            skLineSegment(sketch, "E2778", {"start": v(33.28, -23.44) * mm, "end": v(33.25, -23.42) * mm});
            skLineSegment(sketch, "E2779", {"start": v(33.25, -23.42) * mm, "end": v(33.21, -23.4) * mm});
            skLineSegment(sketch, "E2780", {"start": v(33.21, -23.4) * mm, "end": v(33.18, -23.38) * mm});
            skLineSegment(sketch, "E2781", {"start": v(33.18, -23.38) * mm, "end": v(33.15, -23.36) * mm});
            skLineSegment(sketch, "E2782", {"start": v(33.15, -23.36) * mm, "end": v(33.12, -23.33) * mm});
            skLineSegment(sketch, "E2783", {"start": v(33.12, -23.33) * mm, "end": v(33.1, -23.3) * mm});
            skLineSegment(sketch, "E2784", {"start": v(33.1, -23.3) * mm, "end": v(33.07, -23.28) * mm});
            skLineSegment(sketch, "E2785", {"start": v(33.07, -23.28) * mm, "end": v(33.05, -23.25) * mm});
            skLineSegment(sketch, "E2786", {"start": v(33.05, -23.25) * mm, "end": v(33.03, -23.21) * mm});
            skLineSegment(sketch, "E2787", {"start": v(33.03, -23.21) * mm, "end": v(33, -23.18) * mm});
            skLineSegment(sketch, "E2788", {"start": v(33, -23.18) * mm, "end": v(26.3, -9.7) * mm});
            skLineSegment(sketch, "E2789", {"start": v(26.3, -9.7) * mm, "end": v(26.23, -9.58) * mm});
            skLineSegment(sketch, "E2790", {"start": v(26.23, -9.58) * mm, "end": v(26.15, -9.46) * mm});
            skLineSegment(sketch, "E2791", {"start": v(26.15, -9.46) * mm, "end": v(26.07, -9.35) * mm});
            skLineSegment(sketch, "E2792", {"start": v(26.07, -9.35) * mm, "end": v(25.98, -9.25) * mm});
            skLineSegment(sketch, "E2793", {"start": v(25.98, -9.25) * mm, "end": v(25.9, -9.15) * mm});
            skLineSegment(sketch, "E2794", {"start": v(25.9, -9.15) * mm, "end": v(25.79, -9.06) * mm});
            skLineSegment(sketch, "E2795", {"start": v(25.79, -9.06) * mm, "end": v(25.68, -8.98) * mm});
            skLineSegment(sketch, "E2796", {"start": v(25.68, -8.98) * mm, "end": v(25.57, -8.9) * mm});
            skLineSegment(sketch, "E2797", {"start": v(25.57, -8.9) * mm, "end": v(25.46, -8.84) * mm});
            skLineSegment(sketch, "E2798", {"start": v(25.46, -8.84) * mm, "end": v(25.34, -8.78) * mm});
            skLineSegment(sketch, "E2799", {"start": v(25.34, -8.78) * mm, "end": v(25.21, -8.73) * mm});
            skLineSegment(sketch, "E2800", {"start": v(25.21, -8.73) * mm, "end": v(25.08, -8.7) * mm});
            skLineSegment(sketch, "E2801", {"start": v(25.08, -8.7) * mm, "end": v(24.95, -8.66) * mm});
            skLineSegment(sketch, "E2802", {"start": v(24.95, -8.66) * mm, "end": v(24.82, -8.63) * mm});
            skLineSegment(sketch, "E2803", {"start": v(24.82, -8.63) * mm, "end": v(24.68, -8.62) * mm});
            skLineSegment(sketch, "E2804", {"start": v(24.68, -8.62) * mm, "end": v(24.54, -8.61) * mm});
            skLineSegment(sketch, "E2805", {"start": v(24.54, -8.61) * mm, "end": v(9.92, -8.61) * mm});
            skLineSegment(sketch, "E2806", {"start": v(9.92, -8.61) * mm, "end": v(9.8, -8.61) * mm});
            skLineSegment(sketch, "E2807", {"start": v(9.8, -8.61) * mm, "end": v(9.68, -8.6) * mm});
            skLineSegment(sketch, "E2808", {"start": v(9.68, -8.6) * mm, "end": v(9.57, -8.58) * mm});
            skLineSegment(sketch, "E2809", {"start": v(9.57, -8.58) * mm, "end": v(9.47, -8.56) * mm});
            skLineSegment(sketch, "E2810", {"start": v(9.47, -8.56) * mm, "end": v(9.38, -8.52) * mm});
            skLineSegment(sketch, "E2811", {"start": v(9.38, -8.52) * mm, "end": v(9.3, -8.48) * mm});
            skLineSegment(sketch, "E2812", {"start": v(9.3, -8.48) * mm, "end": v(9.22, -8.43) * mm});
            skLineSegment(sketch, "E2813", {"start": v(9.22, -8.43) * mm, "end": v(9.16, -8.37) * mm});
            skLineSegment(sketch, "E2814", {"start": v(9.16, -8.37) * mm, "end": v(9.1, -8.3) * mm});
            skLineSegment(sketch, "E2815", {"start": v(9.1, -8.3) * mm, "end": v(9.05, -8.24) * mm});
            skLineSegment(sketch, "E2816", {"start": v(9.05, -8.24) * mm, "end": v(9, -8.16) * mm});
            skLineSegment(sketch, "E2817", {"start": v(9, -8.16) * mm, "end": v(8.97, -8.07) * mm});
            skLineSegment(sketch, "E2818", {"start": v(8.97, -8.07) * mm, "end": v(8.94, -7.97) * mm});
            skLineSegment(sketch, "E2819", {"start": v(8.94, -7.97) * mm, "end": v(8.93, -7.87) * mm});
            skLineSegment(sketch, "E2820", {"start": v(8.93, -7.87) * mm, "end": v(8.91, -7.75) * mm});
            skLineSegment(sketch, "E2821", {"start": v(8.91, -7.75) * mm, "end": v(8.91, -7.63) * mm});
            skLineSegment(sketch, "E2822", {"start": v(8.91, -7.63) * mm, "end": v(8.91, -7.52) * mm});
            skLineSegment(sketch, "E2823", {"start": v(8.91, -7.52) * mm, "end": v(8.93, -7.4) * mm});
            skLineSegment(sketch, "E2824", {"start": v(8.93, -7.4) * mm, "end": v(8.94, -7.3) * mm});
            skLineSegment(sketch, "E2825", {"start": v(8.94, -7.3) * mm, "end": v(8.97, -7.22) * mm});
            skLineSegment(sketch, "E2826", {"start": v(8.97, -7.22) * mm, "end": v(9, -7.13) * mm});
            skLineSegment(sketch, "E2827", {"start": v(9, -7.13) * mm, "end": v(9.05, -7.06) * mm});
            skLineSegment(sketch, "E2828", {"start": v(9.05, -7.06) * mm, "end": v(9.1, -6.99) * mm});
            skLineSegment(sketch, "E2829", {"start": v(9.1, -6.99) * mm, "end": v(9.16, -6.93) * mm});
            skLineSegment(sketch, "E2830", {"start": v(9.16, -6.93) * mm, "end": v(9.22, -6.87) * mm});
            skLineSegment(sketch, "E2831", {"start": v(9.22, -6.87) * mm, "end": v(9.3, -6.83) * mm});
            skLineSegment(sketch, "E2832", {"start": v(9.3, -6.83) * mm, "end": v(9.38, -6.79) * mm});
            skLineSegment(sketch, "E2833", {"start": v(9.38, -6.79) * mm, "end": v(9.47, -6.75) * mm});
            skLineSegment(sketch, "E2834", {"start": v(9.47, -6.75) * mm, "end": v(9.57, -6.73) * mm});
            skLineSegment(sketch, "E2835", {"start": v(9.57, -6.73) * mm, "end": v(9.68, -6.71) * mm});
            skLineSegment(sketch, "E2836", {"start": v(9.68, -6.71) * mm, "end": v(9.8, -6.7) * mm});
            skLineSegment(sketch, "E2837", {"start": v(9.8, -6.7) * mm, "end": v(9.92, -6.7) * mm});
            skLineSegment(sketch, "E2838", {"start": v(9.92, -6.7) * mm, "end": v(21.86, -6.7) * mm});
            skLineSegment(sketch, "E2839", {"start": v(21.86, -6.7) * mm, "end": v(21.98, -6.7) * mm});
            skLineSegment(sketch, "E2840", {"start": v(21.98, -6.7) * mm, "end": v(22.1, -6.68) * mm});
            skLineSegment(sketch, "E2841", {"start": v(22.1, -6.68) * mm, "end": v(22.2, -6.67) * mm});
            skLineSegment(sketch, "E2842", {"start": v(22.2, -6.67) * mm, "end": v(22.31, -6.64) * mm});
            skLineSegment(sketch, "E2843", {"start": v(22.31, -6.64) * mm, "end": v(22.42, -6.6) * mm});
            skLineSegment(sketch, "E2844", {"start": v(22.42, -6.6) * mm, "end": v(22.53, -6.57) * mm});
            skLineSegment(sketch, "E2845", {"start": v(22.53, -6.57) * mm, "end": v(22.63, -6.53) * mm});
            skLineSegment(sketch, "E2846", {"start": v(22.63, -6.53) * mm, "end": v(22.73, -6.47) * mm});
            skLineSegment(sketch, "E2847", {"start": v(22.73, -6.47) * mm, "end": v(22.83, -6.42) * mm});
            skLineSegment(sketch, "E2848", {"start": v(22.83, -6.42) * mm, "end": v(22.92, -6.35) * mm});
            skLineSegment(sketch, "E2849", {"start": v(22.92, -6.35) * mm, "end": v(23, -6.28) * mm});
            skLineSegment(sketch, "E2850", {"start": v(23, -6.28) * mm, "end": v(23.1, -6.2) * mm});
            skLineSegment(sketch, "E2851", {"start": v(23.1, -6.2) * mm, "end": v(23.17, -6.13) * mm});
            skLineSegment(sketch, "E2852", {"start": v(23.17, -6.13) * mm, "end": v(23.25, -6.04) * mm});
            skLineSegment(sketch, "E2853", {"start": v(23.25, -6.04) * mm, "end": v(23.32, -5.95) * mm});
            skLineSegment(sketch, "E2854", {"start": v(23.32, -5.95) * mm, "end": v(23.38, -5.85) * mm});
            skLineSegment(sketch, "E2855", {"start": v(23.38, -5.85) * mm, "end": v(23.44, -5.75) * mm});
            skLineSegment(sketch, "E2856", {"start": v(23.44, -5.75) * mm, "end": v(23.49, -5.65) * mm});
            skLineSegment(sketch, "E2857", {"start": v(23.49, -5.65) * mm, "end": v(23.53, -5.54) * mm});
            skLineSegment(sketch, "E2858", {"start": v(23.53, -5.54) * mm, "end": v(23.57, -5.44) * mm});
            skLineSegment(sketch, "E2859", {"start": v(23.57, -5.44) * mm, "end": v(23.6, -5.33) * mm});
            skLineSegment(sketch, "E2860", {"start": v(23.6, -5.33) * mm, "end": v(23.62, -5.22) * mm});
            skLineSegment(sketch, "E2861", {"start": v(23.62, -5.22) * mm, "end": v(23.64, -5.1) * mm});
            skLineSegment(sketch, "E2862", {"start": v(23.64, -5.1) * mm, "end": v(23.65, -5) * mm});
            skLineSegment(sketch, "E2863", {"start": v(23.65, -5) * mm, "end": v(23.65, -4.88) * mm});
            skLineSegment(sketch, "E2864", {"start": v(23.65, -4.88) * mm, "end": v(23.65, -4.77) * mm});
            skLineSegment(sketch, "E2865", {"start": v(23.65, -4.77) * mm, "end": v(23.63, -4.66) * mm});
            skLineSegment(sketch, "E2866", {"start": v(23.63, -4.66) * mm, "end": v(23.61, -4.55) * mm});
            skLineSegment(sketch, "E2867", {"start": v(23.61, -4.55) * mm, "end": v(23.59, -4.44) * mm});
            skLineSegment(sketch, "E2868", {"start": v(23.59, -4.44) * mm, "end": v(23.55, -4.33) * mm});
            skLineSegment(sketch, "E2869", {"start": v(23.55, -4.33) * mm, "end": v(23.51, -4.22) * mm});
            skLineSegment(sketch, "E2870", {"start": v(23.51, -4.22) * mm, "end": v(23.46, -4.12) * mm});
            skLineSegment(sketch, "E2871", {"start": v(23.46, -4.12) * mm, "end": v(13.73, 15.58) * mm});
            skLineSegment(sketch, "E2872", {"start": v(13.73, 15.58) * mm, "end": v(13.69, 15.66) * mm});
            skLineSegment(sketch, "E2873", {"start": v(13.69, 15.66) * mm, "end": v(13.64, 15.74) * mm});
            skLineSegment(sketch, "E2874", {"start": v(13.64, 15.74) * mm, "end": v(13.58, 15.81) * mm});
            skLineSegment(sketch, "E2875", {"start": v(13.58, 15.81) * mm, "end": v(13.52, 15.88) * mm});
            skLineSegment(sketch, "E2876", {"start": v(13.52, 15.88) * mm, "end": v(13.46, 15.95) * mm});
            skLineSegment(sketch, "E2877", {"start": v(13.46, 15.95) * mm, "end": v(13.4, 16) * mm});
            skLineSegment(sketch, "E2878", {"start": v(13.4, 16) * mm, "end": v(13.32, 16.06) * mm});
            skLineSegment(sketch, "E2879", {"start": v(13.32, 16.06) * mm, "end": v(13.25, 16.11) * mm});
            skLineSegment(sketch, "E2880", {"start": v(13.25, 16.11) * mm, "end": v(13.17, 16.16) * mm});
            skLineSegment(sketch, "E2881", {"start": v(13.17, 16.16) * mm, "end": v(13.1, 16.2) * mm});
            skLineSegment(sketch, "E2882", {"start": v(13.1, 16.2) * mm, "end": v(13, 16.23) * mm});
            skLineSegment(sketch, "E2883", {"start": v(13, 16.23) * mm, "end": v(12.92, 16.26) * mm});
            skLineSegment(sketch, "E2884", {"start": v(12.92, 16.26) * mm, "end": v(12.83, 16.28) * mm});
            skLineSegment(sketch, "E2885", {"start": v(12.83, 16.28) * mm, "end": v(12.74, 16.3) * mm});
            skLineSegment(sketch, "E2886", {"start": v(12.74, 16.3) * mm, "end": v(12.65, 16.3) * mm});
            skLineSegment(sketch, "E2887", {"start": v(12.65, 16.3) * mm, "end": v(12.56, 16.3) * mm});
            skLineSegment(sketch, "E2888", {"start": v(12.56, 16.3) * mm, "end": v(12.38, 16.3) * mm});
            skLineSegment(sketch, "E2889", {"start": v(12.38, 16.3) * mm, "end": v(12.29, 16.3) * mm});
            skLineSegment(sketch, "E2890", {"start": v(12.29, 16.3) * mm, "end": v(12.2, 16.3) * mm});
            skLineSegment(sketch, "E2891", {"start": v(12.2, 16.3) * mm, "end": v(12.12, 16.28) * mm});
            skLineSegment(sketch, "E2892", {"start": v(12.12, 16.28) * mm, "end": v(12.03, 16.26) * mm});
            skLineSegment(sketch, "E2893", {"start": v(12.03, 16.26) * mm, "end": v(11.95, 16.23) * mm});
            skLineSegment(sketch, "E2894", {"start": v(11.95, 16.23) * mm, "end": v(11.87, 16.2) * mm});
            skLineSegment(sketch, "E2895", {"start": v(11.87, 16.2) * mm, "end": v(11.8, 16.17) * mm});
            skLineSegment(sketch, "E2896", {"start": v(11.8, 16.17) * mm, "end": v(11.72, 16.12) * mm});
            skLineSegment(sketch, "E2897", {"start": v(11.72, 16.12) * mm, "end": v(11.65, 16.08) * mm});
            skLineSegment(sketch, "E2898", {"start": v(11.65, 16.08) * mm, "end": v(11.58, 16.03) * mm});
            skLineSegment(sketch, "E2899", {"start": v(11.58, 16.03) * mm, "end": v(11.52, 15.97) * mm});
            skLineSegment(sketch, "E2900", {"start": v(11.52, 15.97) * mm, "end": v(11.46, 15.9) * mm});
            skLineSegment(sketch, "E2901", {"start": v(11.46, 15.9) * mm, "end": v(11.4, 15.84) * mm});
            skLineSegment(sketch, "E2902", {"start": v(11.4, 15.84) * mm, "end": v(11.35, 15.77) * mm});
            skLineSegment(sketch, "E2903", {"start": v(11.35, 15.77) * mm, "end": v(11.3, 15.7) * mm});
            skLineSegment(sketch, "E2904", {"start": v(11.3, 15.7) * mm, "end": v(11.26, 15.62) * mm});
            skLineSegment(sketch, "E2905", {"start": v(11.26, 15.62) * mm, "end": v(-8.01, -22.72) * mm});
            skLineSegment(sketch, "E2906", {"start": v(-8.01, -22.72) * mm, "end": v(-8.06, -22.8) * mm});
            skLineSegment(sketch, "E2907", {"start": v(-8.06, -22.8) * mm, "end": v(-8.11, -22.89) * mm});
            skLineSegment(sketch, "E2908", {"start": v(-8.11, -22.89) * mm, "end": v(-8.17, -22.96) * mm});
            skLineSegment(sketch, "E2909", {"start": v(-8.17, -22.96) * mm, "end": v(-8.23, -23.04) * mm});
            skLineSegment(sketch, "E2910", {"start": v(-8.23, -23.04) * mm, "end": v(-8.3, -23.1) * mm});
            skLineSegment(sketch, "E2911", {"start": v(-8.3, -23.1) * mm, "end": v(-8.37, -23.17) * mm});
            skLineSegment(sketch, "E2912", {"start": v(-8.37, -23.17) * mm, "end": v(-8.44, -23.23) * mm});
            skLineSegment(sketch, "E2913", {"start": v(-8.44, -23.23) * mm, "end": v(-8.52, -23.28) * mm});
            skLineSegment(sketch, "E2914", {"start": v(-8.52, -23.28) * mm, "end": v(-8.6, -23.32) * mm});
            skLineSegment(sketch, "E2915", {"start": v(-8.6, -23.32) * mm, "end": v(-8.7, -23.37) * mm});
            skLineSegment(sketch, "E2916", {"start": v(-8.7, -23.37) * mm, "end": v(-8.78, -23.4) * mm});
            skLineSegment(sketch, "E2917", {"start": v(-8.78, -23.4) * mm, "end": v(-8.87, -23.43) * mm});
            skLineSegment(sketch, "E2918", {"start": v(-8.87, -23.43) * mm, "end": v(-8.96, -23.45) * mm});
            skLineSegment(sketch, "E2919", {"start": v(-8.96, -23.45) * mm, "end": v(-9.06, -23.47) * mm});
            skLineSegment(sketch, "E2920", {"start": v(-9.06, -23.47) * mm, "end": v(-9.16, -23.48) * mm});
            skLineSegment(sketch, "E2921", {"start": v(-9.16, -23.48) * mm, "end": v(-9.25, -23.48) * mm});
            skLineSegment(sketch, "E2922", {"start": v(-9.25, -23.48) * mm, "end": v(-11.94, -23.48) * mm});
            skLineSegment(sketch, "E2923", {"start": v(-11.94, -23.48) * mm, "end": v(-12.06, -23.48) * mm});
            skLineSegment(sketch, "E2924", {"start": v(-12.06, -23.48) * mm, "end": v(-12.17, -23.47) * mm});
            skLineSegment(sketch, "E2925", {"start": v(-12.17, -23.47) * mm, "end": v(-12.28, -23.46) * mm});
            skLineSegment(sketch, "E2926", {"start": v(-12.28, -23.46) * mm, "end": v(-12.4, -23.44) * mm});
            skLineSegment(sketch, "E2927", {"start": v(-12.4, -23.44) * mm, "end": v(-12.5, -23.42) * mm});
            skLineSegment(sketch, "E2928", {"start": v(-12.5, -23.42) * mm, "end": v(-12.61, -23.39) * mm});
            skLineSegment(sketch, "E2929", {"start": v(-12.61, -23.39) * mm, "end": v(-12.72, -23.35) * mm});
            skLineSegment(sketch, "E2930", {"start": v(-12.72, -23.35) * mm, "end": v(-12.82, -23.3) * mm});
            skLineSegment(sketch, "E2931", {"start": v(-12.82, -23.3) * mm, "end": v(-12.93, -23.26) * mm});
            skLineSegment(sketch, "E2932", {"start": v(-12.93, -23.26) * mm, "end": v(-13.03, -23.21) * mm});
            skLineSegment(sketch, "E2933", {"start": v(-13.03, -23.21) * mm, "end": v(-13.12, -23.16) * mm});
            skLineSegment(sketch, "E2934", {"start": v(-13.12, -23.16) * mm, "end": v(-13.22, -23.1) * mm});
            skLineSegment(sketch, "E2935", {"start": v(-13.22, -23.1) * mm, "end": v(-13.31, -23.03) * mm});
            skLineSegment(sketch, "E2936", {"start": v(-13.31, -23.03) * mm, "end": v(-13.4, -22.96) * mm});
            skLineSegment(sketch, "E2937", {"start": v(-13.4, -22.96) * mm, "end": v(-13.49, -22.89) * mm});
            skLineSegment(sketch, "E2938", {"start": v(-13.49, -22.89) * mm, "end": v(-13.57, -22.8) * mm});
            skLineSegment(sketch, "E2939", {"start": v(-13.57, -22.8) * mm, "end": v(-29.29, -7.1) * mm});
            skLineSegment(sketch, "E2940", {"start": v(-29.29, -7.1) * mm, "end": v(-29.3, -7.08) * mm});
            skLineSegment(sketch, "E2941", {"start": v(-29.3, -7.08) * mm, "end": v(-29.31, -7.06) * mm});
            skLineSegment(sketch, "E2942", {"start": v(-29.31, -7.06) * mm, "end": v(-29.33, -7.04) * mm});
            skLineSegment(sketch, "E2943", {"start": v(-29.33, -7.04) * mm, "end": v(-29.33, -7.03) * mm});
            skLineSegment(sketch, "E2944", {"start": v(-29.33, -7.03) * mm, "end": v(-29.34, -7.01) * mm});
            skLineSegment(sketch, "E2945", {"start": v(-29.34, -7.01) * mm, "end": v(-29.35, -7) * mm});
            skLineSegment(sketch, "E2946", {"start": v(-29.35, -7) * mm, "end": v(-29.35, -6.98) * mm});
            skLineSegment(sketch, "E2947", {"start": v(-29.35, -6.98) * mm, "end": v(-29.35, -6.96) * mm});
            skLineSegment(sketch, "E2948", {"start": v(-29.35, -6.96) * mm, "end": v(-29.36, -6.95) * mm});
            skLineSegment(sketch, "E2949", {"start": v(-29.36, -6.95) * mm, "end": v(-29.36, -6.93) * mm});
            skLineSegment(sketch, "E2950", {"start": v(-29.36, -6.93) * mm, "end": v(-29.36, -6.91) * mm});
            skLineSegment(sketch, "E2951", {"start": v(-29.36, -6.91) * mm, "end": v(-29.35, -6.9) * mm});
            skLineSegment(sketch, "E2952", {"start": v(-29.35, -6.9) * mm, "end": v(-29.35, -6.88) * mm});
            skLineSegment(sketch, "E2953", {"start": v(-29.35, -6.88) * mm, "end": v(-29.35, -6.87) * mm});
            skLineSegment(sketch, "E2954", {"start": v(-29.35, -6.87) * mm, "end": v(-29.34, -6.85) * mm});
            skLineSegment(sketch, "E2955", {"start": v(-29.34, -6.85) * mm, "end": v(-29.34, -6.84) * mm});
            skLineSegment(sketch, "E2956", {"start": v(-29.34, -6.84) * mm, "end": v(-29.33, -6.83) * mm});
            skLineSegment(sketch, "E2957", {"start": v(-29.33, -6.83) * mm, "end": v(-29.33, -6.81) * mm});
            skLineSegment(sketch, "E2958", {"start": v(-29.33, -6.81) * mm, "end": v(-29.32, -6.8) * mm});
            skLineSegment(sketch, "E2959", {"start": v(-29.32, -6.8) * mm, "end": v(-29.3, -6.79) * mm});
            skLineSegment(sketch, "E2960", {"start": v(-29.3, -6.79) * mm, "end": v(-29.3, -6.78) * mm});
            skLineSegment(sketch, "E2961", {"start": v(-29.3, -6.78) * mm, "end": v(-29.29, -6.77) * mm});
            skLineSegment(sketch, "E2962", {"start": v(-29.29, -6.77) * mm, "end": v(-29.28, -6.75) * mm});
            skLineSegment(sketch, "E2963", {"start": v(-29.28, -6.75) * mm, "end": v(-29.26, -6.74) * mm});
            skLineSegment(sketch, "E2964", {"start": v(-29.26, -6.74) * mm, "end": v(-29.25, -6.73) * mm});
            skLineSegment(sketch, "E2965", {"start": v(-29.25, -6.73) * mm, "end": v(-29.24, -6.72) * mm});
            skLineSegment(sketch, "E2966", {"start": v(-29.24, -6.72) * mm, "end": v(-29.22, -6.72) * mm});
            skLineSegment(sketch, "E2967", {"start": v(-29.22, -6.72) * mm, "end": v(-29.2, -6.71) * mm});
            skLineSegment(sketch, "E2968", {"start": v(-29.2, -6.71) * mm, "end": v(-29.18, -6.7) * mm});
            skLineSegment(sketch, "E2969", {"start": v(-29.18, -6.7) * mm, "end": v(-29.17, -6.7) * mm});
            skLineSegment(sketch, "E2970", {"start": v(-29.17, -6.7) * mm, "end": v(-29.15, -6.7) * mm});
            skLineSegment(sketch, "E2971", {"start": v(-29.15, -6.7) * mm, "end": v(-29.13, -6.7) * mm});
            skLineSegment(sketch, "E2972", {"start": v(-29.13, -6.7) * mm, "end": v(-23.36, -6.7) * mm});
            skLineSegment(sketch, "E2973", {"start": v(-23.36, -6.7) * mm, "end": v(-22.87, -6.69) * mm});
            skLineSegment(sketch, "E2974", {"start": v(-22.87, -6.69) * mm, "end": v(-22.38, -6.66) * mm});
            skLineSegment(sketch, "E2975", {"start": v(-22.38, -6.66) * mm, "end": v(-21.9, -6.62) * mm});
            skLineSegment(sketch, "E2976", {"start": v(-21.9, -6.62) * mm, "end": v(-21.42, -6.55) * mm});
            skLineSegment(sketch, "E2977", {"start": v(-21.42, -6.55) * mm, "end": v(-20.95, -6.47) * mm});
            skLineSegment(sketch, "E2978", {"start": v(-20.95, -6.47) * mm, "end": v(-20.48, -6.37) * mm});
            skLineSegment(sketch, "E2979", {"start": v(-20.48, -6.37) * mm, "end": v(-20.03, -6.26) * mm});
            skLineSegment(sketch, "E2980", {"start": v(-20.03, -6.26) * mm, "end": v(-19.58, -6.12) * mm});
            skLineSegment(sketch, "E2981", {"start": v(-19.58, -6.12) * mm, "end": v(-19.13, -5.97) * mm});
            skLineSegment(sketch, "E2982", {"start": v(-19.13, -5.97) * mm, "end": v(-18.7, -5.8) * mm});
            skLineSegment(sketch, "E2983", {"start": v(-18.7, -5.8) * mm, "end": v(-18.26, -5.61) * mm});
            skLineSegment(sketch, "E2984", {"start": v(-18.26, -5.61) * mm, "end": v(-17.84, -5.4) * mm});
            skLineSegment(sketch, "E2985", {"start": v(-17.84, -5.4) * mm, "end": v(-17.42, -5.18) * mm});
            skLineSegment(sketch, "E2986", {"start": v(-17.42, -5.18) * mm, "end": v(-17.01, -4.94) * mm});
            skLineSegment(sketch, "E2987", {"start": v(-17.01, -4.94) * mm, "end": v(-16.6, -4.68) * mm});
            skLineSegment(sketch, "E2988", {"start": v(-16.6, -4.68) * mm, "end": v(-16.21, -4.4) * mm});
            skLineSegment(sketch, "E2989", {"start": v(-16.21, -4.4) * mm, "end": v(-15.7, -4) * mm});
            skLineSegment(sketch, "E2990", {"start": v(-15.7, -4) * mm, "end": v(-15.23, -3.59) * mm});
            skLineSegment(sketch, "E2991", {"start": v(-15.23, -3.59) * mm, "end": v(-14.78, -3.14) * mm});
            skLineSegment(sketch, "E2992", {"start": v(-14.78, -3.14) * mm, "end": v(-14.37, -2.68) * mm});
            skLineSegment(sketch, "E2993", {"start": v(-14.37, -2.68) * mm, "end": v(-14, -2.19) * mm});
            skLineSegment(sketch, "E2994", {"start": v(-14, -2.19) * mm, "end": v(-13.65, -1.67) * mm});
            skLineSegment(sketch, "E2995", {"start": v(-13.65, -1.67) * mm, "end": v(-13.33, -1.14) * mm});
            skLineSegment(sketch, "E2996", {"start": v(-13.33, -1.14) * mm, "end": v(-13.05, -0.58) * mm});
            skLineSegment(sketch, "E2997", {"start": v(-13.05, -0.58) * mm, "end": v(-12.8, 0) * mm});
            skLineSegment(sketch, "E2998", {"start": v(-12.8, 0) * mm, "end": v(-12.59, 0.6) * mm});
            skLineSegment(sketch, "E2999", {"start": v(-12.59, 0.6) * mm, "end": v(-12.4, 1.22) * mm});
            skLineSegment(sketch, "E3000", {"start": v(-12.4, 1.22) * mm, "end": v(-12.26, 1.87) * mm});
            skLineSegment(sketch, "E3001", {"start": v(-12.26, 1.87) * mm, "end": v(-12.14, 2.54) * mm});
            skLineSegment(sketch, "E3002", {"start": v(-12.14, 2.54) * mm, "end": v(-12.06, 3.23) * mm});
            skLineSegment(sketch, "E3003", {"start": v(-12.06, 3.23) * mm, "end": v(-12, 3.94) * mm});
            skLineSegment(sketch, "E3004", {"start": v(-12, 3.94) * mm, "end": v(-12, 4.67) * mm});
            skLineSegment(sketch, "E3005", {"start": v(-12, 4.67) * mm, "end": v(-12, 5.4) * mm});
            skLineSegment(sketch, "E3006", {"start": v(-12, 5.4) * mm, "end": v(-12.06, 6.12) * mm});
            skLineSegment(sketch, "E3007", {"start": v(-12.06, 6.12) * mm, "end": v(-12.14, 6.8) * mm});
            skLineSegment(sketch, "E3008", {"start": v(-12.14, 6.8) * mm, "end": v(-12.26, 7.48) * mm});
            skLineSegment(sketch, "E3009", {"start": v(-12.26, 7.48) * mm, "end": v(-12.4, 8.12) * mm});
            skLineSegment(sketch, "E3010", {"start": v(-12.4, 8.12) * mm, "end": v(-12.59, 8.75) * mm});
            skLineSegment(sketch, "E3011", {"start": v(-12.59, 8.75) * mm, "end": v(-12.8, 9.35) * mm});
            skLineSegment(sketch, "E3012", {"start": v(-12.8, 9.35) * mm, "end": v(-13.05, 9.93) * mm});
            skLineSegment(sketch, "E3013", {"start": v(-13.05, 9.93) * mm, "end": v(-13.33, 10.48) * mm});
            skLineSegment(sketch, "E3014", {"start": v(-13.33, 10.48) * mm, "end": v(-13.65, 11.02) * mm});
            skLineSegment(sketch, "E3015", {"start": v(-13.65, 11.02) * mm, "end": v(-14, 11.53) * mm});
            skLineSegment(sketch, "E3016", {"start": v(-14, 11.53) * mm, "end": v(-14.37, 12.02) * mm});
            skLineSegment(sketch, "E3017", {"start": v(-14.37, 12.02) * mm, "end": v(-14.78, 12.49) * mm});
            skLineSegment(sketch, "E3018", {"start": v(-14.78, 12.49) * mm, "end": v(-15.23, 12.93) * mm});
            skLineSegment(sketch, "E3019", {"start": v(-15.23, 12.93) * mm, "end": v(-15.7, 13.35) * mm});
            skLineSegment(sketch, "E3020", {"start": v(-15.7, 13.35) * mm, "end": v(-16.21, 13.75) * mm});
            skLineSegment(sketch, "E3021", {"start": v(-16.21, 13.75) * mm, "end": v(-16.6, 14.03) * mm});
            skLineSegment(sketch, "E3022", {"start": v(-16.6, 14.03) * mm, "end": v(-17.01, 14.29) * mm});
            skLineSegment(sketch, "E3023", {"start": v(-17.01, 14.29) * mm, "end": v(-17.42, 14.53) * mm});
            skLineSegment(sketch, "E3024", {"start": v(-17.42, 14.53) * mm, "end": v(-17.84, 14.75) * mm});
            skLineSegment(sketch, "E3025", {"start": v(-17.84, 14.75) * mm, "end": v(-18.26, 14.96) * mm});
            skLineSegment(sketch, "E3026", {"start": v(-18.26, 14.96) * mm, "end": v(-18.7, 15.15) * mm});
            skLineSegment(sketch, "E3027", {"start": v(-18.7, 15.15) * mm, "end": v(-19.13, 15.32) * mm});
            skLineSegment(sketch, "E3028", {"start": v(-19.13, 15.32) * mm, "end": v(-19.58, 15.47) * mm});
            skLineSegment(sketch, "E3029", {"start": v(-19.58, 15.47) * mm, "end": v(-20.03, 15.6) * mm});
            skLineSegment(sketch, "E3030", {"start": v(-20.03, 15.6) * mm, "end": v(-20.48, 15.72) * mm});
            skLineSegment(sketch, "E3031", {"start": v(-20.48, 15.72) * mm, "end": v(-20.95, 15.82) * mm});
            skLineSegment(sketch, "E3032", {"start": v(-20.95, 15.82) * mm, "end": v(-21.42, 15.9) * mm});
            skLineSegment(sketch, "E3033", {"start": v(-21.42, 15.9) * mm, "end": v(-21.9, 15.96) * mm});
            skLineSegment(sketch, "E3034", {"start": v(-21.9, 15.96) * mm, "end": v(-22.38, 16) * mm});
            skLineSegment(sketch, "E3035", {"start": v(-22.38, 16) * mm, "end": v(-22.87, 16.04) * mm});
            skLineSegment(sketch, "E3036", {"start": v(-22.87, 16.04) * mm, "end": v(-23.36, 16.04) * mm});
            skLineSegment(sketch, "E3037", {"start": v(-23.36, 16.04) * mm, "end": v(-36.97, 16.04) * mm});
            skLineSegment(sketch, "E3038", {"start": v(-36.97, 16.04) * mm, "end": v(-37.25, 16.03) * mm});
            skLineSegment(sketch, "E3039", {"start": v(-37.25, 16.03) * mm, "end": v(-37.52, 15.99) * mm});
            skLineSegment(sketch, "E3040", {"start": v(-37.52, 15.99) * mm, "end": v(-37.78, 15.92) * mm});
            skLineSegment(sketch, "E3041", {"start": v(-37.78, 15.92) * mm, "end": v(-38.03, 15.83) * mm});
            skLineSegment(sketch, "E3042", {"start": v(-38.03, 15.83) * mm, "end": v(-38.27, 15.71) * mm});
            skLineSegment(sketch, "E3043", {"start": v(-38.27, 15.71) * mm, "end": v(-38.5, 15.58) * mm});
            skLineSegment(sketch, "E3044", {"start": v(-38.5, 15.58) * mm, "end": v(-38.7, 15.42) * mm});
            skLineSegment(sketch, "E3045", {"start": v(-38.7, 15.42) * mm, "end": v(-38.9, 15.24) * mm});
            skLineSegment(sketch, "E3046", {"start": v(-38.9, 15.24) * mm, "end": v(-39.08, 15.05) * mm});
            skLineSegment(sketch, "E3047", {"start": v(-39.08, 15.05) * mm, "end": v(-39.24, 14.84) * mm});
            skLineSegment(sketch, "E3048", {"start": v(-39.24, 14.84) * mm, "end": v(-39.38, 14.6) * mm});
            skLineSegment(sketch, "E3049", {"start": v(-39.38, 14.6) * mm, "end": v(-39.5, 14.37) * mm});
            skLineSegment(sketch, "E3050", {"start": v(-39.5, 14.37) * mm, "end": v(-39.58, 14.12) * mm});
            skLineSegment(sketch, "E3051", {"start": v(-39.58, 14.12) * mm, "end": v(-39.65, 13.86) * mm});
            skLineSegment(sketch, "E3052", {"start": v(-39.65, 13.86) * mm, "end": v(-39.7, 13.58) * mm});
            skLineSegment(sketch, "E3053", {"start": v(-39.7, 13.58) * mm, "end": v(-39.7, 13.3) * mm});
            skLineSegment(sketch, "E3054", {"start": v(-39.7, 13.3) * mm, "end": v(-39.7, -22.53) * mm});
            skLineSegment(sketch, "E3055", {"start": v(-39.7, -22.53) * mm, "end": v(-39.71, -22.64) * mm});
            skLineSegment(sketch, "E3056", {"start": v(-39.71, -22.64) * mm, "end": v(-39.72, -22.74) * mm});
            skLineSegment(sketch, "E3057", {"start": v(-39.72, -22.74) * mm, "end": v(-39.74, -22.84) * mm});
            skLineSegment(sketch, "E3058", {"start": v(-39.74, -22.84) * mm, "end": v(-39.77, -22.93) * mm});
            skLineSegment(sketch, "E3059", {"start": v(-39.77, -22.93) * mm, "end": v(-39.8, -23.01) * mm});
            skLineSegment(sketch, "E3060", {"start": v(-39.8, -23.01) * mm, "end": v(-39.85, -23.09) * mm});
            skLineSegment(sketch, "E3061", {"start": v(-39.85, -23.09) * mm, "end": v(-39.9, -23.16) * mm});
            skLineSegment(sketch, "E3062", {"start": v(-39.9, -23.16) * mm, "end": v(-39.96, -23.22) * mm});
            skLineSegment(sketch, "E3063", {"start": v(-39.96, -23.22) * mm, "end": v(-40.03, -23.28) * mm});
            skLineSegment(sketch, "E3064", {"start": v(-40.03, -23.28) * mm, "end": v(-40.1, -23.33) * mm});
            skLineSegment(sketch, "E3065", {"start": v(-40.1, -23.33) * mm, "end": v(-40.18, -23.37) * mm});
            skLineSegment(sketch, "E3066", {"start": v(-40.18, -23.37) * mm, "end": v(-40.27, -23.4) * mm});
            skLineSegment(sketch, "E3067", {"start": v(-40.27, -23.4) * mm, "end": v(-40.37, -23.44) * mm});
            skLineSegment(sketch, "E3068", {"start": v(-40.37, -23.44) * mm, "end": v(-40.48, -23.46) * mm});
            skLineSegment(sketch, "E3069", {"start": v(-40.48, -23.46) * mm, "end": v(-40.6, -23.47) * mm});
            skLineSegment(sketch, "E3070", {"start": v(-40.6, -23.47) * mm, "end": v(-40.72, -23.48) * mm});
            skLineSegment(sketch, "E3071", {"start": v(-40.72, -23.48) * mm, "end": v(-43.52, -23.48) * mm});
            skLineSegment(sketch, "E3072", {"start": v(-43.52, -23.48) * mm, "end": v(-43.62, -23.48) * mm});
            skLineSegment(sketch, "E3073", {"start": v(-43.62, -23.48) * mm, "end": v(-43.72, -23.46) * mm});
            skLineSegment(sketch, "E3074", {"start": v(-43.72, -23.46) * mm, "end": v(-43.82, -23.44) * mm});
            skLineSegment(sketch, "E3075", {"start": v(-43.82, -23.44) * mm, "end": v(-43.91, -23.4) * mm});
            skLineSegment(sketch, "E3076", {"start": v(-43.91, -23.4) * mm, "end": v(-44, -23.36) * mm});
            skLineSegment(sketch, "E3077", {"start": v(-44, -23.36) * mm, "end": v(-44.09, -23.31) * mm});
            skLineSegment(sketch, "E3078", {"start": v(-44.09, -23.31) * mm, "end": v(-44.16, -23.25) * mm});
            skLineSegment(sketch, "E3079", {"start": v(-44.16, -23.25) * mm, "end": v(-44.24, -23.19) * mm});
            skLineSegment(sketch, "E3080", {"start": v(-44.24, -23.19) * mm, "end": v(-44.3, -23.11) * mm});
            skLineSegment(sketch, "E3081", {"start": v(-44.3, -23.11) * mm, "end": v(-44.36, -23.04) * mm});
            skLineSegment(sketch, "E3082", {"start": v(-44.36, -23.04) * mm, "end": v(-44.41, -22.95) * mm});
            skLineSegment(sketch, "E3083", {"start": v(-44.41, -22.95) * mm, "end": v(-44.45, -22.86) * mm});
            skLineSegment(sketch, "E3084", {"start": v(-44.45, -22.86) * mm, "end": v(-44.49, -22.77) * mm});
            skLineSegment(sketch, "E3085", {"start": v(-44.49, -22.77) * mm, "end": v(-44.51, -22.67) * mm});
            skLineSegment(sketch, "E3086", {"start": v(-44.51, -22.67) * mm, "end": v(-44.53, -22.57) * mm});
            skLineSegment(sketch, "E3087", {"start": v(-44.53, -22.57) * mm, "end": v(-44.53, -22.47) * mm});
            skLineSegment(sketch, "E3088", {"start": v(-44.53, -22.47) * mm, "end": v(-44.53, 12.07) * mm});
            skLineSegment(sketch, "E3089", {"start": v(-44.53, 12.07) * mm, "end": v(-44.54, 12.3) * mm});
            skLineSegment(sketch, "E3090", {"start": v(-44.54, 12.3) * mm, "end": v(-44.55, 12.5) * mm});
            skLineSegment(sketch, "E3091", {"start": v(-44.55, 12.5) * mm, "end": v(-44.57, 12.72) * mm});
            skLineSegment(sketch, "E3092", {"start": v(-44.57, 12.72) * mm, "end": v(-44.6, 12.92) * mm});
            skLineSegment(sketch, "E3093", {"start": v(-44.6, 12.92) * mm, "end": v(-44.64, 13.12) * mm});
            skLineSegment(sketch, "E3094", {"start": v(-44.64, 13.12) * mm, "end": v(-44.69, 13.31) * mm});
            skLineSegment(sketch, "E3095", {"start": v(-44.69, 13.31) * mm, "end": v(-44.74, 13.5) * mm});
            skLineSegment(sketch, "E3096", {"start": v(-44.74, 13.5) * mm, "end": v(-44.8, 13.69) * mm});
            skLineSegment(sketch, "E3097", {"start": v(-44.8, 13.69) * mm, "end": v(-44.88, 13.86) * mm});
            skLineSegment(sketch, "E3098", {"start": v(-44.88, 13.86) * mm, "end": v(-44.96, 14.04) * mm});
            skLineSegment(sketch, "E3099", {"start": v(-44.96, 14.04) * mm, "end": v(-45.05, 14.2) * mm});
            skLineSegment(sketch, "E3100", {"start": v(-45.05, 14.2) * mm, "end": v(-45.14, 14.36) * mm});
            skLineSegment(sketch, "E3101", {"start": v(-45.14, 14.36) * mm, "end": v(-45.25, 14.52) * mm});
            skLineSegment(sketch, "E3102", {"start": v(-45.25, 14.52) * mm, "end": v(-45.36, 14.67) * mm});
            skLineSegment(sketch, "E3103", {"start": v(-45.36, 14.67) * mm, "end": v(-45.48, 14.81) * mm});
            skLineSegment(sketch, "E3104", {"start": v(-45.48, 14.81) * mm, "end": v(-45.61, 14.95) * mm});
            skLineSegment(sketch, "E3105", {"start": v(-45.61, 14.95) * mm, "end": v(-45.75, 15.08) * mm});
            skLineSegment(sketch, "E3106", {"start": v(-45.75, 15.08) * mm, "end": v(-45.9, 15.2) * mm});
            skLineSegment(sketch, "E3107", {"start": v(-45.9, 15.2) * mm, "end": v(-46.04, 15.32) * mm});
            skLineSegment(sketch, "E3108", {"start": v(-46.04, 15.32) * mm, "end": v(-46.2, 15.43) * mm});
            skLineSegment(sketch, "E3109", {"start": v(-46.2, 15.43) * mm, "end": v(-46.36, 15.53) * mm});
            skLineSegment(sketch, "E3110", {"start": v(-46.36, 15.53) * mm, "end": v(-46.52, 15.62) * mm});
            skLineSegment(sketch, "E3111", {"start": v(-46.52, 15.62) * mm, "end": v(-46.7, 15.7) * mm});
            skLineSegment(sketch, "E3112", {"start": v(-46.7, 15.7) * mm, "end": v(-46.87, 15.77) * mm});
            skLineSegment(sketch, "E3113", {"start": v(-46.87, 15.77) * mm, "end": v(-47.05, 15.83) * mm});
            skLineSegment(sketch, "E3114", {"start": v(-47.05, 15.83) * mm, "end": v(-47.24, 15.9) * mm});
            skLineSegment(sketch, "E3115", {"start": v(-47.24, 15.9) * mm, "end": v(-47.43, 15.94) * mm});
            skLineSegment(sketch, "E3116", {"start": v(-47.43, 15.94) * mm, "end": v(-47.63, 15.98) * mm});
            skLineSegment(sketch, "E3117", {"start": v(-47.63, 15.98) * mm, "end": v(-47.83, 16) * mm});
            skLineSegment(sketch, "E3118", {"start": v(-47.83, 16) * mm, "end": v(-48.04, 16.03) * mm});
            skLineSegment(sketch, "E3119", {"start": v(-48.04, 16.03) * mm, "end": v(-48.25, 16.04) * mm});
            skLineSegment(sketch, "E3120", {"start": v(-48.25, 16.04) * mm, "end": v(-48.47, 16.04) * mm});
            skLineSegment(sketch, "E3121", {"start": v(-48.47, 16.04) * mm, "end": v(-48.68, 16.04) * mm});
            skLineSegment(sketch, "E3122", {"start": v(-48.68, 16.04) * mm, "end": v(-48.9, 16.03) * mm});
            skLineSegment(sketch, "E3123", {"start": v(-48.9, 16.03) * mm, "end": v(-49.1, 16) * mm});
            skLineSegment(sketch, "E3124", {"start": v(-49.1, 16) * mm, "end": v(-49.3, 15.97) * mm});
            skLineSegment(sketch, "E3125", {"start": v(-49.3, 15.97) * mm, "end": v(-49.49, 15.93) * mm});
            skLineSegment(sketch, "E3126", {"start": v(-49.49, 15.93) * mm, "end": v(-49.68, 15.89) * mm});
            skLineSegment(sketch, "E3127", {"start": v(-49.68, 15.89) * mm, "end": v(-49.86, 15.83) * mm});
            skLineSegment(sketch, "E3128", {"start": v(-49.86, 15.83) * mm, "end": v(-50.04, 15.76) * mm});
            skLineSegment(sketch, "E3129", {"start": v(-50.04, 15.76) * mm, "end": v(-50.21, 15.69) * mm});
            skLineSegment(sketch, "E3130", {"start": v(-50.21, 15.69) * mm, "end": v(-50.38, 15.6) * mm});
            skLineSegment(sketch, "E3131", {"start": v(-50.38, 15.6) * mm, "end": v(-50.55, 15.51) * mm});
            skLineSegment(sketch, "E3132", {"start": v(-50.55, 15.51) * mm, "end": v(-50.7, 15.41) * mm});
            skLineSegment(sketch, "E3133", {"start": v(-50.7, 15.41) * mm, "end": v(-50.87, 15.3) * mm});
            skLineSegment(sketch, "E3134", {"start": v(-50.87, 15.3) * mm, "end": v(-51.02, 15.19) * mm});
            skLineSegment(sketch, "E3135", {"start": v(-51.02, 15.19) * mm, "end": v(-51.16, 15.06) * mm});
            skLineSegment(sketch, "E3136", {"start": v(-51.16, 15.06) * mm, "end": v(-51.3, 14.93) * mm});
            skLineSegment(sketch, "E3137", {"start": v(-51.3, 14.93) * mm, "end": v(-51.43, 14.79) * mm});
            skLineSegment(sketch, "E3138", {"start": v(-51.43, 14.79) * mm, "end": v(-51.56, 14.64) * mm});
            skLineSegment(sketch, "E3139", {"start": v(-51.56, 14.64) * mm, "end": v(-51.68, 14.49) * mm});
            skLineSegment(sketch, "E3140", {"start": v(-51.68, 14.49) * mm, "end": v(-51.78, 14.33) * mm});
            skLineSegment(sketch, "E3141", {"start": v(-51.78, 14.33) * mm, "end": v(-51.88, 14.17) * mm});
            skLineSegment(sketch, "E3142", {"start": v(-51.88, 14.17) * mm, "end": v(-51.97, 14) * mm});
            skLineSegment(sketch, "E3143", {"start": v(-51.97, 14) * mm, "end": v(-52.06, 13.83) * mm});
            skLineSegment(sketch, "E3144", {"start": v(-52.06, 13.83) * mm, "end": v(-52.13, 13.65) * mm});
            skLineSegment(sketch, "E3145", {"start": v(-52.13, 13.65) * mm, "end": v(-52.2, 13.47) * mm});
            skLineSegment(sketch, "E3146", {"start": v(-52.2, 13.47) * mm, "end": v(-52.25, 13.29) * mm});
            skLineSegment(sketch, "E3147", {"start": v(-52.25, 13.29) * mm, "end": v(-52.3, 13.1) * mm});
            skLineSegment(sketch, "E3148", {"start": v(-52.3, 13.1) * mm, "end": v(-52.34, 12.9) * mm});
            skLineSegment(sketch, "E3149", {"start": v(-52.34, 12.9) * mm, "end": v(-52.37, 12.7) * mm});
            skLineSegment(sketch, "E3150", {"start": v(-52.37, 12.7) * mm, "end": v(-52.39, 12.5) * mm});
            skLineSegment(sketch, "E3151", {"start": v(-52.39, 12.5) * mm, "end": v(-52.4, 12.28) * mm});
            skLineSegment(sketch, "E3152", {"start": v(-52.4, 12.28) * mm, "end": v(-52.4, 12.07) * mm});
            skLineSegment(sketch, "E3153", {"start": v(-52.4, 12.07) * mm, "end": v(-52.4, -17.98) * mm});
            skLineSegment(sketch, "E3154", {"start": v(-52.4, -17.98) * mm, "end": v(-52.4, -18) * mm});
            skLineSegment(sketch, "E3155", {"start": v(-52.4, -18) * mm, "end": v(-52.41, -18.02) * mm});
            skLineSegment(sketch, "E3156", {"start": v(-52.41, -18.02) * mm, "end": v(-52.42, -18.03) * mm});
            skLineSegment(sketch, "E3157", {"start": v(-52.42, -18.03) * mm, "end": v(-52.42, -18.05) * mm});
            skLineSegment(sketch, "E3158", {"start": v(-52.42, -18.05) * mm, "end": v(-52.43, -18.06) * mm});
            skLineSegment(sketch, "E3159", {"start": v(-52.43, -18.06) * mm, "end": v(-52.44, -18.08) * mm});
            skLineSegment(sketch, "E3160", {"start": v(-52.44, -18.08) * mm, "end": v(-52.45, -18.09) * mm});
            skLineSegment(sketch, "E3161", {"start": v(-52.45, -18.09) * mm, "end": v(-52.46, -18.1) * mm});
            skLineSegment(sketch, "E3162", {"start": v(-52.46, -18.1) * mm, "end": v(-52.47, -18.11) * mm});
            skLineSegment(sketch, "E3163", {"start": v(-52.47, -18.11) * mm, "end": v(-52.48, -18.12) * mm});
            skLineSegment(sketch, "E3164", {"start": v(-52.48, -18.12) * mm, "end": v(-52.5, -18.13) * mm});
            skLineSegment(sketch, "E3165", {"start": v(-52.5, -18.13) * mm, "end": v(-52.51, -18.13) * mm});
            skLineSegment(sketch, "E3166", {"start": v(-52.51, -18.13) * mm, "end": v(-52.53, -18.14) * mm});
            skLineSegment(sketch, "E3167", {"start": v(-52.53, -18.14) * mm, "end": v(-52.54, -18.14) * mm});
            skLineSegment(sketch, "E3168", {"start": v(-52.54, -18.14) * mm, "end": v(-52.56, -18.14) * mm});
            skLineSegment(sketch, "E3169", {"start": v(-52.56, -18.14) * mm, "end": v(-52.57, -18.14) * mm});
            skLineSegment(sketch, "E3170", {"start": v(-52.57, -18.14) * mm, "end": v(-52.58, -18.14) * mm});
            skLineSegment(sketch, "E3171", {"start": v(-52.58, -18.14) * mm, "end": v(-52.59, -18.14) * mm});
            skLineSegment(sketch, "E3172", {"start": v(-52.59, -18.14) * mm, "end": v(-52.6, -18.14) * mm});
            skLineSegment(sketch, "E3173", {"start": v(-52.6, -18.14) * mm, "end": v(-52.6, -18.14) * mm});
            skLineSegment(sketch, "E3174", {"start": v(-52.6, -18.14) * mm, "end": v(-52.61, -18.14) * mm});
            skLineSegment(sketch, "E3175", {"start": v(-52.61, -18.14) * mm, "end": v(-52.62, -18.13) * mm});
            skLineSegment(sketch, "E3176", {"start": v(-52.62, -18.13) * mm, "end": v(-52.63, -18.13) * mm});
            skLineSegment(sketch, "E3177", {"start": v(-52.63, -18.13) * mm, "end": v(-52.64, -18.13) * mm});
            skLineSegment(sketch, "E3178", {"start": v(-52.64, -18.13) * mm, "end": v(-52.65, -18.12) * mm});
            skLineSegment(sketch, "E3179", {"start": v(-52.65, -18.12) * mm, "end": v(-52.66, -18.12) * mm});
            skLineSegment(sketch, "E3180", {"start": v(-52.66, -18.12) * mm, "end": v(-52.67, -18.1) * mm});
            skLineSegment(sketch, "E3181", {"start": v(-52.67, -18.1) * mm, "end": v(-52.68, -18.1) * mm});
            skLineSegment(sketch, "E3182", {"start": v(-52.68, -18.1) * mm, "end": v(-52.69, -18.09) * mm});
            skLineSegment(sketch, "E3183", {"start": v(-52.69, -18.09) * mm, "end": v(-52.7, -18.08) * mm});
            skLineSegment(sketch, "E3184", {"start": v(-52.7, -18.08) * mm, "end": v(-52.7, -18.07) * mm});
            skLineSegment(sketch, "E3185", {"start": v(-52.7, -18.07) * mm, "end": v(-52.71, -18.05) * mm});
            skLineSegment(sketch, "E3186", {"start": v(-52.71, -18.05) * mm, "end": v(-69.4, 15.25) * mm});
            skLineSegment(sketch, "E3187", {"start": v(-69.4, 15.25) * mm, "end": v(-69.46, 15.34) * mm});
            skLineSegment(sketch, "E3188", {"start": v(-69.46, 15.34) * mm, "end": v(-69.51, 15.42) * mm});
            skLineSegment(sketch, "E3189", {"start": v(-69.51, 15.42) * mm, "end": v(-69.57, 15.5) * mm});
            skLineSegment(sketch, "E3190", {"start": v(-69.57, 15.5) * mm, "end": v(-69.64, 15.58) * mm});
            skLineSegment(sketch, "E3191", {"start": v(-69.64, 15.58) * mm, "end": v(-69.7, 15.65) * mm});
            skLineSegment(sketch, "E3192", {"start": v(-69.7, 15.65) * mm, "end": v(-69.78, 15.72) * mm});
            skLineSegment(sketch, "E3193", {"start": v(-69.78, 15.72) * mm, "end": v(-69.86, 15.78) * mm});
            skLineSegment(sketch, "E3194", {"start": v(-69.86, 15.78) * mm, "end": v(-69.94, 15.83) * mm});
            skLineSegment(sketch, "E3195", {"start": v(-69.94, 15.83) * mm, "end": v(-70.03, 15.88) * mm});
            skLineSegment(sketch, "E3196", {"start": v(-70.03, 15.88) * mm, "end": v(-70.11, 15.92) * mm});
            skLineSegment(sketch, "E3197", {"start": v(-70.11, 15.92) * mm, "end": v(-70.2, 15.96) * mm});
            skLineSegment(sketch, "E3198", {"start": v(-70.2, 15.96) * mm, "end": v(-70.3, 15.99) * mm});
            skLineSegment(sketch, "E3199", {"start": v(-70.3, 15.99) * mm, "end": v(-70.4, 16.01) * mm});
            skLineSegment(sketch, "E3200", {"start": v(-70.4, 16.01) * mm, "end": v(-70.5, 16.03) * mm});
            skLineSegment(sketch, "E3201", {"start": v(-70.5, 16.03) * mm, "end": v(-70.6, 16.04) * mm});
            skLineSegment(sketch, "E3202", {"start": v(-70.6, 16.04) * mm, "end": v(-70.7, 16.04) * mm});
            skLineSegment(sketch, "E3203", {"start": v(-70.7, 16.04) * mm, "end": v(-70.85, 16.04) * mm});
            skLineSegment(sketch, "E3204", {"start": v(-70.85, 16.04) * mm, "end": v(-71, 16.02) * mm});
            skLineSegment(sketch, "E3205", {"start": v(-71, 16.02) * mm, "end": v(-71.13, 15.98) * mm});
            skLineSegment(sketch, "E3206", {"start": v(-71.13, 15.98) * mm, "end": v(-71.26, 15.93) * mm});
            skLineSegment(sketch, "E3207", {"start": v(-71.26, 15.93) * mm, "end": v(-71.39, 15.87) * mm});
            skLineSegment(sketch, "E3208", {"start": v(-71.39, 15.87) * mm, "end": v(-71.5, 15.8) * mm});
            skLineSegment(sketch, "E3209", {"start": v(-71.5, 15.8) * mm, "end": v(-71.62, 15.71) * mm});
            skLineSegment(sketch, "E3210", {"start": v(-71.62, 15.71) * mm, "end": v(-71.72, 15.62) * mm});
            skLineSegment(sketch, "E3211", {"start": v(-71.72, 15.62) * mm, "end": v(-71.81, 15.52) * mm});
            skLineSegment(sketch, "E3212", {"start": v(-71.81, 15.52) * mm, "end": v(-71.9, 15.4) * mm});
            skLineSegment(sketch, "E3213", {"start": v(-71.9, 15.4) * mm, "end": v(-71.97, 15.29) * mm});
            skLineSegment(sketch, "E3214", {"start": v(-71.97, 15.29) * mm, "end": v(-72.03, 15.16) * mm});
            skLineSegment(sketch, "E3215", {"start": v(-72.03, 15.16) * mm, "end": v(-72.08, 15.03) * mm});
            skLineSegment(sketch, "E3216", {"start": v(-72.08, 15.03) * mm, "end": v(-72.12, 14.9) * mm});
            skLineSegment(sketch, "E3217", {"start": v(-72.12, 14.9) * mm, "end": v(-72.14, 14.75) * mm});
            skLineSegment(sketch, "E3218", {"start": v(-72.14, 14.75) * mm, "end": v(-72.15, 14.6) * mm});
            skLineSegment(sketch, "E3219", {"start": v(-72.15, 14.6) * mm, "end": v(-72.15, -22.83) * mm});
            skLineSegment(sketch, "E3220", {"start": v(-72.15, -22.83) * mm, "end": v(-72.15, -22.9) * mm});
            skLineSegment(sketch, "E3221", {"start": v(-72.15, -22.9) * mm, "end": v(-72.16, -22.96) * mm});
            skLineSegment(sketch, "E3222", {"start": v(-72.16, -22.96) * mm, "end": v(-72.17, -23.02) * mm});
            skLineSegment(sketch, "E3223", {"start": v(-72.17, -23.02) * mm, "end": v(-72.2, -23.08) * mm});
            skLineSegment(sketch, "E3224", {"start": v(-72.2, -23.08) * mm, "end": v(-72.22, -23.14) * mm});
            skLineSegment(sketch, "E3225", {"start": v(-72.22, -23.14) * mm, "end": v(-72.26, -23.2) * mm});
            skLineSegment(sketch, "E3226", {"start": v(-72.26, -23.2) * mm, "end": v(-72.3, -23.25) * mm});
            skLineSegment(sketch, "E3227", {"start": v(-72.3, -23.25) * mm, "end": v(-72.34, -23.3) * mm});
            skLineSegment(sketch, "E3228", {"start": v(-72.34, -23.3) * mm, "end": v(-72.38, -23.33) * mm});
            skLineSegment(sketch, "E3229", {"start": v(-72.38, -23.33) * mm, "end": v(-72.43, -23.37) * mm});
            skLineSegment(sketch, "E3230", {"start": v(-72.43, -23.37) * mm, "end": v(-72.49, -23.4) * mm});
            skLineSegment(sketch, "E3231", {"start": v(-72.49, -23.4) * mm, "end": v(-72.55, -23.43) * mm});
            skLineSegment(sketch, "E3232", {"start": v(-72.55, -23.43) * mm, "end": v(-72.6, -23.45) * mm});
            skLineSegment(sketch, "E3233", {"start": v(-72.6, -23.45) * mm, "end": v(-72.67, -23.47) * mm});
            skLineSegment(sketch, "E3234", {"start": v(-72.67, -23.47) * mm, "end": v(-72.73, -23.48) * mm});
            skLineSegment(sketch, "E3235", {"start": v(-72.73, -23.48) * mm, "end": v(-72.8, -23.48) * mm});
            skLineSegment(sketch, "E3236", {"start": v(-72.8, -23.48) * mm, "end": v(-91.32, -23.48) * mm});
            skLineSegment(sketch, "E3237", {"start": v(-91.32, -23.48) * mm, "end": v(-91.38, -23.48) * mm});
            skLineSegment(sketch, "E3238", {"start": v(-91.38, -23.48) * mm, "end": v(-91.44, -23.47) * mm});
            skLineSegment(sketch, "E3239", {"start": v(-91.44, -23.47) * mm, "end": v(-91.5, -23.46) * mm});
            skLineSegment(sketch, "E3240", {"start": v(-91.5, -23.46) * mm, "end": v(-91.55, -23.44) * mm});
            skLineSegment(sketch, "E3241", {"start": v(-91.55, -23.44) * mm, "end": v(-91.6, -23.42) * mm});
            skLineSegment(sketch, "E3242", {"start": v(-91.6, -23.42) * mm, "end": v(-91.64, -23.39) * mm});
            skLineSegment(sketch, "E3243", {"start": v(-91.64, -23.39) * mm, "end": v(-91.69, -23.35) * mm});
            skLineSegment(sketch, "E3244", {"start": v(-91.69, -23.35) * mm, "end": v(-91.73, -23.32) * mm});
            skLineSegment(sketch, "E3245", {"start": v(-91.73, -23.32) * mm, "end": v(-91.76, -23.28) * mm});
            skLineSegment(sketch, "E3246", {"start": v(-91.76, -23.28) * mm, "end": v(-91.8, -23.23) * mm});
            skLineSegment(sketch, "E3247", {"start": v(-91.8, -23.23) * mm, "end": v(-91.83, -23.18) * mm});
            skLineSegment(sketch, "E3248", {"start": v(-91.83, -23.18) * mm, "end": v(-91.85, -23.13) * mm});
            skLineSegment(sketch, "E3249", {"start": v(-91.85, -23.13) * mm, "end": v(-91.87, -23.08) * mm});
            skLineSegment(sketch, "E3250", {"start": v(-91.87, -23.08) * mm, "end": v(-91.88, -23.03) * mm});
            skLineSegment(sketch, "E3251", {"start": v(-91.88, -23.03) * mm, "end": v(-91.9, -22.97) * mm});
            skLineSegment(sketch, "E3252", {"start": v(-91.9, -22.97) * mm, "end": v(-91.9, -22.91) * mm});
            skLineSegment(sketch, "E3253", {"start": v(-91.9, -22.91) * mm, "end": v(-91.9, -21.25) * mm});
            skLineSegment(sketch, "E3254", {"start": v(-91.9, -21.25) * mm, "end": v(-91.9, -21.23) * mm});
            skLineSegment(sketch, "E3255", {"start": v(-91.9, -21.23) * mm, "end": v(-91.9, -21.21) * mm});
            skLineSegment(sketch, "E3256", {"start": v(-91.9, -21.21) * mm, "end": v(-91.89, -21.2) * mm});
            skLineSegment(sketch, "E3257", {"start": v(-91.89, -21.2) * mm, "end": v(-91.88, -21.18) * mm});
            skLineSegment(sketch, "E3258", {"start": v(-91.88, -21.18) * mm, "end": v(-91.87, -21.16) * mm});
            skLineSegment(sketch, "E3259", {"start": v(-91.87, -21.16) * mm, "end": v(-91.87, -21.14) * mm});
            skLineSegment(sketch, "E3260", {"start": v(-91.87, -21.14) * mm, "end": v(-91.86, -21.13) * mm});
            skLineSegment(sketch, "E3261", {"start": v(-91.86, -21.13) * mm, "end": v(-91.84, -21.11) * mm});
            skLineSegment(sketch, "E3262", {"start": v(-91.84, -21.11) * mm, "end": v(-91.83, -21.1) * mm});
            skLineSegment(sketch, "E3263", {"start": v(-91.83, -21.1) * mm, "end": v(-91.82, -21.09) * mm});
            skLineSegment(sketch, "E3264", {"start": v(-91.82, -21.09) * mm, "end": v(-91.8, -21.07) * mm});
            skLineSegment(sketch, "E3265", {"start": v(-91.8, -21.07) * mm, "end": v(-91.79, -21.06) * mm});
            skLineSegment(sketch, "E3266", {"start": v(-91.79, -21.06) * mm, "end": v(-91.77, -21.05) * mm});
            skLineSegment(sketch, "E3267", {"start": v(-91.77, -21.05) * mm, "end": v(-91.75, -21.04) * mm});
            skLineSegment(sketch, "E3268", {"start": v(-91.75, -21.04) * mm, "end": v(-91.73, -21.04) * mm});
            skLineSegment(sketch, "E3269", {"start": v(-91.73, -21.04) * mm, "end": v(-91.72, -21.03) * mm});
            skLineSegment(sketch, "E3270", {"start": v(-91.72, -21.03) * mm, "end": v(-90.93, -20.84) * mm});
            skLineSegment(sketch, "E3271", {"start": v(-90.93, -20.84) * mm, "end": v(-90.16, -20.62) * mm});
            skLineSegment(sketch, "E3272", {"start": v(-90.16, -20.62) * mm, "end": v(-89.41, -20.37) * mm});
            skLineSegment(sketch, "E3273", {"start": v(-89.41, -20.37) * mm, "end": v(-88.68, -20.09) * mm});
            skLineSegment(sketch, "E3274", {"start": v(-88.68, -20.09) * mm, "end": v(-87.96, -19.78) * mm});
            skLineSegment(sketch, "E3275", {"start": v(-87.96, -19.78) * mm, "end": v(-87.26, -19.44) * mm});
            skLineSegment(sketch, "E3276", {"start": v(-87.26, -19.44) * mm, "end": v(-86.57, -19.07) * mm});
            skLineSegment(sketch, "E3277", {"start": v(-86.57, -19.07) * mm, "end": v(-85.9, -18.68) * mm});
            skLineSegment(sketch, "E3278", {"start": v(-85.9, -18.68) * mm, "end": v(-85.25, -18.25) * mm});
            skLineSegment(sketch, "E3279", {"start": v(-85.25, -18.25) * mm, "end": v(-84.62, -17.8) * mm});
            skLineSegment(sketch, "E3280", {"start": v(-84.62, -17.8) * mm, "end": v(-84, -17.32) * mm});
            skLineSegment(sketch, "E3281", {"start": v(-84, -17.32) * mm, "end": v(-83.4, -16.81) * mm});
            skLineSegment(sketch, "E3282", {"start": v(-83.4, -16.81) * mm, "end": v(-82.83, -16.27) * mm});
            skLineSegment(sketch, "E3283", {"start": v(-82.83, -16.27) * mm, "end": v(-82.27, -15.7) * mm});
            skLineSegment(sketch, "E3284", {"start": v(-82.27, -15.7) * mm, "end": v(-81.73, -15.11) * mm});
            skLineSegment(sketch, "E3285", {"start": v(-81.73, -15.11) * mm, "end": v(-81.2, -14.5) * mm});
            skLineSegment(sketch, "E3286", {"start": v(-81.2, -14.5) * mm, "end": v(-80.7, -13.84) * mm});
            skLineSegment(sketch, "E3287", {"start": v(-80.7, -13.84) * mm, "end": v(-80.21, -13.17) * mm});
            skLineSegment(sketch, "E3288", {"start": v(-80.21, -13.17) * mm, "end": v(-79.77, -12.5) * mm});
            skLineSegment(sketch, "E3289", {"start": v(-79.77, -12.5) * mm, "end": v(-79.36, -11.8) * mm});
            skLineSegment(sketch, "E3290", {"start": v(-79.36, -11.8) * mm, "end": v(-78.98, -11.1) * mm});
            skLineSegment(sketch, "E3291", {"start": v(-78.98, -11.1) * mm, "end": v(-78.63, -10.38) * mm});
            skLineSegment(sketch, "E3292", {"start": v(-78.63, -10.38) * mm, "end": v(-78.32, -9.66) * mm});
            skLineSegment(sketch, "E3293", {"start": v(-78.32, -9.66) * mm, "end": v(-78.03, -8.92) * mm});
            skLineSegment(sketch, "E3294", {"start": v(-78.03, -8.92) * mm, "end": v(-77.79, -8.17) * mm});
            skLineSegment(sketch, "E3295", {"start": v(-77.79, -8.17) * mm, "end": v(-77.57, -7.41) * mm});
            skLineSegment(sketch, "E3296", {"start": v(-77.57, -7.41) * mm, "end": v(-77.39, -6.64) * mm});
            skLineSegment(sketch, "E3297", {"start": v(-77.39, -6.64) * mm, "end": v(-77.24, -5.86) * mm});
            skLineSegment(sketch, "E3298", {"start": v(-77.24, -5.86) * mm, "end": v(-77.12, -5.07) * mm});
            skLineSegment(sketch, "E3299", {"start": v(-77.12, -5.07) * mm, "end": v(-77.04, -4.26) * mm});
            skLineSegment(sketch, "E3300", {"start": v(-77.04, -4.26) * mm, "end": v(-76.99, -3.45) * mm});
            skLineSegment(sketch, "E3301", {"start": v(-76.99, -3.45) * mm, "end": v(-76.97, -2.63) * mm});
            skLineSegment(sketch, "E3302", {"start": v(-76.97, -2.63) * mm, "end": v(-77, -1.65) * mm});
            skLineSegment(sketch, "E3303", {"start": v(-77, -1.65) * mm, "end": v(-77.06, -0.7) * mm});
            skLineSegment(sketch, "E3304", {"start": v(-77.06, -0.7) * mm, "end": v(-77.17, 0.25) * mm});
            skLineSegment(sketch, "E3305", {"start": v(-77.17, 0.25) * mm, "end": v(-77.32, 1.17) * mm});
            skLineSegment(sketch, "E3306", {"start": v(-77.32, 1.17) * mm, "end": v(-77.51, 2.08) * mm});
            skLineSegment(sketch, "E3307", {"start": v(-77.51, 2.08) * mm, "end": v(-77.75, 2.97) * mm});
            skLineSegment(sketch, "E3308", {"start": v(-77.75, 2.97) * mm, "end": v(-78.03, 3.84) * mm});
            skLineSegment(sketch, "E3309", {"start": v(-78.03, 3.84) * mm, "end": v(-78.35, 4.69) * mm});
            skLineSegment(sketch, "E3310", {"start": v(-78.35, 4.69) * mm, "end": v(-78.72, 5.52) * mm});
            skLineSegment(sketch, "E3311", {"start": v(-78.72, 5.52) * mm, "end": v(-79.13, 6.33) * mm});
            skLineSegment(sketch, "E3312", {"start": v(-79.13, 6.33) * mm, "end": v(-79.58, 7.13) * mm});
            skLineSegment(sketch, "E3313", {"start": v(-79.58, 7.13) * mm, "end": v(-80.08, 7.9) * mm});
            skLineSegment(sketch, "E3314", {"start": v(-80.08, 7.9) * mm, "end": v(-80.61, 8.66) * mm});
            skLineSegment(sketch, "E3315", {"start": v(-80.61, 8.66) * mm, "end": v(-81.2, 9.4) * mm});
            skLineSegment(sketch, "E3316", {"start": v(-81.2, 9.4) * mm, "end": v(-81.81, 10.1) * mm});
            skLineSegment(sketch, "E3317", {"start": v(-81.81, 10.1) * mm, "end": v(-82.48, 10.8) * mm});
            skLineSegment(sketch, "E3318", {"start": v(-82.48, 10.8) * mm, "end": v(-83.17, 11.47) * mm});
            skLineSegment(sketch, "E3319", {"start": v(-83.17, 11.47) * mm, "end": v(-83.89, 12.09) * mm});
            skLineSegment(sketch, "E3320", {"start": v(-83.89, 12.09) * mm, "end": v(-84.62, 12.67) * mm});
            skLineSegment(sketch, "E3321", {"start": v(-84.62, 12.67) * mm, "end": v(-85.38, 13.2) * mm});
            skLineSegment(sketch, "E3322", {"start": v(-85.38, 13.2) * mm, "end": v(-86.15, 13.7) * mm});
            skLineSegment(sketch, "E3323", {"start": v(-86.15, 13.7) * mm, "end": v(-86.95, 14.15) * mm});
            skLineSegment(sketch, "E3324", {"start": v(-86.95, 14.15) * mm, "end": v(-87.76, 14.56) * mm});
            skLineSegment(sketch, "E3325", {"start": v(-87.76, 14.56) * mm, "end": v(-88.6, 14.93) * mm});
            skLineSegment(sketch, "E3326", {"start": v(-88.6, 14.93) * mm, "end": v(-89.44, 15.25) * mm});
            skLineSegment(sketch, "E3327", {"start": v(-89.44, 15.25) * mm, "end": v(-90.31, 15.53) * mm});
            skLineSegment(sketch, "E3328", {"start": v(-90.31, 15.53) * mm, "end": v(-91.2, 15.77) * mm});
            skLineSegment(sketch, "E3329", {"start": v(-91.2, 15.77) * mm, "end": v(-92.1, 15.96) * mm});
            skLineSegment(sketch, "E3330", {"start": v(-92.1, 15.96) * mm, "end": v(-93.03, 16.11) * mm});
            skLineSegment(sketch, "E3331", {"start": v(-93.03, 16.11) * mm, "end": v(-93.97, 16.22) * mm});
            skLineSegment(sketch, "E3332", {"start": v(-93.97, 16.22) * mm, "end": v(-94.93, 16.29) * mm});
            skLineSegment(sketch, "E3333", {"start": v(-94.93, 16.29) * mm, "end": v(-95.91, 16.3) * mm});
            skLineSegment(sketch, "E3334", {"start": v(-95.91, 16.3) * mm, "end": v(-96.88, 16.29) * mm});
            skLineSegment(sketch, "E3335", {"start": v(-96.88, 16.29) * mm, "end": v(-97.84, 16.22) * mm});
            skLineSegment(sketch, "E3336", {"start": v(-97.84, 16.22) * mm, "end": v(-98.77, 16.11) * mm});
            skLineSegment(sketch, "E3337", {"start": v(-98.77, 16.11) * mm, "end": v(-99.7, 15.96) * mm});
            skLineSegment(sketch, "E3338", {"start": v(-99.7, 15.96) * mm, "end": v(-100.6, 15.77) * mm});
            skLineSegment(sketch, "E3339", {"start": v(-100.6, 15.77) * mm, "end": v(-101.48, 15.53) * mm});
            skLineSegment(sketch, "E3340", {"start": v(-101.48, 15.53) * mm, "end": v(-102.34, 15.25) * mm});
            skLineSegment(sketch, "E3341", {"start": v(-102.34, 15.25) * mm, "end": v(-103.19, 14.93) * mm});
            skLineSegment(sketch, "E3342", {"start": v(-103.19, 14.93) * mm, "end": v(-104.02, 14.56) * mm});
            skLineSegment(sketch, "E3343", {"start": v(-104.02, 14.56) * mm, "end": v(-104.83, 14.15) * mm});
            skLineSegment(sketch, "E3344", {"start": v(-104.83, 14.15) * mm, "end": v(-105.62, 13.7) * mm});
            skLineSegment(sketch, "E3345", {"start": v(-105.62, 13.7) * mm, "end": v(-106.4, 13.2) * mm});
            skLineSegment(sketch, "E3346", {"start": v(-106.4, 13.2) * mm, "end": v(-107.15, 12.67) * mm});
            skLineSegment(sketch, "E3347", {"start": v(-107.15, 12.67) * mm, "end": v(-107.88, 12.09) * mm});
            skLineSegment(sketch, "E3348", {"start": v(-107.88, 12.09) * mm, "end": v(-108.6, 11.47) * mm});
            skLineSegment(sketch, "E3349", {"start": v(-108.6, 11.47) * mm, "end": v(-109.29, 10.8) * mm});
            skLineSegment(sketch, "E3350", {"start": v(-109.29, 10.8) * mm, "end": v(-109.95, 10.1) * mm});
            skLineSegment(sketch, "E3351", {"start": v(-109.95, 10.1) * mm, "end": v(-110.58, 9.4) * mm});
            skLineSegment(sketch, "E3352", {"start": v(-110.58, 9.4) * mm, "end": v(-111.15, 8.66) * mm});
            skLineSegment(sketch, "E3353", {"start": v(-111.15, 8.66) * mm, "end": v(-111.7, 7.9) * mm});
            skLineSegment(sketch, "E3354", {"start": v(-111.7, 7.9) * mm, "end": v(-112.19, 7.13) * mm});
            skLineSegment(sketch, "E3355", {"start": v(-112.19, 7.13) * mm, "end": v(-112.64, 6.33) * mm});
            skLineSegment(sketch, "E3356", {"start": v(-112.64, 6.33) * mm, "end": v(-113.05, 5.52) * mm});
            skLineSegment(sketch, "E3357", {"start": v(-113.05, 5.52) * mm, "end": v(-113.41, 4.69) * mm});
            skLineSegment(sketch, "E3358", {"start": v(-113.41, 4.69) * mm, "end": v(-113.74, 3.84) * mm});
            skLineSegment(sketch, "E3359", {"start": v(-113.74, 3.84) * mm, "end": v(-114.02, 2.97) * mm});
            skLineSegment(sketch, "E3360", {"start": v(-114.02, 2.97) * mm, "end": v(-114.25, 2.08) * mm});
            skLineSegment(sketch, "E3361", {"start": v(-114.25, 2.08) * mm, "end": v(-114.45, 1.17) * mm});
            skLineSegment(sketch, "E3362", {"start": v(-114.45, 1.17) * mm, "end": v(-114.6, 0.25) * mm});
            skLineSegment(sketch, "E3363", {"start": v(-114.6, 0.25) * mm, "end": v(-114.7, -0.7) * mm});
            skLineSegment(sketch, "E3364", {"start": v(-114.7, -0.7) * mm, "end": v(-114.77, -1.65) * mm});
            skLineSegment(sketch, "E3365", {"start": v(-114.77, -1.65) * mm, "end": v(-114.8, -2.63) * mm});
            skLineSegment(sketch, "E3366", {"start": v(-114.8, -2.63) * mm, "end": v(-114.78, -3.45) * mm});
            skLineSegment(sketch, "E3367", {"start": v(-114.78, -3.45) * mm, "end": v(-114.73, -4.26) * mm});
            skLineSegment(sketch, "E3368", {"start": v(-114.73, -4.26) * mm, "end": v(-114.65, -5.07) * mm});
            skLineSegment(sketch, "E3369", {"start": v(-114.65, -5.07) * mm, "end": v(-114.53, -5.86) * mm});
            skLineSegment(sketch, "E3370", {"start": v(-114.53, -5.86) * mm, "end": v(-114.38, -6.64) * mm});
            skLineSegment(sketch, "E3371", {"start": v(-114.38, -6.64) * mm, "end": v(-114.2, -7.41) * mm});
            skLineSegment(sketch, "E3372", {"start": v(-114.2, -7.41) * mm, "end": v(-113.98, -8.17) * mm});
            skLineSegment(sketch, "E3373", {"start": v(-113.98, -8.17) * mm, "end": v(-113.73, -8.92) * mm});
            skLineSegment(sketch, "E3374", {"start": v(-113.73, -8.92) * mm, "end": v(-113.45, -9.66) * mm});
            skLineSegment(sketch, "E3375", {"start": v(-113.45, -9.66) * mm, "end": v(-113.14, -10.38) * mm});
            skLineSegment(sketch, "E3376", {"start": v(-113.14, -10.38) * mm, "end": v(-112.8, -11.1) * mm});
            skLineSegment(sketch, "E3377", {"start": v(-112.8, -11.1) * mm, "end": v(-112.41, -11.8) * mm});
            skLineSegment(sketch, "E3378", {"start": v(-112.41, -11.8) * mm, "end": v(-112, -12.5) * mm});
            skLineSegment(sketch, "E3379", {"start": v(-112, -12.5) * mm, "end": v(-111.55, -13.17) * mm});
            skLineSegment(sketch, "E3380", {"start": v(-111.55, -13.17) * mm, "end": v(-111.08, -13.84) * mm});
            skLineSegment(sketch, "E3381", {"start": v(-111.08, -13.84) * mm, "end": v(-110.57, -14.5) * mm});
            skLineSegment(sketch, "E3382", {"start": v(-110.57, -14.5) * mm, "end": v(-110.04, -15.11) * mm});
            skLineSegment(sketch, "E3383", {"start": v(-110.04, -15.11) * mm, "end": v(-109.5, -15.7) * mm});
            skLineSegment(sketch, "E3384", {"start": v(-109.5, -15.7) * mm, "end": v(-108.94, -16.27) * mm});
            skLineSegment(sketch, "E3385", {"start": v(-108.94, -16.27) * mm, "end": v(-108.36, -16.81) * mm});
            skLineSegment(sketch, "E3386", {"start": v(-108.36, -16.81) * mm, "end": v(-107.76, -17.32) * mm});
            skLineSegment(sketch, "E3387", {"start": v(-107.76, -17.32) * mm, "end": v(-107.15, -17.8) * mm});
            skLineSegment(sketch, "E3388", {"start": v(-107.15, -17.8) * mm, "end": v(-106.51, -18.25) * mm});
            skLineSegment(sketch, "E3389", {"start": v(-106.51, -18.25) * mm, "end": v(-105.86, -18.68) * mm});
            skLineSegment(sketch, "E3390", {"start": v(-105.86, -18.68) * mm, "end": v(-105.2, -19.07) * mm});
            skLineSegment(sketch, "E3391", {"start": v(-105.2, -19.07) * mm, "end": v(-104.51, -19.44) * mm});
            skLineSegment(sketch, "E3392", {"start": v(-104.51, -19.44) * mm, "end": v(-103.81, -19.78) * mm});
            skLineSegment(sketch, "E3393", {"start": v(-103.81, -19.78) * mm, "end": v(-103.1, -20.09) * mm});
            skLineSegment(sketch, "E3394", {"start": v(-103.1, -20.09) * mm, "end": v(-102.36, -20.37) * mm});
            skLineSegment(sketch, "E3395", {"start": v(-102.36, -20.37) * mm, "end": v(-101.6, -20.62) * mm});
            skLineSegment(sketch, "E3396", {"start": v(-101.6, -20.62) * mm, "end": v(-100.84, -20.84) * mm});
            skLineSegment(sketch, "E3397", {"start": v(-100.84, -20.84) * mm, "end": v(-100.05, -21.03) * mm});
            skLineSegment(sketch, "E3398", {"start": v(-100.05, -21.03) * mm, "end": v(-100.03, -21.04) * mm});
            skLineSegment(sketch, "E3399", {"start": v(-100.03, -21.04) * mm, "end": v(-100.01, -21.04) * mm});
            skLineSegment(sketch, "E3400", {"start": v(-100.01, -21.04) * mm, "end": v(-100, -21.05) * mm});
            skLineSegment(sketch, "E3401", {"start": v(-100, -21.05) * mm, "end": v(-99.98, -21.06) * mm});
            skLineSegment(sketch, "E3402", {"start": v(-99.98, -21.06) * mm, "end": v(-99.96, -21.07) * mm});
            skLineSegment(sketch, "E3403", {"start": v(-99.96, -21.07) * mm, "end": v(-99.95, -21.09) * mm});
            skLineSegment(sketch, "E3404", {"start": v(-99.95, -21.09) * mm, "end": v(-99.94, -21.1) * mm});
            skLineSegment(sketch, "E3405", {"start": v(-99.94, -21.1) * mm, "end": v(-99.92, -21.11) * mm});
            skLineSegment(sketch, "E3406", {"start": v(-99.92, -21.11) * mm, "end": v(-99.91, -21.13) * mm});
            skLineSegment(sketch, "E3407", {"start": v(-99.91, -21.13) * mm, "end": v(-99.9, -21.14) * mm});
            skLineSegment(sketch, "E3408", {"start": v(-99.9, -21.14) * mm, "end": v(-99.9, -21.16) * mm});
            skLineSegment(sketch, "E3409", {"start": v(-99.9, -21.16) * mm, "end": v(-99.89, -21.18) * mm});
            skLineSegment(sketch, "E3410", {"start": v(-99.89, -21.18) * mm, "end": v(-99.88, -21.2) * mm});
            skLineSegment(sketch, "E3411", {"start": v(-99.88, -21.2) * mm, "end": v(-99.88, -21.21) * mm});
            skLineSegment(sketch, "E3412", {"start": v(-99.88, -21.21) * mm, "end": v(-99.87, -21.23) * mm});
            skLineSegment(sketch, "E3413", {"start": v(-99.87, -21.23) * mm, "end": v(-99.87, -21.25) * mm});
            skLineSegment(sketch, "E3414", {"start": v(-99.87, -21.25) * mm, "end": v(-99.87, -22.91) * mm});
            skLineSegment(sketch, "E3415", {"start": v(-99.87, -22.91) * mm, "end": v(-99.88, -22.97) * mm});
            skLineSegment(sketch, "E3416", {"start": v(-99.88, -22.97) * mm, "end": v(-99.89, -23.03) * mm});
            skLineSegment(sketch, "E3417", {"start": v(-99.89, -23.03) * mm, "end": v(-99.9, -23.08) * mm});
            skLineSegment(sketch, "E3418", {"start": v(-99.9, -23.08) * mm, "end": v(-99.92, -23.13) * mm});
            skLineSegment(sketch, "E3419", {"start": v(-99.92, -23.13) * mm, "end": v(-99.94, -23.18) * mm});
            skLineSegment(sketch, "E3420", {"start": v(-99.94, -23.18) * mm, "end": v(-99.97, -23.23) * mm});
            skLineSegment(sketch, "E3421", {"start": v(-99.97, -23.23) * mm, "end": v(-100, -23.28) * mm});
            skLineSegment(sketch, "E3422", {"start": v(-100, -23.28) * mm, "end": v(-100.04, -23.32) * mm});
            skLineSegment(sketch, "E3423", {"start": v(-100.04, -23.32) * mm, "end": v(-100.08, -23.35) * mm});
            skLineSegment(sketch, "E3424", {"start": v(-100.08, -23.35) * mm, "end": v(-100.13, -23.39) * mm});
            skLineSegment(sketch, "E3425", {"start": v(-100.13, -23.39) * mm, "end": v(-100.17, -23.42) * mm});
            skLineSegment(sketch, "E3426", {"start": v(-100.17, -23.42) * mm, "end": v(-100.22, -23.44) * mm});
            skLineSegment(sketch, "E3427", {"start": v(-100.22, -23.44) * mm, "end": v(-100.28, -23.46) * mm});
            skLineSegment(sketch, "E3428", {"start": v(-100.28, -23.46) * mm, "end": v(-100.33, -23.47) * mm});
            skLineSegment(sketch, "E3429", {"start": v(-100.33, -23.47) * mm, "end": v(-100.39, -23.48) * mm});
            skLineSegment(sketch, "E3430", {"start": v(-100.39, -23.48) * mm, "end": v(-100.44, -23.48) * mm});
            skLineSegment(sketch, "E3431", {"start": v(-100.44, -23.48) * mm, "end": v(-140.73, -23.48) * mm});
            skLineSegment(sketch, "E3432", {"start": v(-140.73, -23.48) * mm, "end": v(-140.86, -23.48) * mm});
            skLineSegment(sketch, "E3433", {"start": v(-140.86, -23.48) * mm, "end": v(-140.97, -23.47) * mm});
            skLineSegment(sketch, "E3434", {"start": v(-140.97, -23.47) * mm, "end": v(-141.08, -23.45) * mm});
            skLineSegment(sketch, "E3435", {"start": v(-141.08, -23.45) * mm, "end": v(-141.18, -23.43) * mm});
            skLineSegment(sketch, "E3436", {"start": v(-141.18, -23.43) * mm, "end": v(-141.27, -23.4) * mm});
            skLineSegment(sketch, "E3437", {"start": v(-141.27, -23.4) * mm, "end": v(-141.35, -23.35) * mm});
            skLineSegment(sketch, "E3438", {"start": v(-141.35, -23.35) * mm, "end": v(-141.43, -23.3) * mm});
            skLineSegment(sketch, "E3439", {"start": v(-141.43, -23.3) * mm, "end": v(-141.5, -23.25) * mm});
            skLineSegment(sketch, "E3440", {"start": v(-141.5, -23.25) * mm, "end": v(-141.55, -23.19) * mm});
            skLineSegment(sketch, "E3441", {"start": v(-141.55, -23.19) * mm, "end": v(-141.6, -23.12) * mm});
            skLineSegment(sketch, "E3442", {"start": v(-141.6, -23.12) * mm, "end": v(-141.65, -23.04) * mm});
            skLineSegment(sketch, "E3443", {"start": v(-141.65, -23.04) * mm, "end": v(-141.68, -22.95) * mm});
            skLineSegment(sketch, "E3444", {"start": v(-141.68, -22.95) * mm, "end": v(-141.7, -22.86) * mm});
            skLineSegment(sketch, "E3445", {"start": v(-141.7, -22.86) * mm, "end": v(-141.73, -22.75) * mm});
            skLineSegment(sketch, "E3446", {"start": v(-141.73, -22.75) * mm, "end": v(-141.74, -22.64) * mm});
            skLineSegment(sketch, "E3447", {"start": v(-141.74, -22.64) * mm, "end": v(-141.74, -22.53) * mm});
            skLineSegment(sketch, "E3448", {"start": v(-141.74, -22.53) * mm, "end": v(-141.74, -22.4) * mm});
            skLineSegment(sketch, "E3449", {"start": v(-141.74, -22.4) * mm, "end": v(-141.73, -22.3) * mm});
            skLineSegment(sketch, "E3450", {"start": v(-141.73, -22.3) * mm, "end": v(-141.7, -22.2) * mm});
            skLineSegment(sketch, "E3451", {"start": v(-141.7, -22.2) * mm, "end": v(-141.68, -22.1) * mm});
            skLineSegment(sketch, "E3452", {"start": v(-141.68, -22.1) * mm, "end": v(-141.65, -22.01) * mm});
            skLineSegment(sketch, "E3453", {"start": v(-141.65, -22.01) * mm, "end": v(-141.6, -21.94) * mm});
            skLineSegment(sketch, "E3454", {"start": v(-141.6, -21.94) * mm, "end": v(-141.55, -21.86) * mm});
            skLineSegment(sketch, "E3455", {"start": v(-141.55, -21.86) * mm, "end": v(-141.5, -21.8) * mm});
            skLineSegment(sketch, "E3456", {"start": v(-141.5, -21.8) * mm, "end": v(-141.43, -21.75) * mm});
            skLineSegment(sketch, "E3457", {"start": v(-141.43, -21.75) * mm, "end": v(-141.35, -21.7) * mm});
            skLineSegment(sketch, "E3458", {"start": v(-141.35, -21.7) * mm, "end": v(-141.27, -21.66) * mm});
            skLineSegment(sketch, "E3459", {"start": v(-141.27, -21.66) * mm, "end": v(-141.18, -21.63) * mm});
            skLineSegment(sketch, "E3460", {"start": v(-141.18, -21.63) * mm, "end": v(-141.08, -21.6) * mm});
            skLineSegment(sketch, "E3461", {"start": v(-141.08, -21.6) * mm, "end": v(-140.97, -21.58) * mm});
            skLineSegment(sketch, "E3462", {"start": v(-140.97, -21.58) * mm, "end": v(-140.86, -21.57) * mm});
            skLineSegment(sketch, "E3463", {"start": v(-140.86, -21.57) * mm, "end": v(-140.73, -21.57) * mm});
            skLineSegment(sketch, "E3464", {"start": v(-140.73, -21.57) * mm, "end": v(-123.48, -21.57) * mm});
            skLineSegment(sketch, "E3465", {"start": v(-123.48, -21.57) * mm, "end": v(-123.27, -21.56) * mm});
            skLineSegment(sketch, "E3466", {"start": v(-123.27, -21.56) * mm, "end": v(-123.07, -21.55) * mm});
            skLineSegment(sketch, "E3467", {"start": v(-123.07, -21.55) * mm, "end": v(-122.87, -21.53) * mm});
            skLineSegment(sketch, "E3468", {"start": v(-122.87, -21.53) * mm, "end": v(-122.67, -21.5) * mm});
            skLineSegment(sketch, "E3469", {"start": v(-122.67, -21.5) * mm, "end": v(-122.48, -21.46) * mm});
            skLineSegment(sketch, "E3470", {"start": v(-122.48, -21.46) * mm, "end": v(-122.3, -21.4) * mm});
            skLineSegment(sketch, "E3471", {"start": v(-122.3, -21.4) * mm, "end": v(-122.1, -21.35) * mm});
            skLineSegment(sketch, "E3472", {"start": v(-122.1, -21.35) * mm, "end": v(-121.93, -21.28) * mm});
            skLineSegment(sketch, "E3473", {"start": v(-121.93, -21.28) * mm, "end": v(-121.75, -21.2) * mm});
            skLineSegment(sketch, "E3474", {"start": v(-121.75, -21.2) * mm, "end": v(-121.58, -21.12) * mm});
            skLineSegment(sketch, "E3475", {"start": v(-121.58, -21.12) * mm, "end": v(-121.41, -21.03) * mm});
            skLineSegment(sketch, "E3476", {"start": v(-121.41, -21.03) * mm, "end": v(-121.25, -20.92) * mm});
            skLineSegment(sketch, "E3477", {"start": v(-121.25, -20.92) * mm, "end": v(-121.09, -20.81) * mm});
            skLineSegment(sketch, "E3478", {"start": v(-121.09, -20.81) * mm, "end": v(-120.93, -20.7) * mm});
            skLineSegment(sketch, "E3479", {"start": v(-120.93, -20.7) * mm, "end": v(-120.78, -20.57) * mm});
            skLineSegment(sketch, "E3480", {"start": v(-120.78, -20.57) * mm, "end": v(-120.63, -20.43) * mm});
            skLineSegment(sketch, "E3481", {"start": v(-120.63, -20.43) * mm, "end": v(-120.5, -20.28) * mm});
            skLineSegment(sketch, "E3482", {"start": v(-120.5, -20.28) * mm, "end": v(-120.36, -20.13) * mm});
            skLineSegment(sketch, "E3483", {"start": v(-120.36, -20.13) * mm, "end": v(-120.24, -19.98) * mm});
            skLineSegment(sketch, "E3484", {"start": v(-120.24, -19.98) * mm, "end": v(-120.12, -19.82) * mm});
            skLineSegment(sketch, "E3485", {"start": v(-120.12, -19.82) * mm, "end": v(-120.02, -19.66) * mm});
            skLineSegment(sketch, "E3486", {"start": v(-120.02, -19.66) * mm, "end": v(-119.92, -19.5) * mm});
            skLineSegment(sketch, "E3487", {"start": v(-119.92, -19.5) * mm, "end": v(-119.84, -19.33) * mm});
            skLineSegment(sketch, "E3488", {"start": v(-119.84, -19.33) * mm, "end": v(-119.76, -19.15) * mm});
            skLineSegment(sketch, "E3489", {"start": v(-119.76, -19.15) * mm, "end": v(-119.69, -18.97) * mm});
            skLineSegment(sketch, "E3490", {"start": v(-119.69, -18.97) * mm, "end": v(-119.63, -18.79) * mm});
            skLineSegment(sketch, "E3491", {"start": v(-119.63, -18.79) * mm, "end": v(-119.58, -18.6) * mm});
            skLineSegment(sketch, "E3492", {"start": v(-119.58, -18.6) * mm, "end": v(-119.54, -18.4) * mm});
            skLineSegment(sketch, "E3493", {"start": v(-119.54, -18.4) * mm, "end": v(-119.5, -18.21) * mm});
            skLineSegment(sketch, "E3494", {"start": v(-119.5, -18.21) * mm, "end": v(-119.48, -18.02) * mm});
            skLineSegment(sketch, "E3495", {"start": v(-119.48, -18.02) * mm, "end": v(-119.47, -17.81) * mm});
            skLineSegment(sketch, "E3496", {"start": v(-119.47, -17.81) * mm, "end": v(-119.46, -17.6) * mm});
            skLineSegment(sketch, "E3497", {"start": v(-119.46, -17.6) * mm, "end": v(-119.47, -17.4) * mm});
            skLineSegment(sketch, "E3498", {"start": v(-119.47, -17.4) * mm, "end": v(-119.48, -17.18) * mm});
            skLineSegment(sketch, "E3499", {"start": v(-119.48, -17.18) * mm, "end": v(-119.5, -16.98) * mm});
            skLineSegment(sketch, "E3500", {"start": v(-119.5, -16.98) * mm, "end": v(-119.54, -16.78) * mm});
            skLineSegment(sketch, "E3501", {"start": v(-119.54, -16.78) * mm, "end": v(-119.58, -16.58) * mm});
            skLineSegment(sketch, "E3502", {"start": v(-119.58, -16.58) * mm, "end": v(-119.63, -16.39) * mm});
            skLineSegment(sketch, "E3503", {"start": v(-119.63, -16.39) * mm, "end": v(-119.68, -16.2) * mm});
            skLineSegment(sketch, "E3504", {"start": v(-119.68, -16.2) * mm, "end": v(-119.75, -16.02) * mm});
            skLineSegment(sketch, "E3505", {"start": v(-119.75, -16.02) * mm, "end": v(-119.83, -15.84) * mm});
            skLineSegment(sketch, "E3506", {"start": v(-119.83, -15.84) * mm, "end": v(-119.91, -15.67) * mm});
            skLineSegment(sketch, "E3507", {"start": v(-119.91, -15.67) * mm, "end": v(-120, -15.5) * mm});
            skLineSegment(sketch, "E3508", {"start": v(-120, -15.5) * mm, "end": v(-120.1, -15.34) * mm});
            skLineSegment(sketch, "E3509", {"start": v(-120.1, -15.34) * mm, "end": v(-120.22, -15.18) * mm});
            skLineSegment(sketch, "E3510", {"start": v(-120.22, -15.18) * mm, "end": v(-120.34, -15.02) * mm});
            skLineSegment(sketch, "E3511", {"start": v(-120.34, -15.02) * mm, "end": v(-120.47, -14.87) * mm});
            skLineSegment(sketch, "E3512", {"start": v(-120.47, -14.87) * mm, "end": v(-120.6, -14.73) * mm});
            skLineSegment(sketch, "E3513", {"start": v(-120.6, -14.73) * mm, "end": v(-120.75, -14.6) * mm});
            skLineSegment(sketch, "E3514", {"start": v(-120.75, -14.6) * mm, "end": v(-120.9, -14.46) * mm});
            skLineSegment(sketch, "E3515", {"start": v(-120.9, -14.46) * mm, "end": v(-121.05, -14.34) * mm});
            skLineSegment(sketch, "E3516", {"start": v(-121.05, -14.34) * mm, "end": v(-121.21, -14.23) * mm});
            skLineSegment(sketch, "E3517", {"start": v(-121.21, -14.23) * mm, "end": v(-121.37, -14.13) * mm});
            skLineSegment(sketch, "E3518", {"start": v(-121.37, -14.13) * mm, "end": v(-121.54, -14.04) * mm});
            skLineSegment(sketch, "E3519", {"start": v(-121.54, -14.04) * mm, "end": v(-121.72, -13.95) * mm});
            skLineSegment(sketch, "E3520", {"start": v(-121.72, -13.95) * mm, "end": v(-121.9, -13.88) * mm});
            skLineSegment(sketch, "E3521", {"start": v(-121.9, -13.88) * mm, "end": v(-122.08, -13.8) * mm});
            skLineSegment(sketch, "E3522", {"start": v(-122.08, -13.8) * mm, "end": v(-122.26, -13.75) * mm});
            skLineSegment(sketch, "E3523", {"start": v(-122.26, -13.75) * mm, "end": v(-122.46, -13.7) * mm});
            skLineSegment(sketch, "E3524", {"start": v(-122.46, -13.7) * mm, "end": v(-122.65, -13.66) * mm});
            skLineSegment(sketch, "E3525", {"start": v(-122.65, -13.66) * mm, "end": v(-122.85, -13.63) * mm});
            skLineSegment(sketch, "E3526", {"start": v(-122.85, -13.63) * mm, "end": v(-123.06, -13.6) * mm});
            skLineSegment(sketch, "E3527", {"start": v(-123.06, -13.6) * mm, "end": v(-123.27, -13.6) * mm});
            skLineSegment(sketch, "E3528", {"start": v(-123.27, -13.6) * mm, "end": v(-123.48, -13.59) * mm});
            skLineSegment(sketch, "E3529", {"start": v(-123.48, -13.59) * mm, "end": v(-138.61, -13.59) * mm});
            skLineSegment(sketch, "E3530", {"start": v(-138.61, -13.59) * mm, "end": v(-138.9, -13.58) * mm});
            skLineSegment(sketch, "E3531", {"start": v(-138.9, -13.58) * mm, "end": v(-139.18, -13.54) * mm});
            skLineSegment(sketch, "E3532", {"start": v(-139.18, -13.54) * mm, "end": v(-139.46, -13.47) * mm});
            skLineSegment(sketch, "E3533", {"start": v(-139.46, -13.47) * mm, "end": v(-139.72, -13.38) * mm});
            skLineSegment(sketch, "E3534", {"start": v(-139.72, -13.38) * mm, "end": v(-139.97, -13.27) * mm});
            skLineSegment(sketch, "E3535", {"start": v(-139.97, -13.27) * mm, "end": v(-140.22, -13.14) * mm});
            skLineSegment(sketch, "E3536", {"start": v(-140.22, -13.14) * mm, "end": v(-140.44, -13) * mm});
            skLineSegment(sketch, "E3537", {"start": v(-140.44, -13) * mm, "end": v(-140.66, -12.82) * mm});
            skLineSegment(sketch, "E3538", {"start": v(-140.66, -12.82) * mm, "end": v(-140.86, -12.63) * mm});
            skLineSegment(sketch, "E3539", {"start": v(-140.86, -12.63) * mm, "end": v(-141.04, -12.43) * mm});
            skLineSegment(sketch, "E3540", {"start": v(-141.04, -12.43) * mm, "end": v(-141.2, -12.2) * mm});
            skLineSegment(sketch, "E3541", {"start": v(-141.2, -12.2) * mm, "end": v(-141.34, -11.97) * mm});
            skLineSegment(sketch, "E3542", {"start": v(-141.34, -11.97) * mm, "end": v(-141.46, -11.72) * mm});
            skLineSegment(sketch, "E3543", {"start": v(-141.46, -11.72) * mm, "end": v(-141.56, -11.46) * mm});
            skLineSegment(sketch, "E3544", {"start": v(-141.56, -11.46) * mm, "end": v(-141.64, -11.19) * mm});
            skLineSegment(sketch, "E3545", {"start": v(-141.64, -11.19) * mm, "end": v(-141.69, -10.9) * mm});
            skLineSegment(sketch, "E3546", {"start": v(-141.69, -10.9) * mm, "end": v(-141.72, -10.65) * mm});
            skLineSegment(sketch, "E3547", {"start": v(-141.72, -10.65) * mm, "end": v(-141.74, -10.4) * mm});
            skLineSegment(sketch, "E3548", {"start": v(-141.74, -10.4) * mm, "end": v(-141.74, -10.16) * mm});
            skLineSegment(sketch, "E3549", {"start": v(-141.74, -10.16) * mm, "end": v(-141.74, -9.92) * mm});
            skLineSegment(sketch, "E3550", {"start": v(-141.74, -9.92) * mm, "end": v(-141.72, -9.7) * mm});
            skLineSegment(sketch, "E3551", {"start": v(-141.72, -9.7) * mm, "end": v(-141.7, -9.47) * mm});
            skLineSegment(sketch, "E3552", {"start": v(-141.7, -9.47) * mm, "end": v(-141.65, -9.26) * mm});
            skLineSegment(sketch, "E3553", {"start": v(-141.65, -9.26) * mm, "end": v(-141.6, -9.05) * mm});
            skLineSegment(sketch, "E3554", {"start": v(-141.6, -9.05) * mm, "end": v(-141.54, -8.85) * mm});
            skLineSegment(sketch, "E3555", {"start": v(-141.54, -8.85) * mm, "end": v(-141.47, -8.65) * mm});
            skLineSegment(sketch, "E3556", {"start": v(-141.47, -8.65) * mm, "end": v(-141.38, -8.47) * mm});
            skLineSegment(sketch, "E3557", {"start": v(-141.38, -8.47) * mm, "end": v(-141.29, -8.29) * mm});
            skLineSegment(sketch, "E3558", {"start": v(-141.29, -8.29) * mm, "end": v(-141.18, -8.12) * mm});
            skLineSegment(sketch, "E3559", {"start": v(-141.18, -8.12) * mm, "end": v(-141.06, -7.95) * mm});
            skLineSegment(sketch, "E3560", {"start": v(-141.06, -7.95) * mm, "end": v(-140.93, -7.8) * mm});
            skLineSegment(sketch, "E3561", {"start": v(-140.93, -7.8) * mm, "end": v(-140.8, -7.65) * mm});
            skLineSegment(sketch, "E3562", {"start": v(-140.8, -7.65) * mm, "end": v(-140.67, -7.53) * mm});
            skLineSegment(sketch, "E3563", {"start": v(-140.67, -7.53) * mm, "end": v(-140.55, -7.43) * mm});
            skLineSegment(sketch, "E3564", {"start": v(-140.55, -7.43) * mm, "end": v(-140.42, -7.33) * mm});
            skLineSegment(sketch, "E3565", {"start": v(-140.42, -7.33) * mm, "end": v(-140.28, -7.23) * mm});
            skLineSegment(sketch, "E3566", {"start": v(-140.28, -7.23) * mm, "end": v(-140.14, -7.15) * mm});
            skLineSegment(sketch, "E3567", {"start": v(-140.14, -7.15) * mm, "end": v(-140, -7.07) * mm});
            skLineSegment(sketch, "E3568", {"start": v(-140, -7.07) * mm, "end": v(-139.85, -7) * mm});
            skLineSegment(sketch, "E3569", {"start": v(-139.85, -7) * mm, "end": v(-139.7, -6.94) * mm});
            skLineSegment(sketch, "E3570", {"start": v(-139.7, -6.94) * mm, "end": v(-139.53, -6.88) * mm});
            skLineSegment(sketch, "E3571", {"start": v(-139.53, -6.88) * mm, "end": v(-139.37, -6.83) * mm});
            skLineSegment(sketch, "E3572", {"start": v(-139.37, -6.83) * mm, "end": v(-139.2, -6.8) * mm});
            skLineSegment(sketch, "E3573", {"start": v(-139.2, -6.8) * mm, "end": v(-139.03, -6.76) * mm});
            skLineSegment(sketch, "E3574", {"start": v(-139.03, -6.76) * mm, "end": v(-138.85, -6.73) * mm});
            skLineSegment(sketch, "E3575", {"start": v(-138.85, -6.73) * mm, "end": v(-138.67, -6.71) * mm});
            skLineSegment(sketch, "E3576", {"start": v(-138.67, -6.71) * mm, "end": v(-138.49, -6.7) * mm});
            skLineSegment(sketch, "E3577", {"start": v(-138.49, -6.7) * mm, "end": v(-138.3, -6.7) * mm});
            skLineSegment(sketch, "E3578", {"start": v(-138.3, -6.7) * mm, "end": v(-128.4, -6.7) * mm});
            skLineSegment(sketch, "E3579", {"start": v(-128.4, -6.7) * mm, "end": v(-128.18, -6.7) * mm});
            skLineSegment(sketch, "E3580", {"start": v(-128.18, -6.7) * mm, "end": v(-127.97, -6.68) * mm});
            skLineSegment(sketch, "E3581", {"start": v(-127.97, -6.68) * mm, "end": v(-127.76, -6.66) * mm});
            skLineSegment(sketch, "E3582", {"start": v(-127.76, -6.66) * mm, "end": v(-127.55, -6.63) * mm});
            skLineSegment(sketch, "E3583", {"start": v(-127.55, -6.63) * mm, "end": v(-127.35, -6.6) * mm});
            skLineSegment(sketch, "E3584", {"start": v(-127.35, -6.6) * mm, "end": v(-127.16, -6.54) * mm});
            skLineSegment(sketch, "E3585", {"start": v(-127.16, -6.54) * mm, "end": v(-126.97, -6.49) * mm});
            skLineSegment(sketch, "E3586", {"start": v(-126.97, -6.49) * mm, "end": v(-126.79, -6.42) * mm});
            skLineSegment(sketch, "E3587", {"start": v(-126.79, -6.42) * mm, "end": v(-126.61, -6.35) * mm});
            skLineSegment(sketch, "E3588", {"start": v(-126.61, -6.35) * mm, "end": v(-126.44, -6.27) * mm});
            skLineSegment(sketch, "E3589", {"start": v(-126.44, -6.27) * mm, "end": v(-126.27, -6.18) * mm});
            skLineSegment(sketch, "E3590", {"start": v(-126.27, -6.18) * mm, "end": v(-126.11, -6.08) * mm});
            skLineSegment(sketch, "E3591", {"start": v(-126.11, -6.08) * mm, "end": v(-125.96, -5.98) * mm});
            skLineSegment(sketch, "E3592", {"start": v(-125.96, -5.98) * mm, "end": v(-125.8, -5.86) * mm});
            skLineSegment(sketch, "E3593", {"start": v(-125.8, -5.86) * mm, "end": v(-125.66, -5.74) * mm});
            skLineSegment(sketch, "E3594", {"start": v(-125.66, -5.74) * mm, "end": v(-125.53, -5.61) * mm});
            skLineSegment(sketch, "E3595", {"start": v(-125.53, -5.61) * mm, "end": v(-125.4, -5.47) * mm});
            skLineSegment(sketch, "E3596", {"start": v(-125.4, -5.47) * mm, "end": v(-125.27, -5.33) * mm});
            skLineSegment(sketch, "E3597", {"start": v(-125.27, -5.33) * mm, "end": v(-125.16, -5.18) * mm});
            skLineSegment(sketch, "E3598", {"start": v(-125.16, -5.18) * mm, "end": v(-125.05, -5.02) * mm});
            skLineSegment(sketch, "E3599", {"start": v(-125.05, -5.02) * mm, "end": v(-124.95, -4.86) * mm});
            skLineSegment(sketch, "E3600", {"start": v(-124.95, -4.86) * mm, "end": v(-124.86, -4.7) * mm});
            skLineSegment(sketch, "E3601", {"start": v(-124.86, -4.7) * mm, "end": v(-124.78, -4.52) * mm});
            skLineSegment(sketch, "E3602", {"start": v(-124.78, -4.52) * mm, "end": v(-124.71, -4.35) * mm});
            skLineSegment(sketch, "E3603", {"start": v(-124.71, -4.35) * mm, "end": v(-124.65, -4.16) * mm});
            skLineSegment(sketch, "E3604", {"start": v(-124.65, -4.16) * mm, "end": v(-124.6, -3.98) * mm});
            skLineSegment(sketch, "E3605", {"start": v(-124.6, -3.98) * mm, "end": v(-124.55, -3.78) * mm});
            skLineSegment(sketch, "E3606", {"start": v(-124.55, -3.78) * mm, "end": v(-124.5, -3.58) * mm});
            skLineSegment(sketch, "E3607", {"start": v(-124.5, -3.58) * mm, "end": v(-124.48, -3.38) * mm});
            skLineSegment(sketch, "E3608", {"start": v(-124.48, -3.38) * mm, "end": v(-124.46, -3.17) * mm});
            skLineSegment(sketch, "E3609", {"start": v(-124.46, -3.17) * mm, "end": v(-124.44, -2.95) * mm});
            skLineSegment(sketch, "E3610", {"start": v(-124.44, -2.95) * mm, "end": v(-124.44, -2.74) * mm});
            skLineSegment(sketch, "E3611", {"start": v(-124.44, -2.74) * mm, "end": v(-124.44, -2.52) * mm});
            skLineSegment(sketch, "E3612", {"start": v(-124.44, -2.52) * mm, "end": v(-124.46, -2.31) * mm});
            skLineSegment(sketch, "E3613", {"start": v(-124.46, -2.31) * mm, "end": v(-124.48, -2.1) * mm});
            skLineSegment(sketch, "E3614", {"start": v(-124.48, -2.1) * mm, "end": v(-124.5, -1.9) * mm});
            skLineSegment(sketch, "E3615", {"start": v(-124.5, -1.9) * mm, "end": v(-124.55, -1.71) * mm});
            skLineSegment(sketch, "E3616", {"start": v(-124.55, -1.71) * mm, "end": v(-124.6, -1.52) * mm});
            skLineSegment(sketch, "E3617", {"start": v(-124.6, -1.52) * mm, "end": v(-124.65, -1.34) * mm});
            skLineSegment(sketch, "E3618", {"start": v(-124.65, -1.34) * mm, "end": v(-124.72, -1.16) * mm});
            skLineSegment(sketch, "E3619", {"start": v(-124.72, -1.16) * mm, "end": v(-124.8, -0.98) * mm});
            skLineSegment(sketch, "E3620", {"start": v(-124.8, -0.98) * mm, "end": v(-124.87, -0.8) * mm});
            skLineSegment(sketch, "E3621", {"start": v(-124.87, -0.8) * mm, "end": v(-124.97, -0.64) * mm});
            skLineSegment(sketch, "E3622", {"start": v(-124.97, -0.64) * mm, "end": v(-125.07, -0.48) * mm});
            skLineSegment(sketch, "E3623", {"start": v(-125.07, -0.48) * mm, "end": v(-125.18, -0.33) * mm});
            skLineSegment(sketch, "E3624", {"start": v(-125.18, -0.33) * mm, "end": v(-125.3, -0.17) * mm});
            skLineSegment(sketch, "E3625", {"start": v(-125.3, -0.17) * mm, "end": v(-125.42, -0.03) * mm});
            skLineSegment(sketch, "E3626", {"start": v(-125.42, -0.03) * mm, "end": v(-125.55, 0.11) * mm});
            skLineSegment(sketch, "E3627", {"start": v(-125.55, 0.11) * mm, "end": v(-125.7, 0.25) * mm});
            skLineSegment(sketch, "E3628", {"start": v(-125.7, 0.25) * mm, "end": v(-125.84, 0.37) * mm});
            skLineSegment(sketch, "E3629", {"start": v(-125.84, 0.37) * mm, "end": v(-126, 0.5) * mm});
            skLineSegment(sketch, "E3630", {"start": v(-126, 0.5) * mm, "end": v(-126.15, 0.6) * mm});
            skLineSegment(sketch, "E3631", {"start": v(-126.15, 0.6) * mm, "end": v(-126.3, 0.7) * mm});
            skLineSegment(sketch, "E3632", {"start": v(-126.3, 0.7) * mm, "end": v(-126.48, 0.8) * mm});
            skLineSegment(sketch, "E3633", {"start": v(-126.48, 0.8) * mm, "end": v(-126.65, 0.87) * mm});
            skLineSegment(sketch, "E3634", {"start": v(-126.65, 0.87) * mm, "end": v(-126.82, 0.95) * mm});
            skLineSegment(sketch, "E3635", {"start": v(-126.82, 0.95) * mm, "end": v(-127, 1.01) * mm});
            skLineSegment(sketch, "E3636", {"start": v(-127, 1.01) * mm, "end": v(-127.19, 1.07) * mm});
            skLineSegment(sketch, "E3637", {"start": v(-127.19, 1.07) * mm, "end": v(-127.38, 1.12) * mm});
            skLineSegment(sketch, "E3638", {"start": v(-127.38, 1.12) * mm, "end": v(-127.57, 1.16) * mm});
            skLineSegment(sketch, "E3639", {"start": v(-127.57, 1.16) * mm, "end": v(-127.77, 1.19) * mm});
            skLineSegment(sketch, "E3640", {"start": v(-127.77, 1.19) * mm, "end": v(-127.98, 1.21) * mm});
            skLineSegment(sketch, "E3641", {"start": v(-127.98, 1.21) * mm, "end": v(-128.19, 1.22) * mm});
            skLineSegment(sketch, "E3642", {"start": v(-128.19, 1.22) * mm, "end": v(-128.4, 1.23) * mm});
            skLineSegment(sketch, "E3643", {"start": v(-128.4, 1.23) * mm, "end": v(-138.3, 1.23) * mm});
            skLineSegment(sketch, "E3644", {"start": v(-138.3, 1.23) * mm, "end": v(-138.49, 1.23) * mm});
            skLineSegment(sketch, "E3645", {"start": v(-138.49, 1.23) * mm, "end": v(-138.67, 1.24) * mm});
            skLineSegment(sketch, "E3646", {"start": v(-138.67, 1.24) * mm, "end": v(-138.85, 1.26) * mm});
            skLineSegment(sketch, "E3647", {"start": v(-138.85, 1.26) * mm, "end": v(-139.03, 1.29) * mm});
            skLineSegment(sketch, "E3648", {"start": v(-139.03, 1.29) * mm, "end": v(-139.2, 1.32) * mm});
            skLineSegment(sketch, "E3649", {"start": v(-139.2, 1.32) * mm, "end": v(-139.37, 1.36) * mm});
            skLineSegment(sketch, "E3650", {"start": v(-139.37, 1.36) * mm, "end": v(-139.53, 1.41) * mm});
            skLineSegment(sketch, "E3651", {"start": v(-139.53, 1.41) * mm, "end": v(-139.7, 1.47) * mm});
            skLineSegment(sketch, "E3652", {"start": v(-139.7, 1.47) * mm, "end": v(-139.85, 1.53) * mm});
            skLineSegment(sketch, "E3653", {"start": v(-139.85, 1.53) * mm, "end": v(-140, 1.6) * mm});
            skLineSegment(sketch, "E3654", {"start": v(-140, 1.6) * mm, "end": v(-140.14, 1.68) * mm});
            skLineSegment(sketch, "E3655", {"start": v(-140.14, 1.68) * mm, "end": v(-140.28, 1.76) * mm});
            skLineSegment(sketch, "E3656", {"start": v(-140.28, 1.76) * mm, "end": v(-140.42, 1.86) * mm});
            skLineSegment(sketch, "E3657", {"start": v(-140.42, 1.86) * mm, "end": v(-140.55, 1.96) * mm});
            skLineSegment(sketch, "E3658", {"start": v(-140.55, 1.96) * mm, "end": v(-140.67, 2.06) * mm});
            skLineSegment(sketch, "E3659", {"start": v(-140.67, 2.06) * mm, "end": v(-140.8, 2.18) * mm});
            skLineSegment(sketch, "E3660", {"start": v(-140.8, 2.18) * mm, "end": v(-140.9, 2.3) * mm});
            skLineSegment(sketch, "E3661", {"start": v(-140.9, 2.3) * mm, "end": v(-141.01, 2.42) * mm});
            skLineSegment(sketch, "E3662", {"start": v(-141.01, 2.42) * mm, "end": v(-141.11, 2.55) * mm});
            skLineSegment(sketch, "E3663", {"start": v(-141.11, 2.55) * mm, "end": v(-141.2, 2.69) * mm});
            skLineSegment(sketch, "E3664", {"start": v(-141.2, 2.69) * mm, "end": v(-141.3, 2.83) * mm});
            skLineSegment(sketch, "E3665", {"start": v(-141.3, 2.83) * mm, "end": v(-141.37, 2.97) * mm});
            skLineSegment(sketch, "E3666", {"start": v(-141.37, 2.97) * mm, "end": v(-141.44, 3.12) * mm});
            skLineSegment(sketch, "E3667", {"start": v(-141.44, 3.12) * mm, "end": v(-141.5, 3.28) * mm});
            skLineSegment(sketch, "E3668", {"start": v(-141.5, 3.28) * mm, "end": v(-141.56, 3.44) * mm});
            skLineSegment(sketch, "E3669", {"start": v(-141.56, 3.44) * mm, "end": v(-141.6, 3.6) * mm});
            skLineSegment(sketch, "E3670", {"start": v(-141.6, 3.6) * mm, "end": v(-141.65, 3.77) * mm});
            skLineSegment(sketch, "E3671", {"start": v(-141.65, 3.77) * mm, "end": v(-141.68, 3.94) * mm});
            skLineSegment(sketch, "E3672", {"start": v(-141.68, 3.94) * mm, "end": v(-141.7, 4.12) * mm});
            skLineSegment(sketch, "E3673", {"start": v(-141.7, 4.12) * mm, "end": v(-141.73, 4.3) * mm});
            skLineSegment(sketch, "E3674", {"start": v(-141.73, 4.3) * mm, "end": v(-141.74, 4.48) * mm});
            skLineSegment(sketch, "E3675", {"start": v(-141.74, 4.48) * mm, "end": v(-141.74, 4.67) * mm});
            skLineSegment(sketch, "E3676", {"start": v(-141.74, 4.67) * mm, "end": v(-141.74, 4.86) * mm});
            skLineSegment(sketch, "E3677", {"start": v(-141.74, 4.86) * mm, "end": v(-141.73, 5.05) * mm});
            skLineSegment(sketch, "E3678", {"start": v(-141.73, 5.05) * mm, "end": v(-141.7, 5.23) * mm});
            skLineSegment(sketch, "E3679", {"start": v(-141.7, 5.23) * mm, "end": v(-141.68, 5.4) * mm});
            skLineSegment(sketch, "E3680", {"start": v(-141.68, 5.4) * mm, "end": v(-141.65, 5.58) * mm});
            skLineSegment(sketch, "E3681", {"start": v(-141.65, 5.58) * mm, "end": v(-141.6, 5.75) * mm});
            skLineSegment(sketch, "E3682", {"start": v(-141.6, 5.75) * mm, "end": v(-141.56, 5.91) * mm});
            skLineSegment(sketch, "E3683", {"start": v(-141.56, 5.91) * mm, "end": v(-141.5, 6.07) * mm});
            skLineSegment(sketch, "E3684", {"start": v(-141.5, 6.07) * mm, "end": v(-141.44, 6.22) * mm});
            skLineSegment(sketch, "E3685", {"start": v(-141.44, 6.22) * mm, "end": v(-141.37, 6.37) * mm});
            skLineSegment(sketch, "E3686", {"start": v(-141.37, 6.37) * mm, "end": v(-141.3, 6.52) * mm});
            skLineSegment(sketch, "E3687", {"start": v(-141.3, 6.52) * mm, "end": v(-141.2, 6.66) * mm});
            skLineSegment(sketch, "E3688", {"start": v(-141.2, 6.66) * mm, "end": v(-141.11, 6.8) * mm});
            skLineSegment(sketch, "E3689", {"start": v(-141.11, 6.8) * mm, "end": v(-141.01, 6.92) * mm});
            skLineSegment(sketch, "E3690", {"start": v(-141.01, 6.92) * mm, "end": v(-140.9, 7.05) * mm});
            skLineSegment(sketch, "E3691", {"start": v(-140.9, 7.05) * mm, "end": v(-140.8, 7.17) * mm});
            skLineSegment(sketch, "E3692", {"start": v(-140.8, 7.17) * mm, "end": v(-140.67, 7.28) * mm});
            skLineSegment(sketch, "E3693", {"start": v(-140.67, 7.28) * mm, "end": v(-140.55, 7.4) * mm});
            skLineSegment(sketch, "E3694", {"start": v(-140.55, 7.4) * mm, "end": v(-140.42, 7.5) * mm});
            skLineSegment(sketch, "E3695", {"start": v(-140.42, 7.5) * mm, "end": v(-140.28, 7.58) * mm});
            skLineSegment(sketch, "E3696", {"start": v(-140.28, 7.58) * mm, "end": v(-140.14, 7.67) * mm});
            skLineSegment(sketch, "E3697", {"start": v(-140.14, 7.67) * mm, "end": v(-140, 7.75) * mm});
            skLineSegment(sketch, "E3698", {"start": v(-140, 7.75) * mm, "end": v(-139.85, 7.82) * mm});
            skLineSegment(sketch, "E3699", {"start": v(-139.85, 7.82) * mm, "end": v(-139.7, 7.88) * mm});
            skLineSegment(sketch, "E3700", {"start": v(-139.7, 7.88) * mm, "end": v(-139.53, 7.94) * mm});
            skLineSegment(sketch, "E3701", {"start": v(-139.53, 7.94) * mm, "end": v(-139.37, 7.98) * mm});
            skLineSegment(sketch, "E3702", {"start": v(-139.37, 7.98) * mm, "end": v(-139.2, 8.03) * mm});
            skLineSegment(sketch, "E3703", {"start": v(-139.2, 8.03) * mm, "end": v(-139.03, 8.06) * mm});
            skLineSegment(sketch, "E3704", {"start": v(-139.03, 8.06) * mm, "end": v(-138.85, 8.09) * mm});
            skLineSegment(sketch, "E3705", {"start": v(-138.85, 8.09) * mm, "end": v(-138.67, 8.1) * mm});
            skLineSegment(sketch, "E3706", {"start": v(-138.67, 8.1) * mm, "end": v(-138.49, 8.11) * mm});
            skLineSegment(sketch, "E3707", {"start": v(-138.49, 8.11) * mm, "end": v(-138.3, 8.12) * mm});
            skLineSegment(sketch, "E3708", {"start": v(-138.3, 8.12) * mm, "end": v(-123.48, 8.12) * mm});
            skLineSegment(sketch, "E3709", {"start": v(-123.48, 8.12) * mm, "end": v(-123.27, 8.12) * mm});
            skLineSegment(sketch, "E3710", {"start": v(-123.27, 8.12) * mm, "end": v(-123.06, 8.14) * mm});
            skLineSegment(sketch, "E3711", {"start": v(-123.06, 8.14) * mm, "end": v(-122.85, 8.16) * mm});
            skLineSegment(sketch, "E3712", {"start": v(-122.85, 8.16) * mm, "end": v(-122.65, 8.19) * mm});
            skLineSegment(sketch, "E3713", {"start": v(-122.65, 8.19) * mm, "end": v(-122.46, 8.23) * mm});
            skLineSegment(sketch, "E3714", {"start": v(-122.46, 8.23) * mm, "end": v(-122.26, 8.28) * mm});
            skLineSegment(sketch, "E3715", {"start": v(-122.26, 8.28) * mm, "end": v(-122.08, 8.33) * mm});
            skLineSegment(sketch, "E3716", {"start": v(-122.08, 8.33) * mm, "end": v(-121.9, 8.4) * mm});
            skLineSegment(sketch, "E3717", {"start": v(-121.9, 8.4) * mm, "end": v(-121.72, 8.47) * mm});
            skLineSegment(sketch, "E3718", {"start": v(-121.72, 8.47) * mm, "end": v(-121.54, 8.56) * mm});
            skLineSegment(sketch, "E3719", {"start": v(-121.54, 8.56) * mm, "end": v(-121.38, 8.65) * mm});
            skLineSegment(sketch, "E3720", {"start": v(-121.38, 8.65) * mm, "end": v(-121.21, 8.75) * mm});
            skLineSegment(sketch, "E3721", {"start": v(-121.21, 8.75) * mm, "end": v(-121.05, 8.85) * mm});
            skLineSegment(sketch, "E3722", {"start": v(-121.05, 8.85) * mm, "end": v(-120.9, 8.97) * mm});
            skLineSegment(sketch, "E3723", {"start": v(-120.9, 8.97) * mm, "end": v(-120.75, 9.1) * mm});
            skLineSegment(sketch, "E3724", {"start": v(-120.75, 9.1) * mm, "end": v(-120.6, 9.23) * mm});
            skLineSegment(sketch, "E3725", {"start": v(-120.6, 9.23) * mm, "end": v(-120.47, 9.37) * mm});
            skLineSegment(sketch, "E3726", {"start": v(-120.47, 9.37) * mm, "end": v(-120.34, 9.52) * mm});
            skLineSegment(sketch, "E3727", {"start": v(-120.34, 9.52) * mm, "end": v(-120.22, 9.67) * mm});
            skLineSegment(sketch, "E3728", {"start": v(-120.22, 9.67) * mm, "end": v(-120.1, 9.83) * mm});
            skLineSegment(sketch, "E3729", {"start": v(-120.1, 9.83) * mm, "end": v(-120, 9.99) * mm});
            skLineSegment(sketch, "E3730", {"start": v(-120, 9.99) * mm, "end": v(-119.91, 10.15) * mm});
            skLineSegment(sketch, "E3731", {"start": v(-119.91, 10.15) * mm, "end": v(-119.83, 10.33) * mm});
            skLineSegment(sketch, "E3732", {"start": v(-119.83, 10.33) * mm, "end": v(-119.75, 10.5) * mm});
            skLineSegment(sketch, "E3733", {"start": v(-119.75, 10.5) * mm, "end": v(-119.68, 10.68) * mm});
            skLineSegment(sketch, "E3734", {"start": v(-119.68, 10.68) * mm, "end": v(-119.63, 10.87) * mm});
            skLineSegment(sketch, "E3735", {"start": v(-119.63, 10.87) * mm, "end": v(-119.58, 11.06) * mm});
            skLineSegment(sketch, "E3736", {"start": v(-119.58, 11.06) * mm, "end": v(-119.54, 11.25) * mm});
            skLineSegment(sketch, "E3737", {"start": v(-119.54, 11.25) * mm, "end": v(-119.5, 11.45) * mm});
            skLineSegment(sketch, "E3738", {"start": v(-119.5, 11.45) * mm, "end": v(-119.48, 11.66) * mm});
            skLineSegment(sketch, "E3739", {"start": v(-119.48, 11.66) * mm, "end": v(-119.47, 11.87) * mm});
            skLineSegment(sketch, "E3740", {"start": v(-119.47, 11.87) * mm, "end": v(-119.46, 12.08) * mm});
            skLineSegment(sketch, "E3741", {"start": v(-119.46, 12.08) * mm, "end": v(-119.47, 12.3) * mm});
            skLineSegment(sketch, "E3742", {"start": v(-119.47, 12.3) * mm, "end": v(-119.48, 12.5) * mm});
            skLineSegment(sketch, "E3743", {"start": v(-119.48, 12.5) * mm, "end": v(-119.5, 12.7) * mm});
            skLineSegment(sketch, "E3744", {"start": v(-119.5, 12.7) * mm, "end": v(-119.54, 12.9) * mm});
            skLineSegment(sketch, "E3745", {"start": v(-119.54, 12.9) * mm, "end": v(-119.58, 13.1) * mm});
            skLineSegment(sketch, "E3746", {"start": v(-119.58, 13.1) * mm, "end": v(-119.63, 13.3) * mm});
            skLineSegment(sketch, "E3747", {"start": v(-119.63, 13.3) * mm, "end": v(-119.68, 13.48) * mm});
            skLineSegment(sketch, "E3748", {"start": v(-119.68, 13.48) * mm, "end": v(-119.75, 13.66) * mm});
            skLineSegment(sketch, "E3749", {"start": v(-119.75, 13.66) * mm, "end": v(-119.83, 13.84) * mm});
            skLineSegment(sketch, "E3750", {"start": v(-119.83, 13.84) * mm, "end": v(-119.91, 14) * mm});
            skLineSegment(sketch, "E3751", {"start": v(-119.91, 14) * mm, "end": v(-120, 14.17) * mm});
            skLineSegment(sketch, "E3752", {"start": v(-120, 14.17) * mm, "end": v(-120.1, 14.34) * mm});
            skLineSegment(sketch, "E3753", {"start": v(-120.1, 14.34) * mm, "end": v(-120.22, 14.5) * mm});
            skLineSegment(sketch, "E3754", {"start": v(-120.22, 14.5) * mm, "end": v(-120.34, 14.64) * mm});
            skLineSegment(sketch, "E3755", {"start": v(-120.34, 14.64) * mm, "end": v(-120.47, 14.79) * mm});
            skLineSegment(sketch, "E3756", {"start": v(-120.47, 14.79) * mm, "end": v(-120.6, 14.93) * mm});
            skLineSegment(sketch, "E3757", {"start": v(-120.6, 14.93) * mm, "end": v(-120.75, 15.07) * mm});
            skLineSegment(sketch, "E3758", {"start": v(-120.75, 15.07) * mm, "end": v(-120.9, 15.2) * mm});
            skLineSegment(sketch, "E3759", {"start": v(-120.9, 15.2) * mm, "end": v(-121.05, 15.3) * mm});
            skLineSegment(sketch, "E3760", {"start": v(-121.05, 15.3) * mm, "end": v(-121.21, 15.42) * mm});
            skLineSegment(sketch, "E3761", {"start": v(-121.21, 15.42) * mm, "end": v(-121.38, 15.52) * mm});
            skLineSegment(sketch, "E3762", {"start": v(-121.38, 15.52) * mm, "end": v(-121.54, 15.6) * mm});
            skLineSegment(sketch, "E3763", {"start": v(-121.54, 15.6) * mm, "end": v(-121.72, 15.7) * mm});
            skLineSegment(sketch, "E3764", {"start": v(-121.72, 15.7) * mm, "end": v(-121.9, 15.76) * mm});
            skLineSegment(sketch, "E3765", {"start": v(-121.9, 15.76) * mm, "end": v(-122.08, 15.83) * mm});
            skLineSegment(sketch, "E3766", {"start": v(-122.08, 15.83) * mm, "end": v(-122.26, 15.89) * mm});
            skLineSegment(sketch, "E3767", {"start": v(-122.26, 15.89) * mm, "end": v(-122.46, 15.94) * mm});
            skLineSegment(sketch, "E3768", {"start": v(-122.46, 15.94) * mm, "end": v(-122.65, 15.97) * mm});
            skLineSegment(sketch, "E3769", {"start": v(-122.65, 15.97) * mm, "end": v(-122.85, 16) * mm});
            skLineSegment(sketch, "E3770", {"start": v(-122.85, 16) * mm, "end": v(-123.06, 16.03) * mm});
            skLineSegment(sketch, "E3771", {"start": v(-123.06, 16.03) * mm, "end": v(-123.27, 16.04) * mm});
            skLineSegment(sketch, "E3772", {"start": v(-123.27, 16.04) * mm, "end": v(-123.48, 16.04) * mm});
            skLineSegment(sketch, "E3773", {"start": v(-123.48, 16.04) * mm, "end": v(-146.51, 16.04) * mm});
            skLineSegment(sketch, "E3774", {"start": v(-146.51, 16.04) * mm, "end": v(-146.83, 16.03) * mm});
            skLineSegment(sketch, "E3775", {"start": v(-146.83, 16.03) * mm, "end": v(-147.15, 15.98) * mm});
            skLineSegment(sketch, "E3776", {"start": v(-147.15, 15.98) * mm, "end": v(-147.45, 15.9) * mm});
            skLineSegment(sketch, "E3777", {"start": v(-147.45, 15.9) * mm, "end": v(-147.74, 15.8) * mm});
            skLineSegment(sketch, "E3778", {"start": v(-147.74, 15.8) * mm, "end": v(-148.02, 15.66) * mm});
            skLineSegment(sketch, "E3779", {"start": v(-148.02, 15.66) * mm, "end": v(-148.28, 15.5) * mm});
            skLineSegment(sketch, "E3780", {"start": v(-148.28, 15.5) * mm, "end": v(-148.52, 15.32) * mm});
            skLineSegment(sketch, "E3781", {"start": v(-148.52, 15.32) * mm, "end": v(-148.74, 15.12) * mm});
            skLineSegment(sketch, "E3782", {"start": v(-148.74, 15.12) * mm, "end": v(-148.95, 14.9) * mm});
            skLineSegment(sketch, "E3783", {"start": v(-148.95, 14.9) * mm, "end": v(-149.13, 14.65) * mm});
            skLineSegment(sketch, "E3784", {"start": v(-149.13, 14.65) * mm, "end": v(-149.29, 14.4) * mm});
            skLineSegment(sketch, "E3785", {"start": v(-149.29, 14.4) * mm, "end": v(-149.42, 14.12) * mm});
            skLineSegment(sketch, "E3786", {"start": v(-149.42, 14.12) * mm, "end": v(-149.53, 13.83) * mm});
            skLineSegment(sketch, "E3787", {"start": v(-149.53, 13.83) * mm, "end": v(-149.6, 13.52) * mm});
            skLineSegment(sketch, "E3788", {"start": v(-149.6, 13.52) * mm, "end": v(-149.65, 13.21) * mm});
            skLineSegment(sketch, "E3789", {"start": v(-149.65, 13.21) * mm, "end": v(-149.67, 12.89) * mm});
            skLineSegment(sketch, "E3790", {"start": v(-149.67, 12.89) * mm, "end": v(-149.67, -22.53) * mm});
            skLineSegment(sketch, "E3791", {"start": v(-149.67, -22.53) * mm, "end": v(-149.67, -22.64) * mm});
            skLineSegment(sketch, "E3792", {"start": v(-149.67, -22.64) * mm, "end": v(-149.68, -22.74) * mm});
            skLineSegment(sketch, "E3793", {"start": v(-149.68, -22.74) * mm, "end": v(-149.7, -22.84) * mm});
            skLineSegment(sketch, "E3794", {"start": v(-149.7, -22.84) * mm, "end": v(-149.73, -22.93) * mm});
            skLineSegment(sketch, "E3795", {"start": v(-149.73, -22.93) * mm, "end": v(-149.77, -23.01) * mm});
            skLineSegment(sketch, "E3796", {"start": v(-149.77, -23.01) * mm, "end": v(-149.8, -23.09) * mm});
            skLineSegment(sketch, "E3797", {"start": v(-149.8, -23.09) * mm, "end": v(-149.86, -23.16) * mm});
            skLineSegment(sketch, "E3798", {"start": v(-149.86, -23.16) * mm, "end": v(-149.92, -23.22) * mm});
            skLineSegment(sketch, "E3799", {"start": v(-149.92, -23.22) * mm, "end": v(-149.99, -23.28) * mm});
            skLineSegment(sketch, "E3800", {"start": v(-149.99, -23.28) * mm, "end": v(-150.06, -23.33) * mm});
            skLineSegment(sketch, "E3801", {"start": v(-150.06, -23.33) * mm, "end": v(-150.14, -23.37) * mm});
            skLineSegment(sketch, "E3802", {"start": v(-150.14, -23.37) * mm, "end": v(-150.23, -23.4) * mm});
            skLineSegment(sketch, "E3803", {"start": v(-150.23, -23.4) * mm, "end": v(-150.33, -23.44) * mm});
            skLineSegment(sketch, "E3804", {"start": v(-150.33, -23.44) * mm, "end": v(-150.44, -23.46) * mm});
            skLineSegment(sketch, "E3805", {"start": v(-150.44, -23.46) * mm, "end": v(-150.56, -23.47) * mm});
            skLineSegment(sketch, "E3806", {"start": v(-150.56, -23.47) * mm, "end": v(-150.68, -23.48) * mm});
            skLineSegment(sketch, "E3807", {"start": v(-150.68, -23.48) * mm, "end": v(-153.84, -23.48) * mm});
            skLineSegment(sketch, "E3808", {"start": v(-153.84, -23.48) * mm, "end": v(-153.9, -23.48) * mm});
            skLineSegment(sketch, "E3809", {"start": v(-153.9, -23.48) * mm, "end": v(-153.97, -23.47) * mm});
            skLineSegment(sketch, "E3810", {"start": v(-153.97, -23.47) * mm, "end": v(-154.03, -23.45) * mm});
            skLineSegment(sketch, "E3811", {"start": v(-154.03, -23.45) * mm, "end": v(-154.1, -23.43) * mm});
            skLineSegment(sketch, "E3812", {"start": v(-154.1, -23.43) * mm, "end": v(-154.15, -23.4) * mm});
            skLineSegment(sketch, "E3813", {"start": v(-154.15, -23.4) * mm, "end": v(-154.2, -23.37) * mm});
            skLineSegment(sketch, "E3814", {"start": v(-154.2, -23.37) * mm, "end": v(-154.26, -23.33) * mm});
            skLineSegment(sketch, "E3815", {"start": v(-154.26, -23.33) * mm, "end": v(-154.3, -23.3) * mm});
            skLineSegment(sketch, "E3816", {"start": v(-154.3, -23.3) * mm, "end": v(-154.34, -23.25) * mm});
            skLineSegment(sketch, "E3817", {"start": v(-154.34, -23.25) * mm, "end": v(-154.38, -23.2) * mm});
            skLineSegment(sketch, "E3818", {"start": v(-154.38, -23.2) * mm, "end": v(-154.42, -23.14) * mm});
            skLineSegment(sketch, "E3819", {"start": v(-154.42, -23.14) * mm, "end": v(-154.44, -23.08) * mm});
            skLineSegment(sketch, "E3820", {"start": v(-154.44, -23.08) * mm, "end": v(-154.46, -23.02) * mm});
            skLineSegment(sketch, "E3821", {"start": v(-154.46, -23.02) * mm, "end": v(-154.48, -22.96) * mm});
            skLineSegment(sketch, "E3822", {"start": v(-154.48, -22.96) * mm, "end": v(-154.5, -22.9) * mm});
            skLineSegment(sketch, "E3823", {"start": v(-154.5, -22.9) * mm, "end": v(-154.5, -22.83) * mm});
            skLineSegment(sketch, "E3824", {"start": v(-154.5, -22.83) * mm, "end": v(-154.5, 12.07) * mm});
            skLineSegment(sketch, "E3825", {"start": v(-154.5, 12.07) * mm, "end": v(-154.5, 12.3) * mm});
            skLineSegment(sketch, "E3826", {"start": v(-154.5, 12.3) * mm, "end": v(-154.51, 12.5) * mm});
            skLineSegment(sketch, "E3827", {"start": v(-154.51, 12.5) * mm, "end": v(-154.53, 12.72) * mm});
            skLineSegment(sketch, "E3828", {"start": v(-154.53, 12.72) * mm, "end": v(-154.56, 12.92) * mm});
            skLineSegment(sketch, "E3829", {"start": v(-154.56, 12.92) * mm, "end": v(-154.6, 13.12) * mm});
            skLineSegment(sketch, "E3830", {"start": v(-154.6, 13.12) * mm, "end": v(-154.65, 13.31) * mm});
            skLineSegment(sketch, "E3831", {"start": v(-154.65, 13.31) * mm, "end": v(-154.7, 13.5) * mm});
            skLineSegment(sketch, "E3832", {"start": v(-154.7, 13.5) * mm, "end": v(-154.77, 13.69) * mm});
            skLineSegment(sketch, "E3833", {"start": v(-154.77, 13.69) * mm, "end": v(-154.84, 13.86) * mm});
            skLineSegment(sketch, "E3834", {"start": v(-154.84, 13.86) * mm, "end": v(-154.92, 14.04) * mm});
            skLineSegment(sketch, "E3835", {"start": v(-154.92, 14.04) * mm, "end": v(-155, 14.2) * mm});
            skLineSegment(sketch, "E3836", {"start": v(-155, 14.2) * mm, "end": v(-155.1, 14.36) * mm});
            skLineSegment(sketch, "E3837", {"start": v(-155.1, 14.36) * mm, "end": v(-155.2, 14.52) * mm});
            skLineSegment(sketch, "E3838", {"start": v(-155.2, 14.52) * mm, "end": v(-155.32, 14.67) * mm});
            skLineSegment(sketch, "E3839", {"start": v(-155.32, 14.67) * mm, "end": v(-155.44, 14.81) * mm});
            skLineSegment(sketch, "E3840", {"start": v(-155.44, 14.81) * mm, "end": v(-155.57, 14.95) * mm});
            skLineSegment(sketch, "E3841", {"start": v(-155.57, 14.95) * mm, "end": v(-155.71, 15.08) * mm});
            skLineSegment(sketch, "E3842", {"start": v(-155.71, 15.08) * mm, "end": v(-155.85, 15.2) * mm});
            skLineSegment(sketch, "E3843", {"start": v(-155.85, 15.2) * mm, "end": v(-156, 15.32) * mm});
            skLineSegment(sketch, "E3844", {"start": v(-156, 15.32) * mm, "end": v(-156.16, 15.43) * mm});
            skLineSegment(sketch, "E3845", {"start": v(-156.16, 15.43) * mm, "end": v(-156.32, 15.53) * mm});
            skLineSegment(sketch, "E3846", {"start": v(-156.32, 15.53) * mm, "end": v(-156.48, 15.62) * mm});
            skLineSegment(sketch, "E3847", {"start": v(-156.48, 15.62) * mm, "end": v(-156.65, 15.7) * mm});
            skLineSegment(sketch, "E3848", {"start": v(-156.65, 15.7) * mm, "end": v(-156.83, 15.77) * mm});
            skLineSegment(sketch, "E3849", {"start": v(-156.83, 15.77) * mm, "end": v(-157.01, 15.83) * mm});
            skLineSegment(sketch, "E3850", {"start": v(-157.01, 15.83) * mm, "end": v(-157.2, 15.9) * mm});
            skLineSegment(sketch, "E3851", {"start": v(-157.2, 15.9) * mm, "end": v(-157.4, 15.94) * mm});
            skLineSegment(sketch, "E3852", {"start": v(-157.4, 15.94) * mm, "end": v(-157.59, 15.98) * mm});
            skLineSegment(sketch, "E3853", {"start": v(-157.59, 15.98) * mm, "end": v(-157.8, 16) * mm});
            skLineSegment(sketch, "E3854", {"start": v(-157.8, 16) * mm, "end": v(-158, 16.03) * mm});
            skLineSegment(sketch, "E3855", {"start": v(-158, 16.03) * mm, "end": v(-158.21, 16.04) * mm});
            skLineSegment(sketch, "E3856", {"start": v(-158.21, 16.04) * mm, "end": v(-158.43, 16.04) * mm});
            skLineSegment(sketch, "E3857", {"start": v(-158.43, 16.04) * mm, "end": v(-158.64, 16.04) * mm});
            skLineSegment(sketch, "E3858", {"start": v(-158.64, 16.04) * mm, "end": v(-158.85, 16.03) * mm});
            skLineSegment(sketch, "E3859", {"start": v(-158.85, 16.03) * mm, "end": v(-159.05, 16) * mm});
            skLineSegment(sketch, "E3860", {"start": v(-159.05, 16) * mm, "end": v(-159.25, 15.97) * mm});
            skLineSegment(sketch, "E3861", {"start": v(-159.25, 15.97) * mm, "end": v(-159.45, 15.93) * mm});
            skLineSegment(sketch, "E3862", {"start": v(-159.45, 15.93) * mm, "end": v(-159.64, 15.89) * mm});
            skLineSegment(sketch, "E3863", {"start": v(-159.64, 15.89) * mm, "end": v(-159.82, 15.83) * mm});
            skLineSegment(sketch, "E3864", {"start": v(-159.82, 15.83) * mm, "end": v(-160, 15.76) * mm});
            skLineSegment(sketch, "E3865", {"start": v(-160, 15.76) * mm, "end": v(-160.17, 15.69) * mm});
            skLineSegment(sketch, "E3866", {"start": v(-160.17, 15.69) * mm, "end": v(-160.34, 15.6) * mm});
            skLineSegment(sketch, "E3867", {"start": v(-160.34, 15.6) * mm, "end": v(-160.5, 15.51) * mm});
            skLineSegment(sketch, "E3868", {"start": v(-160.5, 15.51) * mm, "end": v(-160.67, 15.41) * mm});
            skLineSegment(sketch, "E3869", {"start": v(-160.67, 15.41) * mm, "end": v(-160.83, 15.3) * mm});
            skLineSegment(sketch, "E3870", {"start": v(-160.83, 15.3) * mm, "end": v(-160.98, 15.19) * mm});
            skLineSegment(sketch, "E3871", {"start": v(-160.98, 15.19) * mm, "end": v(-161.12, 15.06) * mm});
            skLineSegment(sketch, "E3872", {"start": v(-161.12, 15.06) * mm, "end": v(-161.26, 14.93) * mm});
            skLineSegment(sketch, "E3873", {"start": v(-161.26, 14.93) * mm, "end": v(-161.4, 14.79) * mm});
            skLineSegment(sketch, "E3874", {"start": v(-161.4, 14.79) * mm, "end": v(-161.52, 14.64) * mm});
            skLineSegment(sketch, "E3875", {"start": v(-161.52, 14.64) * mm, "end": v(-161.64, 14.49) * mm});
            skLineSegment(sketch, "E3876", {"start": v(-161.64, 14.49) * mm, "end": v(-161.74, 14.33) * mm});
            skLineSegment(sketch, "E3877", {"start": v(-161.74, 14.33) * mm, "end": v(-161.84, 14.17) * mm});
            skLineSegment(sketch, "E3878", {"start": v(-161.84, 14.17) * mm, "end": v(-161.93, 14) * mm});
            skLineSegment(sketch, "E3879", {"start": v(-161.93, 14) * mm, "end": v(-162.02, 13.83) * mm});
            skLineSegment(sketch, "E3880", {"start": v(-162.02, 13.83) * mm, "end": v(-162.09, 13.65) * mm});
            skLineSegment(sketch, "E3881", {"start": v(-162.09, 13.65) * mm, "end": v(-162.15, 13.47) * mm});
            skLineSegment(sketch, "E3882", {"start": v(-162.15, 13.47) * mm, "end": v(-162.21, 13.29) * mm});
            skLineSegment(sketch, "E3883", {"start": v(-162.21, 13.29) * mm, "end": v(-162.26, 13.1) * mm});
            skLineSegment(sketch, "E3884", {"start": v(-162.26, 13.1) * mm, "end": v(-162.3, 12.9) * mm});
            skLineSegment(sketch, "E3885", {"start": v(-162.3, 12.9) * mm, "end": v(-162.33, 12.7) * mm});
            skLineSegment(sketch, "E3886", {"start": v(-162.33, 12.7) * mm, "end": v(-162.35, 12.5) * mm});
            skLineSegment(sketch, "E3887", {"start": v(-162.35, 12.5) * mm, "end": v(-162.36, 12.28) * mm});
            skLineSegment(sketch, "E3888", {"start": v(-162.36, 12.28) * mm, "end": v(-162.37, 12.07) * mm});
            skLineSegment(sketch, "E3889", {"start": v(-162.37, 12.07) * mm, "end": v(-162.37, -18.54) * mm});
            skLineSegment(sketch, "E3890", {"start": v(-162.37, -18.54) * mm, "end": v(-162.37, -18.54) * mm});
            skLineSegment(sketch, "E3891", {"start": v(-162.37, -18.54) * mm, "end": v(-162.37, -18.55) * mm});
            skLineSegment(sketch, "E3892", {"start": v(-162.37, -18.55) * mm, "end": v(-162.37, -18.55) * mm});
            skLineSegment(sketch, "E3893", {"start": v(-162.37, -18.55) * mm, "end": v(-162.37, -18.56) * mm});
            skLineSegment(sketch, "E3894", {"start": v(-162.37, -18.56) * mm, "end": v(-162.37, -18.56) * mm});
            skLineSegment(sketch, "E3895", {"start": v(-162.37, -18.56) * mm, "end": v(-162.38, -18.56) * mm});
            skLineSegment(sketch, "E3896", {"start": v(-162.38, -18.56) * mm, "end": v(-162.38, -18.56) * mm});
            skLineSegment(sketch, "E3897", {"start": v(-162.38, -18.56) * mm, "end": v(-162.39, -18.56) * mm});
            skLineSegment(sketch, "E3898", {"start": v(-162.39, -18.56) * mm, "end": v(-162.39, -18.56) * mm});
            skLineSegment(sketch, "E3899", {"start": v(-162.39, -18.56) * mm, "end": v(-162.4, -18.56) * mm});
            skLineSegment(sketch, "E3900", {"start": v(-162.4, -18.56) * mm, "end": v(-162.4, -18.56) * mm});
            skLineSegment(sketch, "E3901", {"start": v(-162.4, -18.56) * mm, "end": v(-162.41, -18.56) * mm});
            skLineSegment(sketch, "E3902", {"start": v(-162.41, -18.56) * mm, "end": v(-162.41, -18.56) * mm});
            skLineSegment(sketch, "E3903", {"start": v(-162.41, -18.56) * mm, "end": v(-162.42, -18.56) * mm});
            skLineSegment(sketch, "E3904", {"start": v(-162.42, -18.56) * mm, "end": v(-162.42, -18.56) * mm});
            skLineSegment(sketch, "E3905", {"start": v(-162.42, -18.56) * mm, "end": v(-162.42, -18.55) * mm});
            skLineSegment(sketch, "E3906", {"start": v(-162.42, -18.55) * mm, "end": v(-179.18, 14.87) * mm});
            skLineSegment(sketch, "E3907", {"start": v(-179.18, 14.87) * mm, "end": v(-179.24, 14.98) * mm});
            skLineSegment(sketch, "E3908", {"start": v(-179.24, 14.98) * mm, "end": v(-179.3, 15.1) * mm});
            skLineSegment(sketch, "E3909", {"start": v(-179.3, 15.1) * mm, "end": v(-179.37, 15.21) * mm});
            skLineSegment(sketch, "E3910", {"start": v(-179.37, 15.21) * mm, "end": v(-179.45, 15.33) * mm});
            skLineSegment(sketch, "E3911", {"start": v(-179.45, 15.33) * mm, "end": v(-179.53, 15.44) * mm});
            skLineSegment(sketch, "E3912", {"start": v(-179.53, 15.44) * mm, "end": v(-179.62, 15.55) * mm});
            skLineSegment(sketch, "E3913", {"start": v(-179.62, 15.55) * mm, "end": v(-179.72, 15.65) * mm});
            skLineSegment(sketch, "E3914", {"start": v(-179.72, 15.65) * mm, "end": v(-179.82, 15.75) * mm});
            skLineSegment(sketch, "E3915", {"start": v(-179.82, 15.75) * mm, "end": v(-179.93, 15.83) * mm});
            skLineSegment(sketch, "E3916", {"start": v(-179.93, 15.83) * mm, "end": v(-180.05, 15.9) * mm});
            skLineSegment(sketch, "E3917", {"start": v(-180.05, 15.9) * mm, "end": v(-180.18, 15.96) * mm});
            skLineSegment(sketch, "E3918", {"start": v(-180.18, 15.96) * mm, "end": v(-180.32, 16) * mm});
            skLineSegment(sketch, "E3919", {"start": v(-180.32, 16) * mm, "end": v(-180.47, 16.04) * mm});
            skLineSegment(sketch, "E3920", {"start": v(-180.47, 16.04) * mm, "end": v(-180.63, 16.05) * mm});
            skLineSegment(sketch, "E3921", {"start": v(-180.63, 16.05) * mm, "end": v(-180.67, 16.05) * mm});
            skLineSegment(sketch, "E3922", {"start": v(-180.67, 16.05) * mm, "end": v(-180.7, 16.04) * mm});
            skLineSegment(sketch, "E3923", {"start": v(-180.7, 16.04) * mm, "end": v(-180.73, 16.04) * mm});
            skLineSegment(sketch, "E3924", {"start": v(-180.73, 16.04) * mm, "end": v(-180.75, 16.04) * mm});
            skLineSegment(sketch, "E3925", {"start": v(-180.75, 16.04) * mm, "end": v(-180.76, 16.04) * mm});
            skLineSegment(sketch, "E3926", {"start": v(-180.76, 16.04) * mm, "end": v(-180.78, 16.04) * mm});
            skLineSegment(sketch, "E3927", {"start": v(-180.78, 16.04) * mm, "end": v(-180.83, 16.04) * mm});
            skLineSegment(sketch, "E3928", {"start": v(-180.83, 16.04) * mm, "end": v(-180.98, 16.03) * mm});
            skLineSegment(sketch, "E3929", {"start": v(-180.98, 16.03) * mm, "end": v(-181.12, 16) * mm});
            skLineSegment(sketch, "E3930", {"start": v(-181.12, 16) * mm, "end": v(-181.25, 15.96) * mm});
            skLineSegment(sketch, "E3931", {"start": v(-181.25, 15.96) * mm, "end": v(-181.37, 15.9) * mm});
            skLineSegment(sketch, "E3932", {"start": v(-181.37, 15.9) * mm, "end": v(-181.49, 15.83) * mm});
            skLineSegment(sketch, "E3933", {"start": v(-181.49, 15.83) * mm, "end": v(-181.59, 15.75) * mm});
            skLineSegment(sketch, "E3934", {"start": v(-181.59, 15.75) * mm, "end": v(-181.68, 15.66) * mm});
            skLineSegment(sketch, "E3935", {"start": v(-181.68, 15.66) * mm, "end": v(-181.77, 15.56) * mm});
            skLineSegment(sketch, "E3936", {"start": v(-181.77, 15.56) * mm, "end": v(-181.84, 15.45) * mm});
            skLineSegment(sketch, "E3937", {"start": v(-181.84, 15.45) * mm, "end": v(-181.9, 15.34) * mm});
            skLineSegment(sketch, "E3938", {"start": v(-181.9, 15.34) * mm, "end": v(-181.96, 15.23) * mm});
            skLineSegment(sketch, "E3939", {"start": v(-181.96, 15.23) * mm, "end": v(-182.01, 15.12) * mm});
            skLineSegment(sketch, "E3940", {"start": v(-182.01, 15.12) * mm, "end": v(-182.05, 15) * mm});
            skLineSegment(sketch, "E3941", {"start": v(-182.05, 15) * mm, "end": v(-182.08, 14.88) * mm});
            skLineSegment(sketch, "E3942", {"start": v(-182.08, 14.88) * mm, "end": v(-182.1, 14.77) * mm});
            skLineSegment(sketch, "E3943", {"start": v(-182.1, 14.77) * mm, "end": v(-182.1, 14.67) * mm});
            skLineSegment(sketch, "E3944", {"start": v(-182.1, 14.67) * mm, "end": v(-182.1, -22.83) * mm});
            skLineSegment(sketch, "E3945", {"start": v(-182.1, -22.83) * mm, "end": v(-182.1, -22.9) * mm});
            skLineSegment(sketch, "E3946", {"start": v(-182.1, -22.9) * mm, "end": v(-182.12, -22.96) * mm});
            skLineSegment(sketch, "E3947", {"start": v(-182.12, -22.96) * mm, "end": v(-182.13, -23.02) * mm});
            skLineSegment(sketch, "E3948", {"start": v(-182.13, -23.02) * mm, "end": v(-182.16, -23.08) * mm});
            skLineSegment(sketch, "E3949", {"start": v(-182.16, -23.08) * mm, "end": v(-182.18, -23.14) * mm});
            skLineSegment(sketch, "E3950", {"start": v(-182.18, -23.14) * mm, "end": v(-182.22, -23.2) * mm});
            skLineSegment(sketch, "E3951", {"start": v(-182.22, -23.2) * mm, "end": v(-182.26, -23.25) * mm});
            skLineSegment(sketch, "E3952", {"start": v(-182.26, -23.25) * mm, "end": v(-182.3, -23.3) * mm});
            skLineSegment(sketch, "E3953", {"start": v(-182.3, -23.3) * mm, "end": v(-182.34, -23.33) * mm});
            skLineSegment(sketch, "E3954", {"start": v(-182.34, -23.33) * mm, "end": v(-182.4, -23.37) * mm});
            skLineSegment(sketch, "E3955", {"start": v(-182.4, -23.37) * mm, "end": v(-182.45, -23.4) * mm});
            skLineSegment(sketch, "E3956", {"start": v(-182.45, -23.4) * mm, "end": v(-182.5, -23.43) * mm});
            skLineSegment(sketch, "E3957", {"start": v(-182.5, -23.43) * mm, "end": v(-182.57, -23.45) * mm});
            skLineSegment(sketch, "E3958", {"start": v(-182.57, -23.45) * mm, "end": v(-182.63, -23.47) * mm});
            skLineSegment(sketch, "E3959", {"start": v(-182.63, -23.47) * mm, "end": v(-182.7, -23.48) * mm});
            skLineSegment(sketch, "E3960", {"start": v(-182.7, -23.48) * mm, "end": v(-182.76, -23.48) * mm});
            skLineSegment(sketch, "E3961", {"start": v(-182.76, -23.48) * mm, "end": v(-184.5, -23.48) * mm});
            skLineSegment(sketch, "E3962", {"start": v(-184.5, -23.48) * mm, "end": v(-184.53, -23.52) * mm});
            skLineSegment(sketch, "E3963", {"start": v(-184.53, -23.52) * mm, "end": v(-192.86, -23.52) * mm});
            skLineSegment(sketch, "E3964", {"start": v(-192.86, -23.52) * mm, "end": v(-193.43, -23.5) * mm});
            skLineSegment(sketch, "E3965", {"start": v(-193.43, -23.5) * mm, "end": v(-193.99, -23.4) * mm});
            skLineSegment(sketch, "E3966", {"start": v(-193.99, -23.4) * mm, "end": v(-194.53, -23.27) * mm});
            skLineSegment(sketch, "E3967", {"start": v(-194.53, -23.27) * mm, "end": v(-195.05, -23.08) * mm});
            skLineSegment(sketch, "E3968", {"start": v(-195.05, -23.08) * mm, "end": v(-195.54, -22.84) * mm});
            skLineSegment(sketch, "E3969", {"start": v(-195.54, -22.84) * mm, "end": v(-196, -22.56) * mm});
            skLineSegment(sketch, "E3970", {"start": v(-196, -22.56) * mm, "end": v(-196.44, -22.23) * mm});
            skLineSegment(sketch, "E3971", {"start": v(-196.44, -22.23) * mm, "end": v(-196.84, -21.87) * mm});
            skLineSegment(sketch, "E3972", {"start": v(-196.84, -21.87) * mm, "end": v(-197.2, -21.47) * mm});
            skLineSegment(sketch, "E3973", {"start": v(-197.2, -21.47) * mm, "end": v(-197.53, -21.03) * mm});
            skLineSegment(sketch, "E3974", {"start": v(-197.53, -21.03) * mm, "end": v(-197.8, -20.57) * mm});
            skLineSegment(sketch, "E3975", {"start": v(-197.8, -20.57) * mm, "end": v(-198.05, -20.08) * mm});
            skLineSegment(sketch, "E3976", {"start": v(-198.05, -20.08) * mm, "end": v(-198.24, -19.56) * mm});
            skLineSegment(sketch, "E3977", {"start": v(-198.24, -19.56) * mm, "end": v(-198.37, -19.02) * mm});
            skLineSegment(sketch, "E3978", {"start": v(-198.37, -19.02) * mm, "end": v(-198.46, -18.46) * mm});
            skLineSegment(sketch, "E3979", {"start": v(-198.46, -18.46) * mm, "end": v(-198.49, -17.89) * mm});
            skLineSegment(sketch, "E3980", {"start": v(-198.49, -17.89) * mm, "end": v(-198.49, 17.82) * mm});
            skLineSegment(sketch, "E3981", {"start": v(-198.49, 17.82) * mm, "end": v(-198.46, 18.4) * mm});
            skLineSegment(sketch, "E3982", {"start": v(-198.46, 18.4) * mm, "end": v(-198.37, 18.96) * mm});
            skLineSegment(sketch, "E3983", {"start": v(-198.37, 18.96) * mm, "end": v(-198.24, 19.5) * mm});
            skLineSegment(sketch, "E3984", {"start": v(-198.24, 19.5) * mm, "end": v(-198.05, 20.02) * mm});
            skLineSegment(sketch, "E3985", {"start": v(-198.05, 20.02) * mm, "end": v(-197.8, 20.5) * mm});
            skLineSegment(sketch, "E3986", {"start": v(-197.8, 20.5) * mm, "end": v(-197.53, 20.97) * mm});
            skLineSegment(sketch, "E3987", {"start": v(-197.53, 20.97) * mm, "end": v(-197.2, 21.4) * mm});
            skLineSegment(sketch, "E3988", {"start": v(-197.2, 21.4) * mm, "end": v(-196.84, 21.8) * mm});
            skLineSegment(sketch, "E3989", {"start": v(-196.84, 21.8) * mm, "end": v(-196.44, 22.17) * mm});
            skLineSegment(sketch, "E3990", {"start": v(-196.44, 22.17) * mm, "end": v(-196, 22.5) * mm});
            skLineSegment(sketch, "E3991", {"start": v(-196, 22.5) * mm, "end": v(-195.54, 22.78) * mm});
            skLineSegment(sketch, "E3992", {"start": v(-195.54, 22.78) * mm, "end": v(-195.05, 23.01) * mm});
            skLineSegment(sketch, "E3993", {"start": v(-195.05, 23.01) * mm, "end": v(-194.53, 23.2) * mm});
            skLineSegment(sketch, "E3994", {"start": v(-194.53, 23.2) * mm, "end": v(-193.99, 23.34) * mm});
            skLineSegment(sketch, "E3995", {"start": v(-193.99, 23.34) * mm, "end": v(-193.43, 23.43) * mm});
            skLineSegment(sketch, "E3996", {"start": v(-193.43, 23.43) * mm, "end": v(-192.86, 23.46) * mm});
            skLineSegment(sketch, "E3997", {"start": v(-192.86, 23.46) * mm, "end": v(192.86, 23.46) * mm});
            skLineSegment(sketch, "E3998", {"start": v(192.86, 23.46) * mm, "end": v(193.43, 23.43) * mm});
            skLineSegment(sketch, "E3999", {"start": v(193.43, 23.43) * mm, "end": v(193.99, 23.34) * mm});
            skLineSegment(sketch, "E4000", {"start": v(193.99, 23.34) * mm, "end": v(194.53, 23.2) * mm});
            skLineSegment(sketch, "E4001", {"start": v(194.53, 23.2) * mm, "end": v(195.05, 23.01) * mm});
            skLineSegment(sketch, "E4002", {"start": v(195.05, 23.01) * mm, "end": v(195.54, 22.78) * mm});
            skLineSegment(sketch, "E4003", {"start": v(195.54, 22.78) * mm, "end": v(196, 22.5) * mm});
            skLineSegment(sketch, "E4004", {"start": v(196, 22.5) * mm, "end": v(196.44, 22.17) * mm});
            skLineSegment(sketch, "E4005", {"start": v(196.44, 22.17) * mm, "end": v(196.84, 21.8) * mm});
            skLineSegment(sketch, "E4006", {"start": v(196.84, 21.8) * mm, "end": v(197.2, 21.4) * mm});
            skLineSegment(sketch, "E4007", {"start": v(197.2, 21.4) * mm, "end": v(197.53, 20.97) * mm});
            skLineSegment(sketch, "E4008", {"start": v(197.53, 20.97) * mm, "end": v(197.8, 20.5) * mm});
            skLineSegment(sketch, "E4009", {"start": v(197.8, 20.5) * mm, "end": v(198.05, 20.02) * mm});
            skLineSegment(sketch, "E4010", {"start": v(198.05, 20.02) * mm, "end": v(198.24, 19.5) * mm});
            skLineSegment(sketch, "E4011", {"start": v(198.24, 19.5) * mm, "end": v(198.37, 18.96) * mm});
            skLineSegment(sketch, "E4012", {"start": v(198.37, 18.96) * mm, "end": v(198.46, 18.4) * mm});
            skLineSegment(sketch, "E4013", {"start": v(198.46, 18.4) * mm, "end": v(198.49, 17.82) * mm});
            skLineSegment(sketch, "E4014", {"start": v(198.49, 17.82) * mm, "end": v(198.49, -17.89) * mm});
            skSolve(sketch);
        }
        {
            var Q0;
            Q0=makeQuery(id+"F0.imprint","IMPRINT",FACE,{"disambiguationData":[TD([[makeQuery(id+"F0.imprint","IMPRINT",EDGE,{"derivedFrom":sQuery(id+"F0.wireOp",EDGE,"E0")}),1.0]])]});
            var Q1;
            Q1=makeQuery(id+"F0.imprint","IMPRINT",FACE,{"disambiguationData":[TD([[makeQuery(id+"F0.imprint","IMPRINT",EDGE,{"derivedFrom":sQuery(id+"F0.wireOp",EDGE,"E136")}),1.0]])]});
            extrude(context, id + "F1", {"entities" : qUnion([Q0, Q1]), "oppositeDirection" : true, "depth" : 10 * mm, "offsetDistance" : 25 * mm});
        }
        {
            var Q0;
            Q0=qCreatedBy(makeId("Top.planeOp"),FACE);
            var sketch = newSketch(context, id + "F2", { "sketchPlane" : qUnion([Q0])});
            skLineSegment(sketch, "E4015.top", {"start": v(0, 0) * mm, "end": v(800, 0) * mm});
            skLineSegment(sketch, "E4015.right", {"start": v(800, 200) * mm, "end": v(800, 0) * mm});
            skLineSegment(sketch, "E4016", {"start": v(0, 124.86) * mm, "end": v(0, -124.86) * mm, "construction": true});
            skLineSegment(sketch, "E4017", {"start": v(-355.85, 0) * mm, "end": v(355.85, 0) * mm, "construction": true});
            skLineSegment(sketch, "E4018.bottom", {"start": v(-156.51, 23.46) * mm, "end": v(-151.51, 23.46) * mm});
            skLineSegment(sketch, "E4018.top", {"start": v(-156.51, 36.51) * mm, "end": v(-151.51, 36.51) * mm});
            skLineSegment(sketch, "E4018.left", {"start": v(-156.51, 23.46) * mm, "end": v(-156.51, 36.51) * mm});
            skLineSegment(sketch, "E4018.right", {"start": v(-151.51, 23.46) * mm, "end": v(-151.51, 36.51) * mm});
            skLineSegment(sketch, "E4019.bottom", {"start": v(-121.51, -36.51) * mm, "end": v(-116.51, -36.51) * mm});
            skLineSegment(sketch, "E4019.top", {"start": v(-121.51, -23.48) * mm, "end": v(-116.51, -23.48) * mm});
            skLineSegment(sketch, "E4019.left", {"start": v(-121.51, -36.51) * mm, "end": v(-121.51, -23.48) * mm});
            skLineSegment(sketch, "E4019.right", {"start": v(-116.51, -36.51) * mm, "end": v(-116.51, -23.48) * mm});
            skLineSegment(sketch, "E4020.bottom", {"start": v(106.51, -36.51) * mm, "end": v(111.51, -36.51) * mm});
            skLineSegment(sketch, "E4020.top", {"start": v(106.51, -23.48) * mm, "end": v(111.51, -23.48) * mm});
            skLineSegment(sketch, "E4020.left", {"start": v(106.51, -36.51) * mm, "end": v(106.51, -23.48) * mm});
            skLineSegment(sketch, "E4020.right", {"start": v(111.51, -36.51) * mm, "end": v(111.51, -23.48) * mm});
            skLineSegment(sketch, "E4021.bottom", {"start": v(-2.51, 23.46) * mm, "end": v(2.49, 23.46) * mm});
            skLineSegment(sketch, "E4021.top", {"start": v(-2.51, 36.51) * mm, "end": v(2.49, 36.51) * mm});
            skLineSegment(sketch, "E4021.left", {"start": v(-2.51, 23.46) * mm, "end": v(-2.51, 36.51) * mm});
            skLineSegment(sketch, "E4021.right", {"start": v(2.49, 23.46) * mm, "end": v(2.49, 36.51) * mm});
            skLineSegment(sketch, "E4022.bottom", {"start": v(151.51, 23.46) * mm, "end": v(156.51, 23.46) * mm});
            skLineSegment(sketch, "E4022.top", {"start": v(151.51, 36.51) * mm, "end": v(156.51, 36.51) * mm});
            skLineSegment(sketch, "E4022.left", {"start": v(151.51, 23.46) * mm, "end": v(151.51, 36.51) * mm});
            skLineSegment(sketch, "E4022.right", {"start": v(156.51, 23.46) * mm, "end": v(156.51, 36.51) * mm});
            skLineSegment(sketch, "E4023.bottom", {"start": v(-216.51, -2.53) * mm, "end": v(-198.49, -2.53) * mm});
            skLineSegment(sketch, "E4023.top", {"start": v(-216.51, 2.47) * mm, "end": v(-198.49, 2.47) * mm});
            skLineSegment(sketch, "E4023.left", {"start": v(-216.51, -2.53) * mm, "end": v(-216.51, 2.47) * mm});
            skLineSegment(sketch, "E4023.right", {"start": v(-198.49, -2.53) * mm, "end": v(-198.49, 2.47) * mm});
            skLineSegment(sketch, "E4024.bottom", {"start": v(198.49, -2.53) * mm, "end": v(216.51, -2.53) * mm});
            skLineSegment(sketch, "E4024.top", {"start": v(198.49, 2.47) * mm, "end": v(216.51, 2.47) * mm});
            skLineSegment(sketch, "E4024.left", {"start": v(198.49, -2.53) * mm, "end": v(198.49, 2.47) * mm});
            skLineSegment(sketch, "E4024.right", {"start": v(216.51, -2.53) * mm, "end": v(216.51, 2.47) * mm});
            skSolve(sketch);
        }
        {
            var Q0;
            Q0=qSketchRegion(id+"F2",true);
            extrude(context, id + "F3", {"entities" : qUnion([Q0]), "depth" : 12.5 * mm});
        }
    });
